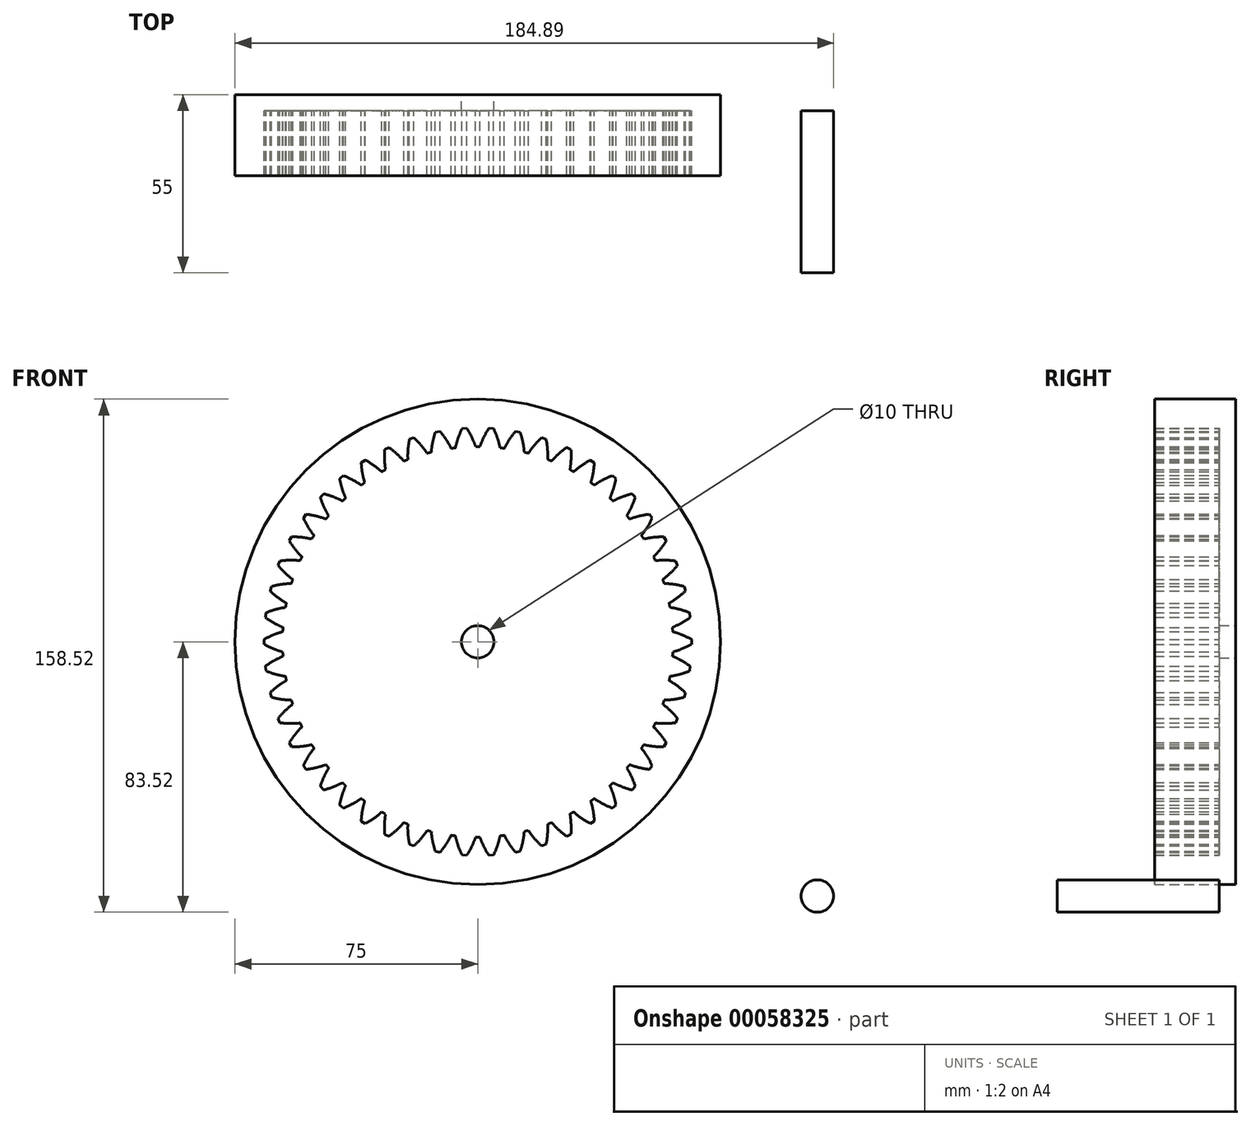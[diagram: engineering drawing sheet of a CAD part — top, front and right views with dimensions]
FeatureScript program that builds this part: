
annotation { "Feature Type Name" : "Feature", "Feature Type Description" : "" }
export const myFeature = defineFeature(function(context is Context, id is Id, definition is map)
    precondition{}
    {
        {
            var Q0;
            Q0=qCreatedBy(makeId("Front.planeOp"),FACE);
            var sketch = newSketch(context, id + "F0", { "sketchPlane" : qUnion([Q0])});
            skCircle(sketch, "E0", {"center": v(0, 0) * mm, "radius": 75 * mm});
            skSolve(sketch);
        }
        {
            var Q0;
            Q0 = qSketchRegion(id + "F0", true);
            extrude(context, id + "F1", {"entities" : qUnion([Q0]), "depth" : 20 * mm});
        }
        {
            var Q0;
            Q0=qCreatedBy(makeId("Front.planeOp"),FACE);
            var sketch = newSketch(context, id + "F2", { "sketchPlane" : qUnion([Q0])});
            skLineSegment(sketch, "E1", {"start": v(60.24, -3.11) * mm, "end": v(60.4, -3.07) * mm});
            skLineSegment(sketch, "E2", {"start": v(60.4, -3.07) * mm, "end": v(60.56, -3.03) * mm});
            skLineSegment(sketch, "E3", {"start": v(60.56, -3.03) * mm, "end": v(60.72, -2.98) * mm});
            skLineSegment(sketch, "E4", {"start": v(60.72, -2.98) * mm, "end": v(60.89, -2.94) * mm});
            skLineSegment(sketch, "E5", {"start": v(60.89, -2.94) * mm, "end": v(61.06, -2.88) * mm});
            skLineSegment(sketch, "E6", {"start": v(61.06, -2.88) * mm, "end": v(61.23, -2.83) * mm});
            skLineSegment(sketch, "E7", {"start": v(61.23, -2.83) * mm, "end": v(61.4, -2.77) * mm});
            skLineSegment(sketch, "E8", {"start": v(61.4, -2.77) * mm, "end": v(61.59, -2.71) * mm});
            skLineSegment(sketch, "E9", {"start": v(61.59, -2.71) * mm, "end": v(61.77, -2.65) * mm});
            skLineSegment(sketch, "E10", {"start": v(61.77, -2.65) * mm, "end": v(61.96, -2.59) * mm});
            skLineSegment(sketch, "E11", {"start": v(61.96, -2.59) * mm, "end": v(62.15, -2.52) * mm});
            skLineSegment(sketch, "E12", {"start": v(62.15, -2.52) * mm, "end": v(62.35, -2.44) * mm});
            skLineSegment(sketch, "E13", {"start": v(62.35, -2.44) * mm, "end": v(62.55, -2.37) * mm});
            skLineSegment(sketch, "E14", {"start": v(62.55, -2.37) * mm, "end": v(62.75, -2.3) * mm});
            skLineSegment(sketch, "E15", {"start": v(62.75, -2.3) * mm, "end": v(62.95, -2.2) * mm});
            skLineSegment(sketch, "E16", {"start": v(62.95, -2.2) * mm, "end": v(63.16, -2.12) * mm});
            skLineSegment(sketch, "E17", {"start": v(63.16, -2.12) * mm, "end": v(63.38, -2.03) * mm});
            skLineSegment(sketch, "E18", {"start": v(63.38, -2.03) * mm, "end": v(63.6, -1.94) * mm});
            skLineSegment(sketch, "E19", {"start": v(63.6, -1.94) * mm, "end": v(63.8, -1.85) * mm});
            skLineSegment(sketch, "E20", {"start": v(63.8, -1.85) * mm, "end": v(64.03, -1.75) * mm});
            skLineSegment(sketch, "E21", {"start": v(64.03, -1.75) * mm, "end": v(64.26, -1.64) * mm});
            skLineSegment(sketch, "E22", {"start": v(64.26, -1.64) * mm, "end": v(64.48, -1.54) * mm});
            skLineSegment(sketch, "E23", {"start": v(64.48, -1.54) * mm, "end": v(64.72, -1.42) * mm});
            skLineSegment(sketch, "E24", {"start": v(64.72, -1.42) * mm, "end": v(64.95, -1.3) * mm});
            skLineSegment(sketch, "E25", {"start": v(64.95, -1.3) * mm, "end": v(65.19, -1.19) * mm});
            skLineSegment(sketch, "E26", {"start": v(65.19, -1.19) * mm, "end": v(65.43, -1.07) * mm});
            skLineSegment(sketch, "E27", {"start": v(65.43, -1.07) * mm, "end": v(65.67, -0.94) * mm});
            skLineSegment(sketch, "E28", {"start": v(65.67, -0.94) * mm, "end": v(65.91, -0.8) * mm});
            skLineSegment(sketch, "E29", {"start": v(65.91, -0.8) * mm, "end": v(66.04, -0.74) * mm});
            skLineSegment(sketch, "E30", {"start": v(66.04, -0.74) * mm, "end": v(66.04, 0.74) * mm});
            skLineSegment(sketch, "E31", {"start": v(66.04, 0.74) * mm, "end": v(65.91, 0.8) * mm});
            skLineSegment(sketch, "E32", {"start": v(65.91, 0.8) * mm, "end": v(65.67, 0.94) * mm});
            skLineSegment(sketch, "E33", {"start": v(65.67, 0.94) * mm, "end": v(65.43, 1.07) * mm});
            skLineSegment(sketch, "E34", {"start": v(65.43, 1.07) * mm, "end": v(65.19, 1.19) * mm});
            skLineSegment(sketch, "E35", {"start": v(65.19, 1.19) * mm, "end": v(64.95, 1.3) * mm});
            skLineSegment(sketch, "E36", {"start": v(64.95, 1.3) * mm, "end": v(64.72, 1.42) * mm});
            skLineSegment(sketch, "E37", {"start": v(64.72, 1.42) * mm, "end": v(64.48, 1.54) * mm});
            skLineSegment(sketch, "E38", {"start": v(64.48, 1.54) * mm, "end": v(64.26, 1.64) * mm});
            skLineSegment(sketch, "E39", {"start": v(64.26, 1.64) * mm, "end": v(64.03, 1.75) * mm});
            skLineSegment(sketch, "E40", {"start": v(64.03, 1.75) * mm, "end": v(63.8, 1.85) * mm});
            skLineSegment(sketch, "E41", {"start": v(63.8, 1.85) * mm, "end": v(63.6, 1.94) * mm});
            skLineSegment(sketch, "E42", {"start": v(63.6, 1.94) * mm, "end": v(63.38, 2.03) * mm});
            skLineSegment(sketch, "E43", {"start": v(63.38, 2.03) * mm, "end": v(63.16, 2.12) * mm});
            skLineSegment(sketch, "E44", {"start": v(63.16, 2.12) * mm, "end": v(62.95, 2.2) * mm});
            skLineSegment(sketch, "E45", {"start": v(62.95, 2.2) * mm, "end": v(62.75, 2.3) * mm});
            skLineSegment(sketch, "E46", {"start": v(62.75, 2.3) * mm, "end": v(62.55, 2.37) * mm});
            skLineSegment(sketch, "E47", {"start": v(62.55, 2.37) * mm, "end": v(62.35, 2.44) * mm});
            skLineSegment(sketch, "E48", {"start": v(62.35, 2.44) * mm, "end": v(62.15, 2.52) * mm});
            skLineSegment(sketch, "E49", {"start": v(62.15, 2.52) * mm, "end": v(61.96, 2.59) * mm});
            skLineSegment(sketch, "E50", {"start": v(61.96, 2.59) * mm, "end": v(61.77, 2.65) * mm});
            skLineSegment(sketch, "E51", {"start": v(61.77, 2.65) * mm, "end": v(61.59, 2.71) * mm});
            skLineSegment(sketch, "E52", {"start": v(61.59, 2.71) * mm, "end": v(61.4, 2.77) * mm});
            skLineSegment(sketch, "E53", {"start": v(61.4, 2.77) * mm, "end": v(61.23, 2.83) * mm});
            skLineSegment(sketch, "E54", {"start": v(61.23, 2.83) * mm, "end": v(61.06, 2.88) * mm});
            skLineSegment(sketch, "E55", {"start": v(61.06, 2.88) * mm, "end": v(60.89, 2.94) * mm});
            skLineSegment(sketch, "E56", {"start": v(60.89, 2.94) * mm, "end": v(60.72, 2.98) * mm});
            skLineSegment(sketch, "E57", {"start": v(60.72, 2.98) * mm, "end": v(60.56, 3.03) * mm});
            skLineSegment(sketch, "E58", {"start": v(60.56, 3.03) * mm, "end": v(60.4, 3.07) * mm});
            skLineSegment(sketch, "E59", {"start": v(60.4, 3.07) * mm, "end": v(60.24, 3.11) * mm});
            skArc(sketch, "E60", {"start": v(60.24, 3.11) * mm, "mid": v(60.2, 3.79) * mm, "end": v(60.16, 4.46) * mm});
            skLineSegment(sketch, "E61", {"start": v(60.16, 4.46) * mm, "end": v(60.3, 4.52) * mm});
            skLineSegment(sketch, "E62", {"start": v(60.3, 4.52) * mm, "end": v(60.46, 4.58) * mm});
            skLineSegment(sketch, "E63", {"start": v(60.46, 4.58) * mm, "end": v(60.61, 4.65) * mm});
            skLineSegment(sketch, "E64", {"start": v(60.61, 4.65) * mm, "end": v(60.77, 4.72) * mm});
            skLineSegment(sketch, "E65", {"start": v(60.77, 4.72) * mm, "end": v(60.94, 4.8) * mm});
            skLineSegment(sketch, "E66", {"start": v(60.94, 4.8) * mm, "end": v(61.1, 4.87) * mm});
            skLineSegment(sketch, "E67", {"start": v(61.1, 4.87) * mm, "end": v(61.27, 4.94) * mm});
            skLineSegment(sketch, "E68", {"start": v(61.27, 4.94) * mm, "end": v(61.44, 5.03) * mm});
            skLineSegment(sketch, "E69", {"start": v(61.44, 5.03) * mm, "end": v(61.62, 5.11) * mm});
            skLineSegment(sketch, "E70", {"start": v(61.62, 5.11) * mm, "end": v(61.8, 5.2) * mm});
            skLineSegment(sketch, "E71", {"start": v(61.8, 5.2) * mm, "end": v(61.98, 5.3) * mm});
            skLineSegment(sketch, "E72", {"start": v(61.98, 5.3) * mm, "end": v(62.16, 5.39) * mm});
            skLineSegment(sketch, "E73", {"start": v(62.16, 5.39) * mm, "end": v(62.35, 5.49) * mm});
            skLineSegment(sketch, "E74", {"start": v(62.35, 5.49) * mm, "end": v(62.54, 5.6) * mm});
            skLineSegment(sketch, "E75", {"start": v(62.54, 5.6) * mm, "end": v(62.73, 5.7) * mm});
            skLineSegment(sketch, "E76", {"start": v(62.73, 5.7) * mm, "end": v(62.93, 5.8) * mm});
            skLineSegment(sketch, "E77", {"start": v(62.93, 5.8) * mm, "end": v(63.13, 5.92) * mm});
            skLineSegment(sketch, "E78", {"start": v(63.13, 5.92) * mm, "end": v(63.33, 6.04) * mm});
            skLineSegment(sketch, "E79", {"start": v(63.33, 6.04) * mm, "end": v(63.54, 6.17) * mm});
            skLineSegment(sketch, "E80", {"start": v(63.54, 6.17) * mm, "end": v(63.75, 6.3) * mm});
            skLineSegment(sketch, "E81", {"start": v(63.75, 6.3) * mm, "end": v(63.96, 6.42) * mm});
            skLineSegment(sketch, "E82", {"start": v(63.96, 6.42) * mm, "end": v(64.17, 6.56) * mm});
            skLineSegment(sketch, "E83", {"start": v(64.17, 6.56) * mm, "end": v(64.38, 6.7) * mm});
            skLineSegment(sketch, "E84", {"start": v(64.38, 6.7) * mm, "end": v(64.6, 6.84) * mm});
            skLineSegment(sketch, "E85", {"start": v(64.6, 6.84) * mm, "end": v(64.82, 7) * mm});
            skLineSegment(sketch, "E86", {"start": v(64.82, 7) * mm, "end": v(65.04, 7.14) * mm});
            skLineSegment(sketch, "E87", {"start": v(65.04, 7.14) * mm, "end": v(65.27, 7.3) * mm});
            skLineSegment(sketch, "E88", {"start": v(65.27, 7.3) * mm, "end": v(65.5, 7.46) * mm});
            skLineSegment(sketch, "E89", {"start": v(65.5, 7.46) * mm, "end": v(65.6, 7.54) * mm});
            skLineSegment(sketch, "E90", {"start": v(65.6, 7.54) * mm, "end": v(65.42, 9.01) * mm});
            skLineSegment(sketch, "E91", {"start": v(65.42, 9.01) * mm, "end": v(65.3, 9.06) * mm});
            skLineSegment(sketch, "E92", {"start": v(65.3, 9.06) * mm, "end": v(65.03, 9.16) * mm});
            skLineSegment(sketch, "E93", {"start": v(65.03, 9.16) * mm, "end": v(64.78, 9.26) * mm});
            skLineSegment(sketch, "E94", {"start": v(64.78, 9.26) * mm, "end": v(64.52, 9.35) * mm});
            skLineSegment(sketch, "E95", {"start": v(64.52, 9.35) * mm, "end": v(64.27, 9.44) * mm});
            skLineSegment(sketch, "E96", {"start": v(64.27, 9.44) * mm, "end": v(64.03, 9.52) * mm});
            skLineSegment(sketch, "E97", {"start": v(64.03, 9.52) * mm, "end": v(63.78, 9.6) * mm});
            skLineSegment(sketch, "E98", {"start": v(63.78, 9.6) * mm, "end": v(63.54, 9.68) * mm});
            skLineSegment(sketch, "E99", {"start": v(63.54, 9.68) * mm, "end": v(63.3, 9.76) * mm});
            skLineSegment(sketch, "E100", {"start": v(63.3, 9.76) * mm, "end": v(63.07, 9.83) * mm});
            skLineSegment(sketch, "E101", {"start": v(63.07, 9.83) * mm, "end": v(62.85, 9.9) * mm});
            skLineSegment(sketch, "E102", {"start": v(62.85, 9.9) * mm, "end": v(62.62, 9.96) * mm});
            skLineSegment(sketch, "E103", {"start": v(62.62, 9.96) * mm, "end": v(62.4, 10.02) * mm});
            skLineSegment(sketch, "E104", {"start": v(62.4, 10.02) * mm, "end": v(62.18, 10.08) * mm});
            skLineSegment(sketch, "E105", {"start": v(62.18, 10.08) * mm, "end": v(61.97, 10.14) * mm});
            skLineSegment(sketch, "E106", {"start": v(61.97, 10.14) * mm, "end": v(61.76, 10.19) * mm});
            skLineSegment(sketch, "E107", {"start": v(61.76, 10.19) * mm, "end": v(61.55, 10.24) * mm});
            skLineSegment(sketch, "E108", {"start": v(61.55, 10.24) * mm, "end": v(61.35, 10.29) * mm});
            skLineSegment(sketch, "E109", {"start": v(61.35, 10.29) * mm, "end": v(61.15, 10.33) * mm});
            skLineSegment(sketch, "E110", {"start": v(61.15, 10.33) * mm, "end": v(60.95, 10.37) * mm});
            skLineSegment(sketch, "E111", {"start": v(60.95, 10.37) * mm, "end": v(60.76, 10.41) * mm});
            skLineSegment(sketch, "E112", {"start": v(60.76, 10.41) * mm, "end": v(60.57, 10.45) * mm});
            skLineSegment(sketch, "E113", {"start": v(60.57, 10.45) * mm, "end": v(60.4, 10.48) * mm});
            skLineSegment(sketch, "E114", {"start": v(60.4, 10.48) * mm, "end": v(60.21, 10.51) * mm});
            skLineSegment(sketch, "E115", {"start": v(60.21, 10.51) * mm, "end": v(60.04, 10.54) * mm});
            skLineSegment(sketch, "E116", {"start": v(60.04, 10.54) * mm, "end": v(59.87, 10.57) * mm});
            skLineSegment(sketch, "E117", {"start": v(59.87, 10.57) * mm, "end": v(59.7, 10.6) * mm});
            skLineSegment(sketch, "E118", {"start": v(59.7, 10.6) * mm, "end": v(59.54, 10.62) * mm});
            skLineSegment(sketch, "E119", {"start": v(59.54, 10.62) * mm, "end": v(59.38, 10.64) * mm});
            skArc(sketch, "E120", {"start": v(59.38, 10.64) * mm, "mid": v(59.25, 11.3) * mm, "end": v(59.13, 11.97) * mm});
            skLineSegment(sketch, "E121", {"start": v(59.13, 11.97) * mm, "end": v(59.26, 12.04) * mm});
            skLineSegment(sketch, "E122", {"start": v(59.26, 12.04) * mm, "end": v(59.4, 12.13) * mm});
            skLineSegment(sketch, "E123", {"start": v(59.4, 12.13) * mm, "end": v(59.55, 12.21) * mm});
            skLineSegment(sketch, "E124", {"start": v(59.55, 12.21) * mm, "end": v(59.7, 12.3) * mm});
            skLineSegment(sketch, "E125", {"start": v(59.7, 12.3) * mm, "end": v(59.85, 12.4) * mm});
            skLineSegment(sketch, "E126", {"start": v(59.85, 12.4) * mm, "end": v(60, 12.49) * mm});
            skLineSegment(sketch, "E127", {"start": v(60, 12.49) * mm, "end": v(60.17, 12.58) * mm});
            skLineSegment(sketch, "E128", {"start": v(60.17, 12.58) * mm, "end": v(60.33, 12.69) * mm});
            skLineSegment(sketch, "E129", {"start": v(60.33, 12.69) * mm, "end": v(60.5, 12.8) * mm});
            skLineSegment(sketch, "E130", {"start": v(60.5, 12.8) * mm, "end": v(60.66, 12.9) * mm});
            skLineSegment(sketch, "E131", {"start": v(60.66, 12.9) * mm, "end": v(60.83, 13.02) * mm});
            skLineSegment(sketch, "E132", {"start": v(60.83, 13.02) * mm, "end": v(61, 13.14) * mm});
            skLineSegment(sketch, "E133", {"start": v(61, 13.14) * mm, "end": v(61.17, 13.26) * mm});
            skLineSegment(sketch, "E134", {"start": v(61.17, 13.26) * mm, "end": v(61.35, 13.39) * mm});
            skLineSegment(sketch, "E135", {"start": v(61.35, 13.39) * mm, "end": v(61.53, 13.52) * mm});
            skLineSegment(sketch, "E136", {"start": v(61.53, 13.52) * mm, "end": v(61.7, 13.65) * mm});
            skLineSegment(sketch, "E137", {"start": v(61.7, 13.65) * mm, "end": v(61.9, 13.8) * mm});
            skLineSegment(sketch, "E138", {"start": v(61.9, 13.8) * mm, "end": v(62.08, 13.93) * mm});
            skLineSegment(sketch, "E139", {"start": v(62.08, 13.93) * mm, "end": v(62.26, 14.08) * mm});
            skLineSegment(sketch, "E140", {"start": v(62.26, 14.08) * mm, "end": v(62.45, 14.23) * mm});
            skLineSegment(sketch, "E141", {"start": v(62.45, 14.23) * mm, "end": v(62.65, 14.39) * mm});
            skLineSegment(sketch, "E142", {"start": v(62.65, 14.39) * mm, "end": v(62.84, 14.55) * mm});
            skLineSegment(sketch, "E143", {"start": v(62.84, 14.55) * mm, "end": v(63.04, 14.71) * mm});
            skLineSegment(sketch, "E144", {"start": v(63.04, 14.71) * mm, "end": v(63.23, 14.88) * mm});
            skLineSegment(sketch, "E145", {"start": v(63.23, 14.88) * mm, "end": v(63.43, 15.06) * mm});
            skLineSegment(sketch, "E146", {"start": v(63.43, 15.06) * mm, "end": v(63.64, 15.24) * mm});
            skLineSegment(sketch, "E147", {"start": v(63.64, 15.24) * mm, "end": v(63.84, 15.42) * mm});
            skLineSegment(sketch, "E148", {"start": v(63.84, 15.42) * mm, "end": v(64.04, 15.61) * mm});
            skLineSegment(sketch, "E149", {"start": v(64.04, 15.61) * mm, "end": v(64.15, 15.7) * mm});
            skLineSegment(sketch, "E150", {"start": v(64.15, 15.7) * mm, "end": v(63.78, 17.14) * mm});
            skLineSegment(sketch, "E151", {"start": v(63.78, 17.14) * mm, "end": v(63.64, 17.17) * mm});
            skLineSegment(sketch, "E152", {"start": v(63.64, 17.17) * mm, "end": v(63.37, 17.24) * mm});
            skLineSegment(sketch, "E153", {"start": v(63.37, 17.24) * mm, "end": v(63.1, 17.3) * mm});
            skLineSegment(sketch, "E154", {"start": v(63.1, 17.3) * mm, "end": v(62.84, 17.36) * mm});
            skLineSegment(sketch, "E155", {"start": v(62.84, 17.36) * mm, "end": v(62.58, 17.42) * mm});
            skLineSegment(sketch, "E156", {"start": v(62.58, 17.42) * mm, "end": v(62.33, 17.47) * mm});
            skLineSegment(sketch, "E157", {"start": v(62.33, 17.47) * mm, "end": v(62.08, 17.52) * mm});
            skLineSegment(sketch, "E158", {"start": v(62.08, 17.52) * mm, "end": v(61.83, 17.57) * mm});
            skLineSegment(sketch, "E159", {"start": v(61.83, 17.57) * mm, "end": v(61.59, 17.62) * mm});
            skLineSegment(sketch, "E160", {"start": v(61.59, 17.62) * mm, "end": v(61.35, 17.66) * mm});
            skLineSegment(sketch, "E161", {"start": v(61.35, 17.66) * mm, "end": v(61.1, 17.7) * mm});
            skLineSegment(sketch, "E162", {"start": v(61.1, 17.7) * mm, "end": v(60.88, 17.73) * mm});
            skLineSegment(sketch, "E163", {"start": v(60.88, 17.73) * mm, "end": v(60.65, 17.76) * mm});
            skLineSegment(sketch, "E164", {"start": v(60.65, 17.76) * mm, "end": v(60.43, 17.8) * mm});
            skLineSegment(sketch, "E165", {"start": v(60.43, 17.8) * mm, "end": v(60.2, 17.82) * mm});
            skLineSegment(sketch, "E166", {"start": v(60.2, 17.82) * mm, "end": v(60, 17.85) * mm});
            skLineSegment(sketch, "E167", {"start": v(60, 17.85) * mm, "end": v(59.78, 17.87) * mm});
            skLineSegment(sketch, "E168", {"start": v(59.78, 17.87) * mm, "end": v(59.57, 17.9) * mm});
            skLineSegment(sketch, "E169", {"start": v(59.57, 17.9) * mm, "end": v(59.37, 17.91) * mm});
            skLineSegment(sketch, "E170", {"start": v(59.37, 17.91) * mm, "end": v(59.17, 17.93) * mm});
            skLineSegment(sketch, "E171", {"start": v(59.17, 17.93) * mm, "end": v(58.98, 17.94) * mm});
            skLineSegment(sketch, "E172", {"start": v(58.98, 17.94) * mm, "end": v(58.79, 17.96) * mm});
            skLineSegment(sketch, "E173", {"start": v(58.79, 17.96) * mm, "end": v(58.6, 17.97) * mm});
            skLineSegment(sketch, "E174", {"start": v(58.6, 17.97) * mm, "end": v(58.42, 17.98) * mm});
            skLineSegment(sketch, "E175", {"start": v(58.42, 17.98) * mm, "end": v(58.24, 17.98) * mm});
            skLineSegment(sketch, "E176", {"start": v(58.24, 17.98) * mm, "end": v(58.07, 18) * mm});
            skLineSegment(sketch, "E177", {"start": v(58.07, 18) * mm, "end": v(57.9, 18) * mm});
            skLineSegment(sketch, "E178", {"start": v(57.9, 18) * mm, "end": v(57.74, 18) * mm});
            skLineSegment(sketch, "E179", {"start": v(57.74, 18) * mm, "end": v(57.58, 18) * mm});
            skArc(sketch, "E180", {"start": v(57.58, 18) * mm, "mid": v(57.37, 18.64) * mm, "end": v(57.16, 19.28) * mm});
            skLineSegment(sketch, "E181", {"start": v(57.16, 19.28) * mm, "end": v(57.29, 19.38) * mm});
            skLineSegment(sketch, "E182", {"start": v(57.29, 19.38) * mm, "end": v(57.42, 19.48) * mm});
            skLineSegment(sketch, "E183", {"start": v(57.42, 19.48) * mm, "end": v(57.55, 19.58) * mm});
            skLineSegment(sketch, "E184", {"start": v(57.55, 19.58) * mm, "end": v(57.7, 19.68) * mm});
            skLineSegment(sketch, "E185", {"start": v(57.7, 19.68) * mm, "end": v(57.83, 19.8) * mm});
            skLineSegment(sketch, "E186", {"start": v(57.83, 19.8) * mm, "end": v(57.97, 19.9) * mm});
            skLineSegment(sketch, "E187", {"start": v(57.97, 19.9) * mm, "end": v(58.12, 20.03) * mm});
            skLineSegment(sketch, "E188", {"start": v(58.12, 20.03) * mm, "end": v(58.26, 20.15) * mm});
            skLineSegment(sketch, "E189", {"start": v(58.26, 20.15) * mm, "end": v(58.41, 20.27) * mm});
            skLineSegment(sketch, "E190", {"start": v(58.41, 20.27) * mm, "end": v(58.56, 20.4) * mm});
            skLineSegment(sketch, "E191", {"start": v(58.56, 20.4) * mm, "end": v(58.71, 20.54) * mm});
            skLineSegment(sketch, "E192", {"start": v(58.71, 20.54) * mm, "end": v(58.87, 20.68) * mm});
            skLineSegment(sketch, "E193", {"start": v(58.87, 20.68) * mm, "end": v(59.03, 20.82) * mm});
            skLineSegment(sketch, "E194", {"start": v(59.03, 20.82) * mm, "end": v(59.19, 20.97) * mm});
            skLineSegment(sketch, "E195", {"start": v(59.19, 20.97) * mm, "end": v(59.35, 21.12) * mm});
            skLineSegment(sketch, "E196", {"start": v(59.35, 21.12) * mm, "end": v(59.5, 21.28) * mm});
            skLineSegment(sketch, "E197", {"start": v(59.5, 21.28) * mm, "end": v(59.67, 21.44) * mm});
            skLineSegment(sketch, "E198", {"start": v(59.67, 21.44) * mm, "end": v(59.84, 21.6) * mm});
            skLineSegment(sketch, "E199", {"start": v(59.84, 21.6) * mm, "end": v(60, 21.77) * mm});
            skLineSegment(sketch, "E200", {"start": v(60, 21.77) * mm, "end": v(60.18, 21.95) * mm});
            skLineSegment(sketch, "E201", {"start": v(60.18, 21.95) * mm, "end": v(60.35, 22.13) * mm});
            skLineSegment(sketch, "E202", {"start": v(60.35, 22.13) * mm, "end": v(60.52, 22.31) * mm});
            skLineSegment(sketch, "E203", {"start": v(60.52, 22.31) * mm, "end": v(60.7, 22.5) * mm});
            skLineSegment(sketch, "E204", {"start": v(60.7, 22.5) * mm, "end": v(60.87, 22.7) * mm});
            skLineSegment(sketch, "E205", {"start": v(60.87, 22.7) * mm, "end": v(61.05, 22.9) * mm});
            skLineSegment(sketch, "E206", {"start": v(61.05, 22.9) * mm, "end": v(61.22, 23.1) * mm});
            skLineSegment(sketch, "E207", {"start": v(61.22, 23.1) * mm, "end": v(61.4, 23.3) * mm});
            skLineSegment(sketch, "E208", {"start": v(61.4, 23.3) * mm, "end": v(61.58, 23.51) * mm});
            skLineSegment(sketch, "E209", {"start": v(61.58, 23.51) * mm, "end": v(61.67, 23.62) * mm});
            skLineSegment(sketch, "E210", {"start": v(61.67, 23.62) * mm, "end": v(61.13, 25) * mm});
            skLineSegment(sketch, "E211", {"start": v(61.13, 25) * mm, "end": v(60.99, 25.01) * mm});
            skLineSegment(sketch, "E212", {"start": v(60.99, 25.01) * mm, "end": v(60.71, 25.05) * mm});
            skLineSegment(sketch, "E213", {"start": v(60.71, 25.05) * mm, "end": v(60.44, 25.08) * mm});
            skLineSegment(sketch, "E214", {"start": v(60.44, 25.08) * mm, "end": v(60.17, 25.1) * mm});
            skLineSegment(sketch, "E215", {"start": v(60.17, 25.1) * mm, "end": v(59.9, 25.13) * mm});
            skLineSegment(sketch, "E216", {"start": v(59.9, 25.13) * mm, "end": v(59.65, 25.15) * mm});
            skLineSegment(sketch, "E217", {"start": v(59.65, 25.15) * mm, "end": v(59.4, 25.17) * mm});
            skLineSegment(sketch, "E218", {"start": v(59.4, 25.17) * mm, "end": v(59.14, 25.18) * mm});
            skLineSegment(sketch, "E219", {"start": v(59.14, 25.18) * mm, "end": v(58.9, 25.2) * mm});
            skLineSegment(sketch, "E220", {"start": v(58.9, 25.2) * mm, "end": v(58.65, 25.2) * mm});
            skLineSegment(sketch, "E221", {"start": v(58.65, 25.2) * mm, "end": v(58.41, 25.22) * mm});
            skLineSegment(sketch, "E222", {"start": v(58.41, 25.22) * mm, "end": v(58.18, 25.22) * mm});
            skLineSegment(sketch, "E223", {"start": v(58.18, 25.22) * mm, "end": v(57.95, 25.23) * mm});
            skLineSegment(sketch, "E224", {"start": v(57.95, 25.23) * mm, "end": v(57.72, 25.23) * mm});
            skLineSegment(sketch, "E225", {"start": v(57.72, 25.23) * mm, "end": v(57.5, 25.23) * mm});
            skLineSegment(sketch, "E226", {"start": v(57.5, 25.23) * mm, "end": v(57.28, 25.23) * mm});
            skLineSegment(sketch, "E227", {"start": v(57.28, 25.23) * mm, "end": v(57.07, 25.22) * mm});
            skLineSegment(sketch, "E228", {"start": v(57.07, 25.22) * mm, "end": v(56.86, 25.22) * mm});
            skLineSegment(sketch, "E229", {"start": v(56.86, 25.22) * mm, "end": v(56.66, 25.21) * mm});
            skLineSegment(sketch, "E230", {"start": v(56.66, 25.21) * mm, "end": v(56.46, 25.2) * mm});
            skLineSegment(sketch, "E231", {"start": v(56.46, 25.2) * mm, "end": v(56.26, 25.2) * mm});
            skLineSegment(sketch, "E232", {"start": v(56.26, 25.2) * mm, "end": v(56.07, 25.18) * mm});
            skLineSegment(sketch, "E233", {"start": v(56.07, 25.18) * mm, "end": v(55.89, 25.17) * mm});
            skLineSegment(sketch, "E234", {"start": v(55.89, 25.17) * mm, "end": v(55.7, 25.16) * mm});
            skLineSegment(sketch, "E235", {"start": v(55.7, 25.16) * mm, "end": v(55.53, 25.14) * mm});
            skLineSegment(sketch, "E236", {"start": v(55.53, 25.14) * mm, "end": v(55.36, 25.13) * mm});
            skLineSegment(sketch, "E237", {"start": v(55.36, 25.13) * mm, "end": v(55.19, 25.1) * mm});
            skLineSegment(sketch, "E238", {"start": v(55.19, 25.1) * mm, "end": v(55.03, 25.1) * mm});
            skLineSegment(sketch, "E239", {"start": v(55.03, 25.1) * mm, "end": v(54.87, 25.07) * mm});
            skArc(sketch, "E240", {"start": v(54.87, 25.07) * mm, "mid": v(54.58, 25.68) * mm, "end": v(54.3, 26.3) * mm});
            skLineSegment(sketch, "E241", {"start": v(54.3, 26.3) * mm, "end": v(54.4, 26.4) * mm});
            skLineSegment(sketch, "E242", {"start": v(54.4, 26.4) * mm, "end": v(54.53, 26.52) * mm});
            skLineSegment(sketch, "E243", {"start": v(54.53, 26.52) * mm, "end": v(54.65, 26.64) * mm});
            skLineSegment(sketch, "E244", {"start": v(54.65, 26.64) * mm, "end": v(54.77, 26.76) * mm});
            skLineSegment(sketch, "E245", {"start": v(54.77, 26.76) * mm, "end": v(54.9, 26.89) * mm});
            skLineSegment(sketch, "E246", {"start": v(54.9, 26.89) * mm, "end": v(55.02, 27.02) * mm});
            skLineSegment(sketch, "E247", {"start": v(55.02, 27.02) * mm, "end": v(55.15, 27.15) * mm});
            skLineSegment(sketch, "E248", {"start": v(55.15, 27.15) * mm, "end": v(55.28, 27.3) * mm});
            skLineSegment(sketch, "E249", {"start": v(55.28, 27.3) * mm, "end": v(55.4, 27.44) * mm});
            skLineSegment(sketch, "E250", {"start": v(55.4, 27.44) * mm, "end": v(55.54, 27.58) * mm});
            skLineSegment(sketch, "E251", {"start": v(55.54, 27.58) * mm, "end": v(55.68, 27.74) * mm});
            skLineSegment(sketch, "E252", {"start": v(55.68, 27.74) * mm, "end": v(55.81, 27.9) * mm});
            skLineSegment(sketch, "E253", {"start": v(55.81, 27.9) * mm, "end": v(55.95, 28.06) * mm});
            skLineSegment(sketch, "E254", {"start": v(55.95, 28.06) * mm, "end": v(56.1, 28.22) * mm});
            skLineSegment(sketch, "E255", {"start": v(56.1, 28.22) * mm, "end": v(56.23, 28.4) * mm});
            skLineSegment(sketch, "E256", {"start": v(56.23, 28.4) * mm, "end": v(56.37, 28.57) * mm});
            skLineSegment(sketch, "E257", {"start": v(56.37, 28.57) * mm, "end": v(56.52, 28.75) * mm});
            skLineSegment(sketch, "E258", {"start": v(56.52, 28.75) * mm, "end": v(56.66, 28.93) * mm});
            skLineSegment(sketch, "E259", {"start": v(56.66, 28.93) * mm, "end": v(56.8, 29.12) * mm});
            skLineSegment(sketch, "E260", {"start": v(56.8, 29.12) * mm, "end": v(56.95, 29.32) * mm});
            skLineSegment(sketch, "E261", {"start": v(56.95, 29.32) * mm, "end": v(57.1, 29.52) * mm});
            skLineSegment(sketch, "E262", {"start": v(57.1, 29.52) * mm, "end": v(57.25, 29.72) * mm});
            skLineSegment(sketch, "E263", {"start": v(57.25, 29.72) * mm, "end": v(57.4, 29.93) * mm});
            skLineSegment(sketch, "E264", {"start": v(57.4, 29.93) * mm, "end": v(57.55, 30.14) * mm});
            skLineSegment(sketch, "E265", {"start": v(57.55, 30.14) * mm, "end": v(57.7, 30.36) * mm});
            skLineSegment(sketch, "E266", {"start": v(57.7, 30.36) * mm, "end": v(57.85, 30.58) * mm});
            skLineSegment(sketch, "E267", {"start": v(57.85, 30.58) * mm, "end": v(58, 30.81) * mm});
            skLineSegment(sketch, "E268", {"start": v(58, 30.81) * mm, "end": v(58.15, 31.05) * mm});
            skLineSegment(sketch, "E269", {"start": v(58.15, 31.05) * mm, "end": v(58.22, 31.16) * mm});
            skLineSegment(sketch, "E270", {"start": v(58.22, 31.16) * mm, "end": v(57.51, 32.46) * mm});
            skLineSegment(sketch, "E271", {"start": v(57.51, 32.46) * mm, "end": v(57.37, 32.46) * mm});
            skLineSegment(sketch, "E272", {"start": v(57.37, 32.46) * mm, "end": v(57.1, 32.46) * mm});
            skLineSegment(sketch, "E273", {"start": v(57.1, 32.46) * mm, "end": v(56.82, 32.45) * mm});
            skLineSegment(sketch, "E274", {"start": v(56.82, 32.45) * mm, "end": v(56.55, 32.45) * mm});
            skLineSegment(sketch, "E275", {"start": v(56.55, 32.45) * mm, "end": v(56.28, 32.44) * mm});
            skLineSegment(sketch, "E276", {"start": v(56.28, 32.44) * mm, "end": v(56.02, 32.42) * mm});
            skLineSegment(sketch, "E277", {"start": v(56.02, 32.42) * mm, "end": v(55.77, 32.41) * mm});
            skLineSegment(sketch, "E278", {"start": v(55.77, 32.41) * mm, "end": v(55.52, 32.4) * mm});
            skLineSegment(sketch, "E279", {"start": v(55.52, 32.4) * mm, "end": v(55.27, 32.38) * mm});
            skLineSegment(sketch, "E280", {"start": v(55.27, 32.38) * mm, "end": v(55.03, 32.36) * mm});
            skLineSegment(sketch, "E281", {"start": v(55.03, 32.36) * mm, "end": v(54.79, 32.34) * mm});
            skLineSegment(sketch, "E282", {"start": v(54.79, 32.34) * mm, "end": v(54.56, 32.31) * mm});
            skLineSegment(sketch, "E283", {"start": v(54.56, 32.31) * mm, "end": v(54.33, 32.29) * mm});
            skLineSegment(sketch, "E284", {"start": v(54.33, 32.29) * mm, "end": v(54.1, 32.26) * mm});
            skLineSegment(sketch, "E285", {"start": v(54.1, 32.26) * mm, "end": v(53.88, 32.24) * mm});
            skLineSegment(sketch, "E286", {"start": v(53.88, 32.24) * mm, "end": v(53.67, 32.2) * mm});
            skLineSegment(sketch, "E287", {"start": v(53.67, 32.2) * mm, "end": v(53.46, 32.18) * mm});
            skLineSegment(sketch, "E288", {"start": v(53.46, 32.18) * mm, "end": v(53.25, 32.15) * mm});
            skLineSegment(sketch, "E289", {"start": v(53.25, 32.15) * mm, "end": v(53.05, 32.12) * mm});
            skLineSegment(sketch, "E290", {"start": v(53.05, 32.12) * mm, "end": v(52.85, 32.08) * mm});
            skLineSegment(sketch, "E291", {"start": v(52.85, 32.08) * mm, "end": v(52.66, 32.05) * mm});
            skLineSegment(sketch, "E292", {"start": v(52.66, 32.05) * mm, "end": v(52.47, 32.01) * mm});
            skLineSegment(sketch, "E293", {"start": v(52.47, 32.01) * mm, "end": v(52.3, 31.98) * mm});
            skLineSegment(sketch, "E294", {"start": v(52.3, 31.98) * mm, "end": v(52.11, 31.94) * mm});
            skLineSegment(sketch, "E295", {"start": v(52.11, 31.94) * mm, "end": v(51.94, 31.9) * mm});
            skLineSegment(sketch, "E296", {"start": v(51.94, 31.9) * mm, "end": v(51.77, 31.87) * mm});
            skLineSegment(sketch, "E297", {"start": v(51.77, 31.87) * mm, "end": v(51.6, 31.83) * mm});
            skLineSegment(sketch, "E298", {"start": v(51.6, 31.83) * mm, "end": v(51.45, 31.79) * mm});
            skLineSegment(sketch, "E299", {"start": v(51.45, 31.79) * mm, "end": v(51.3, 31.75) * mm});
            skArc(sketch, "E300", {"start": v(51.3, 31.75) * mm, "mid": v(50.93, 32.32) * mm, "end": v(50.57, 32.9) * mm});
            skLineSegment(sketch, "E301", {"start": v(50.57, 32.9) * mm, "end": v(50.67, 33.02) * mm});
            skLineSegment(sketch, "E302", {"start": v(50.67, 33.02) * mm, "end": v(50.77, 33.14) * mm});
            skLineSegment(sketch, "E303", {"start": v(50.77, 33.14) * mm, "end": v(50.88, 33.28) * mm});
            skLineSegment(sketch, "E304", {"start": v(50.88, 33.28) * mm, "end": v(50.98, 33.41) * mm});
            skLineSegment(sketch, "E305", {"start": v(50.98, 33.41) * mm, "end": v(51.09, 33.55) * mm});
            skLineSegment(sketch, "E306", {"start": v(51.09, 33.55) * mm, "end": v(51.2, 33.7) * mm});
            skLineSegment(sketch, "E307", {"start": v(51.2, 33.7) * mm, "end": v(51.3, 33.85) * mm});
            skLineSegment(sketch, "E308", {"start": v(51.3, 33.85) * mm, "end": v(51.42, 34) * mm});
            skLineSegment(sketch, "E309", {"start": v(51.42, 34) * mm, "end": v(51.53, 34.16) * mm});
            skLineSegment(sketch, "E310", {"start": v(51.53, 34.16) * mm, "end": v(51.65, 34.33) * mm});
            skLineSegment(sketch, "E311", {"start": v(51.65, 34.33) * mm, "end": v(51.76, 34.5) * mm});
            skLineSegment(sketch, "E312", {"start": v(51.76, 34.5) * mm, "end": v(51.88, 34.67) * mm});
            skLineSegment(sketch, "E313", {"start": v(51.88, 34.67) * mm, "end": v(52, 34.85) * mm});
            skLineSegment(sketch, "E314", {"start": v(52, 34.85) * mm, "end": v(52.11, 35.03) * mm});
            skLineSegment(sketch, "E315", {"start": v(52.11, 35.03) * mm, "end": v(52.23, 35.22) * mm});
            skLineSegment(sketch, "E316", {"start": v(52.23, 35.22) * mm, "end": v(52.35, 35.4) * mm});
            skLineSegment(sketch, "E317", {"start": v(52.35, 35.4) * mm, "end": v(52.47, 35.6) * mm});
            skLineSegment(sketch, "E318", {"start": v(52.47, 35.6) * mm, "end": v(52.59, 35.8) * mm});
            skLineSegment(sketch, "E319", {"start": v(52.59, 35.8) * mm, "end": v(52.7, 36.01) * mm});
            skLineSegment(sketch, "E320", {"start": v(52.7, 36.01) * mm, "end": v(52.83, 36.22) * mm});
            skLineSegment(sketch, "E321", {"start": v(52.83, 36.22) * mm, "end": v(52.95, 36.44) * mm});
            skLineSegment(sketch, "E322", {"start": v(52.95, 36.44) * mm, "end": v(53.07, 36.66) * mm});
            skLineSegment(sketch, "E323", {"start": v(53.07, 36.66) * mm, "end": v(53.2, 36.89) * mm});
            skLineSegment(sketch, "E324", {"start": v(53.2, 36.89) * mm, "end": v(53.31, 37.12) * mm});
            skLineSegment(sketch, "E325", {"start": v(53.31, 37.12) * mm, "end": v(53.44, 37.35) * mm});
            skLineSegment(sketch, "E326", {"start": v(53.44, 37.35) * mm, "end": v(53.56, 37.6) * mm});
            skLineSegment(sketch, "E327", {"start": v(53.56, 37.6) * mm, "end": v(53.68, 37.84) * mm});
            skLineSegment(sketch, "E328", {"start": v(53.68, 37.84) * mm, "end": v(53.8, 38.1) * mm});
            skLineSegment(sketch, "E329", {"start": v(53.8, 38.1) * mm, "end": v(53.86, 38.22) * mm});
            skLineSegment(sketch, "E330", {"start": v(53.86, 38.22) * mm, "end": v(52.99, 39.41) * mm});
            skLineSegment(sketch, "E331", {"start": v(52.99, 39.41) * mm, "end": v(52.85, 39.4) * mm});
            skLineSegment(sketch, "E332", {"start": v(52.85, 39.4) * mm, "end": v(52.57, 39.36) * mm});
            skLineSegment(sketch, "E333", {"start": v(52.57, 39.36) * mm, "end": v(52.3, 39.32) * mm});
            skLineSegment(sketch, "E334", {"start": v(52.3, 39.32) * mm, "end": v(52.04, 39.28) * mm});
            skLineSegment(sketch, "E335", {"start": v(52.04, 39.28) * mm, "end": v(51.78, 39.23) * mm});
            skLineSegment(sketch, "E336", {"start": v(51.78, 39.23) * mm, "end": v(51.52, 39.2) * mm});
            skLineSegment(sketch, "E337", {"start": v(51.52, 39.2) * mm, "end": v(51.27, 39.14) * mm});
            skLineSegment(sketch, "E338", {"start": v(51.27, 39.14) * mm, "end": v(51.02, 39.1) * mm});
            skLineSegment(sketch, "E339", {"start": v(51.02, 39.1) * mm, "end": v(50.78, 39.05) * mm});
            skLineSegment(sketch, "E340", {"start": v(50.78, 39.05) * mm, "end": v(50.54, 39) * mm});
            skLineSegment(sketch, "E341", {"start": v(50.54, 39) * mm, "end": v(50.3, 38.95) * mm});
            skLineSegment(sketch, "E342", {"start": v(50.3, 38.95) * mm, "end": v(50.08, 38.9) * mm});
            skLineSegment(sketch, "E343", {"start": v(50.08, 38.9) * mm, "end": v(49.85, 38.84) * mm});
            skLineSegment(sketch, "E344", {"start": v(49.85, 38.84) * mm, "end": v(49.63, 38.8) * mm});
            skLineSegment(sketch, "E345", {"start": v(49.63, 38.8) * mm, "end": v(49.42, 38.74) * mm});
            skLineSegment(sketch, "E346", {"start": v(49.42, 38.74) * mm, "end": v(49.2, 38.68) * mm});
            skLineSegment(sketch, "E347", {"start": v(49.2, 38.68) * mm, "end": v(49, 38.62) * mm});
            skLineSegment(sketch, "E348", {"start": v(49, 38.62) * mm, "end": v(48.8, 38.57) * mm});
            skLineSegment(sketch, "E349", {"start": v(48.8, 38.57) * mm, "end": v(48.6, 38.51) * mm});
            skLineSegment(sketch, "E350", {"start": v(48.6, 38.51) * mm, "end": v(48.42, 38.45) * mm});
            skLineSegment(sketch, "E351", {"start": v(48.42, 38.45) * mm, "end": v(48.23, 38.4) * mm});
            skLineSegment(sketch, "E352", {"start": v(48.23, 38.4) * mm, "end": v(48.05, 38.34) * mm});
            skLineSegment(sketch, "E353", {"start": v(48.05, 38.34) * mm, "end": v(47.87, 38.28) * mm});
            skLineSegment(sketch, "E354", {"start": v(47.87, 38.28) * mm, "end": v(47.7, 38.22) * mm});
            skLineSegment(sketch, "E355", {"start": v(47.7, 38.22) * mm, "end": v(47.53, 38.16) * mm});
            skLineSegment(sketch, "E356", {"start": v(47.53, 38.16) * mm, "end": v(47.37, 38.1) * mm});
            skLineSegment(sketch, "E357", {"start": v(47.37, 38.1) * mm, "end": v(47.21, 38.05) * mm});
            skLineSegment(sketch, "E358", {"start": v(47.21, 38.05) * mm, "end": v(47.06, 37.99) * mm});
            skLineSegment(sketch, "E359", {"start": v(47.06, 37.99) * mm, "end": v(46.9, 37.93) * mm});
            skArc(sketch, "E360", {"start": v(46.9, 37.93) * mm, "mid": v(46.48, 38.45) * mm, "end": v(46.05, 38.97) * mm});
            skLineSegment(sketch, "E361", {"start": v(46.05, 38.97) * mm, "end": v(46.13, 39.1) * mm});
            skLineSegment(sketch, "E362", {"start": v(46.13, 39.1) * mm, "end": v(46.22, 39.25) * mm});
            skLineSegment(sketch, "E363", {"start": v(46.22, 39.25) * mm, "end": v(46.3, 39.4) * mm});
            skLineSegment(sketch, "E364", {"start": v(46.3, 39.4) * mm, "end": v(46.4, 39.54) * mm});
            skLineSegment(sketch, "E365", {"start": v(46.4, 39.54) * mm, "end": v(46.48, 39.7) * mm});
            skLineSegment(sketch, "E366", {"start": v(46.48, 39.7) * mm, "end": v(46.57, 39.85) * mm});
            skLineSegment(sketch, "E367", {"start": v(46.57, 39.85) * mm, "end": v(46.66, 40.01) * mm});
            skLineSegment(sketch, "E368", {"start": v(46.66, 40.01) * mm, "end": v(46.75, 40.18) * mm});
            skLineSegment(sketch, "E369", {"start": v(46.75, 40.18) * mm, "end": v(46.84, 40.35) * mm});
            skLineSegment(sketch, "E370", {"start": v(46.84, 40.35) * mm, "end": v(46.94, 40.53) * mm});
            skLineSegment(sketch, "E371", {"start": v(46.94, 40.53) * mm, "end": v(47.03, 40.71) * mm});
            skLineSegment(sketch, "E372", {"start": v(47.03, 40.71) * mm, "end": v(47.12, 40.9) * mm});
            skLineSegment(sketch, "E373", {"start": v(47.12, 40.9) * mm, "end": v(47.22, 41.09) * mm});
            skLineSegment(sketch, "E374", {"start": v(47.22, 41.09) * mm, "end": v(47.3, 41.28) * mm});
            skLineSegment(sketch, "E375", {"start": v(47.3, 41.28) * mm, "end": v(47.4, 41.48) * mm});
            skLineSegment(sketch, "E376", {"start": v(47.4, 41.48) * mm, "end": v(47.5, 41.7) * mm});
            skLineSegment(sketch, "E377", {"start": v(47.5, 41.7) * mm, "end": v(47.6, 41.9) * mm});
            skLineSegment(sketch, "E378", {"start": v(47.6, 41.9) * mm, "end": v(47.69, 42.12) * mm});
            skLineSegment(sketch, "E379", {"start": v(47.69, 42.12) * mm, "end": v(47.78, 42.33) * mm});
            skLineSegment(sketch, "E380", {"start": v(47.78, 42.33) * mm, "end": v(47.87, 42.56) * mm});
            skLineSegment(sketch, "E381", {"start": v(47.87, 42.56) * mm, "end": v(47.97, 42.79) * mm});
            skLineSegment(sketch, "E382", {"start": v(47.97, 42.79) * mm, "end": v(48.06, 43.02) * mm});
            skLineSegment(sketch, "E383", {"start": v(48.06, 43.02) * mm, "end": v(48.15, 43.26) * mm});
            skLineSegment(sketch, "E384", {"start": v(48.15, 43.26) * mm, "end": v(48.24, 43.5) * mm});
            skLineSegment(sketch, "E385", {"start": v(48.24, 43.5) * mm, "end": v(48.33, 43.76) * mm});
            skLineSegment(sketch, "E386", {"start": v(48.33, 43.76) * mm, "end": v(48.42, 44) * mm});
            skLineSegment(sketch, "E387", {"start": v(48.42, 44) * mm, "end": v(48.51, 44.27) * mm});
            skLineSegment(sketch, "E388", {"start": v(48.51, 44.27) * mm, "end": v(48.6, 44.53) * mm});
            skLineSegment(sketch, "E389", {"start": v(48.6, 44.53) * mm, "end": v(48.64, 44.67) * mm});
            skLineSegment(sketch, "E390", {"start": v(48.64, 44.67) * mm, "end": v(47.63, 45.74) * mm});
            skLineSegment(sketch, "E391", {"start": v(47.63, 45.74) * mm, "end": v(47.5, 45.7) * mm});
            skLineSegment(sketch, "E392", {"start": v(47.5, 45.7) * mm, "end": v(47.23, 45.64) * mm});
            skLineSegment(sketch, "E393", {"start": v(47.23, 45.64) * mm, "end": v(46.96, 45.56) * mm});
            skLineSegment(sketch, "E394", {"start": v(46.96, 45.56) * mm, "end": v(46.7, 45.49) * mm});
            skLineSegment(sketch, "E395", {"start": v(46.7, 45.49) * mm, "end": v(46.45, 45.41) * mm});
            skLineSegment(sketch, "E396", {"start": v(46.45, 45.41) * mm, "end": v(46.2, 45.34) * mm});
            skLineSegment(sketch, "E397", {"start": v(46.2, 45.34) * mm, "end": v(45.96, 45.26) * mm});
            skLineSegment(sketch, "E398", {"start": v(45.96, 45.26) * mm, "end": v(45.72, 45.18) * mm});
            skLineSegment(sketch, "E399", {"start": v(45.72, 45.18) * mm, "end": v(45.48, 45.1) * mm});
            skLineSegment(sketch, "E400", {"start": v(45.48, 45.1) * mm, "end": v(45.25, 45.03) * mm});
            skLineSegment(sketch, "E401", {"start": v(45.25, 45.03) * mm, "end": v(45.03, 44.95) * mm});
            skLineSegment(sketch, "E402", {"start": v(45.03, 44.95) * mm, "end": v(44.8, 44.87) * mm});
            skLineSegment(sketch, "E403", {"start": v(44.8, 44.87) * mm, "end": v(44.6, 44.79) * mm});
            skLineSegment(sketch, "E404", {"start": v(44.6, 44.79) * mm, "end": v(44.38, 44.7) * mm});
            skLineSegment(sketch, "E405", {"start": v(44.38, 44.7) * mm, "end": v(44.17, 44.62) * mm});
            skLineSegment(sketch, "E406", {"start": v(44.17, 44.62) * mm, "end": v(43.97, 44.54) * mm});
            skLineSegment(sketch, "E407", {"start": v(43.97, 44.54) * mm, "end": v(43.78, 44.46) * mm});
            skLineSegment(sketch, "E408", {"start": v(43.78, 44.46) * mm, "end": v(43.58, 44.38) * mm});
            skLineSegment(sketch, "E409", {"start": v(43.58, 44.38) * mm, "end": v(43.4, 44.3) * mm});
            skLineSegment(sketch, "E410", {"start": v(43.4, 44.3) * mm, "end": v(43.22, 44.22) * mm});
            skLineSegment(sketch, "E411", {"start": v(43.22, 44.22) * mm, "end": v(43.04, 44.14) * mm});
            skLineSegment(sketch, "E412", {"start": v(43.04, 44.14) * mm, "end": v(42.86, 44.06) * mm});
            skLineSegment(sketch, "E413", {"start": v(42.86, 44.06) * mm, "end": v(42.7, 43.98) * mm});
            skLineSegment(sketch, "E414", {"start": v(42.7, 43.98) * mm, "end": v(42.53, 43.9) * mm});
            skLineSegment(sketch, "E415", {"start": v(42.53, 43.9) * mm, "end": v(42.37, 43.82) * mm});
            skLineSegment(sketch, "E416", {"start": v(42.37, 43.82) * mm, "end": v(42.22, 43.74) * mm});
            skLineSegment(sketch, "E417", {"start": v(42.22, 43.74) * mm, "end": v(42.07, 43.66) * mm});
            skLineSegment(sketch, "E418", {"start": v(42.07, 43.66) * mm, "end": v(41.92, 43.59) * mm});
            skLineSegment(sketch, "E419", {"start": v(41.92, 43.59) * mm, "end": v(41.79, 43.5) * mm});
            skArc(sketch, "E420", {"start": v(41.79, 43.5) * mm, "mid": v(41.3, 43.97) * mm, "end": v(40.8, 44.44) * mm});
            skLineSegment(sketch, "E421", {"start": v(40.8, 44.43) * mm, "end": v(40.87, 44.58) * mm});
            skLineSegment(sketch, "E422", {"start": v(40.87, 44.58) * mm, "end": v(40.93, 44.73) * mm});
            skLineSegment(sketch, "E423", {"start": v(40.93, 44.73) * mm, "end": v(41, 44.88) * mm});
            skLineSegment(sketch, "E424", {"start": v(41, 44.88) * mm, "end": v(41.07, 45.04) * mm});
            skLineSegment(sketch, "E425", {"start": v(41.07, 45.04) * mm, "end": v(41.14, 45.2) * mm});
            skLineSegment(sketch, "E426", {"start": v(41.14, 45.2) * mm, "end": v(41.2, 45.37) * mm});
            skLineSegment(sketch, "E427", {"start": v(41.2, 45.37) * mm, "end": v(41.28, 45.55) * mm});
            skLineSegment(sketch, "E428", {"start": v(41.28, 45.55) * mm, "end": v(41.35, 45.72) * mm});
            skLineSegment(sketch, "E429", {"start": v(41.35, 45.72) * mm, "end": v(41.42, 45.9) * mm});
            skLineSegment(sketch, "E430", {"start": v(41.42, 45.9) * mm, "end": v(41.49, 46.1) * mm});
            skLineSegment(sketch, "E431", {"start": v(41.49, 46.1) * mm, "end": v(41.56, 46.28) * mm});
            skLineSegment(sketch, "E432", {"start": v(41.56, 46.28) * mm, "end": v(41.63, 46.48) * mm});
            skLineSegment(sketch, "E433", {"start": v(41.63, 46.48) * mm, "end": v(41.7, 46.68) * mm});
            skLineSegment(sketch, "E434", {"start": v(41.7, 46.68) * mm, "end": v(41.76, 46.89) * mm});
            skLineSegment(sketch, "E435", {"start": v(41.76, 46.89) * mm, "end": v(41.83, 47.1) * mm});
            skLineSegment(sketch, "E436", {"start": v(41.83, 47.1) * mm, "end": v(41.9, 47.31) * mm});
            skLineSegment(sketch, "E437", {"start": v(41.9, 47.31) * mm, "end": v(41.96, 47.53) * mm});
            skLineSegment(sketch, "E438", {"start": v(41.96, 47.53) * mm, "end": v(42.03, 47.76) * mm});
            skLineSegment(sketch, "E439", {"start": v(42.03, 47.76) * mm, "end": v(42.1, 47.99) * mm});
            skLineSegment(sketch, "E440", {"start": v(42.1, 47.99) * mm, "end": v(42.16, 48.22) * mm});
            skLineSegment(sketch, "E441", {"start": v(42.16, 48.22) * mm, "end": v(42.22, 48.46) * mm});
            skLineSegment(sketch, "E442", {"start": v(42.22, 48.46) * mm, "end": v(42.29, 48.7) * mm});
            skLineSegment(sketch, "E443", {"start": v(42.29, 48.7) * mm, "end": v(42.35, 48.96) * mm});
            skLineSegment(sketch, "E444", {"start": v(42.35, 48.96) * mm, "end": v(42.4, 49.2) * mm});
            skLineSegment(sketch, "E445", {"start": v(42.4, 49.2) * mm, "end": v(42.47, 49.47) * mm});
            skLineSegment(sketch, "E446", {"start": v(42.47, 49.47) * mm, "end": v(42.53, 49.73) * mm});
            skLineSegment(sketch, "E447", {"start": v(42.53, 49.73) * mm, "end": v(42.58, 50) * mm});
            skLineSegment(sketch, "E448", {"start": v(42.58, 50) * mm, "end": v(42.64, 50.27) * mm});
            skLineSegment(sketch, "E449", {"start": v(42.64, 50.27) * mm, "end": v(42.66, 50.41) * mm});
            skLineSegment(sketch, "E450", {"start": v(42.66, 50.41) * mm, "end": v(41.52, 51.35) * mm});
            skLineSegment(sketch, "E451", {"start": v(41.52, 51.35) * mm, "end": v(41.4, 51.3) * mm});
            skLineSegment(sketch, "E452", {"start": v(41.4, 51.3) * mm, "end": v(41.14, 51.2) * mm});
            skLineSegment(sketch, "E453", {"start": v(41.14, 51.2) * mm, "end": v(40.88, 51.1) * mm});
            skLineSegment(sketch, "E454", {"start": v(40.88, 51.1) * mm, "end": v(40.63, 50.98) * mm});
            skLineSegment(sketch, "E455", {"start": v(40.63, 50.98) * mm, "end": v(40.4, 50.88) * mm});
            skLineSegment(sketch, "E456", {"start": v(40.4, 50.88) * mm, "end": v(40.15, 50.77) * mm});
            skLineSegment(sketch, "E457", {"start": v(40.15, 50.77) * mm, "end": v(39.92, 50.66) * mm});
            skLineSegment(sketch, "E458", {"start": v(39.92, 50.66) * mm, "end": v(39.7, 50.56) * mm});
            skLineSegment(sketch, "E459", {"start": v(39.7, 50.56) * mm, "end": v(39.47, 50.45) * mm});
            skLineSegment(sketch, "E460", {"start": v(39.47, 50.45) * mm, "end": v(39.25, 50.34) * mm});
            skLineSegment(sketch, "E461", {"start": v(39.25, 50.34) * mm, "end": v(39.04, 50.24) * mm});
            skLineSegment(sketch, "E462", {"start": v(39.04, 50.24) * mm, "end": v(38.83, 50.13) * mm});
            skLineSegment(sketch, "E463", {"start": v(38.83, 50.13) * mm, "end": v(38.63, 50.02) * mm});
            skLineSegment(sketch, "E464", {"start": v(38.63, 50.02) * mm, "end": v(38.43, 49.92) * mm});
            skLineSegment(sketch, "E465", {"start": v(38.43, 49.92) * mm, "end": v(38.23, 49.8) * mm});
            skLineSegment(sketch, "E466", {"start": v(38.23, 49.8) * mm, "end": v(38.04, 49.7) * mm});
            skLineSegment(sketch, "E467", {"start": v(38.04, 49.7) * mm, "end": v(37.86, 49.6) * mm});
            skLineSegment(sketch, "E468", {"start": v(37.86, 49.6) * mm, "end": v(37.68, 49.5) * mm});
            skLineSegment(sketch, "E469", {"start": v(37.68, 49.5) * mm, "end": v(37.5, 49.39) * mm});
            skLineSegment(sketch, "E470", {"start": v(37.5, 49.39) * mm, "end": v(37.33, 49.29) * mm});
            skLineSegment(sketch, "E471", {"start": v(37.33, 49.29) * mm, "end": v(37.17, 49.18) * mm});
            skLineSegment(sketch, "E472", {"start": v(37.17, 49.18) * mm, "end": v(37, 49.08) * mm});
            skLineSegment(sketch, "E473", {"start": v(37, 49.08) * mm, "end": v(36.85, 48.98) * mm});
            skLineSegment(sketch, "E474", {"start": v(36.85, 48.98) * mm, "end": v(36.7, 48.88) * mm});
            skLineSegment(sketch, "E475", {"start": v(36.7, 48.88) * mm, "end": v(36.55, 48.78) * mm});
            skLineSegment(sketch, "E476", {"start": v(36.55, 48.78) * mm, "end": v(36.4, 48.69) * mm});
            skLineSegment(sketch, "E477", {"start": v(36.4, 48.69) * mm, "end": v(36.27, 48.6) * mm});
            skLineSegment(sketch, "E478", {"start": v(36.27, 48.6) * mm, "end": v(36.13, 48.5) * mm});
            skLineSegment(sketch, "E479", {"start": v(36.13, 48.5) * mm, "end": v(36, 48.4) * mm});
            skArc(sketch, "E480", {"start": v(36, 48.4) * mm, "mid": v(35.46, 48.8) * mm, "end": v(34.9, 49.2) * mm});
            skLineSegment(sketch, "E481", {"start": v(34.9, 49.2) * mm, "end": v(34.96, 49.35) * mm});
            skLineSegment(sketch, "E482", {"start": v(34.96, 49.35) * mm, "end": v(35, 49.5) * mm});
            skLineSegment(sketch, "E483", {"start": v(35, 49.5) * mm, "end": v(35.05, 49.67) * mm});
            skLineSegment(sketch, "E484", {"start": v(35.05, 49.67) * mm, "end": v(35.1, 49.83) * mm});
            skLineSegment(sketch, "E485", {"start": v(35.1, 49.83) * mm, "end": v(35.15, 50) * mm});
            skLineSegment(sketch, "E486", {"start": v(35.15, 50) * mm, "end": v(35.2, 50.18) * mm});
            skLineSegment(sketch, "E487", {"start": v(35.2, 50.18) * mm, "end": v(35.24, 50.36) * mm});
            skLineSegment(sketch, "E488", {"start": v(35.24, 50.36) * mm, "end": v(35.3, 50.55) * mm});
            skLineSegment(sketch, "E489", {"start": v(35.3, 50.55) * mm, "end": v(35.34, 50.74) * mm});
            skLineSegment(sketch, "E490", {"start": v(35.34, 50.74) * mm, "end": v(35.38, 50.93) * mm});
            skLineSegment(sketch, "E491", {"start": v(35.38, 50.93) * mm, "end": v(35.43, 51.13) * mm});
            skLineSegment(sketch, "E492", {"start": v(35.43, 51.13) * mm, "end": v(35.47, 51.33) * mm});
            skLineSegment(sketch, "E493", {"start": v(35.47, 51.33) * mm, "end": v(35.51, 51.54) * mm});
            skLineSegment(sketch, "E494", {"start": v(35.51, 51.54) * mm, "end": v(35.56, 51.75) * mm});
            skLineSegment(sketch, "E495", {"start": v(35.56, 51.75) * mm, "end": v(35.6, 51.97) * mm});
            skLineSegment(sketch, "E496", {"start": v(35.6, 51.97) * mm, "end": v(35.64, 52.2) * mm});
            skLineSegment(sketch, "E497", {"start": v(35.64, 52.2) * mm, "end": v(35.68, 52.42) * mm});
            skLineSegment(sketch, "E498", {"start": v(35.68, 52.42) * mm, "end": v(35.71, 52.65) * mm});
            skLineSegment(sketch, "E499", {"start": v(35.71, 52.65) * mm, "end": v(35.75, 52.89) * mm});
            skLineSegment(sketch, "E500", {"start": v(35.75, 52.89) * mm, "end": v(35.78, 53.13) * mm});
            skLineSegment(sketch, "E501", {"start": v(35.78, 53.13) * mm, "end": v(35.82, 53.37) * mm});
            skLineSegment(sketch, "E502", {"start": v(35.82, 53.37) * mm, "end": v(35.85, 53.62) * mm});
            skLineSegment(sketch, "E503", {"start": v(35.85, 53.62) * mm, "end": v(35.88, 53.88) * mm});
            skLineSegment(sketch, "E504", {"start": v(35.88, 53.88) * mm, "end": v(35.9, 54.14) * mm});
            skLineSegment(sketch, "E505", {"start": v(35.9, 54.14) * mm, "end": v(35.93, 54.4) * mm});
            skLineSegment(sketch, "E506", {"start": v(35.93, 54.4) * mm, "end": v(35.96, 54.67) * mm});
            skLineSegment(sketch, "E507", {"start": v(35.96, 54.67) * mm, "end": v(35.98, 54.94) * mm});
            skLineSegment(sketch, "E508", {"start": v(35.98, 54.94) * mm, "end": v(36, 55.22) * mm});
            skLineSegment(sketch, "E509", {"start": v(36, 55.22) * mm, "end": v(36, 55.36) * mm});
            skLineSegment(sketch, "E510", {"start": v(36, 55.36) * mm, "end": v(34.76, 56.15) * mm});
            skLineSegment(sketch, "E511", {"start": v(34.76, 56.15) * mm, "end": v(34.64, 56.08) * mm});
            skLineSegment(sketch, "E512", {"start": v(34.64, 56.08) * mm, "end": v(34.4, 55.95) * mm});
            skLineSegment(sketch, "E513", {"start": v(34.4, 55.95) * mm, "end": v(34.16, 55.81) * mm});
            skLineSegment(sketch, "E514", {"start": v(34.16, 55.81) * mm, "end": v(33.92, 55.68) * mm});
            skLineSegment(sketch, "E515", {"start": v(33.92, 55.68) * mm, "end": v(33.7, 55.54) * mm});
            skLineSegment(sketch, "E516", {"start": v(33.7, 55.54) * mm, "end": v(33.47, 55.4) * mm});
            skLineSegment(sketch, "E517", {"start": v(33.47, 55.4) * mm, "end": v(33.26, 55.27) * mm});
            skLineSegment(sketch, "E518", {"start": v(33.26, 55.27) * mm, "end": v(33.04, 55.13) * mm});
            skLineSegment(sketch, "E519", {"start": v(33.04, 55.13) * mm, "end": v(32.84, 55) * mm});
            skLineSegment(sketch, "E520", {"start": v(32.84, 55) * mm, "end": v(32.63, 54.87) * mm});
            skLineSegment(sketch, "E521", {"start": v(32.63, 54.87) * mm, "end": v(32.43, 54.73) * mm});
            skLineSegment(sketch, "E522", {"start": v(32.43, 54.73) * mm, "end": v(32.24, 54.6) * mm});
            skLineSegment(sketch, "E523", {"start": v(32.24, 54.6) * mm, "end": v(32.05, 54.47) * mm});
            skLineSegment(sketch, "E524", {"start": v(32.05, 54.47) * mm, "end": v(31.87, 54.34) * mm});
            skLineSegment(sketch, "E525", {"start": v(31.87, 54.34) * mm, "end": v(31.69, 54.2) * mm});
            skLineSegment(sketch, "E526", {"start": v(31.69, 54.2) * mm, "end": v(31.51, 54.08) * mm});
            skLineSegment(sketch, "E527", {"start": v(31.51, 54.08) * mm, "end": v(31.34, 53.95) * mm});
            skLineSegment(sketch, "E528", {"start": v(31.34, 53.95) * mm, "end": v(31.18, 53.83) * mm});
            skLineSegment(sketch, "E529", {"start": v(31.18, 53.83) * mm, "end": v(31.02, 53.7) * mm});
            skLineSegment(sketch, "E530", {"start": v(31.02, 53.7) * mm, "end": v(30.86, 53.58) * mm});
            skLineSegment(sketch, "E531", {"start": v(30.86, 53.58) * mm, "end": v(30.7, 53.45) * mm});
            skLineSegment(sketch, "E532", {"start": v(30.7, 53.45) * mm, "end": v(30.56, 53.33) * mm});
            skLineSegment(sketch, "E533", {"start": v(30.56, 53.33) * mm, "end": v(30.42, 53.21) * mm});
            skLineSegment(sketch, "E534", {"start": v(30.42, 53.21) * mm, "end": v(30.28, 53.1) * mm});
            skLineSegment(sketch, "E535", {"start": v(30.28, 53.1) * mm, "end": v(30.15, 52.98) * mm});
            skLineSegment(sketch, "E536", {"start": v(30.15, 52.98) * mm, "end": v(30.02, 52.87) * mm});
            skLineSegment(sketch, "E537", {"start": v(30.02, 52.87) * mm, "end": v(29.9, 52.75) * mm});
            skLineSegment(sketch, "E538", {"start": v(29.9, 52.75) * mm, "end": v(29.77, 52.64) * mm});
            skLineSegment(sketch, "E539", {"start": v(29.77, 52.64) * mm, "end": v(29.65, 52.53) * mm});
            skArc(sketch, "E540", {"start": v(29.65, 52.53) * mm, "mid": v(29.06, 52.86) * mm, "end": v(28.47, 53.19) * mm});
            skLineSegment(sketch, "E541", {"start": v(28.47, 53.19) * mm, "end": v(28.5, 53.34) * mm});
            skLineSegment(sketch, "E542", {"start": v(28.5, 53.34) * mm, "end": v(28.52, 53.5) * mm});
            skLineSegment(sketch, "E543", {"start": v(28.52, 53.5) * mm, "end": v(28.55, 53.67) * mm});
            skLineSegment(sketch, "E544", {"start": v(28.55, 53.67) * mm, "end": v(28.58, 53.84) * mm});
            skLineSegment(sketch, "E545", {"start": v(28.58, 53.84) * mm, "end": v(28.6, 54.02) * mm});
            skLineSegment(sketch, "E546", {"start": v(28.6, 54.02) * mm, "end": v(28.63, 54.2) * mm});
            skLineSegment(sketch, "E547", {"start": v(28.63, 54.2) * mm, "end": v(28.66, 54.38) * mm});
            skLineSegment(sketch, "E548", {"start": v(28.66, 54.38) * mm, "end": v(28.68, 54.57) * mm});
            skLineSegment(sketch, "E549", {"start": v(28.68, 54.57) * mm, "end": v(28.7, 54.76) * mm});
            skLineSegment(sketch, "E550", {"start": v(28.7, 54.76) * mm, "end": v(28.72, 54.96) * mm});
            skLineSegment(sketch, "E551", {"start": v(28.72, 54.96) * mm, "end": v(28.74, 55.17) * mm});
            skLineSegment(sketch, "E552", {"start": v(28.74, 55.17) * mm, "end": v(28.76, 55.37) * mm});
            skLineSegment(sketch, "E553", {"start": v(28.76, 55.37) * mm, "end": v(28.77, 55.58) * mm});
            skLineSegment(sketch, "E554", {"start": v(28.77, 55.58) * mm, "end": v(28.79, 55.8) * mm});
            skLineSegment(sketch, "E555", {"start": v(28.79, 55.8) * mm, "end": v(28.8, 56.02) * mm});
            skLineSegment(sketch, "E556", {"start": v(28.8, 56.02) * mm, "end": v(28.81, 56.25) * mm});
            skLineSegment(sketch, "E557", {"start": v(28.81, 56.25) * mm, "end": v(28.82, 56.48) * mm});
            skLineSegment(sketch, "E558", {"start": v(28.82, 56.48) * mm, "end": v(28.83, 56.71) * mm});
            skLineSegment(sketch, "E559", {"start": v(28.83, 56.71) * mm, "end": v(28.84, 56.95) * mm});
            skLineSegment(sketch, "E560", {"start": v(28.84, 56.95) * mm, "end": v(28.84, 57.2) * mm});
            skLineSegment(sketch, "E561", {"start": v(28.84, 57.2) * mm, "end": v(28.85, 57.44) * mm});
            skLineSegment(sketch, "E562", {"start": v(28.85, 57.44) * mm, "end": v(28.84, 57.7) * mm});
            skLineSegment(sketch, "E563", {"start": v(28.84, 57.7) * mm, "end": v(28.84, 57.95) * mm});
            skLineSegment(sketch, "E564", {"start": v(28.84, 57.95) * mm, "end": v(28.84, 58.21) * mm});
            skLineSegment(sketch, "E565", {"start": v(28.84, 58.21) * mm, "end": v(28.83, 58.48) * mm});
            skLineSegment(sketch, "E566", {"start": v(28.83, 58.48) * mm, "end": v(28.82, 58.74) * mm});
            skLineSegment(sketch, "E567", {"start": v(28.82, 58.74) * mm, "end": v(28.8, 59.02) * mm});
            skLineSegment(sketch, "E568", {"start": v(28.8, 59.02) * mm, "end": v(28.8, 59.3) * mm});
            skLineSegment(sketch, "E569", {"start": v(28.8, 59.3) * mm, "end": v(28.79, 59.44) * mm});
            skLineSegment(sketch, "E570", {"start": v(28.79, 59.44) * mm, "end": v(27.45, 60.07) * mm});
            skLineSegment(sketch, "E571", {"start": v(27.45, 60.07) * mm, "end": v(27.33, 59.98) * mm});
            skLineSegment(sketch, "E572", {"start": v(27.33, 59.98) * mm, "end": v(27.11, 59.82) * mm});
            skLineSegment(sketch, "E573", {"start": v(27.11, 59.82) * mm, "end": v(26.9, 59.65) * mm});
            skLineSegment(sketch, "E574", {"start": v(26.9, 59.65) * mm, "end": v(26.68, 59.49) * mm});
            skLineSegment(sketch, "E575", {"start": v(26.68, 59.49) * mm, "end": v(26.47, 59.32) * mm});
            skLineSegment(sketch, "E576", {"start": v(26.47, 59.32) * mm, "end": v(26.27, 59.16) * mm});
            skLineSegment(sketch, "E577", {"start": v(26.27, 59.16) * mm, "end": v(26.07, 59) * mm});
            skLineSegment(sketch, "E578", {"start": v(26.07, 59) * mm, "end": v(25.87, 58.84) * mm});
            skLineSegment(sketch, "E579", {"start": v(25.87, 58.84) * mm, "end": v(25.68, 58.68) * mm});
            skLineSegment(sketch, "E580", {"start": v(25.68, 58.68) * mm, "end": v(25.5, 58.52) * mm});
            skLineSegment(sketch, "E581", {"start": v(25.5, 58.52) * mm, "end": v(25.32, 58.37) * mm});
            skLineSegment(sketch, "E582", {"start": v(25.32, 58.37) * mm, "end": v(25.14, 58.2) * mm});
            skLineSegment(sketch, "E583", {"start": v(25.14, 58.2) * mm, "end": v(24.97, 58.06) * mm});
            skLineSegment(sketch, "E584", {"start": v(24.97, 58.06) * mm, "end": v(24.8, 57.9) * mm});
            skLineSegment(sketch, "E585", {"start": v(24.8, 57.9) * mm, "end": v(24.64, 57.75) * mm});
            skLineSegment(sketch, "E586", {"start": v(24.64, 57.75) * mm, "end": v(24.49, 57.6) * mm});
            skLineSegment(sketch, "E587", {"start": v(24.49, 57.6) * mm, "end": v(24.33, 57.45) * mm});
            skLineSegment(sketch, "E588", {"start": v(24.33, 57.45) * mm, "end": v(24.19, 57.3) * mm});
            skLineSegment(sketch, "E589", {"start": v(24.19, 57.3) * mm, "end": v(24.04, 57.16) * mm});
            skLineSegment(sketch, "E590", {"start": v(24.04, 57.16) * mm, "end": v(23.9, 57.02) * mm});
            skLineSegment(sketch, "E591", {"start": v(23.9, 57.02) * mm, "end": v(23.77, 56.88) * mm});
            skLineSegment(sketch, "E592", {"start": v(23.77, 56.88) * mm, "end": v(23.64, 56.74) * mm});
            skLineSegment(sketch, "E593", {"start": v(23.64, 56.74) * mm, "end": v(23.5, 56.6) * mm});
            skLineSegment(sketch, "E594", {"start": v(23.5, 56.6) * mm, "end": v(23.39, 56.47) * mm});
            skLineSegment(sketch, "E595", {"start": v(23.39, 56.47) * mm, "end": v(23.27, 56.34) * mm});
            skLineSegment(sketch, "E596", {"start": v(23.27, 56.34) * mm, "end": v(23.15, 56.21) * mm});
            skLineSegment(sketch, "E597", {"start": v(23.15, 56.21) * mm, "end": v(23.04, 56.08) * mm});
            skLineSegment(sketch, "E598", {"start": v(23.04, 56.08) * mm, "end": v(22.94, 55.96) * mm});
            skLineSegment(sketch, "E599", {"start": v(22.94, 55.96) * mm, "end": v(22.83, 55.84) * mm});
            skArc(sketch, "E600", {"start": v(22.83, 55.84) * mm, "mid": v(22.2, 56.09) * mm, "end": v(21.58, 56.33) * mm});
            skLineSegment(sketch, "E601", {"start": v(21.58, 56.33) * mm, "end": v(21.59, 56.5) * mm});
            skLineSegment(sketch, "E602", {"start": v(21.59, 56.5) * mm, "end": v(21.6, 56.66) * mm});
            skLineSegment(sketch, "E603", {"start": v(21.6, 56.66) * mm, "end": v(21.6, 56.83) * mm});
            skLineSegment(sketch, "E604", {"start": v(21.6, 56.83) * mm, "end": v(21.6, 57) * mm});
            skLineSegment(sketch, "E605", {"start": v(21.6, 57) * mm, "end": v(21.61, 57.18) * mm});
            skLineSegment(sketch, "E606", {"start": v(21.61, 57.18) * mm, "end": v(21.61, 57.36) * mm});
            skLineSegment(sketch, "E607", {"start": v(21.61, 57.36) * mm, "end": v(21.61, 57.54) * mm});
            skLineSegment(sketch, "E608", {"start": v(21.61, 57.54) * mm, "end": v(21.61, 57.73) * mm});
            skLineSegment(sketch, "E609", {"start": v(21.61, 57.73) * mm, "end": v(21.61, 57.93) * mm});
            skLineSegment(sketch, "E610", {"start": v(21.61, 57.93) * mm, "end": v(21.6, 58.13) * mm});
            skLineSegment(sketch, "E611", {"start": v(21.6, 58.13) * mm, "end": v(21.6, 58.33) * mm});
            skLineSegment(sketch, "E612", {"start": v(21.6, 58.33) * mm, "end": v(21.6, 58.54) * mm});
            skLineSegment(sketch, "E613", {"start": v(21.6, 58.54) * mm, "end": v(21.58, 58.75) * mm});
            skLineSegment(sketch, "E614", {"start": v(21.58, 58.75) * mm, "end": v(21.57, 58.97) * mm});
            skLineSegment(sketch, "E615", {"start": v(21.57, 58.97) * mm, "end": v(21.55, 59.2) * mm});
            skLineSegment(sketch, "E616", {"start": v(21.55, 59.2) * mm, "end": v(21.54, 59.42) * mm});
            skLineSegment(sketch, "E617", {"start": v(21.54, 59.42) * mm, "end": v(21.52, 59.64) * mm});
            skLineSegment(sketch, "E618", {"start": v(21.52, 59.64) * mm, "end": v(21.5, 59.88) * mm});
            skLineSegment(sketch, "E619", {"start": v(21.5, 59.88) * mm, "end": v(21.47, 60.12) * mm});
            skLineSegment(sketch, "E620", {"start": v(21.47, 60.12) * mm, "end": v(21.45, 60.36) * mm});
            skLineSegment(sketch, "E621", {"start": v(21.45, 60.36) * mm, "end": v(21.42, 60.6) * mm});
            skLineSegment(sketch, "E622", {"start": v(21.42, 60.6) * mm, "end": v(21.39, 60.85) * mm});
            skLineSegment(sketch, "E623", {"start": v(21.39, 60.85) * mm, "end": v(21.35, 61.1) * mm});
            skLineSegment(sketch, "E624", {"start": v(21.35, 61.1) * mm, "end": v(21.31, 61.37) * mm});
            skLineSegment(sketch, "E625", {"start": v(21.31, 61.37) * mm, "end": v(21.27, 61.63) * mm});
            skLineSegment(sketch, "E626", {"start": v(21.27, 61.63) * mm, "end": v(21.23, 61.9) * mm});
            skLineSegment(sketch, "E627", {"start": v(21.23, 61.9) * mm, "end": v(21.19, 62.16) * mm});
            skLineSegment(sketch, "E628", {"start": v(21.19, 62.16) * mm, "end": v(21.14, 62.44) * mm});
            skLineSegment(sketch, "E629", {"start": v(21.14, 62.44) * mm, "end": v(21.1, 62.58) * mm});
            skLineSegment(sketch, "E630", {"start": v(21.1, 62.58) * mm, "end": v(19.7, 63.03) * mm});
            skLineSegment(sketch, "E631", {"start": v(19.7, 63.03) * mm, "end": v(19.6, 62.94) * mm});
            skLineSegment(sketch, "E632", {"start": v(19.6, 62.94) * mm, "end": v(19.4, 62.74) * mm});
            skLineSegment(sketch, "E633", {"start": v(19.4, 62.74) * mm, "end": v(19.2, 62.55) * mm});
            skLineSegment(sketch, "E634", {"start": v(19.2, 62.55) * mm, "end": v(19.01, 62.36) * mm});
            skLineSegment(sketch, "E635", {"start": v(19.01, 62.36) * mm, "end": v(18.83, 62.17) * mm});
            skLineSegment(sketch, "E636", {"start": v(18.83, 62.17) * mm, "end": v(18.64, 61.99) * mm});
            skLineSegment(sketch, "E637", {"start": v(18.64, 61.99) * mm, "end": v(18.47, 61.8) * mm});
            skLineSegment(sketch, "E638", {"start": v(18.47, 61.8) * mm, "end": v(18.3, 61.62) * mm});
            skLineSegment(sketch, "E639", {"start": v(18.3, 61.62) * mm, "end": v(18.13, 61.44) * mm});
            skLineSegment(sketch, "E640", {"start": v(18.13, 61.44) * mm, "end": v(17.96, 61.26) * mm});
            skLineSegment(sketch, "E641", {"start": v(17.96, 61.26) * mm, "end": v(17.8, 61.08) * mm});
            skLineSegment(sketch, "E642", {"start": v(17.8, 61.08) * mm, "end": v(17.65, 60.9) * mm});
            skLineSegment(sketch, "E643", {"start": v(17.65, 60.9) * mm, "end": v(17.5, 60.73) * mm});
            skLineSegment(sketch, "E644", {"start": v(17.5, 60.73) * mm, "end": v(17.35, 60.56) * mm});
            skLineSegment(sketch, "E645", {"start": v(17.35, 60.56) * mm, "end": v(17.21, 60.39) * mm});
            skLineSegment(sketch, "E646", {"start": v(17.21, 60.39) * mm, "end": v(17.07, 60.22) * mm});
            skLineSegment(sketch, "E647", {"start": v(17.07, 60.22) * mm, "end": v(16.94, 60.05) * mm});
            skLineSegment(sketch, "E648", {"start": v(16.94, 60.05) * mm, "end": v(16.81, 59.89) * mm});
            skLineSegment(sketch, "E649", {"start": v(16.81, 59.89) * mm, "end": v(16.69, 59.73) * mm});
            skLineSegment(sketch, "E650", {"start": v(16.69, 59.73) * mm, "end": v(16.57, 59.57) * mm});
            skLineSegment(sketch, "E651", {"start": v(16.57, 59.57) * mm, "end": v(16.45, 59.41) * mm});
            skLineSegment(sketch, "E652", {"start": v(16.45, 59.41) * mm, "end": v(16.34, 59.26) * mm});
            skLineSegment(sketch, "E653", {"start": v(16.34, 59.26) * mm, "end": v(16.23, 59.1) * mm});
            skLineSegment(sketch, "E654", {"start": v(16.23, 59.1) * mm, "end": v(16.12, 58.96) * mm});
            skLineSegment(sketch, "E655", {"start": v(16.12, 58.96) * mm, "end": v(16.02, 58.81) * mm});
            skLineSegment(sketch, "E656", {"start": v(16.02, 58.81) * mm, "end": v(15.93, 58.67) * mm});
            skLineSegment(sketch, "E657", {"start": v(15.93, 58.67) * mm, "end": v(15.83, 58.53) * mm});
            skLineSegment(sketch, "E658", {"start": v(15.83, 58.53) * mm, "end": v(15.74, 58.4) * mm});
            skLineSegment(sketch, "E659", {"start": v(15.74, 58.4) * mm, "end": v(15.66, 58.26) * mm});
            skArc(sketch, "E660", {"start": v(15.66, 58.26) * mm, "mid": v(15, 58.43) * mm, "end": v(14.35, 58.6) * mm});
            skLineSegment(sketch, "E661", {"start": v(14.35, 58.6) * mm, "end": v(14.34, 58.75) * mm});
            skLineSegment(sketch, "E662", {"start": v(14.34, 58.75) * mm, "end": v(14.32, 58.92) * mm});
            skLineSegment(sketch, "E663", {"start": v(14.32, 58.92) * mm, "end": v(14.3, 59.08) * mm});
            skLineSegment(sketch, "E664", {"start": v(14.3, 59.08) * mm, "end": v(14.3, 59.26) * mm});
            skLineSegment(sketch, "E665", {"start": v(14.3, 59.26) * mm, "end": v(14.27, 59.43) * mm});
            skLineSegment(sketch, "E666", {"start": v(14.27, 59.43) * mm, "end": v(14.25, 59.61) * mm});
            skLineSegment(sketch, "E667", {"start": v(14.25, 59.61) * mm, "end": v(14.23, 59.8) * mm});
            skLineSegment(sketch, "E668", {"start": v(14.23, 59.8) * mm, "end": v(14.2, 59.99) * mm});
            skLineSegment(sketch, "E669", {"start": v(14.2, 59.99) * mm, "end": v(14.18, 60.18) * mm});
            skLineSegment(sketch, "E670", {"start": v(14.18, 60.18) * mm, "end": v(14.15, 60.38) * mm});
            skLineSegment(sketch, "E671", {"start": v(14.15, 60.38) * mm, "end": v(14.12, 60.58) * mm});
            skLineSegment(sketch, "E672", {"start": v(14.12, 60.58) * mm, "end": v(14.08, 60.79) * mm});
            skLineSegment(sketch, "E673", {"start": v(14.08, 60.79) * mm, "end": v(14.05, 61) * mm});
            skLineSegment(sketch, "E674", {"start": v(14.05, 61) * mm, "end": v(14, 61.2) * mm});
            skLineSegment(sketch, "E675", {"start": v(14, 61.2) * mm, "end": v(13.97, 61.43) * mm});
            skLineSegment(sketch, "E676", {"start": v(13.97, 61.43) * mm, "end": v(13.92, 61.65) * mm});
            skLineSegment(sketch, "E677", {"start": v(13.92, 61.65) * mm, "end": v(13.87, 61.87) * mm});
            skLineSegment(sketch, "E678", {"start": v(13.87, 61.87) * mm, "end": v(13.82, 62.1) * mm});
            skLineSegment(sketch, "E679", {"start": v(13.82, 62.1) * mm, "end": v(13.77, 62.33) * mm});
            skLineSegment(sketch, "E680", {"start": v(13.77, 62.33) * mm, "end": v(13.71, 62.57) * mm});
            skLineSegment(sketch, "E681", {"start": v(13.71, 62.57) * mm, "end": v(13.65, 62.81) * mm});
            skLineSegment(sketch, "E682", {"start": v(13.65, 62.81) * mm, "end": v(13.6, 63.05) * mm});
            skLineSegment(sketch, "E683", {"start": v(13.6, 63.05) * mm, "end": v(13.52, 63.3) * mm});
            skLineSegment(sketch, "E684", {"start": v(13.52, 63.3) * mm, "end": v(13.46, 63.55) * mm});
            skLineSegment(sketch, "E685", {"start": v(13.46, 63.55) * mm, "end": v(13.38, 63.8) * mm});
            skLineSegment(sketch, "E686", {"start": v(13.38, 63.8) * mm, "end": v(13.3, 64.07) * mm});
            skLineSegment(sketch, "E687", {"start": v(13.3, 64.07) * mm, "end": v(13.23, 64.33) * mm});
            skLineSegment(sketch, "E688", {"start": v(13.23, 64.33) * mm, "end": v(13.14, 64.6) * mm});
            skLineSegment(sketch, "E689", {"start": v(13.14, 64.6) * mm, "end": v(13.1, 64.73) * mm});
            skLineSegment(sketch, "E690", {"start": v(13.1, 64.73) * mm, "end": v(11.65, 65) * mm});
            skLineSegment(sketch, "E691", {"start": v(11.65, 65) * mm, "end": v(11.56, 64.9) * mm});
            skLineSegment(sketch, "E692", {"start": v(11.56, 64.9) * mm, "end": v(11.38, 64.68) * mm});
            skLineSegment(sketch, "E693", {"start": v(11.38, 64.68) * mm, "end": v(11.21, 64.47) * mm});
            skLineSegment(sketch, "E694", {"start": v(11.21, 64.47) * mm, "end": v(11.05, 64.25) * mm});
            skLineSegment(sketch, "E695", {"start": v(11.05, 64.25) * mm, "end": v(10.88, 64.04) * mm});
            skLineSegment(sketch, "E696", {"start": v(10.88, 64.04) * mm, "end": v(10.73, 63.84) * mm});
            skLineSegment(sketch, "E697", {"start": v(10.73, 63.84) * mm, "end": v(10.58, 63.63) * mm});
            skLineSegment(sketch, "E698", {"start": v(10.58, 63.63) * mm, "end": v(10.43, 63.43) * mm});
            skLineSegment(sketch, "E699", {"start": v(10.43, 63.43) * mm, "end": v(10.28, 63.22) * mm});
            skLineSegment(sketch, "E700", {"start": v(10.28, 63.22) * mm, "end": v(10.14, 63.03) * mm});
            skLineSegment(sketch, "E701", {"start": v(10.14, 63.03) * mm, "end": v(10, 62.83) * mm});
            skLineSegment(sketch, "E702", {"start": v(10, 62.83) * mm, "end": v(9.88, 62.63) * mm});
            skLineSegment(sketch, "E703", {"start": v(9.88, 62.63) * mm, "end": v(9.75, 62.44) * mm});
            skLineSegment(sketch, "E704", {"start": v(9.75, 62.44) * mm, "end": v(9.63, 62.25) * mm});
            skLineSegment(sketch, "E705", {"start": v(9.63, 62.25) * mm, "end": v(9.5, 62.07) * mm});
            skLineSegment(sketch, "E706", {"start": v(9.5, 62.07) * mm, "end": v(9.4, 61.88) * mm});
            skLineSegment(sketch, "E707", {"start": v(9.4, 61.88) * mm, "end": v(9.28, 61.7) * mm});
            skLineSegment(sketch, "E708", {"start": v(9.28, 61.7) * mm, "end": v(9.17, 61.52) * mm});
            skLineSegment(sketch, "E709", {"start": v(9.17, 61.52) * mm, "end": v(9.07, 61.35) * mm});
            skLineSegment(sketch, "E710", {"start": v(9.07, 61.35) * mm, "end": v(8.97, 61.17) * mm});
            skLineSegment(sketch, "E711", {"start": v(8.97, 61.17) * mm, "end": v(8.87, 61) * mm});
            skLineSegment(sketch, "E712", {"start": v(8.87, 61) * mm, "end": v(8.78, 60.84) * mm});
            skLineSegment(sketch, "E713", {"start": v(8.78, 60.84) * mm, "end": v(8.7, 60.67) * mm});
            skLineSegment(sketch, "E714", {"start": v(8.7, 60.67) * mm, "end": v(8.6, 60.51) * mm});
            skLineSegment(sketch, "E715", {"start": v(8.6, 60.51) * mm, "end": v(8.53, 60.36) * mm});
            skLineSegment(sketch, "E716", {"start": v(8.53, 60.36) * mm, "end": v(8.45, 60.2) * mm});
            skLineSegment(sketch, "E717", {"start": v(8.45, 60.2) * mm, "end": v(8.37, 60.05) * mm});
            skLineSegment(sketch, "E718", {"start": v(8.37, 60.05) * mm, "end": v(8.3, 59.9) * mm});
            skLineSegment(sketch, "E719", {"start": v(8.3, 59.9) * mm, "end": v(8.23, 59.76) * mm});
            skArc(sketch, "E720", {"start": v(8.23, 59.76) * mm, "mid": v(7.56, 59.85) * mm, "end": v(6.89, 59.93) * mm});
            skLineSegment(sketch, "E721", {"start": v(6.89, 59.93) * mm, "end": v(6.86, 60.09) * mm});
            skLineSegment(sketch, "E722", {"start": v(6.86, 60.09) * mm, "end": v(6.83, 60.25) * mm});
            skLineSegment(sketch, "E723", {"start": v(6.83, 60.25) * mm, "end": v(6.8, 60.41) * mm});
            skLineSegment(sketch, "E724", {"start": v(6.8, 60.41) * mm, "end": v(6.75, 60.58) * mm});
            skLineSegment(sketch, "E725", {"start": v(6.75, 60.58) * mm, "end": v(6.71, 60.75) * mm});
            skLineSegment(sketch, "E726", {"start": v(6.71, 60.75) * mm, "end": v(6.67, 60.93) * mm});
            skLineSegment(sketch, "E727", {"start": v(6.67, 60.93) * mm, "end": v(6.62, 61.11) * mm});
            skLineSegment(sketch, "E728", {"start": v(6.62, 61.11) * mm, "end": v(6.58, 61.3) * mm});
            skLineSegment(sketch, "E729", {"start": v(6.58, 61.3) * mm, "end": v(6.52, 61.48) * mm});
            skLineSegment(sketch, "E730", {"start": v(6.52, 61.48) * mm, "end": v(6.47, 61.68) * mm});
            skLineSegment(sketch, "E731", {"start": v(6.47, 61.68) * mm, "end": v(6.41, 61.87) * mm});
            skLineSegment(sketch, "E732", {"start": v(6.41, 61.87) * mm, "end": v(6.35, 62.07) * mm});
            skLineSegment(sketch, "E733", {"start": v(6.35, 62.07) * mm, "end": v(6.3, 62.27) * mm});
            skLineSegment(sketch, "E734", {"start": v(6.3, 62.27) * mm, "end": v(6.23, 62.48) * mm});
            skLineSegment(sketch, "E735", {"start": v(6.23, 62.48) * mm, "end": v(6.16, 62.7) * mm});
            skLineSegment(sketch, "E736", {"start": v(6.16, 62.7) * mm, "end": v(6.09, 62.9) * mm});
            skLineSegment(sketch, "E737", {"start": v(6.09, 62.9) * mm, "end": v(6, 63.12) * mm});
            skLineSegment(sketch, "E738", {"start": v(6, 63.12) * mm, "end": v(5.93, 63.34) * mm});
            skLineSegment(sketch, "E739", {"start": v(5.93, 63.34) * mm, "end": v(5.85, 63.57) * mm});
            skLineSegment(sketch, "E740", {"start": v(5.85, 63.57) * mm, "end": v(5.76, 63.8) * mm});
            skLineSegment(sketch, "E741", {"start": v(5.76, 63.8) * mm, "end": v(5.67, 64.03) * mm});
            skLineSegment(sketch, "E742", {"start": v(5.67, 64.03) * mm, "end": v(5.58, 64.26) * mm});
            skLineSegment(sketch, "E743", {"start": v(5.58, 64.26) * mm, "end": v(5.48, 64.5) * mm});
            skLineSegment(sketch, "E744", {"start": v(5.48, 64.5) * mm, "end": v(5.38, 64.74) * mm});
            skLineSegment(sketch, "E745", {"start": v(5.38, 64.74) * mm, "end": v(5.28, 64.98) * mm});
            skLineSegment(sketch, "E746", {"start": v(5.28, 64.98) * mm, "end": v(5.17, 65.23) * mm});
            skLineSegment(sketch, "E747", {"start": v(5.17, 65.23) * mm, "end": v(5.06, 65.48) * mm});
            skLineSegment(sketch, "E748", {"start": v(5.06, 65.48) * mm, "end": v(4.94, 65.73) * mm});
            skLineSegment(sketch, "E749", {"start": v(4.94, 65.73) * mm, "end": v(4.88, 65.86) * mm});
            skLineSegment(sketch, "E750", {"start": v(4.88, 65.86) * mm, "end": v(3.4, 65.95) * mm});
            skLineSegment(sketch, "E751", {"start": v(3.4, 65.95) * mm, "end": v(3.33, 65.83) * mm});
            skLineSegment(sketch, "E752", {"start": v(3.33, 65.83) * mm, "end": v(3.19, 65.6) * mm});
            skLineSegment(sketch, "E753", {"start": v(3.19, 65.6) * mm, "end": v(3.04, 65.36) * mm});
            skLineSegment(sketch, "E754", {"start": v(3.04, 65.36) * mm, "end": v(2.9, 65.13) * mm});
            skLineSegment(sketch, "E755", {"start": v(2.9, 65.13) * mm, "end": v(2.77, 64.9) * mm});
            skLineSegment(sketch, "E756", {"start": v(2.77, 64.9) * mm, "end": v(2.64, 64.68) * mm});
            skLineSegment(sketch, "E757", {"start": v(2.64, 64.68) * mm, "end": v(2.52, 64.45) * mm});
            skLineSegment(sketch, "E758", {"start": v(2.52, 64.45) * mm, "end": v(2.4, 64.23) * mm});
            skLineSegment(sketch, "E759", {"start": v(2.4, 64.23) * mm, "end": v(2.28, 64.01) * mm});
            skLineSegment(sketch, "E760", {"start": v(2.28, 64.01) * mm, "end": v(2.16, 63.8) * mm});
            skLineSegment(sketch, "E761", {"start": v(2.16, 63.8) * mm, "end": v(2.05, 63.59) * mm});
            skLineSegment(sketch, "E762", {"start": v(2.05, 63.59) * mm, "end": v(1.95, 63.38) * mm});
            skLineSegment(sketch, "E763", {"start": v(1.95, 63.38) * mm, "end": v(1.85, 63.17) * mm});
            skLineSegment(sketch, "E764", {"start": v(1.85, 63.17) * mm, "end": v(1.75, 62.97) * mm});
            skLineSegment(sketch, "E765", {"start": v(1.75, 62.97) * mm, "end": v(1.65, 62.77) * mm});
            skLineSegment(sketch, "E766", {"start": v(1.65, 62.77) * mm, "end": v(1.56, 62.57) * mm});
            skLineSegment(sketch, "E767", {"start": v(1.56, 62.57) * mm, "end": v(1.47, 62.38) * mm});
            skLineSegment(sketch, "E768", {"start": v(1.47, 62.38) * mm, "end": v(1.4, 62.19) * mm});
            skLineSegment(sketch, "E769", {"start": v(1.4, 62.19) * mm, "end": v(1.31, 62) * mm});
            skLineSegment(sketch, "E770", {"start": v(1.31, 62) * mm, "end": v(1.23, 61.82) * mm});
            skLineSegment(sketch, "E771", {"start": v(1.23, 61.82) * mm, "end": v(1.16, 61.64) * mm});
            skLineSegment(sketch, "E772", {"start": v(1.16, 61.64) * mm, "end": v(1.09, 61.46) * mm});
            skLineSegment(sketch, "E773", {"start": v(1.09, 61.46) * mm, "end": v(1.02, 61.29) * mm});
            skLineSegment(sketch, "E774", {"start": v(1.02, 61.29) * mm, "end": v(0.96, 61.12) * mm});
            skLineSegment(sketch, "E775", {"start": v(0.96, 61.12) * mm, "end": v(0.9, 60.95) * mm});
            skLineSegment(sketch, "E776", {"start": v(0.9, 60.95) * mm, "end": v(0.83, 60.79) * mm});
            skLineSegment(sketch, "E777", {"start": v(0.83, 60.79) * mm, "end": v(0.78, 60.63) * mm});
            skLineSegment(sketch, "E778", {"start": v(0.78, 60.63) * mm, "end": v(0.73, 60.47) * mm});
            skLineSegment(sketch, "E779", {"start": v(0.73, 60.47) * mm, "end": v(0.68, 60.32) * mm});
            skArc(sketch, "E780", {"start": v(0.68, 60.32) * mm, "mid": v(0, 60.32) * mm, "end": v(-0.68, 60.32) * mm});
            skLineSegment(sketch, "E781", {"start": v(-0.68, 60.32) * mm, "end": v(-0.73, 60.47) * mm});
            skLineSegment(sketch, "E782", {"start": v(-0.73, 60.47) * mm, "end": v(-0.78, 60.63) * mm});
            skLineSegment(sketch, "E783", {"start": v(-0.78, 60.63) * mm, "end": v(-0.83, 60.79) * mm});
            skLineSegment(sketch, "E784", {"start": v(-0.83, 60.79) * mm, "end": v(-0.9, 60.95) * mm});
            skLineSegment(sketch, "E785", {"start": v(-0.9, 60.95) * mm, "end": v(-0.96, 61.12) * mm});
            skLineSegment(sketch, "E786", {"start": v(-0.96, 61.12) * mm, "end": v(-1.02, 61.29) * mm});
            skLineSegment(sketch, "E787", {"start": v(-1.02, 61.29) * mm, "end": v(-1.09, 61.46) * mm});
            skLineSegment(sketch, "E788", {"start": v(-1.09, 61.46) * mm, "end": v(-1.16, 61.64) * mm});
            skLineSegment(sketch, "E789", {"start": v(-1.16, 61.64) * mm, "end": v(-1.23, 61.82) * mm});
            skLineSegment(sketch, "E790", {"start": v(-1.23, 61.82) * mm, "end": v(-1.31, 62) * mm});
            skLineSegment(sketch, "E791", {"start": v(-1.31, 62) * mm, "end": v(-1.4, 62.19) * mm});
            skLineSegment(sketch, "E792", {"start": v(-1.4, 62.19) * mm, "end": v(-1.47, 62.38) * mm});
            skLineSegment(sketch, "E793", {"start": v(-1.47, 62.38) * mm, "end": v(-1.56, 62.57) * mm});
            skLineSegment(sketch, "E794", {"start": v(-1.56, 62.57) * mm, "end": v(-1.65, 62.77) * mm});
            skLineSegment(sketch, "E795", {"start": v(-1.65, 62.77) * mm, "end": v(-1.75, 62.97) * mm});
            skLineSegment(sketch, "E796", {"start": v(-1.75, 62.97) * mm, "end": v(-1.85, 63.17) * mm});
            skLineSegment(sketch, "E797", {"start": v(-1.85, 63.17) * mm, "end": v(-1.95, 63.38) * mm});
            skLineSegment(sketch, "E798", {"start": v(-1.95, 63.38) * mm, "end": v(-2.05, 63.59) * mm});
            skLineSegment(sketch, "E799", {"start": v(-2.05, 63.59) * mm, "end": v(-2.16, 63.8) * mm});
            skLineSegment(sketch, "E800", {"start": v(-2.16, 63.8) * mm, "end": v(-2.28, 64.01) * mm});
            skLineSegment(sketch, "E801", {"start": v(-2.28, 64.01) * mm, "end": v(-2.4, 64.23) * mm});
            skLineSegment(sketch, "E802", {"start": v(-2.4, 64.23) * mm, "end": v(-2.52, 64.45) * mm});
            skLineSegment(sketch, "E803", {"start": v(-2.52, 64.45) * mm, "end": v(-2.64, 64.68) * mm});
            skLineSegment(sketch, "E804", {"start": v(-2.64, 64.68) * mm, "end": v(-2.77, 64.9) * mm});
            skLineSegment(sketch, "E805", {"start": v(-2.77, 64.9) * mm, "end": v(-2.9, 65.13) * mm});
            skLineSegment(sketch, "E806", {"start": v(-2.9, 65.13) * mm, "end": v(-3.04, 65.36) * mm});
            skLineSegment(sketch, "E807", {"start": v(-3.04, 65.36) * mm, "end": v(-3.19, 65.6) * mm});
            skLineSegment(sketch, "E808", {"start": v(-3.19, 65.6) * mm, "end": v(-3.33, 65.83) * mm});
            skLineSegment(sketch, "E809", {"start": v(-3.33, 65.83) * mm, "end": v(-3.4, 65.95) * mm});
            skLineSegment(sketch, "E810", {"start": v(-3.4, 65.95) * mm, "end": v(-4.88, 65.86) * mm});
            skLineSegment(sketch, "E811", {"start": v(-4.88, 65.86) * mm, "end": v(-4.94, 65.73) * mm});
            skLineSegment(sketch, "E812", {"start": v(-4.94, 65.73) * mm, "end": v(-5.06, 65.48) * mm});
            skLineSegment(sketch, "E813", {"start": v(-5.06, 65.48) * mm, "end": v(-5.17, 65.23) * mm});
            skLineSegment(sketch, "E814", {"start": v(-5.17, 65.23) * mm, "end": v(-5.28, 64.98) * mm});
            skLineSegment(sketch, "E815", {"start": v(-5.28, 64.98) * mm, "end": v(-5.38, 64.74) * mm});
            skLineSegment(sketch, "E816", {"start": v(-5.38, 64.74) * mm, "end": v(-5.48, 64.5) * mm});
            skLineSegment(sketch, "E817", {"start": v(-5.48, 64.5) * mm, "end": v(-5.58, 64.26) * mm});
            skLineSegment(sketch, "E818", {"start": v(-5.58, 64.26) * mm, "end": v(-5.67, 64.03) * mm});
            skLineSegment(sketch, "E819", {"start": v(-5.67, 64.03) * mm, "end": v(-5.76, 63.8) * mm});
            skLineSegment(sketch, "E820", {"start": v(-5.76, 63.8) * mm, "end": v(-5.85, 63.57) * mm});
            skLineSegment(sketch, "E821", {"start": v(-5.85, 63.57) * mm, "end": v(-5.93, 63.34) * mm});
            skLineSegment(sketch, "E822", {"start": v(-5.93, 63.34) * mm, "end": v(-6.01, 63.12) * mm});
            skLineSegment(sketch, "E823", {"start": v(-6.01, 63.12) * mm, "end": v(-6.09, 62.9) * mm});
            skLineSegment(sketch, "E824", {"start": v(-6.09, 62.9) * mm, "end": v(-6.16, 62.7) * mm});
            skLineSegment(sketch, "E825", {"start": v(-6.16, 62.7) * mm, "end": v(-6.23, 62.48) * mm});
            skLineSegment(sketch, "E826", {"start": v(-6.23, 62.48) * mm, "end": v(-6.3, 62.27) * mm});
            skLineSegment(sketch, "E827", {"start": v(-6.3, 62.27) * mm, "end": v(-6.35, 62.07) * mm});
            skLineSegment(sketch, "E828", {"start": v(-6.35, 62.07) * mm, "end": v(-6.41, 61.87) * mm});
            skLineSegment(sketch, "E829", {"start": v(-6.41, 61.87) * mm, "end": v(-6.47, 61.68) * mm});
            skLineSegment(sketch, "E830", {"start": v(-6.47, 61.68) * mm, "end": v(-6.52, 61.48) * mm});
            skLineSegment(sketch, "E831", {"start": v(-6.52, 61.48) * mm, "end": v(-6.58, 61.3) * mm});
            skLineSegment(sketch, "E832", {"start": v(-6.58, 61.3) * mm, "end": v(-6.62, 61.11) * mm});
            skLineSegment(sketch, "E833", {"start": v(-6.62, 61.11) * mm, "end": v(-6.67, 60.93) * mm});
            skLineSegment(sketch, "E834", {"start": v(-6.67, 60.93) * mm, "end": v(-6.71, 60.75) * mm});
            skLineSegment(sketch, "E835", {"start": v(-6.71, 60.75) * mm, "end": v(-6.75, 60.58) * mm});
            skLineSegment(sketch, "E836", {"start": v(-6.75, 60.58) * mm, "end": v(-6.8, 60.41) * mm});
            skLineSegment(sketch, "E837", {"start": v(-6.8, 60.41) * mm, "end": v(-6.83, 60.25) * mm});
            skLineSegment(sketch, "E838", {"start": v(-6.83, 60.25) * mm, "end": v(-6.86, 60.09) * mm});
            skLineSegment(sketch, "E839", {"start": v(-6.86, 60.09) * mm, "end": v(-6.89, 59.93) * mm});
            skArc(sketch, "E840", {"start": v(-6.89, 59.93) * mm, "mid": v(-7.56, 59.85) * mm, "end": v(-8.23, 59.76) * mm});
            skLineSegment(sketch, "E841", {"start": v(-8.23, 59.76) * mm, "end": v(-8.3, 59.9) * mm});
            skLineSegment(sketch, "E842", {"start": v(-8.3, 59.9) * mm, "end": v(-8.37, 60.05) * mm});
            skLineSegment(sketch, "E843", {"start": v(-8.37, 60.05) * mm, "end": v(-8.45, 60.2) * mm});
            skLineSegment(sketch, "E844", {"start": v(-8.45, 60.2) * mm, "end": v(-8.53, 60.36) * mm});
            skLineSegment(sketch, "E845", {"start": v(-8.53, 60.36) * mm, "end": v(-8.6, 60.51) * mm});
            skLineSegment(sketch, "E846", {"start": v(-8.6, 60.51) * mm, "end": v(-8.7, 60.67) * mm});
            skLineSegment(sketch, "E847", {"start": v(-8.7, 60.67) * mm, "end": v(-8.78, 60.84) * mm});
            skLineSegment(sketch, "E848", {"start": v(-8.78, 60.84) * mm, "end": v(-8.87, 61) * mm});
            skLineSegment(sketch, "E849", {"start": v(-8.87, 61) * mm, "end": v(-8.97, 61.17) * mm});
            skLineSegment(sketch, "E850", {"start": v(-8.97, 61.17) * mm, "end": v(-9.07, 61.35) * mm});
            skLineSegment(sketch, "E851", {"start": v(-9.07, 61.35) * mm, "end": v(-9.17, 61.52) * mm});
            skLineSegment(sketch, "E852", {"start": v(-9.17, 61.52) * mm, "end": v(-9.28, 61.7) * mm});
            skLineSegment(sketch, "E853", {"start": v(-9.28, 61.7) * mm, "end": v(-9.4, 61.88) * mm});
            skLineSegment(sketch, "E854", {"start": v(-9.4, 61.88) * mm, "end": v(-9.5, 62.07) * mm});
            skLineSegment(sketch, "E855", {"start": v(-9.5, 62.07) * mm, "end": v(-9.63, 62.25) * mm});
            skLineSegment(sketch, "E856", {"start": v(-9.63, 62.25) * mm, "end": v(-9.75, 62.44) * mm});
            skLineSegment(sketch, "E857", {"start": v(-9.75, 62.44) * mm, "end": v(-9.88, 62.63) * mm});
            skLineSegment(sketch, "E858", {"start": v(-9.88, 62.63) * mm, "end": v(-10, 62.83) * mm});
            skLineSegment(sketch, "E859", {"start": v(-10, 62.83) * mm, "end": v(-10.14, 63.03) * mm});
            skLineSegment(sketch, "E860", {"start": v(-10.14, 63.03) * mm, "end": v(-10.28, 63.22) * mm});
            skLineSegment(sketch, "E861", {"start": v(-10.28, 63.22) * mm, "end": v(-10.43, 63.43) * mm});
            skLineSegment(sketch, "E862", {"start": v(-10.43, 63.43) * mm, "end": v(-10.58, 63.63) * mm});
            skLineSegment(sketch, "E863", {"start": v(-10.58, 63.63) * mm, "end": v(-10.73, 63.84) * mm});
            skLineSegment(sketch, "E864", {"start": v(-10.73, 63.84) * mm, "end": v(-10.88, 64.04) * mm});
            skLineSegment(sketch, "E865", {"start": v(-10.88, 64.04) * mm, "end": v(-11.05, 64.25) * mm});
            skLineSegment(sketch, "E866", {"start": v(-11.05, 64.25) * mm, "end": v(-11.21, 64.47) * mm});
            skLineSegment(sketch, "E867", {"start": v(-11.21, 64.47) * mm, "end": v(-11.38, 64.68) * mm});
            skLineSegment(sketch, "E868", {"start": v(-11.38, 64.68) * mm, "end": v(-11.56, 64.9) * mm});
            skLineSegment(sketch, "E869", {"start": v(-11.56, 64.9) * mm, "end": v(-11.65, 65) * mm});
            skLineSegment(sketch, "E870", {"start": v(-11.65, 65) * mm, "end": v(-13.1, 64.73) * mm});
            skLineSegment(sketch, "E871", {"start": v(-13.1, 64.73) * mm, "end": v(-13.14, 64.6) * mm});
            skLineSegment(sketch, "E872", {"start": v(-13.14, 64.6) * mm, "end": v(-13.23, 64.33) * mm});
            skLineSegment(sketch, "E873", {"start": v(-13.23, 64.33) * mm, "end": v(-13.3, 64.07) * mm});
            skLineSegment(sketch, "E874", {"start": v(-13.3, 64.07) * mm, "end": v(-13.38, 63.8) * mm});
            skLineSegment(sketch, "E875", {"start": v(-13.38, 63.8) * mm, "end": v(-13.46, 63.55) * mm});
            skLineSegment(sketch, "E876", {"start": v(-13.46, 63.55) * mm, "end": v(-13.53, 63.3) * mm});
            skLineSegment(sketch, "E877", {"start": v(-13.53, 63.3) * mm, "end": v(-13.6, 63.05) * mm});
            skLineSegment(sketch, "E878", {"start": v(-13.6, 63.05) * mm, "end": v(-13.65, 62.81) * mm});
            skLineSegment(sketch, "E879", {"start": v(-13.65, 62.81) * mm, "end": v(-13.71, 62.57) * mm});
            skLineSegment(sketch, "E880", {"start": v(-13.71, 62.57) * mm, "end": v(-13.77, 62.33) * mm});
            skLineSegment(sketch, "E881", {"start": v(-13.77, 62.33) * mm, "end": v(-13.82, 62.1) * mm});
            skLineSegment(sketch, "E882", {"start": v(-13.82, 62.1) * mm, "end": v(-13.87, 61.87) * mm});
            skLineSegment(sketch, "E883", {"start": v(-13.87, 61.87) * mm, "end": v(-13.92, 61.65) * mm});
            skLineSegment(sketch, "E884", {"start": v(-13.92, 61.65) * mm, "end": v(-13.97, 61.43) * mm});
            skLineSegment(sketch, "E885", {"start": v(-13.97, 61.43) * mm, "end": v(-14, 61.2) * mm});
            skLineSegment(sketch, "E886", {"start": v(-14, 61.2) * mm, "end": v(-14.05, 61) * mm});
            skLineSegment(sketch, "E887", {"start": v(-14.05, 61) * mm, "end": v(-14.08, 60.79) * mm});
            skLineSegment(sketch, "E888", {"start": v(-14.08, 60.79) * mm, "end": v(-14.12, 60.58) * mm});
            skLineSegment(sketch, "E889", {"start": v(-14.12, 60.58) * mm, "end": v(-14.15, 60.38) * mm});
            skLineSegment(sketch, "E890", {"start": v(-14.15, 60.38) * mm, "end": v(-14.18, 60.18) * mm});
            skLineSegment(sketch, "E891", {"start": v(-14.18, 60.18) * mm, "end": v(-14.2, 59.99) * mm});
            skLineSegment(sketch, "E892", {"start": v(-14.2, 59.99) * mm, "end": v(-14.23, 59.8) * mm});
            skLineSegment(sketch, "E893", {"start": v(-14.23, 59.8) * mm, "end": v(-14.25, 59.61) * mm});
            skLineSegment(sketch, "E894", {"start": v(-14.25, 59.61) * mm, "end": v(-14.27, 59.43) * mm});
            skLineSegment(sketch, "E895", {"start": v(-14.27, 59.43) * mm, "end": v(-14.3, 59.26) * mm});
            skLineSegment(sketch, "E896", {"start": v(-14.3, 59.26) * mm, "end": v(-14.3, 59.08) * mm});
            skLineSegment(sketch, "E897", {"start": v(-14.3, 59.08) * mm, "end": v(-14.32, 58.92) * mm});
            skLineSegment(sketch, "E898", {"start": v(-14.32, 58.92) * mm, "end": v(-14.34, 58.75) * mm});
            skLineSegment(sketch, "E899", {"start": v(-14.34, 58.75) * mm, "end": v(-14.35, 58.6) * mm});
            skArc(sketch, "E900", {"start": v(-14.35, 58.6) * mm, "mid": v(-15, 58.43) * mm, "end": v(-15.66, 58.26) * mm});
            skLineSegment(sketch, "E901", {"start": v(-15.66, 58.26) * mm, "end": v(-15.74, 58.4) * mm});
            skLineSegment(sketch, "E902", {"start": v(-15.74, 58.4) * mm, "end": v(-15.83, 58.53) * mm});
            skLineSegment(sketch, "E903", {"start": v(-15.83, 58.53) * mm, "end": v(-15.93, 58.67) * mm});
            skLineSegment(sketch, "E904", {"start": v(-15.93, 58.67) * mm, "end": v(-16.02, 58.81) * mm});
            skLineSegment(sketch, "E905", {"start": v(-16.02, 58.81) * mm, "end": v(-16.12, 58.96) * mm});
            skLineSegment(sketch, "E906", {"start": v(-16.12, 58.96) * mm, "end": v(-16.23, 59.1) * mm});
            skLineSegment(sketch, "E907", {"start": v(-16.23, 59.1) * mm, "end": v(-16.34, 59.26) * mm});
            skLineSegment(sketch, "E908", {"start": v(-16.34, 59.26) * mm, "end": v(-16.45, 59.41) * mm});
            skLineSegment(sketch, "E909", {"start": v(-16.45, 59.41) * mm, "end": v(-16.57, 59.57) * mm});
            skLineSegment(sketch, "E910", {"start": v(-16.57, 59.57) * mm, "end": v(-16.69, 59.73) * mm});
            skLineSegment(sketch, "E911", {"start": v(-16.69, 59.73) * mm, "end": v(-16.81, 59.89) * mm});
            skLineSegment(sketch, "E912", {"start": v(-16.81, 59.89) * mm, "end": v(-16.94, 60.05) * mm});
            skLineSegment(sketch, "E913", {"start": v(-16.94, 60.05) * mm, "end": v(-17.07, 60.22) * mm});
            skLineSegment(sketch, "E914", {"start": v(-17.07, 60.22) * mm, "end": v(-17.21, 60.39) * mm});
            skLineSegment(sketch, "E915", {"start": v(-17.21, 60.39) * mm, "end": v(-17.35, 60.56) * mm});
            skLineSegment(sketch, "E916", {"start": v(-17.35, 60.56) * mm, "end": v(-17.5, 60.73) * mm});
            skLineSegment(sketch, "E917", {"start": v(-17.5, 60.73) * mm, "end": v(-17.65, 60.9) * mm});
            skLineSegment(sketch, "E918", {"start": v(-17.65, 60.9) * mm, "end": v(-17.8, 61.08) * mm});
            skLineSegment(sketch, "E919", {"start": v(-17.8, 61.08) * mm, "end": v(-17.96, 61.26) * mm});
            skLineSegment(sketch, "E920", {"start": v(-17.96, 61.26) * mm, "end": v(-18.13, 61.44) * mm});
            skLineSegment(sketch, "E921", {"start": v(-18.13, 61.44) * mm, "end": v(-18.3, 61.62) * mm});
            skLineSegment(sketch, "E922", {"start": v(-18.3, 61.62) * mm, "end": v(-18.47, 61.8) * mm});
            skLineSegment(sketch, "E923", {"start": v(-18.47, 61.8) * mm, "end": v(-18.64, 61.99) * mm});
            skLineSegment(sketch, "E924", {"start": v(-18.64, 61.99) * mm, "end": v(-18.83, 62.17) * mm});
            skLineSegment(sketch, "E925", {"start": v(-18.83, 62.17) * mm, "end": v(-19.01, 62.36) * mm});
            skLineSegment(sketch, "E926", {"start": v(-19.01, 62.36) * mm, "end": v(-19.2, 62.55) * mm});
            skLineSegment(sketch, "E927", {"start": v(-19.2, 62.55) * mm, "end": v(-19.4, 62.74) * mm});
            skLineSegment(sketch, "E928", {"start": v(-19.4, 62.74) * mm, "end": v(-19.6, 62.94) * mm});
            skLineSegment(sketch, "E929", {"start": v(-19.6, 62.94) * mm, "end": v(-19.7, 63.03) * mm});
            skLineSegment(sketch, "E930", {"start": v(-19.7, 63.03) * mm, "end": v(-21.1, 62.58) * mm});
            skLineSegment(sketch, "E931", {"start": v(-21.1, 62.58) * mm, "end": v(-21.14, 62.44) * mm});
            skLineSegment(sketch, "E932", {"start": v(-21.14, 62.44) * mm, "end": v(-21.19, 62.16) * mm});
            skLineSegment(sketch, "E933", {"start": v(-21.19, 62.16) * mm, "end": v(-21.23, 61.9) * mm});
            skLineSegment(sketch, "E934", {"start": v(-21.23, 61.9) * mm, "end": v(-21.27, 61.63) * mm});
            skLineSegment(sketch, "E935", {"start": v(-21.27, 61.63) * mm, "end": v(-21.31, 61.37) * mm});
            skLineSegment(sketch, "E936", {"start": v(-21.31, 61.37) * mm, "end": v(-21.35, 61.1) * mm});
            skLineSegment(sketch, "E937", {"start": v(-21.35, 61.1) * mm, "end": v(-21.39, 60.85) * mm});
            skLineSegment(sketch, "E938", {"start": v(-21.39, 60.85) * mm, "end": v(-21.42, 60.6) * mm});
            skLineSegment(sketch, "E939", {"start": v(-21.42, 60.6) * mm, "end": v(-21.45, 60.36) * mm});
            skLineSegment(sketch, "E940", {"start": v(-21.45, 60.36) * mm, "end": v(-21.47, 60.12) * mm});
            skLineSegment(sketch, "E941", {"start": v(-21.47, 60.12) * mm, "end": v(-21.5, 59.88) * mm});
            skLineSegment(sketch, "E942", {"start": v(-21.5, 59.88) * mm, "end": v(-21.52, 59.64) * mm});
            skLineSegment(sketch, "E943", {"start": v(-21.52, 59.64) * mm, "end": v(-21.54, 59.42) * mm});
            skLineSegment(sketch, "E944", {"start": v(-21.54, 59.42) * mm, "end": v(-21.55, 59.2) * mm});
            skLineSegment(sketch, "E945", {"start": v(-21.55, 59.2) * mm, "end": v(-21.57, 58.97) * mm});
            skLineSegment(sketch, "E946", {"start": v(-21.57, 58.97) * mm, "end": v(-21.58, 58.75) * mm});
            skLineSegment(sketch, "E947", {"start": v(-21.58, 58.75) * mm, "end": v(-21.6, 58.54) * mm});
            skLineSegment(sketch, "E948", {"start": v(-21.6, 58.54) * mm, "end": v(-21.6, 58.33) * mm});
            skLineSegment(sketch, "E949", {"start": v(-21.6, 58.33) * mm, "end": v(-21.6, 58.13) * mm});
            skLineSegment(sketch, "E950", {"start": v(-21.6, 58.13) * mm, "end": v(-21.61, 57.93) * mm});
            skLineSegment(sketch, "E951", {"start": v(-21.61, 57.93) * mm, "end": v(-21.61, 57.73) * mm});
            skLineSegment(sketch, "E952", {"start": v(-21.61, 57.73) * mm, "end": v(-21.61, 57.54) * mm});
            skLineSegment(sketch, "E953", {"start": v(-21.61, 57.54) * mm, "end": v(-21.61, 57.36) * mm});
            skLineSegment(sketch, "E954", {"start": v(-21.61, 57.36) * mm, "end": v(-21.61, 57.18) * mm});
            skLineSegment(sketch, "E955", {"start": v(-21.61, 57.18) * mm, "end": v(-21.6, 57) * mm});
            skLineSegment(sketch, "E956", {"start": v(-21.6, 57) * mm, "end": v(-21.6, 56.83) * mm});
            skLineSegment(sketch, "E957", {"start": v(-21.6, 56.83) * mm, "end": v(-21.6, 56.66) * mm});
            skLineSegment(sketch, "E958", {"start": v(-21.6, 56.66) * mm, "end": v(-21.59, 56.5) * mm});
            skLineSegment(sketch, "E959", {"start": v(-21.59, 56.5) * mm, "end": v(-21.58, 56.33) * mm});
            skArc(sketch, "E960", {"start": v(-21.58, 56.33) * mm, "mid": v(-22.2, 56.09) * mm, "end": v(-22.83, 55.84) * mm});
            skLineSegment(sketch, "E961", {"start": v(-22.83, 55.84) * mm, "end": v(-22.94, 55.96) * mm});
            skLineSegment(sketch, "E962", {"start": v(-22.94, 55.96) * mm, "end": v(-23.04, 56.08) * mm});
            skLineSegment(sketch, "E963", {"start": v(-23.04, 56.08) * mm, "end": v(-23.15, 56.21) * mm});
            skLineSegment(sketch, "E964", {"start": v(-23.15, 56.21) * mm, "end": v(-23.27, 56.34) * mm});
            skLineSegment(sketch, "E965", {"start": v(-23.27, 56.34) * mm, "end": v(-23.39, 56.47) * mm});
            skLineSegment(sketch, "E966", {"start": v(-23.39, 56.47) * mm, "end": v(-23.5, 56.6) * mm});
            skLineSegment(sketch, "E967", {"start": v(-23.5, 56.6) * mm, "end": v(-23.64, 56.74) * mm});
            skLineSegment(sketch, "E968", {"start": v(-23.64, 56.74) * mm, "end": v(-23.77, 56.88) * mm});
            skLineSegment(sketch, "E969", {"start": v(-23.77, 56.88) * mm, "end": v(-23.9, 57.02) * mm});
            skLineSegment(sketch, "E970", {"start": v(-23.9, 57.02) * mm, "end": v(-24.04, 57.16) * mm});
            skLineSegment(sketch, "E971", {"start": v(-24.04, 57.16) * mm, "end": v(-24.19, 57.3) * mm});
            skLineSegment(sketch, "E972", {"start": v(-24.19, 57.3) * mm, "end": v(-24.33, 57.45) * mm});
            skLineSegment(sketch, "E973", {"start": v(-24.33, 57.45) * mm, "end": v(-24.49, 57.6) * mm});
            skLineSegment(sketch, "E974", {"start": v(-24.49, 57.6) * mm, "end": v(-24.64, 57.75) * mm});
            skLineSegment(sketch, "E975", {"start": v(-24.64, 57.75) * mm, "end": v(-24.8, 57.9) * mm});
            skLineSegment(sketch, "E976", {"start": v(-24.8, 57.9) * mm, "end": v(-24.97, 58.06) * mm});
            skLineSegment(sketch, "E977", {"start": v(-24.97, 58.06) * mm, "end": v(-25.14, 58.2) * mm});
            skLineSegment(sketch, "E978", {"start": v(-25.14, 58.2) * mm, "end": v(-25.32, 58.37) * mm});
            skLineSegment(sketch, "E979", {"start": v(-25.32, 58.37) * mm, "end": v(-25.5, 58.52) * mm});
            skLineSegment(sketch, "E980", {"start": v(-25.5, 58.52) * mm, "end": v(-25.68, 58.68) * mm});
            skLineSegment(sketch, "E981", {"start": v(-25.68, 58.68) * mm, "end": v(-25.87, 58.84) * mm});
            skLineSegment(sketch, "E982", {"start": v(-25.87, 58.84) * mm, "end": v(-26.07, 59) * mm});
            skLineSegment(sketch, "E983", {"start": v(-26.07, 59) * mm, "end": v(-26.27, 59.16) * mm});
            skLineSegment(sketch, "E984", {"start": v(-26.27, 59.16) * mm, "end": v(-26.47, 59.32) * mm});
            skLineSegment(sketch, "E985", {"start": v(-26.47, 59.32) * mm, "end": v(-26.68, 59.49) * mm});
            skLineSegment(sketch, "E986", {"start": v(-26.68, 59.49) * mm, "end": v(-26.9, 59.65) * mm});
            skLineSegment(sketch, "E987", {"start": v(-26.9, 59.65) * mm, "end": v(-27.11, 59.82) * mm});
            skLineSegment(sketch, "E988", {"start": v(-27.11, 59.82) * mm, "end": v(-27.33, 59.98) * mm});
            skLineSegment(sketch, "E989", {"start": v(-27.33, 59.98) * mm, "end": v(-27.45, 60.07) * mm});
            skLineSegment(sketch, "E990", {"start": v(-27.45, 60.07) * mm, "end": v(-28.79, 59.44) * mm});
            skLineSegment(sketch, "E991", {"start": v(-28.79, 59.44) * mm, "end": v(-28.8, 59.3) * mm});
            skLineSegment(sketch, "E992", {"start": v(-28.8, 59.3) * mm, "end": v(-28.8, 59.02) * mm});
            skLineSegment(sketch, "E993", {"start": v(-28.8, 59.02) * mm, "end": v(-28.82, 58.74) * mm});
            skLineSegment(sketch, "E994", {"start": v(-28.82, 58.74) * mm, "end": v(-28.83, 58.48) * mm});
            skLineSegment(sketch, "E995", {"start": v(-28.83, 58.48) * mm, "end": v(-28.84, 58.21) * mm});
            skLineSegment(sketch, "E996", {"start": v(-28.84, 58.21) * mm, "end": v(-28.84, 57.95) * mm});
            skLineSegment(sketch, "E997", {"start": v(-28.84, 57.95) * mm, "end": v(-28.85, 57.7) * mm});
            skLineSegment(sketch, "E998", {"start": v(-28.85, 57.7) * mm, "end": v(-28.85, 57.44) * mm});
            skLineSegment(sketch, "E999", {"start": v(-28.85, 57.44) * mm, "end": v(-28.84, 57.2) * mm});
            skLineSegment(sketch, "E1000", {"start": v(-28.84, 57.2) * mm, "end": v(-28.84, 56.95) * mm});
            skLineSegment(sketch, "E1001", {"start": v(-28.84, 56.95) * mm, "end": v(-28.83, 56.71) * mm});
            skLineSegment(sketch, "E1002", {"start": v(-28.83, 56.71) * mm, "end": v(-28.82, 56.48) * mm});
            skLineSegment(sketch, "E1003", {"start": v(-28.82, 56.48) * mm, "end": v(-28.82, 56.25) * mm});
            skLineSegment(sketch, "E1004", {"start": v(-28.82, 56.25) * mm, "end": v(-28.8, 56.02) * mm});
            skLineSegment(sketch, "E1005", {"start": v(-28.8, 56.02) * mm, "end": v(-28.79, 55.8) * mm});
            skLineSegment(sketch, "E1006", {"start": v(-28.79, 55.8) * mm, "end": v(-28.77, 55.58) * mm});
            skLineSegment(sketch, "E1007", {"start": v(-28.77, 55.58) * mm, "end": v(-28.76, 55.37) * mm});
            skLineSegment(sketch, "E1008", {"start": v(-28.76, 55.37) * mm, "end": v(-28.74, 55.17) * mm});
            skLineSegment(sketch, "E1009", {"start": v(-28.74, 55.17) * mm, "end": v(-28.72, 54.96) * mm});
            skLineSegment(sketch, "E1010", {"start": v(-28.72, 54.96) * mm, "end": v(-28.7, 54.76) * mm});
            skLineSegment(sketch, "E1011", {"start": v(-28.7, 54.76) * mm, "end": v(-28.68, 54.57) * mm});
            skLineSegment(sketch, "E1012", {"start": v(-28.68, 54.57) * mm, "end": v(-28.66, 54.38) * mm});
            skLineSegment(sketch, "E1013", {"start": v(-28.66, 54.38) * mm, "end": v(-28.63, 54.2) * mm});
            skLineSegment(sketch, "E1014", {"start": v(-28.63, 54.2) * mm, "end": v(-28.6, 54.02) * mm});
            skLineSegment(sketch, "E1015", {"start": v(-28.6, 54.02) * mm, "end": v(-28.58, 53.84) * mm});
            skLineSegment(sketch, "E1016", {"start": v(-28.58, 53.84) * mm, "end": v(-28.55, 53.67) * mm});
            skLineSegment(sketch, "E1017", {"start": v(-28.55, 53.67) * mm, "end": v(-28.52, 53.5) * mm});
            skLineSegment(sketch, "E1018", {"start": v(-28.52, 53.5) * mm, "end": v(-28.5, 53.34) * mm});
            skLineSegment(sketch, "E1019", {"start": v(-28.5, 53.34) * mm, "end": v(-28.47, 53.19) * mm});
            skArc(sketch, "E1020", {"start": v(-28.47, 53.19) * mm, "mid": v(-29.06, 52.86) * mm, "end": v(-29.65, 52.53) * mm});
            skLineSegment(sketch, "E1021", {"start": v(-29.65, 52.53) * mm, "end": v(-29.77, 52.64) * mm});
            skLineSegment(sketch, "E1022", {"start": v(-29.77, 52.64) * mm, "end": v(-29.9, 52.75) * mm});
            skLineSegment(sketch, "E1023", {"start": v(-29.9, 52.75) * mm, "end": v(-30.02, 52.87) * mm});
            skLineSegment(sketch, "E1024", {"start": v(-30.02, 52.87) * mm, "end": v(-30.15, 52.98) * mm});
            skLineSegment(sketch, "E1025", {"start": v(-30.15, 52.98) * mm, "end": v(-30.28, 53.1) * mm});
            skLineSegment(sketch, "E1026", {"start": v(-30.28, 53.1) * mm, "end": v(-30.42, 53.21) * mm});
            skLineSegment(sketch, "E1027", {"start": v(-30.42, 53.21) * mm, "end": v(-30.56, 53.33) * mm});
            skLineSegment(sketch, "E1028", {"start": v(-30.56, 53.33) * mm, "end": v(-30.7, 53.45) * mm});
            skLineSegment(sketch, "E1029", {"start": v(-30.7, 53.45) * mm, "end": v(-30.86, 53.58) * mm});
            skLineSegment(sketch, "E1030", {"start": v(-30.86, 53.58) * mm, "end": v(-31.02, 53.7) * mm});
            skLineSegment(sketch, "E1031", {"start": v(-31.02, 53.7) * mm, "end": v(-31.18, 53.83) * mm});
            skLineSegment(sketch, "E1032", {"start": v(-31.18, 53.83) * mm, "end": v(-31.34, 53.95) * mm});
            skLineSegment(sketch, "E1033", {"start": v(-31.34, 53.95) * mm, "end": v(-31.51, 54.08) * mm});
            skLineSegment(sketch, "E1034", {"start": v(-31.51, 54.08) * mm, "end": v(-31.69, 54.2) * mm});
            skLineSegment(sketch, "E1035", {"start": v(-31.69, 54.2) * mm, "end": v(-31.87, 54.34) * mm});
            skLineSegment(sketch, "E1036", {"start": v(-31.87, 54.34) * mm, "end": v(-32.05, 54.47) * mm});
            skLineSegment(sketch, "E1037", {"start": v(-32.05, 54.47) * mm, "end": v(-32.24, 54.6) * mm});
            skLineSegment(sketch, "E1038", {"start": v(-32.24, 54.6) * mm, "end": v(-32.43, 54.73) * mm});
            skLineSegment(sketch, "E1039", {"start": v(-32.43, 54.73) * mm, "end": v(-32.63, 54.87) * mm});
            skLineSegment(sketch, "E1040", {"start": v(-32.63, 54.87) * mm, "end": v(-32.84, 55) * mm});
            skLineSegment(sketch, "E1041", {"start": v(-32.84, 55) * mm, "end": v(-33.04, 55.13) * mm});
            skLineSegment(sketch, "E1042", {"start": v(-33.04, 55.13) * mm, "end": v(-33.26, 55.27) * mm});
            skLineSegment(sketch, "E1043", {"start": v(-33.26, 55.27) * mm, "end": v(-33.47, 55.4) * mm});
            skLineSegment(sketch, "E1044", {"start": v(-33.47, 55.4) * mm, "end": v(-33.7, 55.54) * mm});
            skLineSegment(sketch, "E1045", {"start": v(-33.7, 55.54) * mm, "end": v(-33.92, 55.68) * mm});
            skLineSegment(sketch, "E1046", {"start": v(-33.92, 55.68) * mm, "end": v(-34.16, 55.81) * mm});
            skLineSegment(sketch, "E1047", {"start": v(-34.16, 55.81) * mm, "end": v(-34.4, 55.95) * mm});
            skLineSegment(sketch, "E1048", {"start": v(-34.4, 55.95) * mm, "end": v(-34.64, 56.08) * mm});
            skLineSegment(sketch, "E1049", {"start": v(-34.64, 56.08) * mm, "end": v(-34.76, 56.15) * mm});
            skLineSegment(sketch, "E1050", {"start": v(-34.76, 56.15) * mm, "end": v(-36, 55.36) * mm});
            skLineSegment(sketch, "E1051", {"start": v(-36, 55.36) * mm, "end": v(-36, 55.22) * mm});
            skLineSegment(sketch, "E1052", {"start": v(-36, 55.22) * mm, "end": v(-35.98, 54.94) * mm});
            skLineSegment(sketch, "E1053", {"start": v(-35.98, 54.94) * mm, "end": v(-35.96, 54.67) * mm});
            skLineSegment(sketch, "E1054", {"start": v(-35.96, 54.67) * mm, "end": v(-35.93, 54.4) * mm});
            skLineSegment(sketch, "E1055", {"start": v(-35.93, 54.4) * mm, "end": v(-35.9, 54.14) * mm});
            skLineSegment(sketch, "E1056", {"start": v(-35.9, 54.14) * mm, "end": v(-35.88, 53.88) * mm});
            skLineSegment(sketch, "E1057", {"start": v(-35.88, 53.88) * mm, "end": v(-35.85, 53.62) * mm});
            skLineSegment(sketch, "E1058", {"start": v(-35.85, 53.62) * mm, "end": v(-35.82, 53.37) * mm});
            skLineSegment(sketch, "E1059", {"start": v(-35.82, 53.37) * mm, "end": v(-35.78, 53.13) * mm});
            skLineSegment(sketch, "E1060", {"start": v(-35.78, 53.13) * mm, "end": v(-35.75, 52.89) * mm});
            skLineSegment(sketch, "E1061", {"start": v(-35.75, 52.89) * mm, "end": v(-35.71, 52.65) * mm});
            skLineSegment(sketch, "E1062", {"start": v(-35.71, 52.65) * mm, "end": v(-35.68, 52.42) * mm});
            skLineSegment(sketch, "E1063", {"start": v(-35.68, 52.42) * mm, "end": v(-35.64, 52.2) * mm});
            skLineSegment(sketch, "E1064", {"start": v(-35.64, 52.2) * mm, "end": v(-35.6, 51.97) * mm});
            skLineSegment(sketch, "E1065", {"start": v(-35.6, 51.97) * mm, "end": v(-35.56, 51.75) * mm});
            skLineSegment(sketch, "E1066", {"start": v(-35.56, 51.75) * mm, "end": v(-35.51, 51.54) * mm});
            skLineSegment(sketch, "E1067", {"start": v(-35.51, 51.54) * mm, "end": v(-35.47, 51.33) * mm});
            skLineSegment(sketch, "E1068", {"start": v(-35.47, 51.33) * mm, "end": v(-35.43, 51.13) * mm});
            skLineSegment(sketch, "E1069", {"start": v(-35.43, 51.13) * mm, "end": v(-35.38, 50.93) * mm});
            skLineSegment(sketch, "E1070", {"start": v(-35.38, 50.93) * mm, "end": v(-35.34, 50.74) * mm});
            skLineSegment(sketch, "E1071", {"start": v(-35.34, 50.74) * mm, "end": v(-35.3, 50.55) * mm});
            skLineSegment(sketch, "E1072", {"start": v(-35.3, 50.55) * mm, "end": v(-35.24, 50.36) * mm});
            skLineSegment(sketch, "E1073", {"start": v(-35.24, 50.36) * mm, "end": v(-35.2, 50.18) * mm});
            skLineSegment(sketch, "E1074", {"start": v(-35.2, 50.18) * mm, "end": v(-35.15, 50) * mm});
            skLineSegment(sketch, "E1075", {"start": v(-35.15, 50) * mm, "end": v(-35.1, 49.83) * mm});
            skLineSegment(sketch, "E1076", {"start": v(-35.1, 49.83) * mm, "end": v(-35.05, 49.67) * mm});
            skLineSegment(sketch, "E1077", {"start": v(-35.05, 49.67) * mm, "end": v(-35, 49.5) * mm});
            skLineSegment(sketch, "E1078", {"start": v(-35, 49.5) * mm, "end": v(-34.96, 49.35) * mm});
            skLineSegment(sketch, "E1079", {"start": v(-34.96, 49.35) * mm, "end": v(-34.9, 49.2) * mm});
            skArc(sketch, "E1080", {"start": v(-34.9, 49.2) * mm, "mid": v(-35.46, 48.8) * mm, "end": v(-36, 48.4) * mm});
            skLineSegment(sketch, "E1081", {"start": v(-36, 48.4) * mm, "end": v(-36.13, 48.5) * mm});
            skLineSegment(sketch, "E1082", {"start": v(-36.13, 48.5) * mm, "end": v(-36.27, 48.6) * mm});
            skLineSegment(sketch, "E1083", {"start": v(-36.27, 48.6) * mm, "end": v(-36.4, 48.69) * mm});
            skLineSegment(sketch, "E1084", {"start": v(-36.4, 48.69) * mm, "end": v(-36.55, 48.78) * mm});
            skLineSegment(sketch, "E1085", {"start": v(-36.55, 48.78) * mm, "end": v(-36.7, 48.88) * mm});
            skLineSegment(sketch, "E1086", {"start": v(-36.7, 48.88) * mm, "end": v(-36.85, 48.98) * mm});
            skLineSegment(sketch, "E1087", {"start": v(-36.85, 48.98) * mm, "end": v(-37, 49.08) * mm});
            skLineSegment(sketch, "E1088", {"start": v(-37, 49.08) * mm, "end": v(-37.17, 49.18) * mm});
            skLineSegment(sketch, "E1089", {"start": v(-37.17, 49.18) * mm, "end": v(-37.33, 49.29) * mm});
            skLineSegment(sketch, "E1090", {"start": v(-37.33, 49.29) * mm, "end": v(-37.5, 49.39) * mm});
            skLineSegment(sketch, "E1091", {"start": v(-37.5, 49.39) * mm, "end": v(-37.68, 49.5) * mm});
            skLineSegment(sketch, "E1092", {"start": v(-37.68, 49.5) * mm, "end": v(-37.86, 49.6) * mm});
            skLineSegment(sketch, "E1093", {"start": v(-37.86, 49.6) * mm, "end": v(-38.04, 49.7) * mm});
            skLineSegment(sketch, "E1094", {"start": v(-38.04, 49.7) * mm, "end": v(-38.23, 49.8) * mm});
            skLineSegment(sketch, "E1095", {"start": v(-38.23, 49.8) * mm, "end": v(-38.43, 49.92) * mm});
            skLineSegment(sketch, "E1096", {"start": v(-38.43, 49.92) * mm, "end": v(-38.63, 50.02) * mm});
            skLineSegment(sketch, "E1097", {"start": v(-38.63, 50.02) * mm, "end": v(-38.83, 50.13) * mm});
            skLineSegment(sketch, "E1098", {"start": v(-38.83, 50.13) * mm, "end": v(-39.04, 50.24) * mm});
            skLineSegment(sketch, "E1099", {"start": v(-39.04, 50.24) * mm, "end": v(-39.25, 50.34) * mm});
            skLineSegment(sketch, "E1100", {"start": v(-39.25, 50.34) * mm, "end": v(-39.47, 50.45) * mm});
            skLineSegment(sketch, "E1101", {"start": v(-39.47, 50.45) * mm, "end": v(-39.7, 50.56) * mm});
            skLineSegment(sketch, "E1102", {"start": v(-39.7, 50.56) * mm, "end": v(-39.92, 50.66) * mm});
            skLineSegment(sketch, "E1103", {"start": v(-39.92, 50.66) * mm, "end": v(-40.15, 50.77) * mm});
            skLineSegment(sketch, "E1104", {"start": v(-40.15, 50.77) * mm, "end": v(-40.4, 50.88) * mm});
            skLineSegment(sketch, "E1105", {"start": v(-40.4, 50.88) * mm, "end": v(-40.63, 50.98) * mm});
            skLineSegment(sketch, "E1106", {"start": v(-40.63, 50.98) * mm, "end": v(-40.88, 51.1) * mm});
            skLineSegment(sketch, "E1107", {"start": v(-40.88, 51.1) * mm, "end": v(-41.14, 51.2) * mm});
            skLineSegment(sketch, "E1108", {"start": v(-41.14, 51.2) * mm, "end": v(-41.4, 51.3) * mm});
            skLineSegment(sketch, "E1109", {"start": v(-41.4, 51.3) * mm, "end": v(-41.52, 51.35) * mm});
            skLineSegment(sketch, "E1110", {"start": v(-41.52, 51.35) * mm, "end": v(-42.66, 50.41) * mm});
            skLineSegment(sketch, "E1111", {"start": v(-42.66, 50.41) * mm, "end": v(-42.64, 50.27) * mm});
            skLineSegment(sketch, "E1112", {"start": v(-42.64, 50.27) * mm, "end": v(-42.58, 50) * mm});
            skLineSegment(sketch, "E1113", {"start": v(-42.58, 50) * mm, "end": v(-42.53, 49.73) * mm});
            skLineSegment(sketch, "E1114", {"start": v(-42.53, 49.73) * mm, "end": v(-42.47, 49.47) * mm});
            skLineSegment(sketch, "E1115", {"start": v(-42.47, 49.47) * mm, "end": v(-42.4, 49.2) * mm});
            skLineSegment(sketch, "E1116", {"start": v(-42.4, 49.2) * mm, "end": v(-42.35, 48.96) * mm});
            skLineSegment(sketch, "E1117", {"start": v(-42.35, 48.96) * mm, "end": v(-42.29, 48.7) * mm});
            skLineSegment(sketch, "E1118", {"start": v(-42.29, 48.7) * mm, "end": v(-42.22, 48.46) * mm});
            skLineSegment(sketch, "E1119", {"start": v(-42.22, 48.46) * mm, "end": v(-42.16, 48.22) * mm});
            skLineSegment(sketch, "E1120", {"start": v(-42.16, 48.22) * mm, "end": v(-42.1, 47.99) * mm});
            skLineSegment(sketch, "E1121", {"start": v(-42.1, 47.99) * mm, "end": v(-42.03, 47.76) * mm});
            skLineSegment(sketch, "E1122", {"start": v(-42.03, 47.76) * mm, "end": v(-41.96, 47.53) * mm});
            skLineSegment(sketch, "E1123", {"start": v(-41.96, 47.53) * mm, "end": v(-41.9, 47.31) * mm});
            skLineSegment(sketch, "E1124", {"start": v(-41.9, 47.31) * mm, "end": v(-41.83, 47.1) * mm});
            skLineSegment(sketch, "E1125", {"start": v(-41.83, 47.1) * mm, "end": v(-41.76, 46.89) * mm});
            skLineSegment(sketch, "E1126", {"start": v(-41.76, 46.89) * mm, "end": v(-41.7, 46.68) * mm});
            skLineSegment(sketch, "E1127", {"start": v(-41.7, 46.68) * mm, "end": v(-41.63, 46.48) * mm});
            skLineSegment(sketch, "E1128", {"start": v(-41.63, 46.48) * mm, "end": v(-41.56, 46.28) * mm});
            skLineSegment(sketch, "E1129", {"start": v(-41.56, 46.28) * mm, "end": v(-41.49, 46.1) * mm});
            skLineSegment(sketch, "E1130", {"start": v(-41.49, 46.1) * mm, "end": v(-41.42, 45.9) * mm});
            skLineSegment(sketch, "E1131", {"start": v(-41.42, 45.9) * mm, "end": v(-41.35, 45.72) * mm});
            skLineSegment(sketch, "E1132", {"start": v(-41.35, 45.72) * mm, "end": v(-41.28, 45.55) * mm});
            skLineSegment(sketch, "E1133", {"start": v(-41.28, 45.55) * mm, "end": v(-41.2, 45.37) * mm});
            skLineSegment(sketch, "E1134", {"start": v(-41.2, 45.37) * mm, "end": v(-41.14, 45.2) * mm});
            skLineSegment(sketch, "E1135", {"start": v(-41.14, 45.2) * mm, "end": v(-41.07, 45.04) * mm});
            skLineSegment(sketch, "E1136", {"start": v(-41.07, 45.04) * mm, "end": v(-41, 44.88) * mm});
            skLineSegment(sketch, "E1137", {"start": v(-41, 44.88) * mm, "end": v(-40.93, 44.73) * mm});
            skLineSegment(sketch, "E1138", {"start": v(-40.93, 44.73) * mm, "end": v(-40.87, 44.58) * mm});
            skLineSegment(sketch, "E1139", {"start": v(-40.87, 44.58) * mm, "end": v(-40.8, 44.43) * mm});
            skArc(sketch, "E1140", {"start": v(-40.8, 44.43) * mm, "mid": v(-41.3, 43.97) * mm, "end": v(-41.79, 43.5) * mm});
            skLineSegment(sketch, "E1141", {"start": v(-41.79, 43.5) * mm, "end": v(-41.92, 43.59) * mm});
            skLineSegment(sketch, "E1142", {"start": v(-41.92, 43.59) * mm, "end": v(-42.07, 43.66) * mm});
            skLineSegment(sketch, "E1143", {"start": v(-42.07, 43.66) * mm, "end": v(-42.22, 43.74) * mm});
            skLineSegment(sketch, "E1144", {"start": v(-42.22, 43.74) * mm, "end": v(-42.37, 43.82) * mm});
            skLineSegment(sketch, "E1145", {"start": v(-42.37, 43.82) * mm, "end": v(-42.53, 43.9) * mm});
            skLineSegment(sketch, "E1146", {"start": v(-42.53, 43.9) * mm, "end": v(-42.7, 43.98) * mm});
            skLineSegment(sketch, "E1147", {"start": v(-42.7, 43.98) * mm, "end": v(-42.86, 44.06) * mm});
            skLineSegment(sketch, "E1148", {"start": v(-42.86, 44.06) * mm, "end": v(-43.04, 44.14) * mm});
            skLineSegment(sketch, "E1149", {"start": v(-43.04, 44.14) * mm, "end": v(-43.22, 44.22) * mm});
            skLineSegment(sketch, "E1150", {"start": v(-43.22, 44.22) * mm, "end": v(-43.4, 44.3) * mm});
            skLineSegment(sketch, "E1151", {"start": v(-43.4, 44.3) * mm, "end": v(-43.58, 44.38) * mm});
            skLineSegment(sketch, "E1152", {"start": v(-43.58, 44.38) * mm, "end": v(-43.78, 44.46) * mm});
            skLineSegment(sketch, "E1153", {"start": v(-43.78, 44.46) * mm, "end": v(-43.97, 44.54) * mm});
            skLineSegment(sketch, "E1154", {"start": v(-43.97, 44.54) * mm, "end": v(-44.17, 44.62) * mm});
            skLineSegment(sketch, "E1155", {"start": v(-44.17, 44.62) * mm, "end": v(-44.38, 44.7) * mm});
            skLineSegment(sketch, "E1156", {"start": v(-44.38, 44.7) * mm, "end": v(-44.6, 44.79) * mm});
            skLineSegment(sketch, "E1157", {"start": v(-44.6, 44.79) * mm, "end": v(-44.8, 44.87) * mm});
            skLineSegment(sketch, "E1158", {"start": v(-44.8, 44.87) * mm, "end": v(-45.03, 44.95) * mm});
            skLineSegment(sketch, "E1159", {"start": v(-45.03, 44.95) * mm, "end": v(-45.25, 45.03) * mm});
            skLineSegment(sketch, "E1160", {"start": v(-45.25, 45.03) * mm, "end": v(-45.48, 45.1) * mm});
            skLineSegment(sketch, "E1161", {"start": v(-45.48, 45.1) * mm, "end": v(-45.72, 45.18) * mm});
            skLineSegment(sketch, "E1162", {"start": v(-45.72, 45.18) * mm, "end": v(-45.96, 45.26) * mm});
            skLineSegment(sketch, "E1163", {"start": v(-45.96, 45.26) * mm, "end": v(-46.2, 45.34) * mm});
            skLineSegment(sketch, "E1164", {"start": v(-46.2, 45.34) * mm, "end": v(-46.45, 45.41) * mm});
            skLineSegment(sketch, "E1165", {"start": v(-46.45, 45.41) * mm, "end": v(-46.7, 45.49) * mm});
            skLineSegment(sketch, "E1166", {"start": v(-46.7, 45.49) * mm, "end": v(-46.96, 45.56) * mm});
            skLineSegment(sketch, "E1167", {"start": v(-46.96, 45.56) * mm, "end": v(-47.23, 45.64) * mm});
            skLineSegment(sketch, "E1168", {"start": v(-47.23, 45.64) * mm, "end": v(-47.5, 45.7) * mm});
            skLineSegment(sketch, "E1169", {"start": v(-47.5, 45.7) * mm, "end": v(-47.63, 45.74) * mm});
            skLineSegment(sketch, "E1170", {"start": v(-47.63, 45.74) * mm, "end": v(-48.64, 44.67) * mm});
            skLineSegment(sketch, "E1171", {"start": v(-48.64, 44.67) * mm, "end": v(-48.6, 44.53) * mm});
            skLineSegment(sketch, "E1172", {"start": v(-48.6, 44.53) * mm, "end": v(-48.51, 44.27) * mm});
            skLineSegment(sketch, "E1173", {"start": v(-48.51, 44.27) * mm, "end": v(-48.42, 44) * mm});
            skLineSegment(sketch, "E1174", {"start": v(-48.42, 44) * mm, "end": v(-48.33, 43.76) * mm});
            skLineSegment(sketch, "E1175", {"start": v(-48.33, 43.76) * mm, "end": v(-48.24, 43.5) * mm});
            skLineSegment(sketch, "E1176", {"start": v(-48.24, 43.5) * mm, "end": v(-48.15, 43.26) * mm});
            skLineSegment(sketch, "E1177", {"start": v(-48.15, 43.26) * mm, "end": v(-48.06, 43.02) * mm});
            skLineSegment(sketch, "E1178", {"start": v(-48.06, 43.02) * mm, "end": v(-47.97, 42.79) * mm});
            skLineSegment(sketch, "E1179", {"start": v(-47.97, 42.79) * mm, "end": v(-47.87, 42.56) * mm});
            skLineSegment(sketch, "E1180", {"start": v(-47.87, 42.56) * mm, "end": v(-47.78, 42.33) * mm});
            skLineSegment(sketch, "E1181", {"start": v(-47.78, 42.33) * mm, "end": v(-47.69, 42.12) * mm});
            skLineSegment(sketch, "E1182", {"start": v(-47.69, 42.12) * mm, "end": v(-47.6, 41.9) * mm});
            skLineSegment(sketch, "E1183", {"start": v(-47.6, 41.9) * mm, "end": v(-47.5, 41.7) * mm});
            skLineSegment(sketch, "E1184", {"start": v(-47.5, 41.7) * mm, "end": v(-47.4, 41.48) * mm});
            skLineSegment(sketch, "E1185", {"start": v(-47.4, 41.48) * mm, "end": v(-47.31, 41.28) * mm});
            skLineSegment(sketch, "E1186", {"start": v(-47.31, 41.28) * mm, "end": v(-47.22, 41.09) * mm});
            skLineSegment(sketch, "E1187", {"start": v(-47.22, 41.09) * mm, "end": v(-47.12, 40.9) * mm});
            skLineSegment(sketch, "E1188", {"start": v(-47.12, 40.9) * mm, "end": v(-47.03, 40.71) * mm});
            skLineSegment(sketch, "E1189", {"start": v(-47.03, 40.71) * mm, "end": v(-46.94, 40.53) * mm});
            skLineSegment(sketch, "E1190", {"start": v(-46.94, 40.53) * mm, "end": v(-46.84, 40.35) * mm});
            skLineSegment(sketch, "E1191", {"start": v(-46.84, 40.35) * mm, "end": v(-46.75, 40.18) * mm});
            skLineSegment(sketch, "E1192", {"start": v(-46.75, 40.18) * mm, "end": v(-46.66, 40.01) * mm});
            skLineSegment(sketch, "E1193", {"start": v(-46.66, 40.01) * mm, "end": v(-46.57, 39.85) * mm});
            skLineSegment(sketch, "E1194", {"start": v(-46.57, 39.85) * mm, "end": v(-46.48, 39.7) * mm});
            skLineSegment(sketch, "E1195", {"start": v(-46.48, 39.7) * mm, "end": v(-46.4, 39.54) * mm});
            skLineSegment(sketch, "E1196", {"start": v(-46.4, 39.54) * mm, "end": v(-46.3, 39.39) * mm});
            skLineSegment(sketch, "E1197", {"start": v(-46.3, 39.39) * mm, "end": v(-46.22, 39.25) * mm});
            skLineSegment(sketch, "E1198", {"start": v(-46.22, 39.25) * mm, "end": v(-46.13, 39.1) * mm});
            skLineSegment(sketch, "E1199", {"start": v(-46.13, 39.1) * mm, "end": v(-46.05, 38.97) * mm});
            skArc(sketch, "E1200", {"start": v(-46.05, 38.97) * mm, "mid": v(-46.48, 38.45) * mm, "end": v(-46.9, 37.93) * mm});
            skLineSegment(sketch, "E1201", {"start": v(-46.9, 37.93) * mm, "end": v(-47.06, 37.99) * mm});
            skLineSegment(sketch, "E1202", {"start": v(-47.06, 37.99) * mm, "end": v(-47.21, 38.05) * mm});
            skLineSegment(sketch, "E1203", {"start": v(-47.21, 38.05) * mm, "end": v(-47.37, 38.1) * mm});
            skLineSegment(sketch, "E1204", {"start": v(-47.37, 38.1) * mm, "end": v(-47.53, 38.16) * mm});
            skLineSegment(sketch, "E1205", {"start": v(-47.53, 38.16) * mm, "end": v(-47.7, 38.22) * mm});
            skLineSegment(sketch, "E1206", {"start": v(-47.7, 38.22) * mm, "end": v(-47.87, 38.28) * mm});
            skLineSegment(sketch, "E1207", {"start": v(-47.87, 38.28) * mm, "end": v(-48.05, 38.34) * mm});
            skLineSegment(sketch, "E1208", {"start": v(-48.05, 38.34) * mm, "end": v(-48.23, 38.4) * mm});
            skLineSegment(sketch, "E1209", {"start": v(-48.23, 38.4) * mm, "end": v(-48.42, 38.45) * mm});
            skLineSegment(sketch, "E1210", {"start": v(-48.42, 38.45) * mm, "end": v(-48.6, 38.51) * mm});
            skLineSegment(sketch, "E1211", {"start": v(-48.6, 38.51) * mm, "end": v(-48.8, 38.57) * mm});
            skLineSegment(sketch, "E1212", {"start": v(-48.8, 38.57) * mm, "end": v(-49, 38.62) * mm});
            skLineSegment(sketch, "E1213", {"start": v(-49, 38.62) * mm, "end": v(-49.2, 38.68) * mm});
            skLineSegment(sketch, "E1214", {"start": v(-49.2, 38.68) * mm, "end": v(-49.42, 38.74) * mm});
            skLineSegment(sketch, "E1215", {"start": v(-49.42, 38.74) * mm, "end": v(-49.63, 38.8) * mm});
            skLineSegment(sketch, "E1216", {"start": v(-49.63, 38.8) * mm, "end": v(-49.85, 38.84) * mm});
            skLineSegment(sketch, "E1217", {"start": v(-49.85, 38.84) * mm, "end": v(-50.08, 38.9) * mm});
            skLineSegment(sketch, "E1218", {"start": v(-50.08, 38.9) * mm, "end": v(-50.3, 38.95) * mm});
            skLineSegment(sketch, "E1219", {"start": v(-50.3, 38.95) * mm, "end": v(-50.54, 39) * mm});
            skLineSegment(sketch, "E1220", {"start": v(-50.54, 39) * mm, "end": v(-50.78, 39.05) * mm});
            skLineSegment(sketch, "E1221", {"start": v(-50.78, 39.05) * mm, "end": v(-51.02, 39.1) * mm});
            skLineSegment(sketch, "E1222", {"start": v(-51.02, 39.1) * mm, "end": v(-51.27, 39.14) * mm});
            skLineSegment(sketch, "E1223", {"start": v(-51.27, 39.14) * mm, "end": v(-51.52, 39.2) * mm});
            skLineSegment(sketch, "E1224", {"start": v(-51.52, 39.2) * mm, "end": v(-51.78, 39.23) * mm});
            skLineSegment(sketch, "E1225", {"start": v(-51.78, 39.23) * mm, "end": v(-52.04, 39.28) * mm});
            skLineSegment(sketch, "E1226", {"start": v(-52.04, 39.28) * mm, "end": v(-52.3, 39.32) * mm});
            skLineSegment(sketch, "E1227", {"start": v(-52.3, 39.32) * mm, "end": v(-52.57, 39.36) * mm});
            skLineSegment(sketch, "E1228", {"start": v(-52.57, 39.36) * mm, "end": v(-52.85, 39.4) * mm});
            skLineSegment(sketch, "E1229", {"start": v(-52.85, 39.4) * mm, "end": v(-52.99, 39.41) * mm});
            skLineSegment(sketch, "E1230", {"start": v(-52.99, 39.41) * mm, "end": v(-53.86, 38.22) * mm});
            skLineSegment(sketch, "E1231", {"start": v(-53.86, 38.22) * mm, "end": v(-53.8, 38.09) * mm});
            skLineSegment(sketch, "E1232", {"start": v(-53.8, 38.09) * mm, "end": v(-53.68, 37.84) * mm});
            skLineSegment(sketch, "E1233", {"start": v(-53.68, 37.84) * mm, "end": v(-53.56, 37.6) * mm});
            skLineSegment(sketch, "E1234", {"start": v(-53.56, 37.6) * mm, "end": v(-53.44, 37.35) * mm});
            skLineSegment(sketch, "E1235", {"start": v(-53.44, 37.35) * mm, "end": v(-53.31, 37.12) * mm});
            skLineSegment(sketch, "E1236", {"start": v(-53.31, 37.12) * mm, "end": v(-53.2, 36.89) * mm});
            skLineSegment(sketch, "E1237", {"start": v(-53.2, 36.89) * mm, "end": v(-53.07, 36.66) * mm});
            skLineSegment(sketch, "E1238", {"start": v(-53.07, 36.66) * mm, "end": v(-52.95, 36.44) * mm});
            skLineSegment(sketch, "E1239", {"start": v(-52.95, 36.44) * mm, "end": v(-52.83, 36.22) * mm});
            skLineSegment(sketch, "E1240", {"start": v(-52.83, 36.22) * mm, "end": v(-52.7, 36.01) * mm});
            skLineSegment(sketch, "E1241", {"start": v(-52.7, 36.01) * mm, "end": v(-52.59, 35.8) * mm});
            skLineSegment(sketch, "E1242", {"start": v(-52.59, 35.8) * mm, "end": v(-52.47, 35.6) * mm});
            skLineSegment(sketch, "E1243", {"start": v(-52.47, 35.6) * mm, "end": v(-52.35, 35.4) * mm});
            skLineSegment(sketch, "E1244", {"start": v(-52.35, 35.4) * mm, "end": v(-52.23, 35.22) * mm});
            skLineSegment(sketch, "E1245", {"start": v(-52.23, 35.22) * mm, "end": v(-52.11, 35.03) * mm});
            skLineSegment(sketch, "E1246", {"start": v(-52.11, 35.03) * mm, "end": v(-52, 34.85) * mm});
            skLineSegment(sketch, "E1247", {"start": v(-52, 34.85) * mm, "end": v(-51.88, 34.67) * mm});
            skLineSegment(sketch, "E1248", {"start": v(-51.88, 34.67) * mm, "end": v(-51.76, 34.5) * mm});
            skLineSegment(sketch, "E1249", {"start": v(-51.76, 34.5) * mm, "end": v(-51.65, 34.33) * mm});
            skLineSegment(sketch, "E1250", {"start": v(-51.65, 34.33) * mm, "end": v(-51.53, 34.16) * mm});
            skLineSegment(sketch, "E1251", {"start": v(-51.53, 34.16) * mm, "end": v(-51.42, 34) * mm});
            skLineSegment(sketch, "E1252", {"start": v(-51.42, 34) * mm, "end": v(-51.3, 33.85) * mm});
            skLineSegment(sketch, "E1253", {"start": v(-51.3, 33.85) * mm, "end": v(-51.2, 33.7) * mm});
            skLineSegment(sketch, "E1254", {"start": v(-51.2, 33.7) * mm, "end": v(-51.09, 33.55) * mm});
            skLineSegment(sketch, "E1255", {"start": v(-51.09, 33.55) * mm, "end": v(-50.98, 33.41) * mm});
            skLineSegment(sketch, "E1256", {"start": v(-50.98, 33.41) * mm, "end": v(-50.88, 33.28) * mm});
            skLineSegment(sketch, "E1257", {"start": v(-50.88, 33.28) * mm, "end": v(-50.77, 33.14) * mm});
            skLineSegment(sketch, "E1258", {"start": v(-50.77, 33.14) * mm, "end": v(-50.67, 33.02) * mm});
            skLineSegment(sketch, "E1259", {"start": v(-50.67, 33.02) * mm, "end": v(-50.57, 32.9) * mm});
            skArc(sketch, "E1260", {"start": v(-50.57, 32.9) * mm, "mid": v(-50.93, 32.32) * mm, "end": v(-51.3, 31.75) * mm});
            skLineSegment(sketch, "E1261", {"start": v(-51.3, 31.75) * mm, "end": v(-51.45, 31.79) * mm});
            skLineSegment(sketch, "E1262", {"start": v(-51.45, 31.79) * mm, "end": v(-51.6, 31.83) * mm});
            skLineSegment(sketch, "E1263", {"start": v(-51.6, 31.83) * mm, "end": v(-51.77, 31.87) * mm});
            skLineSegment(sketch, "E1264", {"start": v(-51.77, 31.87) * mm, "end": v(-51.94, 31.9) * mm});
            skLineSegment(sketch, "E1265", {"start": v(-51.94, 31.9) * mm, "end": v(-52.11, 31.94) * mm});
            skLineSegment(sketch, "E1266", {"start": v(-52.11, 31.94) * mm, "end": v(-52.3, 31.98) * mm});
            skLineSegment(sketch, "E1267", {"start": v(-52.3, 31.98) * mm, "end": v(-52.47, 32.01) * mm});
            skLineSegment(sketch, "E1268", {"start": v(-52.47, 32.01) * mm, "end": v(-52.66, 32.05) * mm});
            skLineSegment(sketch, "E1269", {"start": v(-52.66, 32.05) * mm, "end": v(-52.85, 32.08) * mm});
            skLineSegment(sketch, "E1270", {"start": v(-52.85, 32.08) * mm, "end": v(-53.05, 32.12) * mm});
            skLineSegment(sketch, "E1271", {"start": v(-53.05, 32.12) * mm, "end": v(-53.25, 32.15) * mm});
            skLineSegment(sketch, "E1272", {"start": v(-53.25, 32.15) * mm, "end": v(-53.46, 32.18) * mm});
            skLineSegment(sketch, "E1273", {"start": v(-53.46, 32.18) * mm, "end": v(-53.67, 32.2) * mm});
            skLineSegment(sketch, "E1274", {"start": v(-53.67, 32.2) * mm, "end": v(-53.88, 32.24) * mm});
            skLineSegment(sketch, "E1275", {"start": v(-53.88, 32.24) * mm, "end": v(-54.1, 32.26) * mm});
            skLineSegment(sketch, "E1276", {"start": v(-54.1, 32.26) * mm, "end": v(-54.33, 32.29) * mm});
            skLineSegment(sketch, "E1277", {"start": v(-54.33, 32.29) * mm, "end": v(-54.56, 32.31) * mm});
            skLineSegment(sketch, "E1278", {"start": v(-54.56, 32.31) * mm, "end": v(-54.79, 32.34) * mm});
            skLineSegment(sketch, "E1279", {"start": v(-54.79, 32.34) * mm, "end": v(-55.03, 32.36) * mm});
            skLineSegment(sketch, "E1280", {"start": v(-55.03, 32.36) * mm, "end": v(-55.27, 32.38) * mm});
            skLineSegment(sketch, "E1281", {"start": v(-55.27, 32.38) * mm, "end": v(-55.52, 32.4) * mm});
            skLineSegment(sketch, "E1282", {"start": v(-55.52, 32.4) * mm, "end": v(-55.77, 32.41) * mm});
            skLineSegment(sketch, "E1283", {"start": v(-55.77, 32.41) * mm, "end": v(-56.02, 32.42) * mm});
            skLineSegment(sketch, "E1284", {"start": v(-56.02, 32.42) * mm, "end": v(-56.28, 32.44) * mm});
            skLineSegment(sketch, "E1285", {"start": v(-56.28, 32.44) * mm, "end": v(-56.55, 32.45) * mm});
            skLineSegment(sketch, "E1286", {"start": v(-56.55, 32.45) * mm, "end": v(-56.82, 32.45) * mm});
            skLineSegment(sketch, "E1287", {"start": v(-56.82, 32.45) * mm, "end": v(-57.1, 32.46) * mm});
            skLineSegment(sketch, "E1288", {"start": v(-57.1, 32.46) * mm, "end": v(-57.37, 32.46) * mm});
            skLineSegment(sketch, "E1289", {"start": v(-57.37, 32.46) * mm, "end": v(-57.51, 32.46) * mm});
            skLineSegment(sketch, "E1290", {"start": v(-57.51, 32.46) * mm, "end": v(-58.22, 31.16) * mm});
            skLineSegment(sketch, "E1291", {"start": v(-58.22, 31.16) * mm, "end": v(-58.15, 31.05) * mm});
            skLineSegment(sketch, "E1292", {"start": v(-58.15, 31.05) * mm, "end": v(-58, 30.81) * mm});
            skLineSegment(sketch, "E1293", {"start": v(-58, 30.81) * mm, "end": v(-57.85, 30.58) * mm});
            skLineSegment(sketch, "E1294", {"start": v(-57.85, 30.58) * mm, "end": v(-57.7, 30.36) * mm});
            skLineSegment(sketch, "E1295", {"start": v(-57.7, 30.36) * mm, "end": v(-57.55, 30.14) * mm});
            skLineSegment(sketch, "E1296", {"start": v(-57.55, 30.14) * mm, "end": v(-57.4, 29.93) * mm});
            skLineSegment(sketch, "E1297", {"start": v(-57.4, 29.93) * mm, "end": v(-57.25, 29.72) * mm});
            skLineSegment(sketch, "E1298", {"start": v(-57.25, 29.72) * mm, "end": v(-57.1, 29.52) * mm});
            skLineSegment(sketch, "E1299", {"start": v(-57.1, 29.52) * mm, "end": v(-56.95, 29.32) * mm});
            skLineSegment(sketch, "E1300", {"start": v(-56.95, 29.32) * mm, "end": v(-56.8, 29.12) * mm});
            skLineSegment(sketch, "E1301", {"start": v(-56.8, 29.12) * mm, "end": v(-56.66, 28.93) * mm});
            skLineSegment(sketch, "E1302", {"start": v(-56.66, 28.93) * mm, "end": v(-56.52, 28.75) * mm});
            skLineSegment(sketch, "E1303", {"start": v(-56.52, 28.75) * mm, "end": v(-56.37, 28.57) * mm});
            skLineSegment(sketch, "E1304", {"start": v(-56.37, 28.57) * mm, "end": v(-56.23, 28.4) * mm});
            skLineSegment(sketch, "E1305", {"start": v(-56.23, 28.4) * mm, "end": v(-56.1, 28.22) * mm});
            skLineSegment(sketch, "E1306", {"start": v(-56.1, 28.22) * mm, "end": v(-55.95, 28.06) * mm});
            skLineSegment(sketch, "E1307", {"start": v(-55.95, 28.06) * mm, "end": v(-55.81, 27.9) * mm});
            skLineSegment(sketch, "E1308", {"start": v(-55.81, 27.9) * mm, "end": v(-55.68, 27.74) * mm});
            skLineSegment(sketch, "E1309", {"start": v(-55.68, 27.74) * mm, "end": v(-55.54, 27.58) * mm});
            skLineSegment(sketch, "E1310", {"start": v(-55.54, 27.58) * mm, "end": v(-55.4, 27.44) * mm});
            skLineSegment(sketch, "E1311", {"start": v(-55.4, 27.44) * mm, "end": v(-55.28, 27.3) * mm});
            skLineSegment(sketch, "E1312", {"start": v(-55.28, 27.3) * mm, "end": v(-55.15, 27.15) * mm});
            skLineSegment(sketch, "E1313", {"start": v(-55.15, 27.15) * mm, "end": v(-55.02, 27.02) * mm});
            skLineSegment(sketch, "E1314", {"start": v(-55.02, 27.02) * mm, "end": v(-54.9, 26.89) * mm});
            skLineSegment(sketch, "E1315", {"start": v(-54.9, 26.89) * mm, "end": v(-54.77, 26.76) * mm});
            skLineSegment(sketch, "E1316", {"start": v(-54.77, 26.76) * mm, "end": v(-54.65, 26.64) * mm});
            skLineSegment(sketch, "E1317", {"start": v(-54.65, 26.64) * mm, "end": v(-54.53, 26.52) * mm});
            skLineSegment(sketch, "E1318", {"start": v(-54.53, 26.52) * mm, "end": v(-54.4, 26.4) * mm});
            skLineSegment(sketch, "E1319", {"start": v(-54.4, 26.4) * mm, "end": v(-54.3, 26.3) * mm});
            skArc(sketch, "E1320", {"start": v(-54.3, 26.3) * mm, "mid": v(-54.58, 25.68) * mm, "end": v(-54.87, 25.07) * mm});
            skLineSegment(sketch, "E1321", {"start": v(-54.87, 25.07) * mm, "end": v(-55.03, 25.1) * mm});
            skLineSegment(sketch, "E1322", {"start": v(-55.03, 25.1) * mm, "end": v(-55.19, 25.1) * mm});
            skLineSegment(sketch, "E1323", {"start": v(-55.19, 25.1) * mm, "end": v(-55.36, 25.13) * mm});
            skLineSegment(sketch, "E1324", {"start": v(-55.36, 25.13) * mm, "end": v(-55.53, 25.14) * mm});
            skLineSegment(sketch, "E1325", {"start": v(-55.53, 25.14) * mm, "end": v(-55.7, 25.16) * mm});
            skLineSegment(sketch, "E1326", {"start": v(-55.7, 25.16) * mm, "end": v(-55.89, 25.17) * mm});
            skLineSegment(sketch, "E1327", {"start": v(-55.89, 25.17) * mm, "end": v(-56.07, 25.18) * mm});
            skLineSegment(sketch, "E1328", {"start": v(-56.07, 25.18) * mm, "end": v(-56.26, 25.2) * mm});
            skLineSegment(sketch, "E1329", {"start": v(-56.26, 25.2) * mm, "end": v(-56.46, 25.2) * mm});
            skLineSegment(sketch, "E1330", {"start": v(-56.46, 25.2) * mm, "end": v(-56.66, 25.21) * mm});
            skLineSegment(sketch, "E1331", {"start": v(-56.66, 25.21) * mm, "end": v(-56.86, 25.22) * mm});
            skLineSegment(sketch, "E1332", {"start": v(-56.86, 25.22) * mm, "end": v(-57.07, 25.22) * mm});
            skLineSegment(sketch, "E1333", {"start": v(-57.07, 25.22) * mm, "end": v(-57.28, 25.23) * mm});
            skLineSegment(sketch, "E1334", {"start": v(-57.28, 25.23) * mm, "end": v(-57.5, 25.23) * mm});
            skLineSegment(sketch, "E1335", {"start": v(-57.5, 25.23) * mm, "end": v(-57.72, 25.23) * mm});
            skLineSegment(sketch, "E1336", {"start": v(-57.72, 25.23) * mm, "end": v(-57.95, 25.23) * mm});
            skLineSegment(sketch, "E1337", {"start": v(-57.95, 25.23) * mm, "end": v(-58.18, 25.22) * mm});
            skLineSegment(sketch, "E1338", {"start": v(-58.18, 25.22) * mm, "end": v(-58.41, 25.22) * mm});
            skLineSegment(sketch, "E1339", {"start": v(-58.41, 25.22) * mm, "end": v(-58.65, 25.2) * mm});
            skLineSegment(sketch, "E1340", {"start": v(-58.65, 25.2) * mm, "end": v(-58.9, 25.2) * mm});
            skLineSegment(sketch, "E1341", {"start": v(-58.9, 25.2) * mm, "end": v(-59.14, 25.18) * mm});
            skLineSegment(sketch, "E1342", {"start": v(-59.14, 25.18) * mm, "end": v(-59.4, 25.17) * mm});
            skLineSegment(sketch, "E1343", {"start": v(-59.4, 25.17) * mm, "end": v(-59.65, 25.15) * mm});
            skLineSegment(sketch, "E1344", {"start": v(-59.65, 25.15) * mm, "end": v(-59.9, 25.13) * mm});
            skLineSegment(sketch, "E1345", {"start": v(-59.9, 25.13) * mm, "end": v(-60.17, 25.1) * mm});
            skLineSegment(sketch, "E1346", {"start": v(-60.17, 25.1) * mm, "end": v(-60.44, 25.08) * mm});
            skLineSegment(sketch, "E1347", {"start": v(-60.44, 25.08) * mm, "end": v(-60.71, 25.05) * mm});
            skLineSegment(sketch, "E1348", {"start": v(-60.71, 25.05) * mm, "end": v(-60.99, 25.01) * mm});
            skLineSegment(sketch, "E1349", {"start": v(-60.99, 25.01) * mm, "end": v(-61.13, 25) * mm});
            skLineSegment(sketch, "E1350", {"start": v(-61.13, 25) * mm, "end": v(-61.67, 23.62) * mm});
            skLineSegment(sketch, "E1351", {"start": v(-61.67, 23.62) * mm, "end": v(-61.58, 23.51) * mm});
            skLineSegment(sketch, "E1352", {"start": v(-61.58, 23.51) * mm, "end": v(-61.4, 23.3) * mm});
            skLineSegment(sketch, "E1353", {"start": v(-61.4, 23.3) * mm, "end": v(-61.22, 23.1) * mm});
            skLineSegment(sketch, "E1354", {"start": v(-61.22, 23.1) * mm, "end": v(-61.05, 22.9) * mm});
            skLineSegment(sketch, "E1355", {"start": v(-61.05, 22.9) * mm, "end": v(-60.87, 22.7) * mm});
            skLineSegment(sketch, "E1356", {"start": v(-60.87, 22.7) * mm, "end": v(-60.7, 22.5) * mm});
            skLineSegment(sketch, "E1357", {"start": v(-60.7, 22.5) * mm, "end": v(-60.52, 22.31) * mm});
            skLineSegment(sketch, "E1358", {"start": v(-60.52, 22.31) * mm, "end": v(-60.35, 22.13) * mm});
            skLineSegment(sketch, "E1359", {"start": v(-60.35, 22.13) * mm, "end": v(-60.18, 21.95) * mm});
            skLineSegment(sketch, "E1360", {"start": v(-60.18, 21.95) * mm, "end": v(-60, 21.77) * mm});
            skLineSegment(sketch, "E1361", {"start": v(-60, 21.77) * mm, "end": v(-59.84, 21.6) * mm});
            skLineSegment(sketch, "E1362", {"start": v(-59.84, 21.6) * mm, "end": v(-59.67, 21.44) * mm});
            skLineSegment(sketch, "E1363", {"start": v(-59.67, 21.44) * mm, "end": v(-59.5, 21.28) * mm});
            skLineSegment(sketch, "E1364", {"start": v(-59.5, 21.28) * mm, "end": v(-59.35, 21.12) * mm});
            skLineSegment(sketch, "E1365", {"start": v(-59.35, 21.12) * mm, "end": v(-59.19, 20.97) * mm});
            skLineSegment(sketch, "E1366", {"start": v(-59.19, 20.97) * mm, "end": v(-59.03, 20.82) * mm});
            skLineSegment(sketch, "E1367", {"start": v(-59.03, 20.82) * mm, "end": v(-58.87, 20.68) * mm});
            skLineSegment(sketch, "E1368", {"start": v(-58.87, 20.68) * mm, "end": v(-58.71, 20.54) * mm});
            skLineSegment(sketch, "E1369", {"start": v(-58.71, 20.54) * mm, "end": v(-58.56, 20.4) * mm});
            skLineSegment(sketch, "E1370", {"start": v(-58.56, 20.4) * mm, "end": v(-58.41, 20.27) * mm});
            skLineSegment(sketch, "E1371", {"start": v(-58.41, 20.27) * mm, "end": v(-58.26, 20.15) * mm});
            skLineSegment(sketch, "E1372", {"start": v(-58.26, 20.15) * mm, "end": v(-58.12, 20.03) * mm});
            skLineSegment(sketch, "E1373", {"start": v(-58.12, 20.03) * mm, "end": v(-57.97, 19.9) * mm});
            skLineSegment(sketch, "E1374", {"start": v(-57.97, 19.9) * mm, "end": v(-57.83, 19.8) * mm});
            skLineSegment(sketch, "E1375", {"start": v(-57.83, 19.8) * mm, "end": v(-57.7, 19.68) * mm});
            skLineSegment(sketch, "E1376", {"start": v(-57.7, 19.68) * mm, "end": v(-57.55, 19.58) * mm});
            skLineSegment(sketch, "E1377", {"start": v(-57.55, 19.58) * mm, "end": v(-57.42, 19.48) * mm});
            skLineSegment(sketch, "E1378", {"start": v(-57.42, 19.48) * mm, "end": v(-57.29, 19.38) * mm});
            skLineSegment(sketch, "E1379", {"start": v(-57.29, 19.38) * mm, "end": v(-57.16, 19.28) * mm});
            skArc(sketch, "E1380", {"start": v(-57.16, 19.28) * mm, "mid": v(-57.37, 18.64) * mm, "end": v(-57.58, 18) * mm});
            skLineSegment(sketch, "E1381", {"start": v(-57.58, 18) * mm, "end": v(-57.74, 18) * mm});
            skLineSegment(sketch, "E1382", {"start": v(-57.74, 18) * mm, "end": v(-57.9, 18) * mm});
            skLineSegment(sketch, "E1383", {"start": v(-57.9, 18) * mm, "end": v(-58.07, 18) * mm});
            skLineSegment(sketch, "E1384", {"start": v(-58.07, 18) * mm, "end": v(-58.24, 17.98) * mm});
            skLineSegment(sketch, "E1385", {"start": v(-58.24, 17.98) * mm, "end": v(-58.42, 17.98) * mm});
            skLineSegment(sketch, "E1386", {"start": v(-58.42, 17.98) * mm, "end": v(-58.6, 17.97) * mm});
            skLineSegment(sketch, "E1387", {"start": v(-58.6, 17.97) * mm, "end": v(-58.79, 17.96) * mm});
            skLineSegment(sketch, "E1388", {"start": v(-58.79, 17.96) * mm, "end": v(-58.98, 17.94) * mm});
            skLineSegment(sketch, "E1389", {"start": v(-58.98, 17.94) * mm, "end": v(-59.17, 17.93) * mm});
            skLineSegment(sketch, "E1390", {"start": v(-59.17, 17.93) * mm, "end": v(-59.37, 17.91) * mm});
            skLineSegment(sketch, "E1391", {"start": v(-59.37, 17.91) * mm, "end": v(-59.57, 17.9) * mm});
            skLineSegment(sketch, "E1392", {"start": v(-59.57, 17.9) * mm, "end": v(-59.78, 17.87) * mm});
            skLineSegment(sketch, "E1393", {"start": v(-59.78, 17.87) * mm, "end": v(-60, 17.85) * mm});
            skLineSegment(sketch, "E1394", {"start": v(-60, 17.85) * mm, "end": v(-60.2, 17.82) * mm});
            skLineSegment(sketch, "E1395", {"start": v(-60.2, 17.82) * mm, "end": v(-60.43, 17.8) * mm});
            skLineSegment(sketch, "E1396", {"start": v(-60.43, 17.8) * mm, "end": v(-60.65, 17.76) * mm});
            skLineSegment(sketch, "E1397", {"start": v(-60.65, 17.76) * mm, "end": v(-60.88, 17.73) * mm});
            skLineSegment(sketch, "E1398", {"start": v(-60.88, 17.73) * mm, "end": v(-61.1, 17.7) * mm});
            skLineSegment(sketch, "E1399", {"start": v(-61.1, 17.7) * mm, "end": v(-61.35, 17.66) * mm});
            skLineSegment(sketch, "E1400", {"start": v(-61.35, 17.66) * mm, "end": v(-61.59, 17.62) * mm});
            skLineSegment(sketch, "E1401", {"start": v(-61.59, 17.62) * mm, "end": v(-61.83, 17.57) * mm});
            skLineSegment(sketch, "E1402", {"start": v(-61.83, 17.57) * mm, "end": v(-62.08, 17.52) * mm});
            skLineSegment(sketch, "E1403", {"start": v(-62.08, 17.52) * mm, "end": v(-62.33, 17.47) * mm});
            skLineSegment(sketch, "E1404", {"start": v(-62.33, 17.47) * mm, "end": v(-62.58, 17.42) * mm});
            skLineSegment(sketch, "E1405", {"start": v(-62.58, 17.42) * mm, "end": v(-62.84, 17.36) * mm});
            skLineSegment(sketch, "E1406", {"start": v(-62.84, 17.36) * mm, "end": v(-63.1, 17.3) * mm});
            skLineSegment(sketch, "E1407", {"start": v(-63.1, 17.3) * mm, "end": v(-63.37, 17.24) * mm});
            skLineSegment(sketch, "E1408", {"start": v(-63.37, 17.24) * mm, "end": v(-63.64, 17.17) * mm});
            skLineSegment(sketch, "E1409", {"start": v(-63.64, 17.17) * mm, "end": v(-63.78, 17.14) * mm});
            skLineSegment(sketch, "E1410", {"start": v(-63.78, 17.14) * mm, "end": v(-64.15, 15.7) * mm});
            skLineSegment(sketch, "E1411", {"start": v(-64.15, 15.7) * mm, "end": v(-64.04, 15.61) * mm});
            skLineSegment(sketch, "E1412", {"start": v(-64.04, 15.61) * mm, "end": v(-63.84, 15.42) * mm});
            skLineSegment(sketch, "E1413", {"start": v(-63.84, 15.42) * mm, "end": v(-63.64, 15.24) * mm});
            skLineSegment(sketch, "E1414", {"start": v(-63.64, 15.24) * mm, "end": v(-63.43, 15.06) * mm});
            skLineSegment(sketch, "E1415", {"start": v(-63.43, 15.06) * mm, "end": v(-63.23, 14.88) * mm});
            skLineSegment(sketch, "E1416", {"start": v(-63.23, 14.88) * mm, "end": v(-63.04, 14.71) * mm});
            skLineSegment(sketch, "E1417", {"start": v(-63.04, 14.71) * mm, "end": v(-62.84, 14.55) * mm});
            skLineSegment(sketch, "E1418", {"start": v(-62.84, 14.55) * mm, "end": v(-62.65, 14.39) * mm});
            skLineSegment(sketch, "E1419", {"start": v(-62.65, 14.39) * mm, "end": v(-62.45, 14.23) * mm});
            skLineSegment(sketch, "E1420", {"start": v(-62.45, 14.23) * mm, "end": v(-62.26, 14.08) * mm});
            skLineSegment(sketch, "E1421", {"start": v(-62.26, 14.08) * mm, "end": v(-62.08, 13.93) * mm});
            skLineSegment(sketch, "E1422", {"start": v(-62.08, 13.93) * mm, "end": v(-61.9, 13.8) * mm});
            skLineSegment(sketch, "E1423", {"start": v(-61.9, 13.8) * mm, "end": v(-61.7, 13.65) * mm});
            skLineSegment(sketch, "E1424", {"start": v(-61.7, 13.65) * mm, "end": v(-61.53, 13.52) * mm});
            skLineSegment(sketch, "E1425", {"start": v(-61.53, 13.52) * mm, "end": v(-61.35, 13.39) * mm});
            skLineSegment(sketch, "E1426", {"start": v(-61.35, 13.39) * mm, "end": v(-61.17, 13.26) * mm});
            skLineSegment(sketch, "E1427", {"start": v(-61.17, 13.26) * mm, "end": v(-61, 13.14) * mm});
            skLineSegment(sketch, "E1428", {"start": v(-61, 13.14) * mm, "end": v(-60.83, 13.02) * mm});
            skLineSegment(sketch, "E1429", {"start": v(-60.83, 13.02) * mm, "end": v(-60.66, 12.9) * mm});
            skLineSegment(sketch, "E1430", {"start": v(-60.66, 12.9) * mm, "end": v(-60.5, 12.8) * mm});
            skLineSegment(sketch, "E1431", {"start": v(-60.5, 12.8) * mm, "end": v(-60.33, 12.69) * mm});
            skLineSegment(sketch, "E1432", {"start": v(-60.33, 12.69) * mm, "end": v(-60.17, 12.58) * mm});
            skLineSegment(sketch, "E1433", {"start": v(-60.17, 12.58) * mm, "end": v(-60, 12.49) * mm});
            skLineSegment(sketch, "E1434", {"start": v(-60, 12.49) * mm, "end": v(-59.85, 12.4) * mm});
            skLineSegment(sketch, "E1435", {"start": v(-59.85, 12.4) * mm, "end": v(-59.7, 12.3) * mm});
            skLineSegment(sketch, "E1436", {"start": v(-59.7, 12.3) * mm, "end": v(-59.55, 12.21) * mm});
            skLineSegment(sketch, "E1437", {"start": v(-59.55, 12.21) * mm, "end": v(-59.4, 12.13) * mm});
            skLineSegment(sketch, "E1438", {"start": v(-59.4, 12.13) * mm, "end": v(-59.26, 12.04) * mm});
            skLineSegment(sketch, "E1439", {"start": v(-59.26, 12.04) * mm, "end": v(-59.13, 11.97) * mm});
            skArc(sketch, "E1440", {"start": v(-59.13, 11.97) * mm, "mid": v(-59.25, 11.3) * mm, "end": v(-59.38, 10.64) * mm});
            skLineSegment(sketch, "E1441", {"start": v(-59.38, 10.64) * mm, "end": v(-59.54, 10.62) * mm});
            skLineSegment(sketch, "E1442", {"start": v(-59.54, 10.62) * mm, "end": v(-59.7, 10.6) * mm});
            skLineSegment(sketch, "E1443", {"start": v(-59.7, 10.6) * mm, "end": v(-59.87, 10.57) * mm});
            skLineSegment(sketch, "E1444", {"start": v(-59.87, 10.57) * mm, "end": v(-60.04, 10.54) * mm});
            skLineSegment(sketch, "E1445", {"start": v(-60.04, 10.54) * mm, "end": v(-60.21, 10.51) * mm});
            skLineSegment(sketch, "E1446", {"start": v(-60.21, 10.51) * mm, "end": v(-60.4, 10.48) * mm});
            skLineSegment(sketch, "E1447", {"start": v(-60.4, 10.48) * mm, "end": v(-60.57, 10.45) * mm});
            skLineSegment(sketch, "E1448", {"start": v(-60.57, 10.45) * mm, "end": v(-60.76, 10.41) * mm});
            skLineSegment(sketch, "E1449", {"start": v(-60.76, 10.41) * mm, "end": v(-60.95, 10.37) * mm});
            skLineSegment(sketch, "E1450", {"start": v(-60.95, 10.37) * mm, "end": v(-61.15, 10.33) * mm});
            skLineSegment(sketch, "E1451", {"start": v(-61.15, 10.33) * mm, "end": v(-61.35, 10.29) * mm});
            skLineSegment(sketch, "E1452", {"start": v(-61.35, 10.29) * mm, "end": v(-61.55, 10.24) * mm});
            skLineSegment(sketch, "E1453", {"start": v(-61.55, 10.24) * mm, "end": v(-61.76, 10.19) * mm});
            skLineSegment(sketch, "E1454", {"start": v(-61.76, 10.19) * mm, "end": v(-61.97, 10.14) * mm});
            skLineSegment(sketch, "E1455", {"start": v(-61.97, 10.14) * mm, "end": v(-62.18, 10.08) * mm});
            skLineSegment(sketch, "E1456", {"start": v(-62.18, 10.08) * mm, "end": v(-62.4, 10.02) * mm});
            skLineSegment(sketch, "E1457", {"start": v(-62.4, 10.02) * mm, "end": v(-62.62, 9.96) * mm});
            skLineSegment(sketch, "E1458", {"start": v(-62.62, 9.96) * mm, "end": v(-62.85, 9.9) * mm});
            skLineSegment(sketch, "E1459", {"start": v(-62.85, 9.9) * mm, "end": v(-63.07, 9.83) * mm});
            skLineSegment(sketch, "E1460", {"start": v(-63.07, 9.83) * mm, "end": v(-63.3, 9.76) * mm});
            skLineSegment(sketch, "E1461", {"start": v(-63.3, 9.76) * mm, "end": v(-63.54, 9.68) * mm});
            skLineSegment(sketch, "E1462", {"start": v(-63.54, 9.68) * mm, "end": v(-63.78, 9.6) * mm});
            skLineSegment(sketch, "E1463", {"start": v(-63.78, 9.6) * mm, "end": v(-64.03, 9.52) * mm});
            skLineSegment(sketch, "E1464", {"start": v(-64.03, 9.52) * mm, "end": v(-64.27, 9.44) * mm});
            skLineSegment(sketch, "E1465", {"start": v(-64.27, 9.44) * mm, "end": v(-64.52, 9.35) * mm});
            skLineSegment(sketch, "E1466", {"start": v(-64.52, 9.35) * mm, "end": v(-64.78, 9.26) * mm});
            skLineSegment(sketch, "E1467", {"start": v(-64.78, 9.26) * mm, "end": v(-65.03, 9.16) * mm});
            skLineSegment(sketch, "E1468", {"start": v(-65.03, 9.16) * mm, "end": v(-65.3, 9.06) * mm});
            skLineSegment(sketch, "E1469", {"start": v(-65.3, 9.06) * mm, "end": v(-65.42, 9.01) * mm});
            skLineSegment(sketch, "E1470", {"start": v(-65.42, 9.01) * mm, "end": v(-65.6, 7.54) * mm});
            skLineSegment(sketch, "E1471", {"start": v(-65.6, 7.54) * mm, "end": v(-65.5, 7.46) * mm});
            skLineSegment(sketch, "E1472", {"start": v(-65.5, 7.46) * mm, "end": v(-65.27, 7.3) * mm});
            skLineSegment(sketch, "E1473", {"start": v(-65.27, 7.3) * mm, "end": v(-65.04, 7.14) * mm});
            skLineSegment(sketch, "E1474", {"start": v(-65.04, 7.14) * mm, "end": v(-64.82, 7) * mm});
            skLineSegment(sketch, "E1475", {"start": v(-64.82, 7) * mm, "end": v(-64.6, 6.84) * mm});
            skLineSegment(sketch, "E1476", {"start": v(-64.6, 6.84) * mm, "end": v(-64.38, 6.7) * mm});
            skLineSegment(sketch, "E1477", {"start": v(-64.38, 6.7) * mm, "end": v(-64.17, 6.56) * mm});
            skLineSegment(sketch, "E1478", {"start": v(-64.17, 6.56) * mm, "end": v(-63.96, 6.42) * mm});
            skLineSegment(sketch, "E1479", {"start": v(-63.96, 6.42) * mm, "end": v(-63.75, 6.3) * mm});
            skLineSegment(sketch, "E1480", {"start": v(-63.75, 6.3) * mm, "end": v(-63.54, 6.17) * mm});
            skLineSegment(sketch, "E1481", {"start": v(-63.54, 6.17) * mm, "end": v(-63.33, 6.04) * mm});
            skLineSegment(sketch, "E1482", {"start": v(-63.33, 6.04) * mm, "end": v(-63.13, 5.92) * mm});
            skLineSegment(sketch, "E1483", {"start": v(-63.13, 5.92) * mm, "end": v(-62.93, 5.8) * mm});
            skLineSegment(sketch, "E1484", {"start": v(-62.93, 5.8) * mm, "end": v(-62.73, 5.7) * mm});
            skLineSegment(sketch, "E1485", {"start": v(-62.73, 5.7) * mm, "end": v(-62.54, 5.6) * mm});
            skLineSegment(sketch, "E1486", {"start": v(-62.54, 5.6) * mm, "end": v(-62.35, 5.49) * mm});
            skLineSegment(sketch, "E1487", {"start": v(-62.35, 5.49) * mm, "end": v(-62.16, 5.39) * mm});
            skLineSegment(sketch, "E1488", {"start": v(-62.16, 5.39) * mm, "end": v(-61.98, 5.3) * mm});
            skLineSegment(sketch, "E1489", {"start": v(-61.98, 5.3) * mm, "end": v(-61.8, 5.2) * mm});
            skLineSegment(sketch, "E1490", {"start": v(-61.8, 5.2) * mm, "end": v(-61.62, 5.11) * mm});
            skLineSegment(sketch, "E1491", {"start": v(-61.62, 5.11) * mm, "end": v(-61.44, 5.03) * mm});
            skLineSegment(sketch, "E1492", {"start": v(-61.44, 5.03) * mm, "end": v(-61.27, 4.94) * mm});
            skLineSegment(sketch, "E1493", {"start": v(-61.27, 4.94) * mm, "end": v(-61.1, 4.87) * mm});
            skLineSegment(sketch, "E1494", {"start": v(-61.1, 4.87) * mm, "end": v(-60.94, 4.8) * mm});
            skLineSegment(sketch, "E1495", {"start": v(-60.94, 4.8) * mm, "end": v(-60.77, 4.72) * mm});
            skLineSegment(sketch, "E1496", {"start": v(-60.77, 4.72) * mm, "end": v(-60.61, 4.65) * mm});
            skLineSegment(sketch, "E1497", {"start": v(-60.61, 4.65) * mm, "end": v(-60.46, 4.58) * mm});
            skLineSegment(sketch, "E1498", {"start": v(-60.46, 4.58) * mm, "end": v(-60.3, 4.52) * mm});
            skLineSegment(sketch, "E1499", {"start": v(-60.3, 4.52) * mm, "end": v(-60.16, 4.46) * mm});
            skArc(sketch, "E1500", {"start": v(-60.16, 4.46) * mm, "mid": v(-60.2, 3.79) * mm, "end": v(-60.24, 3.11) * mm});
            skLineSegment(sketch, "E1501", {"start": v(-60.24, 3.11) * mm, "end": v(-60.4, 3.07) * mm});
            skLineSegment(sketch, "E1502", {"start": v(-60.4, 3.07) * mm, "end": v(-60.56, 3.03) * mm});
            skLineSegment(sketch, "E1503", {"start": v(-60.56, 3.03) * mm, "end": v(-60.72, 2.98) * mm});
            skLineSegment(sketch, "E1504", {"start": v(-60.72, 2.98) * mm, "end": v(-60.89, 2.94) * mm});
            skLineSegment(sketch, "E1505", {"start": v(-60.89, 2.94) * mm, "end": v(-61.06, 2.88) * mm});
            skLineSegment(sketch, "E1506", {"start": v(-61.06, 2.88) * mm, "end": v(-61.23, 2.83) * mm});
            skLineSegment(sketch, "E1507", {"start": v(-61.23, 2.83) * mm, "end": v(-61.4, 2.77) * mm});
            skLineSegment(sketch, "E1508", {"start": v(-61.4, 2.77) * mm, "end": v(-61.59, 2.71) * mm});
            skLineSegment(sketch, "E1509", {"start": v(-61.59, 2.71) * mm, "end": v(-61.77, 2.65) * mm});
            skLineSegment(sketch, "E1510", {"start": v(-61.77, 2.65) * mm, "end": v(-61.96, 2.59) * mm});
            skLineSegment(sketch, "E1511", {"start": v(-61.96, 2.59) * mm, "end": v(-62.15, 2.52) * mm});
            skLineSegment(sketch, "E1512", {"start": v(-62.15, 2.52) * mm, "end": v(-62.35, 2.44) * mm});
            skLineSegment(sketch, "E1513", {"start": v(-62.35, 2.44) * mm, "end": v(-62.55, 2.37) * mm});
            skLineSegment(sketch, "E1514", {"start": v(-62.55, 2.37) * mm, "end": v(-62.75, 2.3) * mm});
            skLineSegment(sketch, "E1515", {"start": v(-62.75, 2.3) * mm, "end": v(-62.95, 2.2) * mm});
            skLineSegment(sketch, "E1516", {"start": v(-62.95, 2.2) * mm, "end": v(-63.16, 2.12) * mm});
            skLineSegment(sketch, "E1517", {"start": v(-63.16, 2.12) * mm, "end": v(-63.38, 2.03) * mm});
            skLineSegment(sketch, "E1518", {"start": v(-63.38, 2.03) * mm, "end": v(-63.6, 1.94) * mm});
            skLineSegment(sketch, "E1519", {"start": v(-63.6, 1.94) * mm, "end": v(-63.8, 1.85) * mm});
            skLineSegment(sketch, "E1520", {"start": v(-63.8, 1.85) * mm, "end": v(-64.03, 1.75) * mm});
            skLineSegment(sketch, "E1521", {"start": v(-64.03, 1.75) * mm, "end": v(-64.26, 1.64) * mm});
            skLineSegment(sketch, "E1522", {"start": v(-64.26, 1.64) * mm, "end": v(-64.48, 1.54) * mm});
            skLineSegment(sketch, "E1523", {"start": v(-64.48, 1.54) * mm, "end": v(-64.72, 1.42) * mm});
            skLineSegment(sketch, "E1524", {"start": v(-64.72, 1.42) * mm, "end": v(-64.95, 1.3) * mm});
            skLineSegment(sketch, "E1525", {"start": v(-64.95, 1.3) * mm, "end": v(-65.19, 1.19) * mm});
            skLineSegment(sketch, "E1526", {"start": v(-65.19, 1.19) * mm, "end": v(-65.43, 1.07) * mm});
            skLineSegment(sketch, "E1527", {"start": v(-65.43, 1.07) * mm, "end": v(-65.67, 0.94) * mm});
            skLineSegment(sketch, "E1528", {"start": v(-65.67, 0.94) * mm, "end": v(-65.91, 0.8) * mm});
            skLineSegment(sketch, "E1529", {"start": v(-65.91, 0.8) * mm, "end": v(-66.04, 0.74) * mm});
            skLineSegment(sketch, "E1530", {"start": v(-66.04, 0.74) * mm, "end": v(-66.04, -0.74) * mm});
            skLineSegment(sketch, "E1531", {"start": v(-66.04, -0.74) * mm, "end": v(-65.91, -0.8) * mm});
            skLineSegment(sketch, "E1532", {"start": v(-65.91, -0.8) * mm, "end": v(-65.67, -0.94) * mm});
            skLineSegment(sketch, "E1533", {"start": v(-65.67, -0.94) * mm, "end": v(-65.43, -1.07) * mm});
            skLineSegment(sketch, "E1534", {"start": v(-65.43, -1.07) * mm, "end": v(-65.19, -1.19) * mm});
            skLineSegment(sketch, "E1535", {"start": v(-65.19, -1.19) * mm, "end": v(-64.95, -1.3) * mm});
            skLineSegment(sketch, "E1536", {"start": v(-64.95, -1.3) * mm, "end": v(-64.72, -1.42) * mm});
            skLineSegment(sketch, "E1537", {"start": v(-64.72, -1.42) * mm, "end": v(-64.48, -1.54) * mm});
            skLineSegment(sketch, "E1538", {"start": v(-64.48, -1.54) * mm, "end": v(-64.26, -1.64) * mm});
            skLineSegment(sketch, "E1539", {"start": v(-64.26, -1.64) * mm, "end": v(-64.03, -1.75) * mm});
            skLineSegment(sketch, "E1540", {"start": v(-64.03, -1.75) * mm, "end": v(-63.8, -1.85) * mm});
            skLineSegment(sketch, "E1541", {"start": v(-63.8, -1.85) * mm, "end": v(-63.6, -1.94) * mm});
            skLineSegment(sketch, "E1542", {"start": v(-63.6, -1.94) * mm, "end": v(-63.38, -2.03) * mm});
            skLineSegment(sketch, "E1543", {"start": v(-63.38, -2.03) * mm, "end": v(-63.16, -2.12) * mm});
            skLineSegment(sketch, "E1544", {"start": v(-63.16, -2.12) * mm, "end": v(-62.95, -2.2) * mm});
            skLineSegment(sketch, "E1545", {"start": v(-62.95, -2.2) * mm, "end": v(-62.75, -2.3) * mm});
            skLineSegment(sketch, "E1546", {"start": v(-62.75, -2.3) * mm, "end": v(-62.55, -2.37) * mm});
            skLineSegment(sketch, "E1547", {"start": v(-62.55, -2.37) * mm, "end": v(-62.35, -2.44) * mm});
            skLineSegment(sketch, "E1548", {"start": v(-62.35, -2.44) * mm, "end": v(-62.15, -2.52) * mm});
            skLineSegment(sketch, "E1549", {"start": v(-62.15, -2.52) * mm, "end": v(-61.96, -2.59) * mm});
            skLineSegment(sketch, "E1550", {"start": v(-61.96, -2.59) * mm, "end": v(-61.77, -2.65) * mm});
            skLineSegment(sketch, "E1551", {"start": v(-61.77, -2.65) * mm, "end": v(-61.59, -2.71) * mm});
            skLineSegment(sketch, "E1552", {"start": v(-61.59, -2.71) * mm, "end": v(-61.4, -2.77) * mm});
            skLineSegment(sketch, "E1553", {"start": v(-61.4, -2.77) * mm, "end": v(-61.23, -2.83) * mm});
            skLineSegment(sketch, "E1554", {"start": v(-61.23, -2.83) * mm, "end": v(-61.06, -2.88) * mm});
            skLineSegment(sketch, "E1555", {"start": v(-61.06, -2.88) * mm, "end": v(-60.89, -2.94) * mm});
            skLineSegment(sketch, "E1556", {"start": v(-60.89, -2.94) * mm, "end": v(-60.72, -2.98) * mm});
            skLineSegment(sketch, "E1557", {"start": v(-60.72, -2.98) * mm, "end": v(-60.56, -3.03) * mm});
            skLineSegment(sketch, "E1558", {"start": v(-60.56, -3.03) * mm, "end": v(-60.4, -3.07) * mm});
            skLineSegment(sketch, "E1559", {"start": v(-60.4, -3.07) * mm, "end": v(-60.24, -3.11) * mm});
            skArc(sketch, "E1560", {"start": v(-60.24, -3.11) * mm, "mid": v(-60.2, -3.79) * mm, "end": v(-60.16, -4.46) * mm});
            skLineSegment(sketch, "E1561", {"start": v(-60.16, -4.46) * mm, "end": v(-60.3, -4.52) * mm});
            skLineSegment(sketch, "E1562", {"start": v(-60.3, -4.52) * mm, "end": v(-60.46, -4.58) * mm});
            skLineSegment(sketch, "E1563", {"start": v(-60.46, -4.58) * mm, "end": v(-60.61, -4.65) * mm});
            skLineSegment(sketch, "E1564", {"start": v(-60.61, -4.65) * mm, "end": v(-60.77, -4.72) * mm});
            skLineSegment(sketch, "E1565", {"start": v(-60.77, -4.72) * mm, "end": v(-60.94, -4.8) * mm});
            skLineSegment(sketch, "E1566", {"start": v(-60.94, -4.8) * mm, "end": v(-61.1, -4.87) * mm});
            skLineSegment(sketch, "E1567", {"start": v(-61.1, -4.87) * mm, "end": v(-61.27, -4.94) * mm});
            skLineSegment(sketch, "E1568", {"start": v(-61.27, -4.94) * mm, "end": v(-61.44, -5.03) * mm});
            skLineSegment(sketch, "E1569", {"start": v(-61.44, -5.03) * mm, "end": v(-61.62, -5.11) * mm});
            skLineSegment(sketch, "E1570", {"start": v(-61.62, -5.11) * mm, "end": v(-61.8, -5.2) * mm});
            skLineSegment(sketch, "E1571", {"start": v(-61.8, -5.2) * mm, "end": v(-61.98, -5.3) * mm});
            skLineSegment(sketch, "E1572", {"start": v(-61.98, -5.3) * mm, "end": v(-62.16, -5.39) * mm});
            skLineSegment(sketch, "E1573", {"start": v(-62.16, -5.39) * mm, "end": v(-62.35, -5.49) * mm});
            skLineSegment(sketch, "E1574", {"start": v(-62.35, -5.49) * mm, "end": v(-62.54, -5.6) * mm});
            skLineSegment(sketch, "E1575", {"start": v(-62.54, -5.6) * mm, "end": v(-62.73, -5.7) * mm});
            skLineSegment(sketch, "E1576", {"start": v(-62.73, -5.7) * mm, "end": v(-62.93, -5.8) * mm});
            skLineSegment(sketch, "E1577", {"start": v(-62.93, -5.8) * mm, "end": v(-63.13, -5.92) * mm});
            skLineSegment(sketch, "E1578", {"start": v(-63.13, -5.92) * mm, "end": v(-63.33, -6.04) * mm});
            skLineSegment(sketch, "E1579", {"start": v(-63.33, -6.04) * mm, "end": v(-63.54, -6.17) * mm});
            skLineSegment(sketch, "E1580", {"start": v(-63.54, -6.17) * mm, "end": v(-63.75, -6.3) * mm});
            skLineSegment(sketch, "E1581", {"start": v(-63.75, -6.3) * mm, "end": v(-63.96, -6.42) * mm});
            skLineSegment(sketch, "E1582", {"start": v(-63.96, -6.42) * mm, "end": v(-64.17, -6.56) * mm});
            skLineSegment(sketch, "E1583", {"start": v(-64.17, -6.56) * mm, "end": v(-64.38, -6.7) * mm});
            skLineSegment(sketch, "E1584", {"start": v(-64.38, -6.7) * mm, "end": v(-64.6, -6.84) * mm});
            skLineSegment(sketch, "E1585", {"start": v(-64.6, -6.84) * mm, "end": v(-64.82, -7) * mm});
            skLineSegment(sketch, "E1586", {"start": v(-64.82, -7) * mm, "end": v(-65.04, -7.14) * mm});
            skLineSegment(sketch, "E1587", {"start": v(-65.04, -7.14) * mm, "end": v(-65.27, -7.3) * mm});
            skLineSegment(sketch, "E1588", {"start": v(-65.27, -7.3) * mm, "end": v(-65.5, -7.46) * mm});
            skLineSegment(sketch, "E1589", {"start": v(-65.5, -7.46) * mm, "end": v(-65.6, -7.54) * mm});
            skLineSegment(sketch, "E1590", {"start": v(-65.6, -7.54) * mm, "end": v(-65.42, -9.01) * mm});
            skLineSegment(sketch, "E1591", {"start": v(-65.42, -9.01) * mm, "end": v(-65.3, -9.06) * mm});
            skLineSegment(sketch, "E1592", {"start": v(-65.3, -9.06) * mm, "end": v(-65.03, -9.16) * mm});
            skLineSegment(sketch, "E1593", {"start": v(-65.03, -9.16) * mm, "end": v(-64.78, -9.26) * mm});
            skLineSegment(sketch, "E1594", {"start": v(-64.78, -9.26) * mm, "end": v(-64.52, -9.35) * mm});
            skLineSegment(sketch, "E1595", {"start": v(-64.52, -9.35) * mm, "end": v(-64.27, -9.44) * mm});
            skLineSegment(sketch, "E1596", {"start": v(-64.27, -9.44) * mm, "end": v(-64.03, -9.52) * mm});
            skLineSegment(sketch, "E1597", {"start": v(-64.03, -9.52) * mm, "end": v(-63.78, -9.6) * mm});
            skLineSegment(sketch, "E1598", {"start": v(-63.78, -9.6) * mm, "end": v(-63.54, -9.68) * mm});
            skLineSegment(sketch, "E1599", {"start": v(-63.54, -9.68) * mm, "end": v(-63.3, -9.76) * mm});
            skLineSegment(sketch, "E1600", {"start": v(-63.3, -9.76) * mm, "end": v(-63.07, -9.83) * mm});
            skLineSegment(sketch, "E1601", {"start": v(-63.07, -9.83) * mm, "end": v(-62.85, -9.9) * mm});
            skLineSegment(sketch, "E1602", {"start": v(-62.85, -9.9) * mm, "end": v(-62.62, -9.96) * mm});
            skLineSegment(sketch, "E1603", {"start": v(-62.62, -9.96) * mm, "end": v(-62.4, -10.02) * mm});
            skLineSegment(sketch, "E1604", {"start": v(-62.4, -10.02) * mm, "end": v(-62.18, -10.08) * mm});
            skLineSegment(sketch, "E1605", {"start": v(-62.18, -10.08) * mm, "end": v(-61.97, -10.14) * mm});
            skLineSegment(sketch, "E1606", {"start": v(-61.97, -10.14) * mm, "end": v(-61.76, -10.19) * mm});
            skLineSegment(sketch, "E1607", {"start": v(-61.76, -10.19) * mm, "end": v(-61.55, -10.24) * mm});
            skLineSegment(sketch, "E1608", {"start": v(-61.55, -10.24) * mm, "end": v(-61.35, -10.29) * mm});
            skLineSegment(sketch, "E1609", {"start": v(-61.35, -10.29) * mm, "end": v(-61.15, -10.33) * mm});
            skLineSegment(sketch, "E1610", {"start": v(-61.15, -10.33) * mm, "end": v(-60.95, -10.37) * mm});
            skLineSegment(sketch, "E1611", {"start": v(-60.95, -10.37) * mm, "end": v(-60.76, -10.41) * mm});
            skLineSegment(sketch, "E1612", {"start": v(-60.76, -10.41) * mm, "end": v(-60.57, -10.45) * mm});
            skLineSegment(sketch, "E1613", {"start": v(-60.57, -10.45) * mm, "end": v(-60.4, -10.48) * mm});
            skLineSegment(sketch, "E1614", {"start": v(-60.4, -10.48) * mm, "end": v(-60.21, -10.51) * mm});
            skLineSegment(sketch, "E1615", {"start": v(-60.21, -10.51) * mm, "end": v(-60.04, -10.54) * mm});
            skLineSegment(sketch, "E1616", {"start": v(-60.04, -10.54) * mm, "end": v(-59.87, -10.57) * mm});
            skLineSegment(sketch, "E1617", {"start": v(-59.87, -10.57) * mm, "end": v(-59.7, -10.6) * mm});
            skLineSegment(sketch, "E1618", {"start": v(-59.7, -10.6) * mm, "end": v(-59.54, -10.62) * mm});
            skLineSegment(sketch, "E1619", {"start": v(-59.54, -10.62) * mm, "end": v(-59.38, -10.64) * mm});
            skArc(sketch, "E1620", {"start": v(-59.38, -10.64) * mm, "mid": v(-59.25, -11.3) * mm, "end": v(-59.13, -11.97) * mm});
            skLineSegment(sketch, "E1621", {"start": v(-59.13, -11.97) * mm, "end": v(-59.26, -12.04) * mm});
            skLineSegment(sketch, "E1622", {"start": v(-59.26, -12.04) * mm, "end": v(-59.4, -12.13) * mm});
            skLineSegment(sketch, "E1623", {"start": v(-59.4, -12.13) * mm, "end": v(-59.55, -12.21) * mm});
            skLineSegment(sketch, "E1624", {"start": v(-59.55, -12.21) * mm, "end": v(-59.7, -12.3) * mm});
            skLineSegment(sketch, "E1625", {"start": v(-59.7, -12.3) * mm, "end": v(-59.85, -12.4) * mm});
            skLineSegment(sketch, "E1626", {"start": v(-59.85, -12.4) * mm, "end": v(-60, -12.49) * mm});
            skLineSegment(sketch, "E1627", {"start": v(-60, -12.49) * mm, "end": v(-60.17, -12.58) * mm});
            skLineSegment(sketch, "E1628", {"start": v(-60.17, -12.58) * mm, "end": v(-60.33, -12.69) * mm});
            skLineSegment(sketch, "E1629", {"start": v(-60.33, -12.69) * mm, "end": v(-60.5, -12.8) * mm});
            skLineSegment(sketch, "E1630", {"start": v(-60.5, -12.8) * mm, "end": v(-60.66, -12.9) * mm});
            skLineSegment(sketch, "E1631", {"start": v(-60.66, -12.9) * mm, "end": v(-60.83, -13.02) * mm});
            skLineSegment(sketch, "E1632", {"start": v(-60.83, -13.02) * mm, "end": v(-61, -13.14) * mm});
            skLineSegment(sketch, "E1633", {"start": v(-61, -13.14) * mm, "end": v(-61.17, -13.26) * mm});
            skLineSegment(sketch, "E1634", {"start": v(-61.17, -13.26) * mm, "end": v(-61.35, -13.39) * mm});
            skLineSegment(sketch, "E1635", {"start": v(-61.35, -13.39) * mm, "end": v(-61.53, -13.52) * mm});
            skLineSegment(sketch, "E1636", {"start": v(-61.53, -13.52) * mm, "end": v(-61.7, -13.65) * mm});
            skLineSegment(sketch, "E1637", {"start": v(-61.7, -13.65) * mm, "end": v(-61.9, -13.8) * mm});
            skLineSegment(sketch, "E1638", {"start": v(-61.9, -13.8) * mm, "end": v(-62.08, -13.93) * mm});
            skLineSegment(sketch, "E1639", {"start": v(-62.08, -13.93) * mm, "end": v(-62.26, -14.08) * mm});
            skLineSegment(sketch, "E1640", {"start": v(-62.26, -14.08) * mm, "end": v(-62.45, -14.23) * mm});
            skLineSegment(sketch, "E1641", {"start": v(-62.45, -14.23) * mm, "end": v(-62.65, -14.39) * mm});
            skLineSegment(sketch, "E1642", {"start": v(-62.65, -14.39) * mm, "end": v(-62.84, -14.55) * mm});
            skLineSegment(sketch, "E1643", {"start": v(-62.84, -14.55) * mm, "end": v(-63.04, -14.71) * mm});
            skLineSegment(sketch, "E1644", {"start": v(-63.04, -14.71) * mm, "end": v(-63.23, -14.88) * mm});
            skLineSegment(sketch, "E1645", {"start": v(-63.23, -14.88) * mm, "end": v(-63.43, -15.06) * mm});
            skLineSegment(sketch, "E1646", {"start": v(-63.43, -15.06) * mm, "end": v(-63.64, -15.24) * mm});
            skLineSegment(sketch, "E1647", {"start": v(-63.64, -15.24) * mm, "end": v(-63.84, -15.42) * mm});
            skLineSegment(sketch, "E1648", {"start": v(-63.84, -15.42) * mm, "end": v(-64.04, -15.61) * mm});
            skLineSegment(sketch, "E1649", {"start": v(-64.04, -15.61) * mm, "end": v(-64.15, -15.7) * mm});
            skLineSegment(sketch, "E1650", {"start": v(-64.15, -15.7) * mm, "end": v(-63.78, -17.14) * mm});
            skLineSegment(sketch, "E1651", {"start": v(-63.78, -17.14) * mm, "end": v(-63.64, -17.17) * mm});
            skLineSegment(sketch, "E1652", {"start": v(-63.64, -17.17) * mm, "end": v(-63.37, -17.24) * mm});
            skLineSegment(sketch, "E1653", {"start": v(-63.37, -17.24) * mm, "end": v(-63.1, -17.3) * mm});
            skLineSegment(sketch, "E1654", {"start": v(-63.1, -17.3) * mm, "end": v(-62.84, -17.36) * mm});
            skLineSegment(sketch, "E1655", {"start": v(-62.84, -17.36) * mm, "end": v(-62.58, -17.42) * mm});
            skLineSegment(sketch, "E1656", {"start": v(-62.58, -17.42) * mm, "end": v(-62.33, -17.47) * mm});
            skLineSegment(sketch, "E1657", {"start": v(-62.33, -17.47) * mm, "end": v(-62.08, -17.52) * mm});
            skLineSegment(sketch, "E1658", {"start": v(-62.08, -17.52) * mm, "end": v(-61.83, -17.57) * mm});
            skLineSegment(sketch, "E1659", {"start": v(-61.83, -17.57) * mm, "end": v(-61.59, -17.62) * mm});
            skLineSegment(sketch, "E1660", {"start": v(-61.59, -17.62) * mm, "end": v(-61.35, -17.66) * mm});
            skLineSegment(sketch, "E1661", {"start": v(-61.35, -17.66) * mm, "end": v(-61.1, -17.7) * mm});
            skLineSegment(sketch, "E1662", {"start": v(-61.1, -17.7) * mm, "end": v(-60.88, -17.73) * mm});
            skLineSegment(sketch, "E1663", {"start": v(-60.88, -17.73) * mm, "end": v(-60.65, -17.76) * mm});
            skLineSegment(sketch, "E1664", {"start": v(-60.65, -17.76) * mm, "end": v(-60.43, -17.8) * mm});
            skLineSegment(sketch, "E1665", {"start": v(-60.43, -17.8) * mm, "end": v(-60.2, -17.82) * mm});
            skLineSegment(sketch, "E1666", {"start": v(-60.2, -17.82) * mm, "end": v(-60, -17.85) * mm});
            skLineSegment(sketch, "E1667", {"start": v(-60, -17.85) * mm, "end": v(-59.78, -17.87) * mm});
            skLineSegment(sketch, "E1668", {"start": v(-59.78, -17.87) * mm, "end": v(-59.57, -17.9) * mm});
            skLineSegment(sketch, "E1669", {"start": v(-59.57, -17.9) * mm, "end": v(-59.37, -17.91) * mm});
            skLineSegment(sketch, "E1670", {"start": v(-59.37, -17.91) * mm, "end": v(-59.17, -17.93) * mm});
            skLineSegment(sketch, "E1671", {"start": v(-59.17, -17.93) * mm, "end": v(-58.98, -17.94) * mm});
            skLineSegment(sketch, "E1672", {"start": v(-58.98, -17.94) * mm, "end": v(-58.79, -17.96) * mm});
            skLineSegment(sketch, "E1673", {"start": v(-58.79, -17.96) * mm, "end": v(-58.6, -17.97) * mm});
            skLineSegment(sketch, "E1674", {"start": v(-58.6, -17.97) * mm, "end": v(-58.42, -17.98) * mm});
            skLineSegment(sketch, "E1675", {"start": v(-58.42, -17.98) * mm, "end": v(-58.24, -17.98) * mm});
            skLineSegment(sketch, "E1676", {"start": v(-58.24, -17.98) * mm, "end": v(-58.07, -18) * mm});
            skLineSegment(sketch, "E1677", {"start": v(-58.07, -18) * mm, "end": v(-57.9, -18) * mm});
            skLineSegment(sketch, "E1678", {"start": v(-57.9, -18) * mm, "end": v(-57.74, -18) * mm});
            skLineSegment(sketch, "E1679", {"start": v(-57.74, -18) * mm, "end": v(-57.58, -18) * mm});
            skArc(sketch, "E1680", {"start": v(-57.58, -18) * mm, "mid": v(-57.37, -18.64) * mm, "end": v(-57.16, -19.28) * mm});
            skLineSegment(sketch, "E1681", {"start": v(-57.16, -19.28) * mm, "end": v(-57.29, -19.38) * mm});
            skLineSegment(sketch, "E1682", {"start": v(-57.29, -19.38) * mm, "end": v(-57.42, -19.48) * mm});
            skLineSegment(sketch, "E1683", {"start": v(-57.42, -19.48) * mm, "end": v(-57.55, -19.58) * mm});
            skLineSegment(sketch, "E1684", {"start": v(-57.55, -19.58) * mm, "end": v(-57.7, -19.68) * mm});
            skLineSegment(sketch, "E1685", {"start": v(-57.7, -19.68) * mm, "end": v(-57.83, -19.8) * mm});
            skLineSegment(sketch, "E1686", {"start": v(-57.83, -19.8) * mm, "end": v(-57.97, -19.9) * mm});
            skLineSegment(sketch, "E1687", {"start": v(-57.97, -19.9) * mm, "end": v(-58.12, -20.03) * mm});
            skLineSegment(sketch, "E1688", {"start": v(-58.12, -20.03) * mm, "end": v(-58.26, -20.15) * mm});
            skLineSegment(sketch, "E1689", {"start": v(-58.26, -20.15) * mm, "end": v(-58.41, -20.27) * mm});
            skLineSegment(sketch, "E1690", {"start": v(-58.41, -20.27) * mm, "end": v(-58.56, -20.4) * mm});
            skLineSegment(sketch, "E1691", {"start": v(-58.56, -20.4) * mm, "end": v(-58.71, -20.54) * mm});
            skLineSegment(sketch, "E1692", {"start": v(-58.71, -20.54) * mm, "end": v(-58.87, -20.68) * mm});
            skLineSegment(sketch, "E1693", {"start": v(-58.87, -20.68) * mm, "end": v(-59.03, -20.82) * mm});
            skLineSegment(sketch, "E1694", {"start": v(-59.03, -20.82) * mm, "end": v(-59.19, -20.97) * mm});
            skLineSegment(sketch, "E1695", {"start": v(-59.19, -20.97) * mm, "end": v(-59.35, -21.12) * mm});
            skLineSegment(sketch, "E1696", {"start": v(-59.35, -21.12) * mm, "end": v(-59.5, -21.28) * mm});
            skLineSegment(sketch, "E1697", {"start": v(-59.5, -21.28) * mm, "end": v(-59.67, -21.44) * mm});
            skLineSegment(sketch, "E1698", {"start": v(-59.67, -21.44) * mm, "end": v(-59.84, -21.6) * mm});
            skLineSegment(sketch, "E1699", {"start": v(-59.84, -21.6) * mm, "end": v(-60, -21.77) * mm});
            skLineSegment(sketch, "E1700", {"start": v(-60, -21.77) * mm, "end": v(-60.18, -21.95) * mm});
            skLineSegment(sketch, "E1701", {"start": v(-60.18, -21.95) * mm, "end": v(-60.35, -22.13) * mm});
            skLineSegment(sketch, "E1702", {"start": v(-60.35, -22.13) * mm, "end": v(-60.52, -22.31) * mm});
            skLineSegment(sketch, "E1703", {"start": v(-60.52, -22.31) * mm, "end": v(-60.7, -22.5) * mm});
            skLineSegment(sketch, "E1704", {"start": v(-60.7, -22.5) * mm, "end": v(-60.87, -22.7) * mm});
            skLineSegment(sketch, "E1705", {"start": v(-60.87, -22.7) * mm, "end": v(-61.05, -22.9) * mm});
            skLineSegment(sketch, "E1706", {"start": v(-61.05, -22.9) * mm, "end": v(-61.22, -23.1) * mm});
            skLineSegment(sketch, "E1707", {"start": v(-61.22, -23.1) * mm, "end": v(-61.4, -23.3) * mm});
            skLineSegment(sketch, "E1708", {"start": v(-61.4, -23.3) * mm, "end": v(-61.58, -23.51) * mm});
            skLineSegment(sketch, "E1709", {"start": v(-61.58, -23.51) * mm, "end": v(-61.67, -23.62) * mm});
            skLineSegment(sketch, "E1710", {"start": v(-61.67, -23.62) * mm, "end": v(-61.13, -25) * mm});
            skLineSegment(sketch, "E1711", {"start": v(-61.13, -25) * mm, "end": v(-60.99, -25.01) * mm});
            skLineSegment(sketch, "E1712", {"start": v(-60.99, -25.01) * mm, "end": v(-60.71, -25.05) * mm});
            skLineSegment(sketch, "E1713", {"start": v(-60.71, -25.05) * mm, "end": v(-60.44, -25.08) * mm});
            skLineSegment(sketch, "E1714", {"start": v(-60.44, -25.08) * mm, "end": v(-60.17, -25.1) * mm});
            skLineSegment(sketch, "E1715", {"start": v(-60.17, -25.1) * mm, "end": v(-59.9, -25.13) * mm});
            skLineSegment(sketch, "E1716", {"start": v(-59.9, -25.13) * mm, "end": v(-59.65, -25.15) * mm});
            skLineSegment(sketch, "E1717", {"start": v(-59.65, -25.15) * mm, "end": v(-59.4, -25.17) * mm});
            skLineSegment(sketch, "E1718", {"start": v(-59.4, -25.17) * mm, "end": v(-59.14, -25.18) * mm});
            skLineSegment(sketch, "E1719", {"start": v(-59.14, -25.18) * mm, "end": v(-58.9, -25.2) * mm});
            skLineSegment(sketch, "E1720", {"start": v(-58.9, -25.2) * mm, "end": v(-58.65, -25.2) * mm});
            skLineSegment(sketch, "E1721", {"start": v(-58.65, -25.2) * mm, "end": v(-58.41, -25.22) * mm});
            skLineSegment(sketch, "E1722", {"start": v(-58.41, -25.22) * mm, "end": v(-58.18, -25.22) * mm});
            skLineSegment(sketch, "E1723", {"start": v(-58.18, -25.22) * mm, "end": v(-57.95, -25.23) * mm});
            skLineSegment(sketch, "E1724", {"start": v(-57.95, -25.23) * mm, "end": v(-57.72, -25.23) * mm});
            skLineSegment(sketch, "E1725", {"start": v(-57.72, -25.23) * mm, "end": v(-57.5, -25.23) * mm});
            skLineSegment(sketch, "E1726", {"start": v(-57.5, -25.23) * mm, "end": v(-57.28, -25.23) * mm});
            skLineSegment(sketch, "E1727", {"start": v(-57.28, -25.23) * mm, "end": v(-57.07, -25.22) * mm});
            skLineSegment(sketch, "E1728", {"start": v(-57.07, -25.22) * mm, "end": v(-56.86, -25.22) * mm});
            skLineSegment(sketch, "E1729", {"start": v(-56.86, -25.22) * mm, "end": v(-56.66, -25.21) * mm});
            skLineSegment(sketch, "E1730", {"start": v(-56.66, -25.21) * mm, "end": v(-56.46, -25.2) * mm});
            skLineSegment(sketch, "E1731", {"start": v(-56.46, -25.2) * mm, "end": v(-56.26, -25.2) * mm});
            skLineSegment(sketch, "E1732", {"start": v(-56.26, -25.2) * mm, "end": v(-56.07, -25.18) * mm});
            skLineSegment(sketch, "E1733", {"start": v(-56.07, -25.18) * mm, "end": v(-55.89, -25.17) * mm});
            skLineSegment(sketch, "E1734", {"start": v(-55.89, -25.17) * mm, "end": v(-55.7, -25.16) * mm});
            skLineSegment(sketch, "E1735", {"start": v(-55.7, -25.16) * mm, "end": v(-55.53, -25.14) * mm});
            skLineSegment(sketch, "E1736", {"start": v(-55.53, -25.14) * mm, "end": v(-55.36, -25.13) * mm});
            skLineSegment(sketch, "E1737", {"start": v(-55.36, -25.13) * mm, "end": v(-55.19, -25.1) * mm});
            skLineSegment(sketch, "E1738", {"start": v(-55.19, -25.1) * mm, "end": v(-55.03, -25.1) * mm});
            skLineSegment(sketch, "E1739", {"start": v(-55.03, -25.1) * mm, "end": v(-54.87, -25.07) * mm});
            skArc(sketch, "E1740", {"start": v(-54.87, -25.07) * mm, "mid": v(-54.58, -25.68) * mm, "end": v(-54.3, -26.3) * mm});
            skLineSegment(sketch, "E1741", {"start": v(-54.3, -26.3) * mm, "end": v(-54.4, -26.4) * mm});
            skLineSegment(sketch, "E1742", {"start": v(-54.4, -26.4) * mm, "end": v(-54.53, -26.52) * mm});
            skLineSegment(sketch, "E1743", {"start": v(-54.53, -26.52) * mm, "end": v(-54.65, -26.64) * mm});
            skLineSegment(sketch, "E1744", {"start": v(-54.65, -26.64) * mm, "end": v(-54.77, -26.76) * mm});
            skLineSegment(sketch, "E1745", {"start": v(-54.77, -26.76) * mm, "end": v(-54.9, -26.89) * mm});
            skLineSegment(sketch, "E1746", {"start": v(-54.9, -26.89) * mm, "end": v(-55.02, -27.02) * mm});
            skLineSegment(sketch, "E1747", {"start": v(-55.02, -27.02) * mm, "end": v(-55.15, -27.15) * mm});
            skLineSegment(sketch, "E1748", {"start": v(-55.15, -27.15) * mm, "end": v(-55.28, -27.3) * mm});
            skLineSegment(sketch, "E1749", {"start": v(-55.28, -27.3) * mm, "end": v(-55.4, -27.44) * mm});
            skLineSegment(sketch, "E1750", {"start": v(-55.4, -27.44) * mm, "end": v(-55.54, -27.58) * mm});
            skLineSegment(sketch, "E1751", {"start": v(-55.54, -27.58) * mm, "end": v(-55.68, -27.74) * mm});
            skLineSegment(sketch, "E1752", {"start": v(-55.68, -27.74) * mm, "end": v(-55.81, -27.9) * mm});
            skLineSegment(sketch, "E1753", {"start": v(-55.81, -27.9) * mm, "end": v(-55.95, -28.06) * mm});
            skLineSegment(sketch, "E1754", {"start": v(-55.95, -28.06) * mm, "end": v(-56.1, -28.22) * mm});
            skLineSegment(sketch, "E1755", {"start": v(-56.1, -28.22) * mm, "end": v(-56.23, -28.4) * mm});
            skLineSegment(sketch, "E1756", {"start": v(-56.23, -28.4) * mm, "end": v(-56.37, -28.57) * mm});
            skLineSegment(sketch, "E1757", {"start": v(-56.37, -28.57) * mm, "end": v(-56.52, -28.75) * mm});
            skLineSegment(sketch, "E1758", {"start": v(-56.52, -28.75) * mm, "end": v(-56.66, -28.93) * mm});
            skLineSegment(sketch, "E1759", {"start": v(-56.66, -28.93) * mm, "end": v(-56.8, -29.12) * mm});
            skLineSegment(sketch, "E1760", {"start": v(-56.8, -29.12) * mm, "end": v(-56.95, -29.32) * mm});
            skLineSegment(sketch, "E1761", {"start": v(-56.95, -29.32) * mm, "end": v(-57.1, -29.52) * mm});
            skLineSegment(sketch, "E1762", {"start": v(-57.1, -29.52) * mm, "end": v(-57.25, -29.72) * mm});
            skLineSegment(sketch, "E1763", {"start": v(-57.25, -29.72) * mm, "end": v(-57.4, -29.93) * mm});
            skLineSegment(sketch, "E1764", {"start": v(-57.4, -29.93) * mm, "end": v(-57.55, -30.14) * mm});
            skLineSegment(sketch, "E1765", {"start": v(-57.55, -30.14) * mm, "end": v(-57.7, -30.36) * mm});
            skLineSegment(sketch, "E1766", {"start": v(-57.7, -30.36) * mm, "end": v(-57.85, -30.58) * mm});
            skLineSegment(sketch, "E1767", {"start": v(-57.85, -30.58) * mm, "end": v(-58, -30.81) * mm});
            skLineSegment(sketch, "E1768", {"start": v(-58, -30.81) * mm, "end": v(-58.15, -31.05) * mm});
            skLineSegment(sketch, "E1769", {"start": v(-58.15, -31.05) * mm, "end": v(-58.22, -31.16) * mm});
            skLineSegment(sketch, "E1770", {"start": v(-58.22, -31.16) * mm, "end": v(-57.51, -32.46) * mm});
            skLineSegment(sketch, "E1771", {"start": v(-57.51, -32.46) * mm, "end": v(-57.37, -32.46) * mm});
            skLineSegment(sketch, "E1772", {"start": v(-57.37, -32.46) * mm, "end": v(-57.1, -32.46) * mm});
            skLineSegment(sketch, "E1773", {"start": v(-57.1, -32.46) * mm, "end": v(-56.82, -32.45) * mm});
            skLineSegment(sketch, "E1774", {"start": v(-56.82, -32.45) * mm, "end": v(-56.55, -32.45) * mm});
            skLineSegment(sketch, "E1775", {"start": v(-56.55, -32.45) * mm, "end": v(-56.28, -32.44) * mm});
            skLineSegment(sketch, "E1776", {"start": v(-56.28, -32.44) * mm, "end": v(-56.02, -32.42) * mm});
            skLineSegment(sketch, "E1777", {"start": v(-56.02, -32.42) * mm, "end": v(-55.77, -32.41) * mm});
            skLineSegment(sketch, "E1778", {"start": v(-55.77, -32.41) * mm, "end": v(-55.52, -32.4) * mm});
            skLineSegment(sketch, "E1779", {"start": v(-55.52, -32.4) * mm, "end": v(-55.27, -32.38) * mm});
            skLineSegment(sketch, "E1780", {"start": v(-55.27, -32.38) * mm, "end": v(-55.03, -32.36) * mm});
            skLineSegment(sketch, "E1781", {"start": v(-55.03, -32.36) * mm, "end": v(-54.79, -32.34) * mm});
            skLineSegment(sketch, "E1782", {"start": v(-54.79, -32.34) * mm, "end": v(-54.56, -32.31) * mm});
            skLineSegment(sketch, "E1783", {"start": v(-54.56, -32.31) * mm, "end": v(-54.33, -32.29) * mm});
            skLineSegment(sketch, "E1784", {"start": v(-54.33, -32.29) * mm, "end": v(-54.1, -32.26) * mm});
            skLineSegment(sketch, "E1785", {"start": v(-54.1, -32.26) * mm, "end": v(-53.88, -32.24) * mm});
            skLineSegment(sketch, "E1786", {"start": v(-53.88, -32.24) * mm, "end": v(-53.67, -32.2) * mm});
            skLineSegment(sketch, "E1787", {"start": v(-53.67, -32.2) * mm, "end": v(-53.46, -32.18) * mm});
            skLineSegment(sketch, "E1788", {"start": v(-53.46, -32.18) * mm, "end": v(-53.25, -32.15) * mm});
            skLineSegment(sketch, "E1789", {"start": v(-53.25, -32.15) * mm, "end": v(-53.05, -32.12) * mm});
            skLineSegment(sketch, "E1790", {"start": v(-53.05, -32.12) * mm, "end": v(-52.85, -32.08) * mm});
            skLineSegment(sketch, "E1791", {"start": v(-52.85, -32.08) * mm, "end": v(-52.66, -32.05) * mm});
            skLineSegment(sketch, "E1792", {"start": v(-52.66, -32.05) * mm, "end": v(-52.47, -32.01) * mm});
            skLineSegment(sketch, "E1793", {"start": v(-52.47, -32.01) * mm, "end": v(-52.3, -31.98) * mm});
            skLineSegment(sketch, "E1794", {"start": v(-52.3, -31.98) * mm, "end": v(-52.11, -31.94) * mm});
            skLineSegment(sketch, "E1795", {"start": v(-52.11, -31.94) * mm, "end": v(-51.94, -31.9) * mm});
            skLineSegment(sketch, "E1796", {"start": v(-51.94, -31.9) * mm, "end": v(-51.77, -31.87) * mm});
            skLineSegment(sketch, "E1797", {"start": v(-51.77, -31.87) * mm, "end": v(-51.6, -31.83) * mm});
            skLineSegment(sketch, "E1798", {"start": v(-51.6, -31.83) * mm, "end": v(-51.45, -31.79) * mm});
            skLineSegment(sketch, "E1799", {"start": v(-51.45, -31.79) * mm, "end": v(-51.3, -31.75) * mm});
            skArc(sketch, "E1800", {"start": v(-51.3, -31.75) * mm, "mid": v(-50.93, -32.32) * mm, "end": v(-50.57, -32.9) * mm});
            skLineSegment(sketch, "E1801", {"start": v(-50.57, -32.9) * mm, "end": v(-50.67, -33.02) * mm});
            skLineSegment(sketch, "E1802", {"start": v(-50.67, -33.02) * mm, "end": v(-50.77, -33.14) * mm});
            skLineSegment(sketch, "E1803", {"start": v(-50.77, -33.14) * mm, "end": v(-50.88, -33.28) * mm});
            skLineSegment(sketch, "E1804", {"start": v(-50.88, -33.28) * mm, "end": v(-50.98, -33.41) * mm});
            skLineSegment(sketch, "E1805", {"start": v(-50.98, -33.41) * mm, "end": v(-51.09, -33.55) * mm});
            skLineSegment(sketch, "E1806", {"start": v(-51.09, -33.55) * mm, "end": v(-51.2, -33.7) * mm});
            skLineSegment(sketch, "E1807", {"start": v(-51.2, -33.7) * mm, "end": v(-51.3, -33.85) * mm});
            skLineSegment(sketch, "E1808", {"start": v(-51.3, -33.85) * mm, "end": v(-51.42, -34) * mm});
            skLineSegment(sketch, "E1809", {"start": v(-51.42, -34) * mm, "end": v(-51.53, -34.16) * mm});
            skLineSegment(sketch, "E1810", {"start": v(-51.53, -34.16) * mm, "end": v(-51.65, -34.33) * mm});
            skLineSegment(sketch, "E1811", {"start": v(-51.65, -34.33) * mm, "end": v(-51.76, -34.5) * mm});
            skLineSegment(sketch, "E1812", {"start": v(-51.76, -34.5) * mm, "end": v(-51.88, -34.67) * mm});
            skLineSegment(sketch, "E1813", {"start": v(-51.88, -34.67) * mm, "end": v(-52, -34.85) * mm});
            skLineSegment(sketch, "E1814", {"start": v(-52, -34.85) * mm, "end": v(-52.11, -35.03) * mm});
            skLineSegment(sketch, "E1815", {"start": v(-52.11, -35.03) * mm, "end": v(-52.23, -35.22) * mm});
            skLineSegment(sketch, "E1816", {"start": v(-52.23, -35.22) * mm, "end": v(-52.35, -35.4) * mm});
            skLineSegment(sketch, "E1817", {"start": v(-52.35, -35.4) * mm, "end": v(-52.47, -35.6) * mm});
            skLineSegment(sketch, "E1818", {"start": v(-52.47, -35.6) * mm, "end": v(-52.59, -35.8) * mm});
            skLineSegment(sketch, "E1819", {"start": v(-52.59, -35.8) * mm, "end": v(-52.7, -36.01) * mm});
            skLineSegment(sketch, "E1820", {"start": v(-52.7, -36.01) * mm, "end": v(-52.83, -36.22) * mm});
            skLineSegment(sketch, "E1821", {"start": v(-52.83, -36.22) * mm, "end": v(-52.95, -36.44) * mm});
            skLineSegment(sketch, "E1822", {"start": v(-52.95, -36.44) * mm, "end": v(-53.07, -36.66) * mm});
            skLineSegment(sketch, "E1823", {"start": v(-53.07, -36.66) * mm, "end": v(-53.2, -36.89) * mm});
            skLineSegment(sketch, "E1824", {"start": v(-53.2, -36.89) * mm, "end": v(-53.31, -37.12) * mm});
            skLineSegment(sketch, "E1825", {"start": v(-53.31, -37.12) * mm, "end": v(-53.44, -37.35) * mm});
            skLineSegment(sketch, "E1826", {"start": v(-53.44, -37.35) * mm, "end": v(-53.56, -37.6) * mm});
            skLineSegment(sketch, "E1827", {"start": v(-53.56, -37.6) * mm, "end": v(-53.68, -37.84) * mm});
            skLineSegment(sketch, "E1828", {"start": v(-53.68, -37.84) * mm, "end": v(-53.8, -38.09) * mm});
            skLineSegment(sketch, "E1829", {"start": v(-53.8, -38.09) * mm, "end": v(-53.86, -38.22) * mm});
            skLineSegment(sketch, "E1830", {"start": v(-53.86, -38.22) * mm, "end": v(-52.99, -39.41) * mm});
            skLineSegment(sketch, "E1831", {"start": v(-52.99, -39.41) * mm, "end": v(-52.85, -39.4) * mm});
            skLineSegment(sketch, "E1832", {"start": v(-52.85, -39.4) * mm, "end": v(-52.57, -39.36) * mm});
            skLineSegment(sketch, "E1833", {"start": v(-52.57, -39.36) * mm, "end": v(-52.3, -39.32) * mm});
            skLineSegment(sketch, "E1834", {"start": v(-52.3, -39.32) * mm, "end": v(-52.04, -39.28) * mm});
            skLineSegment(sketch, "E1835", {"start": v(-52.04, -39.28) * mm, "end": v(-51.78, -39.23) * mm});
            skLineSegment(sketch, "E1836", {"start": v(-51.78, -39.23) * mm, "end": v(-51.52, -39.2) * mm});
            skLineSegment(sketch, "E1837", {"start": v(-51.52, -39.2) * mm, "end": v(-51.27, -39.14) * mm});
            skLineSegment(sketch, "E1838", {"start": v(-51.27, -39.14) * mm, "end": v(-51.02, -39.1) * mm});
            skLineSegment(sketch, "E1839", {"start": v(-51.02, -39.1) * mm, "end": v(-50.78, -39.05) * mm});
            skLineSegment(sketch, "E1840", {"start": v(-50.78, -39.05) * mm, "end": v(-50.54, -39) * mm});
            skLineSegment(sketch, "E1841", {"start": v(-50.54, -39) * mm, "end": v(-50.3, -38.95) * mm});
            skLineSegment(sketch, "E1842", {"start": v(-50.3, -38.95) * mm, "end": v(-50.08, -38.9) * mm});
            skLineSegment(sketch, "E1843", {"start": v(-50.08, -38.9) * mm, "end": v(-49.85, -38.84) * mm});
            skLineSegment(sketch, "E1844", {"start": v(-49.85, -38.84) * mm, "end": v(-49.63, -38.8) * mm});
            skLineSegment(sketch, "E1845", {"start": v(-49.63, -38.8) * mm, "end": v(-49.42, -38.74) * mm});
            skLineSegment(sketch, "E1846", {"start": v(-49.42, -38.74) * mm, "end": v(-49.2, -38.68) * mm});
            skLineSegment(sketch, "E1847", {"start": v(-49.2, -38.68) * mm, "end": v(-49, -38.62) * mm});
            skLineSegment(sketch, "E1848", {"start": v(-49, -38.62) * mm, "end": v(-48.8, -38.57) * mm});
            skLineSegment(sketch, "E1849", {"start": v(-48.8, -38.57) * mm, "end": v(-48.6, -38.51) * mm});
            skLineSegment(sketch, "E1850", {"start": v(-48.6, -38.51) * mm, "end": v(-48.42, -38.45) * mm});
            skLineSegment(sketch, "E1851", {"start": v(-48.42, -38.45) * mm, "end": v(-48.23, -38.4) * mm});
            skLineSegment(sketch, "E1852", {"start": v(-48.23, -38.4) * mm, "end": v(-48.05, -38.34) * mm});
            skLineSegment(sketch, "E1853", {"start": v(-48.05, -38.34) * mm, "end": v(-47.87, -38.28) * mm});
            skLineSegment(sketch, "E1854", {"start": v(-47.87, -38.28) * mm, "end": v(-47.7, -38.22) * mm});
            skLineSegment(sketch, "E1855", {"start": v(-47.7, -38.22) * mm, "end": v(-47.53, -38.16) * mm});
            skLineSegment(sketch, "E1856", {"start": v(-47.53, -38.16) * mm, "end": v(-47.37, -38.1) * mm});
            skLineSegment(sketch, "E1857", {"start": v(-47.37, -38.1) * mm, "end": v(-47.21, -38.05) * mm});
            skLineSegment(sketch, "E1858", {"start": v(-47.21, -38.05) * mm, "end": v(-47.06, -37.99) * mm});
            skLineSegment(sketch, "E1859", {"start": v(-47.06, -37.99) * mm, "end": v(-46.9, -37.93) * mm});
            skArc(sketch, "E1860", {"start": v(-46.9, -37.93) * mm, "mid": v(-46.48, -38.45) * mm, "end": v(-46.05, -38.97) * mm});
            skLineSegment(sketch, "E1861", {"start": v(-46.05, -38.97) * mm, "end": v(-46.13, -39.1) * mm});
            skLineSegment(sketch, "E1862", {"start": v(-46.13, -39.1) * mm, "end": v(-46.22, -39.25) * mm});
            skLineSegment(sketch, "E1863", {"start": v(-46.22, -39.25) * mm, "end": v(-46.3, -39.4) * mm});
            skLineSegment(sketch, "E1864", {"start": v(-46.3, -39.4) * mm, "end": v(-46.4, -39.54) * mm});
            skLineSegment(sketch, "E1865", {"start": v(-46.4, -39.54) * mm, "end": v(-46.48, -39.7) * mm});
            skLineSegment(sketch, "E1866", {"start": v(-46.48, -39.7) * mm, "end": v(-46.57, -39.85) * mm});
            skLineSegment(sketch, "E1867", {"start": v(-46.57, -39.85) * mm, "end": v(-46.66, -40.01) * mm});
            skLineSegment(sketch, "E1868", {"start": v(-46.66, -40.01) * mm, "end": v(-46.75, -40.18) * mm});
            skLineSegment(sketch, "E1869", {"start": v(-46.75, -40.18) * mm, "end": v(-46.84, -40.35) * mm});
            skLineSegment(sketch, "E1870", {"start": v(-46.84, -40.35) * mm, "end": v(-46.94, -40.53) * mm});
            skLineSegment(sketch, "E1871", {"start": v(-46.94, -40.53) * mm, "end": v(-47.03, -40.71) * mm});
            skLineSegment(sketch, "E1872", {"start": v(-47.03, -40.71) * mm, "end": v(-47.12, -40.9) * mm});
            skLineSegment(sketch, "E1873", {"start": v(-47.12, -40.9) * mm, "end": v(-47.22, -41.09) * mm});
            skLineSegment(sketch, "E1874", {"start": v(-47.22, -41.09) * mm, "end": v(-47.3, -41.28) * mm});
            skLineSegment(sketch, "E1875", {"start": v(-47.3, -41.28) * mm, "end": v(-47.4, -41.48) * mm});
            skLineSegment(sketch, "E1876", {"start": v(-47.4, -41.48) * mm, "end": v(-47.5, -41.7) * mm});
            skLineSegment(sketch, "E1877", {"start": v(-47.5, -41.7) * mm, "end": v(-47.6, -41.9) * mm});
            skLineSegment(sketch, "E1878", {"start": v(-47.6, -41.9) * mm, "end": v(-47.69, -42.12) * mm});
            skLineSegment(sketch, "E1879", {"start": v(-47.69, -42.12) * mm, "end": v(-47.78, -42.33) * mm});
            skLineSegment(sketch, "E1880", {"start": v(-47.78, -42.33) * mm, "end": v(-47.87, -42.56) * mm});
            skLineSegment(sketch, "E1881", {"start": v(-47.87, -42.56) * mm, "end": v(-47.97, -42.79) * mm});
            skLineSegment(sketch, "E1882", {"start": v(-47.97, -42.79) * mm, "end": v(-48.06, -43.02) * mm});
            skLineSegment(sketch, "E1883", {"start": v(-48.06, -43.02) * mm, "end": v(-48.15, -43.26) * mm});
            skLineSegment(sketch, "E1884", {"start": v(-48.15, -43.26) * mm, "end": v(-48.24, -43.5) * mm});
            skLineSegment(sketch, "E1885", {"start": v(-48.24, -43.5) * mm, "end": v(-48.33, -43.76) * mm});
            skLineSegment(sketch, "E1886", {"start": v(-48.33, -43.76) * mm, "end": v(-48.42, -44) * mm});
            skLineSegment(sketch, "E1887", {"start": v(-48.42, -44) * mm, "end": v(-48.51, -44.27) * mm});
            skLineSegment(sketch, "E1888", {"start": v(-48.51, -44.27) * mm, "end": v(-48.6, -44.53) * mm});
            skLineSegment(sketch, "E1889", {"start": v(-48.6, -44.53) * mm, "end": v(-48.64, -44.67) * mm});
            skLineSegment(sketch, "E1890", {"start": v(-48.64, -44.67) * mm, "end": v(-47.63, -45.74) * mm});
            skLineSegment(sketch, "E1891", {"start": v(-47.63, -45.74) * mm, "end": v(-47.5, -45.7) * mm});
            skLineSegment(sketch, "E1892", {"start": v(-47.5, -45.7) * mm, "end": v(-47.23, -45.64) * mm});
            skLineSegment(sketch, "E1893", {"start": v(-47.23, -45.64) * mm, "end": v(-46.96, -45.56) * mm});
            skLineSegment(sketch, "E1894", {"start": v(-46.96, -45.56) * mm, "end": v(-46.7, -45.49) * mm});
            skLineSegment(sketch, "E1895", {"start": v(-46.7, -45.49) * mm, "end": v(-46.45, -45.41) * mm});
            skLineSegment(sketch, "E1896", {"start": v(-46.45, -45.41) * mm, "end": v(-46.2, -45.34) * mm});
            skLineSegment(sketch, "E1897", {"start": v(-46.2, -45.34) * mm, "end": v(-45.96, -45.26) * mm});
            skLineSegment(sketch, "E1898", {"start": v(-45.96, -45.26) * mm, "end": v(-45.72, -45.18) * mm});
            skLineSegment(sketch, "E1899", {"start": v(-45.72, -45.18) * mm, "end": v(-45.48, -45.1) * mm});
            skLineSegment(sketch, "E1900", {"start": v(-45.48, -45.1) * mm, "end": v(-45.25, -45.03) * mm});
            skLineSegment(sketch, "E1901", {"start": v(-45.25, -45.03) * mm, "end": v(-45.03, -44.95) * mm});
            skLineSegment(sketch, "E1902", {"start": v(-45.03, -44.95) * mm, "end": v(-44.8, -44.87) * mm});
            skLineSegment(sketch, "E1903", {"start": v(-44.8, -44.87) * mm, "end": v(-44.6, -44.79) * mm});
            skLineSegment(sketch, "E1904", {"start": v(-44.6, -44.79) * mm, "end": v(-44.38, -44.7) * mm});
            skLineSegment(sketch, "E1905", {"start": v(-44.38, -44.7) * mm, "end": v(-44.17, -44.62) * mm});
            skLineSegment(sketch, "E1906", {"start": v(-44.17, -44.62) * mm, "end": v(-43.97, -44.54) * mm});
            skLineSegment(sketch, "E1907", {"start": v(-43.97, -44.54) * mm, "end": v(-43.78, -44.46) * mm});
            skLineSegment(sketch, "E1908", {"start": v(-43.78, -44.46) * mm, "end": v(-43.58, -44.38) * mm});
            skLineSegment(sketch, "E1909", {"start": v(-43.58, -44.38) * mm, "end": v(-43.4, -44.3) * mm});
            skLineSegment(sketch, "E1910", {"start": v(-43.4, -44.3) * mm, "end": v(-43.22, -44.22) * mm});
            skLineSegment(sketch, "E1911", {"start": v(-43.22, -44.22) * mm, "end": v(-43.04, -44.14) * mm});
            skLineSegment(sketch, "E1912", {"start": v(-43.04, -44.14) * mm, "end": v(-42.86, -44.06) * mm});
            skLineSegment(sketch, "E1913", {"start": v(-42.86, -44.06) * mm, "end": v(-42.7, -43.98) * mm});
            skLineSegment(sketch, "E1914", {"start": v(-42.7, -43.98) * mm, "end": v(-42.53, -43.9) * mm});
            skLineSegment(sketch, "E1915", {"start": v(-42.53, -43.9) * mm, "end": v(-42.37, -43.82) * mm});
            skLineSegment(sketch, "E1916", {"start": v(-42.37, -43.82) * mm, "end": v(-42.22, -43.74) * mm});
            skLineSegment(sketch, "E1917", {"start": v(-42.22, -43.74) * mm, "end": v(-42.07, -43.66) * mm});
            skLineSegment(sketch, "E1918", {"start": v(-42.07, -43.66) * mm, "end": v(-41.92, -43.59) * mm});
            skLineSegment(sketch, "E1919", {"start": v(-41.92, -43.59) * mm, "end": v(-41.79, -43.5) * mm});
            skArc(sketch, "E1920", {"start": v(-41.79, -43.5) * mm, "mid": v(-41.3, -43.97) * mm, "end": v(-40.8, -44.43) * mm});
            skLineSegment(sketch, "E1921", {"start": v(-40.8, -44.43) * mm, "end": v(-40.87, -44.58) * mm});
            skLineSegment(sketch, "E1922", {"start": v(-40.87, -44.58) * mm, "end": v(-40.93, -44.73) * mm});
            skLineSegment(sketch, "E1923", {"start": v(-40.93, -44.73) * mm, "end": v(-41, -44.88) * mm});
            skLineSegment(sketch, "E1924", {"start": v(-41, -44.88) * mm, "end": v(-41.07, -45.04) * mm});
            skLineSegment(sketch, "E1925", {"start": v(-41.07, -45.04) * mm, "end": v(-41.14, -45.2) * mm});
            skLineSegment(sketch, "E1926", {"start": v(-41.14, -45.2) * mm, "end": v(-41.2, -45.37) * mm});
            skLineSegment(sketch, "E1927", {"start": v(-41.2, -45.37) * mm, "end": v(-41.28, -45.55) * mm});
            skLineSegment(sketch, "E1928", {"start": v(-41.28, -45.55) * mm, "end": v(-41.35, -45.72) * mm});
            skLineSegment(sketch, "E1929", {"start": v(-41.35, -45.72) * mm, "end": v(-41.42, -45.9) * mm});
            skLineSegment(sketch, "E1930", {"start": v(-41.42, -45.9) * mm, "end": v(-41.49, -46.1) * mm});
            skLineSegment(sketch, "E1931", {"start": v(-41.49, -46.1) * mm, "end": v(-41.56, -46.28) * mm});
            skLineSegment(sketch, "E1932", {"start": v(-41.56, -46.28) * mm, "end": v(-41.63, -46.48) * mm});
            skLineSegment(sketch, "E1933", {"start": v(-41.63, -46.48) * mm, "end": v(-41.7, -46.68) * mm});
            skLineSegment(sketch, "E1934", {"start": v(-41.7, -46.68) * mm, "end": v(-41.76, -46.89) * mm});
            skLineSegment(sketch, "E1935", {"start": v(-41.76, -46.89) * mm, "end": v(-41.83, -47.1) * mm});
            skLineSegment(sketch, "E1936", {"start": v(-41.83, -47.1) * mm, "end": v(-41.9, -47.31) * mm});
            skLineSegment(sketch, "E1937", {"start": v(-41.9, -47.31) * mm, "end": v(-41.96, -47.53) * mm});
            skLineSegment(sketch, "E1938", {"start": v(-41.96, -47.53) * mm, "end": v(-42.03, -47.76) * mm});
            skLineSegment(sketch, "E1939", {"start": v(-42.03, -47.76) * mm, "end": v(-42.1, -47.99) * mm});
            skLineSegment(sketch, "E1940", {"start": v(-42.1, -47.99) * mm, "end": v(-42.16, -48.22) * mm});
            skLineSegment(sketch, "E1941", {"start": v(-42.16, -48.22) * mm, "end": v(-42.22, -48.46) * mm});
            skLineSegment(sketch, "E1942", {"start": v(-42.22, -48.46) * mm, "end": v(-42.29, -48.7) * mm});
            skLineSegment(sketch, "E1943", {"start": v(-42.29, -48.7) * mm, "end": v(-42.35, -48.96) * mm});
            skLineSegment(sketch, "E1944", {"start": v(-42.35, -48.96) * mm, "end": v(-42.4, -49.2) * mm});
            skLineSegment(sketch, "E1945", {"start": v(-42.4, -49.2) * mm, "end": v(-42.47, -49.47) * mm});
            skLineSegment(sketch, "E1946", {"start": v(-42.47, -49.47) * mm, "end": v(-42.53, -49.73) * mm});
            skLineSegment(sketch, "E1947", {"start": v(-42.53, -49.73) * mm, "end": v(-42.58, -50) * mm});
            skLineSegment(sketch, "E1948", {"start": v(-42.58, -50) * mm, "end": v(-42.64, -50.27) * mm});
            skLineSegment(sketch, "E1949", {"start": v(-42.64, -50.27) * mm, "end": v(-42.66, -50.41) * mm});
            skLineSegment(sketch, "E1950", {"start": v(-42.66, -50.41) * mm, "end": v(-41.52, -51.35) * mm});
            skLineSegment(sketch, "E1951", {"start": v(-41.52, -51.35) * mm, "end": v(-41.4, -51.3) * mm});
            skLineSegment(sketch, "E1952", {"start": v(-41.4, -51.3) * mm, "end": v(-41.14, -51.2) * mm});
            skLineSegment(sketch, "E1953", {"start": v(-41.14, -51.2) * mm, "end": v(-40.88, -51.1) * mm});
            skLineSegment(sketch, "E1954", {"start": v(-40.88, -51.1) * mm, "end": v(-40.63, -50.98) * mm});
            skLineSegment(sketch, "E1955", {"start": v(-40.63, -50.98) * mm, "end": v(-40.4, -50.88) * mm});
            skLineSegment(sketch, "E1956", {"start": v(-40.4, -50.88) * mm, "end": v(-40.15, -50.77) * mm});
            skLineSegment(sketch, "E1957", {"start": v(-40.15, -50.77) * mm, "end": v(-39.92, -50.66) * mm});
            skLineSegment(sketch, "E1958", {"start": v(-39.92, -50.66) * mm, "end": v(-39.7, -50.56) * mm});
            skLineSegment(sketch, "E1959", {"start": v(-39.7, -50.56) * mm, "end": v(-39.47, -50.45) * mm});
            skLineSegment(sketch, "E1960", {"start": v(-39.47, -50.45) * mm, "end": v(-39.25, -50.34) * mm});
            skLineSegment(sketch, "E1961", {"start": v(-39.25, -50.34) * mm, "end": v(-39.04, -50.24) * mm});
            skLineSegment(sketch, "E1962", {"start": v(-39.04, -50.24) * mm, "end": v(-38.83, -50.13) * mm});
            skLineSegment(sketch, "E1963", {"start": v(-38.83, -50.13) * mm, "end": v(-38.63, -50.02) * mm});
            skLineSegment(sketch, "E1964", {"start": v(-38.63, -50.02) * mm, "end": v(-38.43, -49.92) * mm});
            skLineSegment(sketch, "E1965", {"start": v(-38.43, -49.92) * mm, "end": v(-38.23, -49.8) * mm});
            skLineSegment(sketch, "E1966", {"start": v(-38.23, -49.8) * mm, "end": v(-38.04, -49.7) * mm});
            skLineSegment(sketch, "E1967", {"start": v(-38.04, -49.7) * mm, "end": v(-37.86, -49.6) * mm});
            skLineSegment(sketch, "E1968", {"start": v(-37.86, -49.6) * mm, "end": v(-37.68, -49.5) * mm});
            skLineSegment(sketch, "E1969", {"start": v(-37.68, -49.5) * mm, "end": v(-37.5, -49.39) * mm});
            skLineSegment(sketch, "E1970", {"start": v(-37.5, -49.39) * mm, "end": v(-37.33, -49.29) * mm});
            skLineSegment(sketch, "E1971", {"start": v(-37.33, -49.29) * mm, "end": v(-37.17, -49.18) * mm});
            skLineSegment(sketch, "E1972", {"start": v(-37.17, -49.18) * mm, "end": v(-37, -49.08) * mm});
            skLineSegment(sketch, "E1973", {"start": v(-37, -49.08) * mm, "end": v(-36.85, -48.98) * mm});
            skLineSegment(sketch, "E1974", {"start": v(-36.85, -48.98) * mm, "end": v(-36.7, -48.88) * mm});
            skLineSegment(sketch, "E1975", {"start": v(-36.7, -48.88) * mm, "end": v(-36.55, -48.78) * mm});
            skLineSegment(sketch, "E1976", {"start": v(-36.55, -48.78) * mm, "end": v(-36.4, -48.69) * mm});
            skLineSegment(sketch, "E1977", {"start": v(-36.4, -48.69) * mm, "end": v(-36.27, -48.6) * mm});
            skLineSegment(sketch, "E1978", {"start": v(-36.27, -48.6) * mm, "end": v(-36.13, -48.5) * mm});
            skLineSegment(sketch, "E1979", {"start": v(-36.13, -48.5) * mm, "end": v(-36, -48.4) * mm});
            skArc(sketch, "E1980", {"start": v(-36, -48.4) * mm, "mid": v(-35.46, -48.8) * mm, "end": v(-34.9, -49.2) * mm});
            skLineSegment(sketch, "E1981", {"start": v(-34.9, -49.2) * mm, "end": v(-34.96, -49.35) * mm});
            skLineSegment(sketch, "E1982", {"start": v(-34.96, -49.35) * mm, "end": v(-35, -49.5) * mm});
            skLineSegment(sketch, "E1983", {"start": v(-35, -49.5) * mm, "end": v(-35.05, -49.67) * mm});
            skLineSegment(sketch, "E1984", {"start": v(-35.05, -49.67) * mm, "end": v(-35.1, -49.83) * mm});
            skLineSegment(sketch, "E1985", {"start": v(-35.1, -49.83) * mm, "end": v(-35.15, -50) * mm});
            skLineSegment(sketch, "E1986", {"start": v(-35.15, -50) * mm, "end": v(-35.2, -50.18) * mm});
            skLineSegment(sketch, "E1987", {"start": v(-35.2, -50.18) * mm, "end": v(-35.24, -50.36) * mm});
            skLineSegment(sketch, "E1988", {"start": v(-35.24, -50.36) * mm, "end": v(-35.3, -50.55) * mm});
            skLineSegment(sketch, "E1989", {"start": v(-35.3, -50.55) * mm, "end": v(-35.34, -50.74) * mm});
            skLineSegment(sketch, "E1990", {"start": v(-35.34, -50.74) * mm, "end": v(-35.38, -50.93) * mm});
            skLineSegment(sketch, "E1991", {"start": v(-35.38, -50.93) * mm, "end": v(-35.43, -51.13) * mm});
            skLineSegment(sketch, "E1992", {"start": v(-35.43, -51.13) * mm, "end": v(-35.47, -51.33) * mm});
            skLineSegment(sketch, "E1993", {"start": v(-35.47, -51.33) * mm, "end": v(-35.51, -51.54) * mm});
            skLineSegment(sketch, "E1994", {"start": v(-35.51, -51.54) * mm, "end": v(-35.56, -51.75) * mm});
            skLineSegment(sketch, "E1995", {"start": v(-35.56, -51.75) * mm, "end": v(-35.6, -51.97) * mm});
            skLineSegment(sketch, "E1996", {"start": v(-35.6, -51.97) * mm, "end": v(-35.64, -52.2) * mm});
            skLineSegment(sketch, "E1997", {"start": v(-35.64, -52.2) * mm, "end": v(-35.68, -52.42) * mm});
            skLineSegment(sketch, "E1998", {"start": v(-35.68, -52.42) * mm, "end": v(-35.71, -52.65) * mm});
            skLineSegment(sketch, "E1999", {"start": v(-35.71, -52.65) * mm, "end": v(-35.75, -52.89) * mm});
            skLineSegment(sketch, "E2000", {"start": v(-35.75, -52.89) * mm, "end": v(-35.78, -53.13) * mm});
            skLineSegment(sketch, "E2001", {"start": v(-35.78, -53.13) * mm, "end": v(-35.82, -53.37) * mm});
            skLineSegment(sketch, "E2002", {"start": v(-35.82, -53.37) * mm, "end": v(-35.85, -53.62) * mm});
            skLineSegment(sketch, "E2003", {"start": v(-35.85, -53.62) * mm, "end": v(-35.88, -53.88) * mm});
            skLineSegment(sketch, "E2004", {"start": v(-35.88, -53.88) * mm, "end": v(-35.9, -54.14) * mm});
            skLineSegment(sketch, "E2005", {"start": v(-35.9, -54.14) * mm, "end": v(-35.93, -54.4) * mm});
            skLineSegment(sketch, "E2006", {"start": v(-35.93, -54.4) * mm, "end": v(-35.96, -54.67) * mm});
            skLineSegment(sketch, "E2007", {"start": v(-35.96, -54.67) * mm, "end": v(-35.98, -54.94) * mm});
            skLineSegment(sketch, "E2008", {"start": v(-35.98, -54.94) * mm, "end": v(-36, -55.22) * mm});
            skLineSegment(sketch, "E2009", {"start": v(-36, -55.22) * mm, "end": v(-36, -55.36) * mm});
            skLineSegment(sketch, "E2010", {"start": v(-36, -55.36) * mm, "end": v(-34.76, -56.15) * mm});
            skLineSegment(sketch, "E2011", {"start": v(-34.76, -56.15) * mm, "end": v(-34.64, -56.08) * mm});
            skLineSegment(sketch, "E2012", {"start": v(-34.64, -56.08) * mm, "end": v(-34.4, -55.95) * mm});
            skLineSegment(sketch, "E2013", {"start": v(-34.4, -55.95) * mm, "end": v(-34.16, -55.81) * mm});
            skLineSegment(sketch, "E2014", {"start": v(-34.16, -55.81) * mm, "end": v(-33.92, -55.68) * mm});
            skLineSegment(sketch, "E2015", {"start": v(-33.92, -55.68) * mm, "end": v(-33.7, -55.54) * mm});
            skLineSegment(sketch, "E2016", {"start": v(-33.7, -55.54) * mm, "end": v(-33.47, -55.4) * mm});
            skLineSegment(sketch, "E2017", {"start": v(-33.47, -55.4) * mm, "end": v(-33.26, -55.27) * mm});
            skLineSegment(sketch, "E2018", {"start": v(-33.26, -55.27) * mm, "end": v(-33.04, -55.13) * mm});
            skLineSegment(sketch, "E2019", {"start": v(-33.04, -55.13) * mm, "end": v(-32.84, -55) * mm});
            skLineSegment(sketch, "E2020", {"start": v(-32.84, -55) * mm, "end": v(-32.63, -54.87) * mm});
            skLineSegment(sketch, "E2021", {"start": v(-32.63, -54.87) * mm, "end": v(-32.43, -54.73) * mm});
            skLineSegment(sketch, "E2022", {"start": v(-32.43, -54.73) * mm, "end": v(-32.24, -54.6) * mm});
            skLineSegment(sketch, "E2023", {"start": v(-32.24, -54.6) * mm, "end": v(-32.05, -54.47) * mm});
            skLineSegment(sketch, "E2024", {"start": v(-32.05, -54.47) * mm, "end": v(-31.87, -54.34) * mm});
            skLineSegment(sketch, "E2025", {"start": v(-31.87, -54.34) * mm, "end": v(-31.69, -54.2) * mm});
            skLineSegment(sketch, "E2026", {"start": v(-31.69, -54.2) * mm, "end": v(-31.51, -54.08) * mm});
            skLineSegment(sketch, "E2027", {"start": v(-31.51, -54.08) * mm, "end": v(-31.34, -53.95) * mm});
            skLineSegment(sketch, "E2028", {"start": v(-31.34, -53.95) * mm, "end": v(-31.18, -53.83) * mm});
            skLineSegment(sketch, "E2029", {"start": v(-31.18, -53.83) * mm, "end": v(-31.02, -53.7) * mm});
            skLineSegment(sketch, "E2030", {"start": v(-31.02, -53.7) * mm, "end": v(-30.86, -53.58) * mm});
            skLineSegment(sketch, "E2031", {"start": v(-30.86, -53.58) * mm, "end": v(-30.7, -53.45) * mm});
            skLineSegment(sketch, "E2032", {"start": v(-30.7, -53.45) * mm, "end": v(-30.56, -53.33) * mm});
            skLineSegment(sketch, "E2033", {"start": v(-30.56, -53.33) * mm, "end": v(-30.42, -53.21) * mm});
            skLineSegment(sketch, "E2034", {"start": v(-30.42, -53.21) * mm, "end": v(-30.28, -53.1) * mm});
            skLineSegment(sketch, "E2035", {"start": v(-30.28, -53.1) * mm, "end": v(-30.15, -52.98) * mm});
            skLineSegment(sketch, "E2036", {"start": v(-30.15, -52.98) * mm, "end": v(-30.02, -52.87) * mm});
            skLineSegment(sketch, "E2037", {"start": v(-30.02, -52.87) * mm, "end": v(-29.9, -52.75) * mm});
            skLineSegment(sketch, "E2038", {"start": v(-29.9, -52.75) * mm, "end": v(-29.77, -52.64) * mm});
            skLineSegment(sketch, "E2039", {"start": v(-29.77, -52.64) * mm, "end": v(-29.65, -52.53) * mm});
            skArc(sketch, "E2040", {"start": v(-29.65, -52.53) * mm, "mid": v(-29.06, -52.86) * mm, "end": v(-28.47, -53.19) * mm});
            skLineSegment(sketch, "E2041", {"start": v(-28.47, -53.19) * mm, "end": v(-28.5, -53.34) * mm});
            skLineSegment(sketch, "E2042", {"start": v(-28.5, -53.34) * mm, "end": v(-28.52, -53.5) * mm});
            skLineSegment(sketch, "E2043", {"start": v(-28.52, -53.5) * mm, "end": v(-28.55, -53.67) * mm});
            skLineSegment(sketch, "E2044", {"start": v(-28.55, -53.67) * mm, "end": v(-28.58, -53.84) * mm});
            skLineSegment(sketch, "E2045", {"start": v(-28.58, -53.84) * mm, "end": v(-28.6, -54.02) * mm});
            skLineSegment(sketch, "E2046", {"start": v(-28.6, -54.02) * mm, "end": v(-28.63, -54.2) * mm});
            skLineSegment(sketch, "E2047", {"start": v(-28.63, -54.2) * mm, "end": v(-28.66, -54.38) * mm});
            skLineSegment(sketch, "E2048", {"start": v(-28.66, -54.38) * mm, "end": v(-28.68, -54.57) * mm});
            skLineSegment(sketch, "E2049", {"start": v(-28.68, -54.57) * mm, "end": v(-28.7, -54.76) * mm});
            skLineSegment(sketch, "E2050", {"start": v(-28.7, -54.76) * mm, "end": v(-28.72, -54.96) * mm});
            skLineSegment(sketch, "E2051", {"start": v(-28.72, -54.96) * mm, "end": v(-28.74, -55.17) * mm});
            skLineSegment(sketch, "E2052", {"start": v(-28.74, -55.17) * mm, "end": v(-28.76, -55.37) * mm});
            skLineSegment(sketch, "E2053", {"start": v(-28.76, -55.37) * mm, "end": v(-28.77, -55.58) * mm});
            skLineSegment(sketch, "E2054", {"start": v(-28.77, -55.58) * mm, "end": v(-28.79, -55.8) * mm});
            skLineSegment(sketch, "E2055", {"start": v(-28.79, -55.8) * mm, "end": v(-28.8, -56.02) * mm});
            skLineSegment(sketch, "E2056", {"start": v(-28.8, -56.02) * mm, "end": v(-28.82, -56.25) * mm});
            skLineSegment(sketch, "E2057", {"start": v(-28.82, -56.25) * mm, "end": v(-28.82, -56.48) * mm});
            skLineSegment(sketch, "E2058", {"start": v(-28.82, -56.48) * mm, "end": v(-28.83, -56.71) * mm});
            skLineSegment(sketch, "E2059", {"start": v(-28.83, -56.71) * mm, "end": v(-28.84, -56.95) * mm});
            skLineSegment(sketch, "E2060", {"start": v(-28.84, -56.95) * mm, "end": v(-28.84, -57.2) * mm});
            skLineSegment(sketch, "E2061", {"start": v(-28.84, -57.2) * mm, "end": v(-28.85, -57.44) * mm});
            skLineSegment(sketch, "E2062", {"start": v(-28.85, -57.44) * mm, "end": v(-28.85, -57.7) * mm});
            skLineSegment(sketch, "E2063", {"start": v(-28.85, -57.7) * mm, "end": v(-28.84, -57.95) * mm});
            skLineSegment(sketch, "E2064", {"start": v(-28.84, -57.95) * mm, "end": v(-28.84, -58.21) * mm});
            skLineSegment(sketch, "E2065", {"start": v(-28.84, -58.21) * mm, "end": v(-28.83, -58.48) * mm});
            skLineSegment(sketch, "E2066", {"start": v(-28.83, -58.48) * mm, "end": v(-28.82, -58.74) * mm});
            skLineSegment(sketch, "E2067", {"start": v(-28.82, -58.74) * mm, "end": v(-28.8, -59.02) * mm});
            skLineSegment(sketch, "E2068", {"start": v(-28.8, -59.02) * mm, "end": v(-28.8, -59.3) * mm});
            skLineSegment(sketch, "E2069", {"start": v(-28.8, -59.3) * mm, "end": v(-28.79, -59.44) * mm});
            skLineSegment(sketch, "E2070", {"start": v(-28.79, -59.44) * mm, "end": v(-27.45, -60.07) * mm});
            skLineSegment(sketch, "E2071", {"start": v(-27.45, -60.07) * mm, "end": v(-27.33, -59.98) * mm});
            skLineSegment(sketch, "E2072", {"start": v(-27.33, -59.98) * mm, "end": v(-27.11, -59.82) * mm});
            skLineSegment(sketch, "E2073", {"start": v(-27.11, -59.82) * mm, "end": v(-26.9, -59.65) * mm});
            skLineSegment(sketch, "E2074", {"start": v(-26.9, -59.65) * mm, "end": v(-26.68, -59.49) * mm});
            skLineSegment(sketch, "E2075", {"start": v(-26.68, -59.49) * mm, "end": v(-26.47, -59.32) * mm});
            skLineSegment(sketch, "E2076", {"start": v(-26.47, -59.32) * mm, "end": v(-26.27, -59.16) * mm});
            skLineSegment(sketch, "E2077", {"start": v(-26.27, -59.16) * mm, "end": v(-26.07, -59) * mm});
            skLineSegment(sketch, "E2078", {"start": v(-26.07, -59) * mm, "end": v(-25.87, -58.84) * mm});
            skLineSegment(sketch, "E2079", {"start": v(-25.87, -58.84) * mm, "end": v(-25.68, -58.68) * mm});
            skLineSegment(sketch, "E2080", {"start": v(-25.68, -58.68) * mm, "end": v(-25.5, -58.52) * mm});
            skLineSegment(sketch, "E2081", {"start": v(-25.5, -58.52) * mm, "end": v(-25.32, -58.37) * mm});
            skLineSegment(sketch, "E2082", {"start": v(-25.32, -58.37) * mm, "end": v(-25.14, -58.2) * mm});
            skLineSegment(sketch, "E2083", {"start": v(-25.14, -58.2) * mm, "end": v(-24.97, -58.06) * mm});
            skLineSegment(sketch, "E2084", {"start": v(-24.97, -58.06) * mm, "end": v(-24.8, -57.9) * mm});
            skLineSegment(sketch, "E2085", {"start": v(-24.8, -57.9) * mm, "end": v(-24.64, -57.75) * mm});
            skLineSegment(sketch, "E2086", {"start": v(-24.64, -57.75) * mm, "end": v(-24.49, -57.6) * mm});
            skLineSegment(sketch, "E2087", {"start": v(-24.49, -57.6) * mm, "end": v(-24.33, -57.45) * mm});
            skLineSegment(sketch, "E2088", {"start": v(-24.33, -57.45) * mm, "end": v(-24.19, -57.3) * mm});
            skLineSegment(sketch, "E2089", {"start": v(-24.19, -57.3) * mm, "end": v(-24.04, -57.16) * mm});
            skLineSegment(sketch, "E2090", {"start": v(-24.04, -57.16) * mm, "end": v(-23.9, -57.02) * mm});
            skLineSegment(sketch, "E2091", {"start": v(-23.9, -57.02) * mm, "end": v(-23.77, -56.88) * mm});
            skLineSegment(sketch, "E2092", {"start": v(-23.77, -56.88) * mm, "end": v(-23.64, -56.74) * mm});
            skLineSegment(sketch, "E2093", {"start": v(-23.64, -56.74) * mm, "end": v(-23.5, -56.6) * mm});
            skLineSegment(sketch, "E2094", {"start": v(-23.5, -56.6) * mm, "end": v(-23.39, -56.47) * mm});
            skLineSegment(sketch, "E2095", {"start": v(-23.39, -56.47) * mm, "end": v(-23.27, -56.34) * mm});
            skLineSegment(sketch, "E2096", {"start": v(-23.27, -56.34) * mm, "end": v(-23.15, -56.21) * mm});
            skLineSegment(sketch, "E2097", {"start": v(-23.15, -56.21) * mm, "end": v(-23.04, -56.08) * mm});
            skLineSegment(sketch, "E2098", {"start": v(-23.04, -56.08) * mm, "end": v(-22.94, -55.96) * mm});
            skLineSegment(sketch, "E2099", {"start": v(-22.94, -55.96) * mm, "end": v(-22.83, -55.84) * mm});
            skArc(sketch, "E2100", {"start": v(-22.83, -55.84) * mm, "mid": v(-22.2, -56.09) * mm, "end": v(-21.58, -56.33) * mm});
            skLineSegment(sketch, "E2101", {"start": v(-21.58, -56.33) * mm, "end": v(-21.59, -56.5) * mm});
            skLineSegment(sketch, "E2102", {"start": v(-21.59, -56.5) * mm, "end": v(-21.6, -56.66) * mm});
            skLineSegment(sketch, "E2103", {"start": v(-21.6, -56.66) * mm, "end": v(-21.6, -56.83) * mm});
            skLineSegment(sketch, "E2104", {"start": v(-21.6, -56.83) * mm, "end": v(-21.6, -57) * mm});
            skLineSegment(sketch, "E2105", {"start": v(-21.6, -57) * mm, "end": v(-21.61, -57.18) * mm});
            skLineSegment(sketch, "E2106", {"start": v(-21.61, -57.18) * mm, "end": v(-21.61, -57.36) * mm});
            skLineSegment(sketch, "E2107", {"start": v(-21.61, -57.36) * mm, "end": v(-21.61, -57.54) * mm});
            skLineSegment(sketch, "E2108", {"start": v(-21.61, -57.54) * mm, "end": v(-21.61, -57.73) * mm});
            skLineSegment(sketch, "E2109", {"start": v(-21.61, -57.73) * mm, "end": v(-21.61, -57.93) * mm});
            skLineSegment(sketch, "E2110", {"start": v(-21.61, -57.93) * mm, "end": v(-21.6, -58.13) * mm});
            skLineSegment(sketch, "E2111", {"start": v(-21.6, -58.13) * mm, "end": v(-21.6, -58.33) * mm});
            skLineSegment(sketch, "E2112", {"start": v(-21.6, -58.33) * mm, "end": v(-21.6, -58.54) * mm});
            skLineSegment(sketch, "E2113", {"start": v(-21.6, -58.54) * mm, "end": v(-21.58, -58.75) * mm});
            skLineSegment(sketch, "E2114", {"start": v(-21.58, -58.75) * mm, "end": v(-21.57, -58.97) * mm});
            skLineSegment(sketch, "E2115", {"start": v(-21.57, -58.97) * mm, "end": v(-21.55, -59.2) * mm});
            skLineSegment(sketch, "E2116", {"start": v(-21.55, -59.2) * mm, "end": v(-21.54, -59.42) * mm});
            skLineSegment(sketch, "E2117", {"start": v(-21.54, -59.42) * mm, "end": v(-21.52, -59.64) * mm});
            skLineSegment(sketch, "E2118", {"start": v(-21.52, -59.64) * mm, "end": v(-21.5, -59.88) * mm});
            skLineSegment(sketch, "E2119", {"start": v(-21.5, -59.88) * mm, "end": v(-21.47, -60.12) * mm});
            skLineSegment(sketch, "E2120", {"start": v(-21.47, -60.12) * mm, "end": v(-21.45, -60.36) * mm});
            skLineSegment(sketch, "E2121", {"start": v(-21.45, -60.36) * mm, "end": v(-21.42, -60.6) * mm});
            skLineSegment(sketch, "E2122", {"start": v(-21.42, -60.6) * mm, "end": v(-21.39, -60.85) * mm});
            skLineSegment(sketch, "E2123", {"start": v(-21.39, -60.85) * mm, "end": v(-21.35, -61.1) * mm});
            skLineSegment(sketch, "E2124", {"start": v(-21.35, -61.1) * mm, "end": v(-21.31, -61.37) * mm});
            skLineSegment(sketch, "E2125", {"start": v(-21.31, -61.37) * mm, "end": v(-21.27, -61.63) * mm});
            skLineSegment(sketch, "E2126", {"start": v(-21.27, -61.63) * mm, "end": v(-21.23, -61.9) * mm});
            skLineSegment(sketch, "E2127", {"start": v(-21.23, -61.9) * mm, "end": v(-21.19, -62.16) * mm});
            skLineSegment(sketch, "E2128", {"start": v(-21.19, -62.16) * mm, "end": v(-21.14, -62.44) * mm});
            skLineSegment(sketch, "E2129", {"start": v(-21.14, -62.44) * mm, "end": v(-21.1, -62.58) * mm});
            skLineSegment(sketch, "E2130", {"start": v(-21.1, -62.58) * mm, "end": v(-19.7, -63.03) * mm});
            skLineSegment(sketch, "E2131", {"start": v(-19.7, -63.03) * mm, "end": v(-19.6, -62.94) * mm});
            skLineSegment(sketch, "E2132", {"start": v(-19.6, -62.94) * mm, "end": v(-19.4, -62.74) * mm});
            skLineSegment(sketch, "E2133", {"start": v(-19.4, -62.74) * mm, "end": v(-19.2, -62.55) * mm});
            skLineSegment(sketch, "E2134", {"start": v(-19.2, -62.55) * mm, "end": v(-19.01, -62.36) * mm});
            skLineSegment(sketch, "E2135", {"start": v(-19.01, -62.36) * mm, "end": v(-18.83, -62.17) * mm});
            skLineSegment(sketch, "E2136", {"start": v(-18.83, -62.17) * mm, "end": v(-18.64, -61.99) * mm});
            skLineSegment(sketch, "E2137", {"start": v(-18.64, -61.99) * mm, "end": v(-18.47, -61.8) * mm});
            skLineSegment(sketch, "E2138", {"start": v(-18.47, -61.8) * mm, "end": v(-18.3, -61.62) * mm});
            skLineSegment(sketch, "E2139", {"start": v(-18.3, -61.62) * mm, "end": v(-18.13, -61.44) * mm});
            skLineSegment(sketch, "E2140", {"start": v(-18.13, -61.44) * mm, "end": v(-17.96, -61.26) * mm});
            skLineSegment(sketch, "E2141", {"start": v(-17.96, -61.26) * mm, "end": v(-17.8, -61.08) * mm});
            skLineSegment(sketch, "E2142", {"start": v(-17.8, -61.08) * mm, "end": v(-17.65, -60.9) * mm});
            skLineSegment(sketch, "E2143", {"start": v(-17.65, -60.9) * mm, "end": v(-17.5, -60.73) * mm});
            skLineSegment(sketch, "E2144", {"start": v(-17.5, -60.73) * mm, "end": v(-17.35, -60.56) * mm});
            skLineSegment(sketch, "E2145", {"start": v(-17.35, -60.56) * mm, "end": v(-17.21, -60.39) * mm});
            skLineSegment(sketch, "E2146", {"start": v(-17.21, -60.39) * mm, "end": v(-17.07, -60.22) * mm});
            skLineSegment(sketch, "E2147", {"start": v(-17.07, -60.22) * mm, "end": v(-16.94, -60.05) * mm});
            skLineSegment(sketch, "E2148", {"start": v(-16.94, -60.05) * mm, "end": v(-16.81, -59.89) * mm});
            skLineSegment(sketch, "E2149", {"start": v(-16.81, -59.89) * mm, "end": v(-16.69, -59.73) * mm});
            skLineSegment(sketch, "E2150", {"start": v(-16.69, -59.73) * mm, "end": v(-16.57, -59.57) * mm});
            skLineSegment(sketch, "E2151", {"start": v(-16.57, -59.57) * mm, "end": v(-16.45, -59.41) * mm});
            skLineSegment(sketch, "E2152", {"start": v(-16.45, -59.41) * mm, "end": v(-16.34, -59.26) * mm});
            skLineSegment(sketch, "E2153", {"start": v(-16.34, -59.26) * mm, "end": v(-16.23, -59.1) * mm});
            skLineSegment(sketch, "E2154", {"start": v(-16.23, -59.1) * mm, "end": v(-16.12, -58.96) * mm});
            skLineSegment(sketch, "E2155", {"start": v(-16.12, -58.96) * mm, "end": v(-16.02, -58.81) * mm});
            skLineSegment(sketch, "E2156", {"start": v(-16.02, -58.81) * mm, "end": v(-15.93, -58.67) * mm});
            skLineSegment(sketch, "E2157", {"start": v(-15.93, -58.67) * mm, "end": v(-15.83, -58.53) * mm});
            skLineSegment(sketch, "E2158", {"start": v(-15.83, -58.53) * mm, "end": v(-15.74, -58.4) * mm});
            skLineSegment(sketch, "E2159", {"start": v(-15.74, -58.4) * mm, "end": v(-15.66, -58.26) * mm});
            skArc(sketch, "E2160", {"start": v(-15.66, -58.26) * mm, "mid": v(-15, -58.43) * mm, "end": v(-14.35, -58.6) * mm});
            skLineSegment(sketch, "E2161", {"start": v(-14.35, -58.6) * mm, "end": v(-14.34, -58.75) * mm});
            skLineSegment(sketch, "E2162", {"start": v(-14.34, -58.75) * mm, "end": v(-14.32, -58.92) * mm});
            skLineSegment(sketch, "E2163", {"start": v(-14.32, -58.92) * mm, "end": v(-14.3, -59.08) * mm});
            skLineSegment(sketch, "E2164", {"start": v(-14.3, -59.08) * mm, "end": v(-14.3, -59.26) * mm});
            skLineSegment(sketch, "E2165", {"start": v(-14.3, -59.26) * mm, "end": v(-14.27, -59.43) * mm});
            skLineSegment(sketch, "E2166", {"start": v(-14.27, -59.43) * mm, "end": v(-14.25, -59.61) * mm});
            skLineSegment(sketch, "E2167", {"start": v(-14.25, -59.61) * mm, "end": v(-14.23, -59.8) * mm});
            skLineSegment(sketch, "E2168", {"start": v(-14.23, -59.8) * mm, "end": v(-14.2, -59.99) * mm});
            skLineSegment(sketch, "E2169", {"start": v(-14.2, -59.99) * mm, "end": v(-14.18, -60.18) * mm});
            skLineSegment(sketch, "E2170", {"start": v(-14.18, -60.18) * mm, "end": v(-14.15, -60.38) * mm});
            skLineSegment(sketch, "E2171", {"start": v(-14.15, -60.38) * mm, "end": v(-14.12, -60.58) * mm});
            skLineSegment(sketch, "E2172", {"start": v(-14.12, -60.58) * mm, "end": v(-14.08, -60.79) * mm});
            skLineSegment(sketch, "E2173", {"start": v(-14.08, -60.79) * mm, "end": v(-14.05, -61) * mm});
            skLineSegment(sketch, "E2174", {"start": v(-14.05, -61) * mm, "end": v(-14, -61.2) * mm});
            skLineSegment(sketch, "E2175", {"start": v(-14, -61.2) * mm, "end": v(-13.97, -61.43) * mm});
            skLineSegment(sketch, "E2176", {"start": v(-13.97, -61.43) * mm, "end": v(-13.92, -61.65) * mm});
            skLineSegment(sketch, "E2177", {"start": v(-13.92, -61.65) * mm, "end": v(-13.87, -61.87) * mm});
            skLineSegment(sketch, "E2178", {"start": v(-13.87, -61.87) * mm, "end": v(-13.82, -62.1) * mm});
            skLineSegment(sketch, "E2179", {"start": v(-13.82, -62.1) * mm, "end": v(-13.77, -62.33) * mm});
            skLineSegment(sketch, "E2180", {"start": v(-13.77, -62.33) * mm, "end": v(-13.71, -62.57) * mm});
            skLineSegment(sketch, "E2181", {"start": v(-13.71, -62.57) * mm, "end": v(-13.65, -62.81) * mm});
            skLineSegment(sketch, "E2182", {"start": v(-13.65, -62.81) * mm, "end": v(-13.6, -63.05) * mm});
            skLineSegment(sketch, "E2183", {"start": v(-13.6, -63.05) * mm, "end": v(-13.53, -63.3) * mm});
            skLineSegment(sketch, "E2184", {"start": v(-13.53, -63.3) * mm, "end": v(-13.46, -63.55) * mm});
            skLineSegment(sketch, "E2185", {"start": v(-13.46, -63.55) * mm, "end": v(-13.38, -63.8) * mm});
            skLineSegment(sketch, "E2186", {"start": v(-13.38, -63.8) * mm, "end": v(-13.3, -64.07) * mm});
            skLineSegment(sketch, "E2187", {"start": v(-13.3, -64.07) * mm, "end": v(-13.23, -64.33) * mm});
            skLineSegment(sketch, "E2188", {"start": v(-13.23, -64.33) * mm, "end": v(-13.14, -64.6) * mm});
            skLineSegment(sketch, "E2189", {"start": v(-13.14, -64.6) * mm, "end": v(-13.1, -64.73) * mm});
            skLineSegment(sketch, "E2190", {"start": v(-13.1, -64.73) * mm, "end": v(-11.65, -65) * mm});
            skLineSegment(sketch, "E2191", {"start": v(-11.65, -65) * mm, "end": v(-11.56, -64.9) * mm});
            skLineSegment(sketch, "E2192", {"start": v(-11.56, -64.9) * mm, "end": v(-11.38, -64.68) * mm});
            skLineSegment(sketch, "E2193", {"start": v(-11.38, -64.68) * mm, "end": v(-11.21, -64.47) * mm});
            skLineSegment(sketch, "E2194", {"start": v(-11.21, -64.47) * mm, "end": v(-11.05, -64.25) * mm});
            skLineSegment(sketch, "E2195", {"start": v(-11.05, -64.25) * mm, "end": v(-10.88, -64.04) * mm});
            skLineSegment(sketch, "E2196", {"start": v(-10.88, -64.04) * mm, "end": v(-10.73, -63.84) * mm});
            skLineSegment(sketch, "E2197", {"start": v(-10.73, -63.84) * mm, "end": v(-10.58, -63.63) * mm});
            skLineSegment(sketch, "E2198", {"start": v(-10.58, -63.63) * mm, "end": v(-10.43, -63.43) * mm});
            skLineSegment(sketch, "E2199", {"start": v(-10.43, -63.43) * mm, "end": v(-10.28, -63.22) * mm});
            skLineSegment(sketch, "E2200", {"start": v(-10.28, -63.22) * mm, "end": v(-10.14, -63.03) * mm});
            skLineSegment(sketch, "E2201", {"start": v(-10.14, -63.03) * mm, "end": v(-10, -62.83) * mm});
            skLineSegment(sketch, "E2202", {"start": v(-10, -62.83) * mm, "end": v(-9.88, -62.63) * mm});
            skLineSegment(sketch, "E2203", {"start": v(-9.88, -62.63) * mm, "end": v(-9.75, -62.44) * mm});
            skLineSegment(sketch, "E2204", {"start": v(-9.75, -62.44) * mm, "end": v(-9.63, -62.25) * mm});
            skLineSegment(sketch, "E2205", {"start": v(-9.63, -62.25) * mm, "end": v(-9.5, -62.07) * mm});
            skLineSegment(sketch, "E2206", {"start": v(-9.5, -62.07) * mm, "end": v(-9.4, -61.88) * mm});
            skLineSegment(sketch, "E2207", {"start": v(-9.4, -61.88) * mm, "end": v(-9.28, -61.7) * mm});
            skLineSegment(sketch, "E2208", {"start": v(-9.28, -61.7) * mm, "end": v(-9.17, -61.52) * mm});
            skLineSegment(sketch, "E2209", {"start": v(-9.17, -61.52) * mm, "end": v(-9.07, -61.35) * mm});
            skLineSegment(sketch, "E2210", {"start": v(-9.07, -61.35) * mm, "end": v(-8.97, -61.17) * mm});
            skLineSegment(sketch, "E2211", {"start": v(-8.97, -61.17) * mm, "end": v(-8.87, -61) * mm});
            skLineSegment(sketch, "E2212", {"start": v(-8.87, -61) * mm, "end": v(-8.78, -60.84) * mm});
            skLineSegment(sketch, "E2213", {"start": v(-8.78, -60.84) * mm, "end": v(-8.7, -60.67) * mm});
            skLineSegment(sketch, "E2214", {"start": v(-8.7, -60.67) * mm, "end": v(-8.6, -60.51) * mm});
            skLineSegment(sketch, "E2215", {"start": v(-8.6, -60.51) * mm, "end": v(-8.53, -60.36) * mm});
            skLineSegment(sketch, "E2216", {"start": v(-8.53, -60.36) * mm, "end": v(-8.45, -60.2) * mm});
            skLineSegment(sketch, "E2217", {"start": v(-8.45, -60.2) * mm, "end": v(-8.37, -60.05) * mm});
            skLineSegment(sketch, "E2218", {"start": v(-8.37, -60.05) * mm, "end": v(-8.3, -59.9) * mm});
            skLineSegment(sketch, "E2219", {"start": v(-8.3, -59.9) * mm, "end": v(-8.23, -59.76) * mm});
            skArc(sketch, "E2220", {"start": v(-8.23, -59.76) * mm, "mid": v(-7.56, -59.85) * mm, "end": v(-6.89, -59.93) * mm});
            skLineSegment(sketch, "E2221", {"start": v(-6.89, -59.93) * mm, "end": v(-6.86, -60.09) * mm});
            skLineSegment(sketch, "E2222", {"start": v(-6.86, -60.09) * mm, "end": v(-6.83, -60.25) * mm});
            skLineSegment(sketch, "E2223", {"start": v(-6.83, -60.25) * mm, "end": v(-6.8, -60.41) * mm});
            skLineSegment(sketch, "E2224", {"start": v(-6.8, -60.41) * mm, "end": v(-6.75, -60.58) * mm});
            skLineSegment(sketch, "E2225", {"start": v(-6.75, -60.58) * mm, "end": v(-6.71, -60.75) * mm});
            skLineSegment(sketch, "E2226", {"start": v(-6.71, -60.75) * mm, "end": v(-6.67, -60.93) * mm});
            skLineSegment(sketch, "E2227", {"start": v(-6.67, -60.93) * mm, "end": v(-6.62, -61.11) * mm});
            skLineSegment(sketch, "E2228", {"start": v(-6.62, -61.11) * mm, "end": v(-6.58, -61.3) * mm});
            skLineSegment(sketch, "E2229", {"start": v(-6.58, -61.3) * mm, "end": v(-6.52, -61.48) * mm});
            skLineSegment(sketch, "E2230", {"start": v(-6.52, -61.48) * mm, "end": v(-6.47, -61.68) * mm});
            skLineSegment(sketch, "E2231", {"start": v(-6.47, -61.68) * mm, "end": v(-6.41, -61.87) * mm});
            skLineSegment(sketch, "E2232", {"start": v(-6.41, -61.87) * mm, "end": v(-6.35, -62.07) * mm});
            skLineSegment(sketch, "E2233", {"start": v(-6.35, -62.07) * mm, "end": v(-6.3, -62.27) * mm});
            skLineSegment(sketch, "E2234", {"start": v(-6.3, -62.27) * mm, "end": v(-6.23, -62.48) * mm});
            skLineSegment(sketch, "E2235", {"start": v(-6.23, -62.48) * mm, "end": v(-6.16, -62.7) * mm});
            skLineSegment(sketch, "E2236", {"start": v(-6.16, -62.7) * mm, "end": v(-6.09, -62.9) * mm});
            skLineSegment(sketch, "E2237", {"start": v(-6.09, -62.9) * mm, "end": v(-6.01, -63.12) * mm});
            skLineSegment(sketch, "E2238", {"start": v(-6.01, -63.12) * mm, "end": v(-5.93, -63.34) * mm});
            skLineSegment(sketch, "E2239", {"start": v(-5.93, -63.34) * mm, "end": v(-5.85, -63.57) * mm});
            skLineSegment(sketch, "E2240", {"start": v(-5.85, -63.57) * mm, "end": v(-5.76, -63.8) * mm});
            skLineSegment(sketch, "E2241", {"start": v(-5.76, -63.8) * mm, "end": v(-5.67, -64.03) * mm});
            skLineSegment(sketch, "E2242", {"start": v(-5.67, -64.03) * mm, "end": v(-5.58, -64.26) * mm});
            skLineSegment(sketch, "E2243", {"start": v(-5.58, -64.26) * mm, "end": v(-5.48, -64.5) * mm});
            skLineSegment(sketch, "E2244", {"start": v(-5.48, -64.5) * mm, "end": v(-5.38, -64.74) * mm});
            skLineSegment(sketch, "E2245", {"start": v(-5.38, -64.74) * mm, "end": v(-5.28, -64.98) * mm});
            skLineSegment(sketch, "E2246", {"start": v(-5.28, -64.98) * mm, "end": v(-5.17, -65.23) * mm});
            skLineSegment(sketch, "E2247", {"start": v(-5.17, -65.23) * mm, "end": v(-5.06, -65.48) * mm});
            skLineSegment(sketch, "E2248", {"start": v(-5.06, -65.48) * mm, "end": v(-4.94, -65.73) * mm});
            skLineSegment(sketch, "E2249", {"start": v(-4.94, -65.73) * mm, "end": v(-4.88, -65.86) * mm});
            skLineSegment(sketch, "E2250", {"start": v(-4.88, -65.86) * mm, "end": v(-3.4, -65.95) * mm});
            skLineSegment(sketch, "E2251", {"start": v(-3.4, -65.95) * mm, "end": v(-3.33, -65.83) * mm});
            skLineSegment(sketch, "E2252", {"start": v(-3.33, -65.83) * mm, "end": v(-3.19, -65.6) * mm});
            skLineSegment(sketch, "E2253", {"start": v(-3.19, -65.6) * mm, "end": v(-3.04, -65.36) * mm});
            skLineSegment(sketch, "E2254", {"start": v(-3.04, -65.36) * mm, "end": v(-2.9, -65.13) * mm});
            skLineSegment(sketch, "E2255", {"start": v(-2.9, -65.13) * mm, "end": v(-2.77, -64.9) * mm});
            skLineSegment(sketch, "E2256", {"start": v(-2.77, -64.9) * mm, "end": v(-2.64, -64.68) * mm});
            skLineSegment(sketch, "E2257", {"start": v(-2.64, -64.68) * mm, "end": v(-2.52, -64.45) * mm});
            skLineSegment(sketch, "E2258", {"start": v(-2.52, -64.45) * mm, "end": v(-2.4, -64.23) * mm});
            skLineSegment(sketch, "E2259", {"start": v(-2.4, -64.23) * mm, "end": v(-2.28, -64.01) * mm});
            skLineSegment(sketch, "E2260", {"start": v(-2.28, -64.01) * mm, "end": v(-2.16, -63.8) * mm});
            skLineSegment(sketch, "E2261", {"start": v(-2.16, -63.8) * mm, "end": v(-2.05, -63.59) * mm});
            skLineSegment(sketch, "E2262", {"start": v(-2.05, -63.59) * mm, "end": v(-1.95, -63.38) * mm});
            skLineSegment(sketch, "E2263", {"start": v(-1.95, -63.38) * mm, "end": v(-1.85, -63.17) * mm});
            skLineSegment(sketch, "E2264", {"start": v(-1.85, -63.17) * mm, "end": v(-1.75, -62.97) * mm});
            skLineSegment(sketch, "E2265", {"start": v(-1.75, -62.97) * mm, "end": v(-1.65, -62.77) * mm});
            skLineSegment(sketch, "E2266", {"start": v(-1.65, -62.77) * mm, "end": v(-1.56, -62.57) * mm});
            skLineSegment(sketch, "E2267", {"start": v(-1.56, -62.57) * mm, "end": v(-1.47, -62.38) * mm});
            skLineSegment(sketch, "E2268", {"start": v(-1.47, -62.38) * mm, "end": v(-1.4, -62.19) * mm});
            skLineSegment(sketch, "E2269", {"start": v(-1.4, -62.19) * mm, "end": v(-1.31, -62) * mm});
            skLineSegment(sketch, "E2270", {"start": v(-1.31, -62) * mm, "end": v(-1.23, -61.82) * mm});
            skLineSegment(sketch, "E2271", {"start": v(-1.23, -61.82) * mm, "end": v(-1.16, -61.64) * mm});
            skLineSegment(sketch, "E2272", {"start": v(-1.16, -61.64) * mm, "end": v(-1.09, -61.46) * mm});
            skLineSegment(sketch, "E2273", {"start": v(-1.09, -61.46) * mm, "end": v(-1.02, -61.29) * mm});
            skLineSegment(sketch, "E2274", {"start": v(-1.02, -61.29) * mm, "end": v(-0.96, -61.12) * mm});
            skLineSegment(sketch, "E2275", {"start": v(-0.96, -61.12) * mm, "end": v(-0.9, -60.95) * mm});
            skLineSegment(sketch, "E2276", {"start": v(-0.9, -60.95) * mm, "end": v(-0.83, -60.79) * mm});
            skLineSegment(sketch, "E2277", {"start": v(-0.83, -60.79) * mm, "end": v(-0.78, -60.63) * mm});
            skLineSegment(sketch, "E2278", {"start": v(-0.78, -60.63) * mm, "end": v(-0.73, -60.47) * mm});
            skLineSegment(sketch, "E2279", {"start": v(-0.73, -60.47) * mm, "end": v(-0.68, -60.32) * mm});
            skArc(sketch, "E2280", {"start": v(-0.68, -60.32) * mm, "mid": v(0, -60.32) * mm, "end": v(0.68, -60.32) * mm});
            skLineSegment(sketch, "E2281", {"start": v(0.68, -60.32) * mm, "end": v(0.73, -60.47) * mm});
            skLineSegment(sketch, "E2282", {"start": v(0.73, -60.47) * mm, "end": v(0.78, -60.63) * mm});
            skLineSegment(sketch, "E2283", {"start": v(0.78, -60.63) * mm, "end": v(0.83, -60.79) * mm});
            skLineSegment(sketch, "E2284", {"start": v(0.83, -60.79) * mm, "end": v(0.9, -60.95) * mm});
            skLineSegment(sketch, "E2285", {"start": v(0.9, -60.95) * mm, "end": v(0.96, -61.12) * mm});
            skLineSegment(sketch, "E2286", {"start": v(0.96, -61.12) * mm, "end": v(1.02, -61.29) * mm});
            skLineSegment(sketch, "E2287", {"start": v(1.02, -61.29) * mm, "end": v(1.09, -61.46) * mm});
            skLineSegment(sketch, "E2288", {"start": v(1.09, -61.46) * mm, "end": v(1.16, -61.64) * mm});
            skLineSegment(sketch, "E2289", {"start": v(1.16, -61.64) * mm, "end": v(1.23, -61.82) * mm});
            skLineSegment(sketch, "E2290", {"start": v(1.23, -61.82) * mm, "end": v(1.31, -62) * mm});
            skLineSegment(sketch, "E2291", {"start": v(1.31, -62) * mm, "end": v(1.4, -62.19) * mm});
            skLineSegment(sketch, "E2292", {"start": v(1.4, -62.19) * mm, "end": v(1.47, -62.38) * mm});
            skLineSegment(sketch, "E2293", {"start": v(1.47, -62.38) * mm, "end": v(1.56, -62.57) * mm});
            skLineSegment(sketch, "E2294", {"start": v(1.56, -62.57) * mm, "end": v(1.65, -62.77) * mm});
            skLineSegment(sketch, "E2295", {"start": v(1.65, -62.77) * mm, "end": v(1.75, -62.97) * mm});
            skLineSegment(sketch, "E2296", {"start": v(1.75, -62.97) * mm, "end": v(1.85, -63.17) * mm});
            skLineSegment(sketch, "E2297", {"start": v(1.85, -63.17) * mm, "end": v(1.95, -63.38) * mm});
            skLineSegment(sketch, "E2298", {"start": v(1.95, -63.38) * mm, "end": v(2.05, -63.59) * mm});
            skLineSegment(sketch, "E2299", {"start": v(2.05, -63.59) * mm, "end": v(2.16, -63.8) * mm});
            skLineSegment(sketch, "E2300", {"start": v(2.16, -63.8) * mm, "end": v(2.28, -64.01) * mm});
            skLineSegment(sketch, "E2301", {"start": v(2.28, -64.01) * mm, "end": v(2.4, -64.23) * mm});
            skLineSegment(sketch, "E2302", {"start": v(2.4, -64.23) * mm, "end": v(2.52, -64.45) * mm});
            skLineSegment(sketch, "E2303", {"start": v(2.52, -64.45) * mm, "end": v(2.64, -64.68) * mm});
            skLineSegment(sketch, "E2304", {"start": v(2.64, -64.68) * mm, "end": v(2.77, -64.9) * mm});
            skLineSegment(sketch, "E2305", {"start": v(2.77, -64.9) * mm, "end": v(2.9, -65.13) * mm});
            skLineSegment(sketch, "E2306", {"start": v(2.9, -65.13) * mm, "end": v(3.04, -65.36) * mm});
            skLineSegment(sketch, "E2307", {"start": v(3.04, -65.36) * mm, "end": v(3.19, -65.6) * mm});
            skLineSegment(sketch, "E2308", {"start": v(3.19, -65.6) * mm, "end": v(3.33, -65.83) * mm});
            skLineSegment(sketch, "E2309", {"start": v(3.33, -65.83) * mm, "end": v(3.4, -65.95) * mm});
            skLineSegment(sketch, "E2310", {"start": v(3.4, -65.95) * mm, "end": v(4.88, -65.86) * mm});
            skLineSegment(sketch, "E2311", {"start": v(4.88, -65.86) * mm, "end": v(4.94, -65.73) * mm});
            skLineSegment(sketch, "E2312", {"start": v(4.94, -65.73) * mm, "end": v(5.06, -65.48) * mm});
            skLineSegment(sketch, "E2313", {"start": v(5.06, -65.48) * mm, "end": v(5.17, -65.23) * mm});
            skLineSegment(sketch, "E2314", {"start": v(5.17, -65.23) * mm, "end": v(5.28, -64.98) * mm});
            skLineSegment(sketch, "E2315", {"start": v(5.28, -64.98) * mm, "end": v(5.38, -64.74) * mm});
            skLineSegment(sketch, "E2316", {"start": v(5.38, -64.74) * mm, "end": v(5.48, -64.5) * mm});
            skLineSegment(sketch, "E2317", {"start": v(5.48, -64.5) * mm, "end": v(5.58, -64.26) * mm});
            skLineSegment(sketch, "E2318", {"start": v(5.58, -64.26) * mm, "end": v(5.67, -64.03) * mm});
            skLineSegment(sketch, "E2319", {"start": v(5.67, -64.03) * mm, "end": v(5.76, -63.8) * mm});
            skLineSegment(sketch, "E2320", {"start": v(5.76, -63.8) * mm, "end": v(5.85, -63.57) * mm});
            skLineSegment(sketch, "E2321", {"start": v(5.85, -63.57) * mm, "end": v(5.93, -63.34) * mm});
            skLineSegment(sketch, "E2322", {"start": v(5.93, -63.34) * mm, "end": v(6, -63.12) * mm});
            skLineSegment(sketch, "E2323", {"start": v(6, -63.12) * mm, "end": v(6.09, -62.9) * mm});
            skLineSegment(sketch, "E2324", {"start": v(6.09, -62.9) * mm, "end": v(6.16, -62.7) * mm});
            skLineSegment(sketch, "E2325", {"start": v(6.16, -62.7) * mm, "end": v(6.23, -62.48) * mm});
            skLineSegment(sketch, "E2326", {"start": v(6.23, -62.48) * mm, "end": v(6.3, -62.27) * mm});
            skLineSegment(sketch, "E2327", {"start": v(6.3, -62.27) * mm, "end": v(6.35, -62.07) * mm});
            skLineSegment(sketch, "E2328", {"start": v(6.35, -62.07) * mm, "end": v(6.41, -61.87) * mm});
            skLineSegment(sketch, "E2329", {"start": v(6.41, -61.87) * mm, "end": v(6.47, -61.68) * mm});
            skLineSegment(sketch, "E2330", {"start": v(6.47, -61.68) * mm, "end": v(6.52, -61.48) * mm});
            skLineSegment(sketch, "E2331", {"start": v(6.52, -61.48) * mm, "end": v(6.58, -61.3) * mm});
            skLineSegment(sketch, "E2332", {"start": v(6.58, -61.3) * mm, "end": v(6.62, -61.11) * mm});
            skLineSegment(sketch, "E2333", {"start": v(6.62, -61.11) * mm, "end": v(6.67, -60.93) * mm});
            skLineSegment(sketch, "E2334", {"start": v(6.67, -60.93) * mm, "end": v(6.71, -60.75) * mm});
            skLineSegment(sketch, "E2335", {"start": v(6.71, -60.75) * mm, "end": v(6.75, -60.58) * mm});
            skLineSegment(sketch, "E2336", {"start": v(6.75, -60.58) * mm, "end": v(6.8, -60.41) * mm});
            skLineSegment(sketch, "E2337", {"start": v(6.8, -60.41) * mm, "end": v(6.83, -60.25) * mm});
            skLineSegment(sketch, "E2338", {"start": v(6.83, -60.25) * mm, "end": v(6.86, -60.09) * mm});
            skLineSegment(sketch, "E2339", {"start": v(6.86, -60.09) * mm, "end": v(6.89, -59.93) * mm});
            skArc(sketch, "E2340", {"start": v(6.89, -59.93) * mm, "mid": v(7.56, -59.85) * mm, "end": v(8.23, -59.76) * mm});
            skLineSegment(sketch, "E2341", {"start": v(8.23, -59.76) * mm, "end": v(8.3, -59.9) * mm});
            skLineSegment(sketch, "E2342", {"start": v(8.3, -59.9) * mm, "end": v(8.37, -60.05) * mm});
            skLineSegment(sketch, "E2343", {"start": v(8.37, -60.05) * mm, "end": v(8.45, -60.2) * mm});
            skLineSegment(sketch, "E2344", {"start": v(8.45, -60.2) * mm, "end": v(8.53, -60.36) * mm});
            skLineSegment(sketch, "E2345", {"start": v(8.53, -60.36) * mm, "end": v(8.6, -60.51) * mm});
            skLineSegment(sketch, "E2346", {"start": v(8.6, -60.51) * mm, "end": v(8.7, -60.67) * mm});
            skLineSegment(sketch, "E2347", {"start": v(8.7, -60.67) * mm, "end": v(8.78, -60.84) * mm});
            skLineSegment(sketch, "E2348", {"start": v(8.78, -60.84) * mm, "end": v(8.87, -61) * mm});
            skLineSegment(sketch, "E2349", {"start": v(8.87, -61) * mm, "end": v(8.97, -61.17) * mm});
            skLineSegment(sketch, "E2350", {"start": v(8.97, -61.17) * mm, "end": v(9.07, -61.35) * mm});
            skLineSegment(sketch, "E2351", {"start": v(9.07, -61.35) * mm, "end": v(9.17, -61.52) * mm});
            skLineSegment(sketch, "E2352", {"start": v(9.17, -61.52) * mm, "end": v(9.28, -61.7) * mm});
            skLineSegment(sketch, "E2353", {"start": v(9.28, -61.7) * mm, "end": v(9.4, -61.88) * mm});
            skLineSegment(sketch, "E2354", {"start": v(9.4, -61.88) * mm, "end": v(9.5, -62.07) * mm});
            skLineSegment(sketch, "E2355", {"start": v(9.5, -62.07) * mm, "end": v(9.63, -62.25) * mm});
            skLineSegment(sketch, "E2356", {"start": v(9.63, -62.25) * mm, "end": v(9.75, -62.44) * mm});
            skLineSegment(sketch, "E2357", {"start": v(9.75, -62.44) * mm, "end": v(9.88, -62.63) * mm});
            skLineSegment(sketch, "E2358", {"start": v(9.88, -62.63) * mm, "end": v(10, -62.83) * mm});
            skLineSegment(sketch, "E2359", {"start": v(10, -62.83) * mm, "end": v(10.14, -63.03) * mm});
            skLineSegment(sketch, "E2360", {"start": v(10.14, -63.03) * mm, "end": v(10.28, -63.22) * mm});
            skLineSegment(sketch, "E2361", {"start": v(10.28, -63.22) * mm, "end": v(10.43, -63.43) * mm});
            skLineSegment(sketch, "E2362", {"start": v(10.43, -63.43) * mm, "end": v(10.58, -63.63) * mm});
            skLineSegment(sketch, "E2363", {"start": v(10.58, -63.63) * mm, "end": v(10.73, -63.84) * mm});
            skLineSegment(sketch, "E2364", {"start": v(10.73, -63.84) * mm, "end": v(10.88, -64.04) * mm});
            skLineSegment(sketch, "E2365", {"start": v(10.88, -64.04) * mm, "end": v(11.05, -64.25) * mm});
            skLineSegment(sketch, "E2366", {"start": v(11.05, -64.25) * mm, "end": v(11.21, -64.47) * mm});
            skLineSegment(sketch, "E2367", {"start": v(11.21, -64.47) * mm, "end": v(11.38, -64.68) * mm});
            skLineSegment(sketch, "E2368", {"start": v(11.38, -64.68) * mm, "end": v(11.56, -64.9) * mm});
            skLineSegment(sketch, "E2369", {"start": v(11.56, -64.9) * mm, "end": v(11.65, -65) * mm});
            skLineSegment(sketch, "E2370", {"start": v(11.65, -65) * mm, "end": v(13.1, -64.73) * mm});
            skLineSegment(sketch, "E2371", {"start": v(13.1, -64.73) * mm, "end": v(13.14, -64.6) * mm});
            skLineSegment(sketch, "E2372", {"start": v(13.14, -64.6) * mm, "end": v(13.23, -64.33) * mm});
            skLineSegment(sketch, "E2373", {"start": v(13.23, -64.33) * mm, "end": v(13.3, -64.07) * mm});
            skLineSegment(sketch, "E2374", {"start": v(13.3, -64.07) * mm, "end": v(13.38, -63.8) * mm});
            skLineSegment(sketch, "E2375", {"start": v(13.38, -63.8) * mm, "end": v(13.46, -63.55) * mm});
            skLineSegment(sketch, "E2376", {"start": v(13.46, -63.55) * mm, "end": v(13.52, -63.3) * mm});
            skLineSegment(sketch, "E2377", {"start": v(13.52, -63.3) * mm, "end": v(13.6, -63.05) * mm});
            skLineSegment(sketch, "E2378", {"start": v(13.6, -63.05) * mm, "end": v(13.65, -62.81) * mm});
            skLineSegment(sketch, "E2379", {"start": v(13.65, -62.81) * mm, "end": v(13.71, -62.57) * mm});
            skLineSegment(sketch, "E2380", {"start": v(13.71, -62.57) * mm, "end": v(13.77, -62.33) * mm});
            skLineSegment(sketch, "E2381", {"start": v(13.77, -62.33) * mm, "end": v(13.82, -62.1) * mm});
            skLineSegment(sketch, "E2382", {"start": v(13.82, -62.1) * mm, "end": v(13.87, -61.87) * mm});
            skLineSegment(sketch, "E2383", {"start": v(13.87, -61.87) * mm, "end": v(13.92, -61.65) * mm});
            skLineSegment(sketch, "E2384", {"start": v(13.92, -61.65) * mm, "end": v(13.97, -61.43) * mm});
            skLineSegment(sketch, "E2385", {"start": v(13.97, -61.43) * mm, "end": v(14, -61.2) * mm});
            skLineSegment(sketch, "E2386", {"start": v(14, -61.2) * mm, "end": v(14.05, -61) * mm});
            skLineSegment(sketch, "E2387", {"start": v(14.05, -61) * mm, "end": v(14.08, -60.79) * mm});
            skLineSegment(sketch, "E2388", {"start": v(14.08, -60.79) * mm, "end": v(14.12, -60.58) * mm});
            skLineSegment(sketch, "E2389", {"start": v(14.12, -60.58) * mm, "end": v(14.15, -60.38) * mm});
            skLineSegment(sketch, "E2390", {"start": v(14.15, -60.38) * mm, "end": v(14.18, -60.18) * mm});
            skLineSegment(sketch, "E2391", {"start": v(14.18, -60.18) * mm, "end": v(14.2, -59.99) * mm});
            skLineSegment(sketch, "E2392", {"start": v(14.2, -59.99) * mm, "end": v(14.23, -59.8) * mm});
            skLineSegment(sketch, "E2393", {"start": v(14.23, -59.8) * mm, "end": v(14.25, -59.61) * mm});
            skLineSegment(sketch, "E2394", {"start": v(14.25, -59.61) * mm, "end": v(14.27, -59.43) * mm});
            skLineSegment(sketch, "E2395", {"start": v(14.27, -59.43) * mm, "end": v(14.3, -59.26) * mm});
            skLineSegment(sketch, "E2396", {"start": v(14.3, -59.26) * mm, "end": v(14.3, -59.08) * mm});
            skLineSegment(sketch, "E2397", {"start": v(14.3, -59.08) * mm, "end": v(14.32, -58.92) * mm});
            skLineSegment(sketch, "E2398", {"start": v(14.32, -58.92) * mm, "end": v(14.34, -58.75) * mm});
            skLineSegment(sketch, "E2399", {"start": v(14.34, -58.75) * mm, "end": v(14.35, -58.6) * mm});
            skArc(sketch, "E2400", {"start": v(14.35, -58.6) * mm, "mid": v(15, -58.43) * mm, "end": v(15.66, -58.26) * mm});
            skLineSegment(sketch, "E2401", {"start": v(15.66, -58.26) * mm, "end": v(15.74, -58.4) * mm});
            skLineSegment(sketch, "E2402", {"start": v(15.74, -58.4) * mm, "end": v(15.83, -58.53) * mm});
            skLineSegment(sketch, "E2403", {"start": v(15.83, -58.53) * mm, "end": v(15.93, -58.67) * mm});
            skLineSegment(sketch, "E2404", {"start": v(15.93, -58.67) * mm, "end": v(16.02, -58.81) * mm});
            skLineSegment(sketch, "E2405", {"start": v(16.02, -58.81) * mm, "end": v(16.12, -58.96) * mm});
            skLineSegment(sketch, "E2406", {"start": v(16.12, -58.96) * mm, "end": v(16.23, -59.1) * mm});
            skLineSegment(sketch, "E2407", {"start": v(16.23, -59.1) * mm, "end": v(16.34, -59.26) * mm});
            skLineSegment(sketch, "E2408", {"start": v(16.34, -59.26) * mm, "end": v(16.45, -59.41) * mm});
            skLineSegment(sketch, "E2409", {"start": v(16.45, -59.41) * mm, "end": v(16.57, -59.57) * mm});
            skLineSegment(sketch, "E2410", {"start": v(16.57, -59.57) * mm, "end": v(16.69, -59.73) * mm});
            skLineSegment(sketch, "E2411", {"start": v(16.69, -59.73) * mm, "end": v(16.81, -59.89) * mm});
            skLineSegment(sketch, "E2412", {"start": v(16.81, -59.89) * mm, "end": v(16.94, -60.05) * mm});
            skLineSegment(sketch, "E2413", {"start": v(16.94, -60.05) * mm, "end": v(17.07, -60.22) * mm});
            skLineSegment(sketch, "E2414", {"start": v(17.07, -60.22) * mm, "end": v(17.21, -60.39) * mm});
            skLineSegment(sketch, "E2415", {"start": v(17.21, -60.39) * mm, "end": v(17.35, -60.56) * mm});
            skLineSegment(sketch, "E2416", {"start": v(17.35, -60.56) * mm, "end": v(17.5, -60.73) * mm});
            skLineSegment(sketch, "E2417", {"start": v(17.5, -60.73) * mm, "end": v(17.65, -60.9) * mm});
            skLineSegment(sketch, "E2418", {"start": v(17.65, -60.9) * mm, "end": v(17.8, -61.08) * mm});
            skLineSegment(sketch, "E2419", {"start": v(17.8, -61.08) * mm, "end": v(17.96, -61.26) * mm});
            skLineSegment(sketch, "E2420", {"start": v(17.96, -61.26) * mm, "end": v(18.13, -61.44) * mm});
            skLineSegment(sketch, "E2421", {"start": v(18.13, -61.44) * mm, "end": v(18.3, -61.62) * mm});
            skLineSegment(sketch, "E2422", {"start": v(18.3, -61.62) * mm, "end": v(18.47, -61.8) * mm});
            skLineSegment(sketch, "E2423", {"start": v(18.47, -61.8) * mm, "end": v(18.64, -61.99) * mm});
            skLineSegment(sketch, "E2424", {"start": v(18.64, -61.99) * mm, "end": v(18.83, -62.17) * mm});
            skLineSegment(sketch, "E2425", {"start": v(18.83, -62.17) * mm, "end": v(19.01, -62.36) * mm});
            skLineSegment(sketch, "E2426", {"start": v(19.01, -62.36) * mm, "end": v(19.2, -62.55) * mm});
            skLineSegment(sketch, "E2427", {"start": v(19.2, -62.55) * mm, "end": v(19.4, -62.74) * mm});
            skLineSegment(sketch, "E2428", {"start": v(19.4, -62.74) * mm, "end": v(19.6, -62.94) * mm});
            skLineSegment(sketch, "E2429", {"start": v(19.6, -62.94) * mm, "end": v(19.7, -63.03) * mm});
            skLineSegment(sketch, "E2430", {"start": v(19.7, -63.03) * mm, "end": v(21.1, -62.58) * mm});
            skLineSegment(sketch, "E2431", {"start": v(21.1, -62.58) * mm, "end": v(21.14, -62.44) * mm});
            skLineSegment(sketch, "E2432", {"start": v(21.14, -62.44) * mm, "end": v(21.19, -62.16) * mm});
            skLineSegment(sketch, "E2433", {"start": v(21.19, -62.16) * mm, "end": v(21.23, -61.9) * mm});
            skLineSegment(sketch, "E2434", {"start": v(21.23, -61.9) * mm, "end": v(21.27, -61.63) * mm});
            skLineSegment(sketch, "E2435", {"start": v(21.27, -61.63) * mm, "end": v(21.31, -61.37) * mm});
            skLineSegment(sketch, "E2436", {"start": v(21.31, -61.37) * mm, "end": v(21.35, -61.1) * mm});
            skLineSegment(sketch, "E2437", {"start": v(21.35, -61.1) * mm, "end": v(21.39, -60.85) * mm});
            skLineSegment(sketch, "E2438", {"start": v(21.39, -60.85) * mm, "end": v(21.42, -60.6) * mm});
            skLineSegment(sketch, "E2439", {"start": v(21.42, -60.6) * mm, "end": v(21.45, -60.36) * mm});
            skLineSegment(sketch, "E2440", {"start": v(21.45, -60.36) * mm, "end": v(21.47, -60.12) * mm});
            skLineSegment(sketch, "E2441", {"start": v(21.47, -60.12) * mm, "end": v(21.5, -59.88) * mm});
            skLineSegment(sketch, "E2442", {"start": v(21.5, -59.88) * mm, "end": v(21.52, -59.64) * mm});
            skLineSegment(sketch, "E2443", {"start": v(21.52, -59.64) * mm, "end": v(21.54, -59.42) * mm});
            skLineSegment(sketch, "E2444", {"start": v(21.54, -59.42) * mm, "end": v(21.55, -59.2) * mm});
            skLineSegment(sketch, "E2445", {"start": v(21.55, -59.2) * mm, "end": v(21.57, -58.97) * mm});
            skLineSegment(sketch, "E2446", {"start": v(21.57, -58.97) * mm, "end": v(21.58, -58.75) * mm});
            skLineSegment(sketch, "E2447", {"start": v(21.58, -58.75) * mm, "end": v(21.6, -58.54) * mm});
            skLineSegment(sketch, "E2448", {"start": v(21.6, -58.54) * mm, "end": v(21.6, -58.33) * mm});
            skLineSegment(sketch, "E2449", {"start": v(21.6, -58.33) * mm, "end": v(21.6, -58.13) * mm});
            skLineSegment(sketch, "E2450", {"start": v(21.6, -58.13) * mm, "end": v(21.61, -57.93) * mm});
            skLineSegment(sketch, "E2451", {"start": v(21.61, -57.93) * mm, "end": v(21.61, -57.73) * mm});
            skLineSegment(sketch, "E2452", {"start": v(21.61, -57.73) * mm, "end": v(21.61, -57.54) * mm});
            skLineSegment(sketch, "E2453", {"start": v(21.61, -57.54) * mm, "end": v(21.61, -57.36) * mm});
            skLineSegment(sketch, "E2454", {"start": v(21.61, -57.36) * mm, "end": v(21.61, -57.18) * mm});
            skLineSegment(sketch, "E2455", {"start": v(21.61, -57.18) * mm, "end": v(21.6, -57) * mm});
            skLineSegment(sketch, "E2456", {"start": v(21.6, -57) * mm, "end": v(21.6, -56.83) * mm});
            skLineSegment(sketch, "E2457", {"start": v(21.6, -56.83) * mm, "end": v(21.6, -56.66) * mm});
            skLineSegment(sketch, "E2458", {"start": v(21.6, -56.66) * mm, "end": v(21.59, -56.5) * mm});
            skLineSegment(sketch, "E2459", {"start": v(21.59, -56.5) * mm, "end": v(21.58, -56.33) * mm});
            skArc(sketch, "E2460", {"start": v(21.58, -56.33) * mm, "mid": v(22.2, -56.09) * mm, "end": v(22.83, -55.84) * mm});
            skLineSegment(sketch, "E2461", {"start": v(22.83, -55.84) * mm, "end": v(22.94, -55.96) * mm});
            skLineSegment(sketch, "E2462", {"start": v(22.94, -55.96) * mm, "end": v(23.04, -56.08) * mm});
            skLineSegment(sketch, "E2463", {"start": v(23.04, -56.08) * mm, "end": v(23.15, -56.21) * mm});
            skLineSegment(sketch, "E2464", {"start": v(23.15, -56.21) * mm, "end": v(23.27, -56.34) * mm});
            skLineSegment(sketch, "E2465", {"start": v(23.27, -56.34) * mm, "end": v(23.39, -56.47) * mm});
            skLineSegment(sketch, "E2466", {"start": v(23.39, -56.47) * mm, "end": v(23.5, -56.6) * mm});
            skLineSegment(sketch, "E2467", {"start": v(23.5, -56.6) * mm, "end": v(23.64, -56.74) * mm});
            skLineSegment(sketch, "E2468", {"start": v(23.64, -56.74) * mm, "end": v(23.77, -56.88) * mm});
            skLineSegment(sketch, "E2469", {"start": v(23.77, -56.88) * mm, "end": v(23.9, -57.02) * mm});
            skLineSegment(sketch, "E2470", {"start": v(23.9, -57.02) * mm, "end": v(24.04, -57.16) * mm});
            skLineSegment(sketch, "E2471", {"start": v(24.04, -57.16) * mm, "end": v(24.19, -57.3) * mm});
            skLineSegment(sketch, "E2472", {"start": v(24.19, -57.3) * mm, "end": v(24.33, -57.45) * mm});
            skLineSegment(sketch, "E2473", {"start": v(24.33, -57.45) * mm, "end": v(24.49, -57.6) * mm});
            skLineSegment(sketch, "E2474", {"start": v(24.49, -57.6) * mm, "end": v(24.64, -57.75) * mm});
            skLineSegment(sketch, "E2475", {"start": v(24.64, -57.75) * mm, "end": v(24.8, -57.9) * mm});
            skLineSegment(sketch, "E2476", {"start": v(24.8, -57.9) * mm, "end": v(24.97, -58.06) * mm});
            skLineSegment(sketch, "E2477", {"start": v(24.97, -58.06) * mm, "end": v(25.14, -58.2) * mm});
            skLineSegment(sketch, "E2478", {"start": v(25.14, -58.2) * mm, "end": v(25.32, -58.37) * mm});
            skLineSegment(sketch, "E2479", {"start": v(25.32, -58.37) * mm, "end": v(25.5, -58.52) * mm});
            skLineSegment(sketch, "E2480", {"start": v(25.5, -58.52) * mm, "end": v(25.68, -58.68) * mm});
            skLineSegment(sketch, "E2481", {"start": v(25.68, -58.68) * mm, "end": v(25.87, -58.84) * mm});
            skLineSegment(sketch, "E2482", {"start": v(25.87, -58.84) * mm, "end": v(26.07, -59) * mm});
            skLineSegment(sketch, "E2483", {"start": v(26.07, -59) * mm, "end": v(26.27, -59.16) * mm});
            skLineSegment(sketch, "E2484", {"start": v(26.27, -59.16) * mm, "end": v(26.47, -59.32) * mm});
            skLineSegment(sketch, "E2485", {"start": v(26.47, -59.32) * mm, "end": v(26.68, -59.49) * mm});
            skLineSegment(sketch, "E2486", {"start": v(26.68, -59.49) * mm, "end": v(26.9, -59.65) * mm});
            skLineSegment(sketch, "E2487", {"start": v(26.9, -59.65) * mm, "end": v(27.11, -59.82) * mm});
            skLineSegment(sketch, "E2488", {"start": v(27.11, -59.82) * mm, "end": v(27.33, -59.98) * mm});
            skLineSegment(sketch, "E2489", {"start": v(27.33, -59.98) * mm, "end": v(27.45, -60.07) * mm});
            skLineSegment(sketch, "E2490", {"start": v(27.45, -60.07) * mm, "end": v(28.79, -59.44) * mm});
            skLineSegment(sketch, "E2491", {"start": v(28.79, -59.44) * mm, "end": v(28.8, -59.3) * mm});
            skLineSegment(sketch, "E2492", {"start": v(28.8, -59.3) * mm, "end": v(28.8, -59.02) * mm});
            skLineSegment(sketch, "E2493", {"start": v(28.8, -59.02) * mm, "end": v(28.82, -58.74) * mm});
            skLineSegment(sketch, "E2494", {"start": v(28.82, -58.74) * mm, "end": v(28.83, -58.48) * mm});
            skLineSegment(sketch, "E2495", {"start": v(28.83, -58.48) * mm, "end": v(28.84, -58.21) * mm});
            skLineSegment(sketch, "E2496", {"start": v(28.84, -58.21) * mm, "end": v(28.84, -57.95) * mm});
            skLineSegment(sketch, "E2497", {"start": v(28.84, -57.95) * mm, "end": v(28.84, -57.7) * mm});
            skLineSegment(sketch, "E2498", {"start": v(28.84, -57.7) * mm, "end": v(28.85, -57.44) * mm});
            skLineSegment(sketch, "E2499", {"start": v(28.85, -57.44) * mm, "end": v(28.84, -57.2) * mm});
            skLineSegment(sketch, "E2500", {"start": v(28.84, -57.2) * mm, "end": v(28.84, -56.95) * mm});
            skLineSegment(sketch, "E2501", {"start": v(28.84, -56.95) * mm, "end": v(28.83, -56.71) * mm});
            skLineSegment(sketch, "E2502", {"start": v(28.83, -56.71) * mm, "end": v(28.82, -56.48) * mm});
            skLineSegment(sketch, "E2503", {"start": v(28.82, -56.48) * mm, "end": v(28.81, -56.25) * mm});
            skLineSegment(sketch, "E2504", {"start": v(28.81, -56.25) * mm, "end": v(28.8, -56.02) * mm});
            skLineSegment(sketch, "E2505", {"start": v(28.8, -56.02) * mm, "end": v(28.79, -55.8) * mm});
            skLineSegment(sketch, "E2506", {"start": v(28.79, -55.8) * mm, "end": v(28.77, -55.58) * mm});
            skLineSegment(sketch, "E2507", {"start": v(28.77, -55.58) * mm, "end": v(28.76, -55.37) * mm});
            skLineSegment(sketch, "E2508", {"start": v(28.76, -55.37) * mm, "end": v(28.74, -55.17) * mm});
            skLineSegment(sketch, "E2509", {"start": v(28.74, -55.17) * mm, "end": v(28.72, -54.96) * mm});
            skLineSegment(sketch, "E2510", {"start": v(28.72, -54.96) * mm, "end": v(28.7, -54.76) * mm});
            skLineSegment(sketch, "E2511", {"start": v(28.7, -54.76) * mm, "end": v(28.68, -54.57) * mm});
            skLineSegment(sketch, "E2512", {"start": v(28.68, -54.57) * mm, "end": v(28.66, -54.38) * mm});
            skLineSegment(sketch, "E2513", {"start": v(28.66, -54.38) * mm, "end": v(28.63, -54.2) * mm});
            skLineSegment(sketch, "E2514", {"start": v(28.63, -54.2) * mm, "end": v(28.6, -54.02) * mm});
            skLineSegment(sketch, "E2515", {"start": v(28.6, -54.02) * mm, "end": v(28.58, -53.84) * mm});
            skLineSegment(sketch, "E2516", {"start": v(28.58, -53.84) * mm, "end": v(28.55, -53.67) * mm});
            skLineSegment(sketch, "E2517", {"start": v(28.55, -53.67) * mm, "end": v(28.52, -53.5) * mm});
            skLineSegment(sketch, "E2518", {"start": v(28.52, -53.5) * mm, "end": v(28.5, -53.34) * mm});
            skLineSegment(sketch, "E2519", {"start": v(28.5, -53.34) * mm, "end": v(28.47, -53.19) * mm});
            skArc(sketch, "E2520", {"start": v(28.47, -53.19) * mm, "mid": v(29.06, -52.86) * mm, "end": v(29.65, -52.53) * mm});
            skLineSegment(sketch, "E2521", {"start": v(29.65, -52.53) * mm, "end": v(29.77, -52.64) * mm});
            skLineSegment(sketch, "E2522", {"start": v(29.77, -52.64) * mm, "end": v(29.9, -52.75) * mm});
            skLineSegment(sketch, "E2523", {"start": v(29.9, -52.75) * mm, "end": v(30.02, -52.87) * mm});
            skLineSegment(sketch, "E2524", {"start": v(30.02, -52.87) * mm, "end": v(30.15, -52.98) * mm});
            skLineSegment(sketch, "E2525", {"start": v(30.15, -52.98) * mm, "end": v(30.28, -53.1) * mm});
            skLineSegment(sketch, "E2526", {"start": v(30.28, -53.1) * mm, "end": v(30.42, -53.21) * mm});
            skLineSegment(sketch, "E2527", {"start": v(30.42, -53.21) * mm, "end": v(30.56, -53.33) * mm});
            skLineSegment(sketch, "E2528", {"start": v(30.56, -53.33) * mm, "end": v(30.7, -53.45) * mm});
            skLineSegment(sketch, "E2529", {"start": v(30.7, -53.45) * mm, "end": v(30.86, -53.58) * mm});
            skLineSegment(sketch, "E2530", {"start": v(30.86, -53.58) * mm, "end": v(31.02, -53.7) * mm});
            skLineSegment(sketch, "E2531", {"start": v(31.02, -53.7) * mm, "end": v(31.18, -53.83) * mm});
            skLineSegment(sketch, "E2532", {"start": v(31.18, -53.83) * mm, "end": v(31.34, -53.95) * mm});
            skLineSegment(sketch, "E2533", {"start": v(31.34, -53.95) * mm, "end": v(31.51, -54.08) * mm});
            skLineSegment(sketch, "E2534", {"start": v(31.51, -54.08) * mm, "end": v(31.69, -54.2) * mm});
            skLineSegment(sketch, "E2535", {"start": v(31.69, -54.2) * mm, "end": v(31.87, -54.34) * mm});
            skLineSegment(sketch, "E2536", {"start": v(31.87, -54.34) * mm, "end": v(32.05, -54.47) * mm});
            skLineSegment(sketch, "E2537", {"start": v(32.05, -54.47) * mm, "end": v(32.24, -54.6) * mm});
            skLineSegment(sketch, "E2538", {"start": v(32.24, -54.6) * mm, "end": v(32.43, -54.73) * mm});
            skLineSegment(sketch, "E2539", {"start": v(32.43, -54.73) * mm, "end": v(32.63, -54.87) * mm});
            skLineSegment(sketch, "E2540", {"start": v(32.63, -54.87) * mm, "end": v(32.84, -55) * mm});
            skLineSegment(sketch, "E2541", {"start": v(32.84, -55) * mm, "end": v(33.04, -55.13) * mm});
            skLineSegment(sketch, "E2542", {"start": v(33.04, -55.13) * mm, "end": v(33.26, -55.27) * mm});
            skLineSegment(sketch, "E2543", {"start": v(33.26, -55.27) * mm, "end": v(33.47, -55.4) * mm});
            skLineSegment(sketch, "E2544", {"start": v(33.47, -55.4) * mm, "end": v(33.7, -55.54) * mm});
            skLineSegment(sketch, "E2545", {"start": v(33.7, -55.54) * mm, "end": v(33.92, -55.68) * mm});
            skLineSegment(sketch, "E2546", {"start": v(33.92, -55.68) * mm, "end": v(34.16, -55.81) * mm});
            skLineSegment(sketch, "E2547", {"start": v(34.16, -55.81) * mm, "end": v(34.4, -55.95) * mm});
            skLineSegment(sketch, "E2548", {"start": v(34.4, -55.95) * mm, "end": v(34.64, -56.08) * mm});
            skLineSegment(sketch, "E2549", {"start": v(34.64, -56.08) * mm, "end": v(34.76, -56.15) * mm});
            skLineSegment(sketch, "E2550", {"start": v(34.76, -56.15) * mm, "end": v(36, -55.36) * mm});
            skLineSegment(sketch, "E2551", {"start": v(36, -55.36) * mm, "end": v(36, -55.22) * mm});
            skLineSegment(sketch, "E2552", {"start": v(36, -55.22) * mm, "end": v(35.98, -54.94) * mm});
            skLineSegment(sketch, "E2553", {"start": v(35.98, -54.94) * mm, "end": v(35.96, -54.67) * mm});
            skLineSegment(sketch, "E2554", {"start": v(35.96, -54.67) * mm, "end": v(35.93, -54.4) * mm});
            skLineSegment(sketch, "E2555", {"start": v(35.93, -54.4) * mm, "end": v(35.9, -54.14) * mm});
            skLineSegment(sketch, "E2556", {"start": v(35.9, -54.14) * mm, "end": v(35.88, -53.88) * mm});
            skLineSegment(sketch, "E2557", {"start": v(35.88, -53.88) * mm, "end": v(35.85, -53.62) * mm});
            skLineSegment(sketch, "E2558", {"start": v(35.85, -53.62) * mm, "end": v(35.82, -53.37) * mm});
            skLineSegment(sketch, "E2559", {"start": v(35.82, -53.37) * mm, "end": v(35.78, -53.13) * mm});
            skLineSegment(sketch, "E2560", {"start": v(35.78, -53.13) * mm, "end": v(35.75, -52.89) * mm});
            skLineSegment(sketch, "E2561", {"start": v(35.75, -52.89) * mm, "end": v(35.71, -52.65) * mm});
            skLineSegment(sketch, "E2562", {"start": v(35.71, -52.65) * mm, "end": v(35.68, -52.42) * mm});
            skLineSegment(sketch, "E2563", {"start": v(35.68, -52.42) * mm, "end": v(35.64, -52.2) * mm});
            skLineSegment(sketch, "E2564", {"start": v(35.64, -52.2) * mm, "end": v(35.6, -51.97) * mm});
            skLineSegment(sketch, "E2565", {"start": v(35.6, -51.97) * mm, "end": v(35.56, -51.75) * mm});
            skLineSegment(sketch, "E2566", {"start": v(35.56, -51.75) * mm, "end": v(35.51, -51.54) * mm});
            skLineSegment(sketch, "E2567", {"start": v(35.51, -51.54) * mm, "end": v(35.47, -51.33) * mm});
            skLineSegment(sketch, "E2568", {"start": v(35.47, -51.33) * mm, "end": v(35.43, -51.13) * mm});
            skLineSegment(sketch, "E2569", {"start": v(35.43, -51.13) * mm, "end": v(35.38, -50.93) * mm});
            skLineSegment(sketch, "E2570", {"start": v(35.38, -50.93) * mm, "end": v(35.34, -50.74) * mm});
            skLineSegment(sketch, "E2571", {"start": v(35.34, -50.74) * mm, "end": v(35.3, -50.55) * mm});
            skLineSegment(sketch, "E2572", {"start": v(35.3, -50.55) * mm, "end": v(35.24, -50.36) * mm});
            skLineSegment(sketch, "E2573", {"start": v(35.24, -50.36) * mm, "end": v(35.2, -50.18) * mm});
            skLineSegment(sketch, "E2574", {"start": v(35.2, -50.18) * mm, "end": v(35.15, -50) * mm});
            skLineSegment(sketch, "E2575", {"start": v(35.15, -50) * mm, "end": v(35.1, -49.83) * mm});
            skLineSegment(sketch, "E2576", {"start": v(35.1, -49.83) * mm, "end": v(35.05, -49.67) * mm});
            skLineSegment(sketch, "E2577", {"start": v(35.05, -49.67) * mm, "end": v(35, -49.5) * mm});
            skLineSegment(sketch, "E2578", {"start": v(35, -49.5) * mm, "end": v(34.96, -49.35) * mm});
            skLineSegment(sketch, "E2579", {"start": v(34.96, -49.35) * mm, "end": v(34.9, -49.2) * mm});
            skArc(sketch, "E2580", {"start": v(34.9, -49.2) * mm, "mid": v(35.46, -48.8) * mm, "end": v(36, -48.4) * mm});
            skLineSegment(sketch, "E2581", {"start": v(36, -48.4) * mm, "end": v(36.13, -48.5) * mm});
            skLineSegment(sketch, "E2582", {"start": v(36.13, -48.5) * mm, "end": v(36.27, -48.6) * mm});
            skLineSegment(sketch, "E2583", {"start": v(36.27, -48.6) * mm, "end": v(36.4, -48.69) * mm});
            skLineSegment(sketch, "E2584", {"start": v(36.4, -48.69) * mm, "end": v(36.55, -48.78) * mm});
            skLineSegment(sketch, "E2585", {"start": v(36.55, -48.78) * mm, "end": v(36.7, -48.88) * mm});
            skLineSegment(sketch, "E2586", {"start": v(36.7, -48.88) * mm, "end": v(36.85, -48.98) * mm});
            skLineSegment(sketch, "E2587", {"start": v(36.85, -48.98) * mm, "end": v(37, -49.08) * mm});
            skLineSegment(sketch, "E2588", {"start": v(37, -49.08) * mm, "end": v(37.17, -49.18) * mm});
            skLineSegment(sketch, "E2589", {"start": v(37.17, -49.18) * mm, "end": v(37.33, -49.29) * mm});
            skLineSegment(sketch, "E2590", {"start": v(37.33, -49.29) * mm, "end": v(37.5, -49.39) * mm});
            skLineSegment(sketch, "E2591", {"start": v(37.5, -49.39) * mm, "end": v(37.68, -49.5) * mm});
            skLineSegment(sketch, "E2592", {"start": v(37.68, -49.5) * mm, "end": v(37.86, -49.6) * mm});
            skLineSegment(sketch, "E2593", {"start": v(37.86, -49.6) * mm, "end": v(38.04, -49.7) * mm});
            skLineSegment(sketch, "E2594", {"start": v(38.04, -49.7) * mm, "end": v(38.23, -49.8) * mm});
            skLineSegment(sketch, "E2595", {"start": v(38.23, -49.8) * mm, "end": v(38.43, -49.92) * mm});
            skLineSegment(sketch, "E2596", {"start": v(38.43, -49.92) * mm, "end": v(38.63, -50.02) * mm});
            skLineSegment(sketch, "E2597", {"start": v(38.63, -50.02) * mm, "end": v(38.83, -50.13) * mm});
            skLineSegment(sketch, "E2598", {"start": v(38.83, -50.13) * mm, "end": v(39.04, -50.24) * mm});
            skLineSegment(sketch, "E2599", {"start": v(39.04, -50.24) * mm, "end": v(39.25, -50.34) * mm});
            skLineSegment(sketch, "E2600", {"start": v(39.25, -50.34) * mm, "end": v(39.47, -50.45) * mm});
            skLineSegment(sketch, "E2601", {"start": v(39.47, -50.45) * mm, "end": v(39.7, -50.56) * mm});
            skLineSegment(sketch, "E2602", {"start": v(39.7, -50.56) * mm, "end": v(39.92, -50.66) * mm});
            skLineSegment(sketch, "E2603", {"start": v(39.92, -50.66) * mm, "end": v(40.15, -50.77) * mm});
            skLineSegment(sketch, "E2604", {"start": v(40.15, -50.77) * mm, "end": v(40.4, -50.88) * mm});
            skLineSegment(sketch, "E2605", {"start": v(40.4, -50.88) * mm, "end": v(40.63, -50.98) * mm});
            skLineSegment(sketch, "E2606", {"start": v(40.63, -50.98) * mm, "end": v(40.88, -51.1) * mm});
            skLineSegment(sketch, "E2607", {"start": v(40.88, -51.1) * mm, "end": v(41.14, -51.2) * mm});
            skLineSegment(sketch, "E2608", {"start": v(41.14, -51.2) * mm, "end": v(41.4, -51.3) * mm});
            skLineSegment(sketch, "E2609", {"start": v(41.4, -51.3) * mm, "end": v(41.52, -51.35) * mm});
            skLineSegment(sketch, "E2610", {"start": v(41.52, -51.35) * mm, "end": v(42.66, -50.41) * mm});
            skLineSegment(sketch, "E2611", {"start": v(42.66, -50.41) * mm, "end": v(42.64, -50.27) * mm});
            skLineSegment(sketch, "E2612", {"start": v(42.64, -50.27) * mm, "end": v(42.58, -50) * mm});
            skLineSegment(sketch, "E2613", {"start": v(42.58, -50) * mm, "end": v(42.53, -49.73) * mm});
            skLineSegment(sketch, "E2614", {"start": v(42.53, -49.73) * mm, "end": v(42.47, -49.47) * mm});
            skLineSegment(sketch, "E2615", {"start": v(42.47, -49.47) * mm, "end": v(42.4, -49.2) * mm});
            skLineSegment(sketch, "E2616", {"start": v(42.4, -49.2) * mm, "end": v(42.35, -48.96) * mm});
            skLineSegment(sketch, "E2617", {"start": v(42.35, -48.96) * mm, "end": v(42.29, -48.7) * mm});
            skLineSegment(sketch, "E2618", {"start": v(42.29, -48.7) * mm, "end": v(42.22, -48.46) * mm});
            skLineSegment(sketch, "E2619", {"start": v(42.22, -48.46) * mm, "end": v(42.16, -48.22) * mm});
            skLineSegment(sketch, "E2620", {"start": v(42.16, -48.22) * mm, "end": v(42.1, -47.99) * mm});
            skLineSegment(sketch, "E2621", {"start": v(42.1, -47.99) * mm, "end": v(42.03, -47.76) * mm});
            skLineSegment(sketch, "E2622", {"start": v(42.03, -47.76) * mm, "end": v(41.96, -47.53) * mm});
            skLineSegment(sketch, "E2623", {"start": v(41.96, -47.53) * mm, "end": v(41.9, -47.31) * mm});
            skLineSegment(sketch, "E2624", {"start": v(41.9, -47.31) * mm, "end": v(41.83, -47.1) * mm});
            skLineSegment(sketch, "E2625", {"start": v(41.83, -47.1) * mm, "end": v(41.76, -46.89) * mm});
            skLineSegment(sketch, "E2626", {"start": v(41.76, -46.89) * mm, "end": v(41.7, -46.68) * mm});
            skLineSegment(sketch, "E2627", {"start": v(41.7, -46.68) * mm, "end": v(41.63, -46.48) * mm});
            skLineSegment(sketch, "E2628", {"start": v(41.63, -46.48) * mm, "end": v(41.56, -46.28) * mm});
            skLineSegment(sketch, "E2629", {"start": v(41.56, -46.28) * mm, "end": v(41.49, -46.1) * mm});
            skLineSegment(sketch, "E2630", {"start": v(41.49, -46.1) * mm, "end": v(41.42, -45.9) * mm});
            skLineSegment(sketch, "E2631", {"start": v(41.42, -45.9) * mm, "end": v(41.35, -45.72) * mm});
            skLineSegment(sketch, "E2632", {"start": v(41.35, -45.72) * mm, "end": v(41.28, -45.55) * mm});
            skLineSegment(sketch, "E2633", {"start": v(41.28, -45.55) * mm, "end": v(41.2, -45.37) * mm});
            skLineSegment(sketch, "E2634", {"start": v(41.2, -45.37) * mm, "end": v(41.14, -45.2) * mm});
            skLineSegment(sketch, "E2635", {"start": v(41.14, -45.2) * mm, "end": v(41.07, -45.04) * mm});
            skLineSegment(sketch, "E2636", {"start": v(41.07, -45.04) * mm, "end": v(41, -44.88) * mm});
            skLineSegment(sketch, "E2637", {"start": v(41, -44.88) * mm, "end": v(40.93, -44.73) * mm});
            skLineSegment(sketch, "E2638", {"start": v(40.93, -44.73) * mm, "end": v(40.87, -44.58) * mm});
            skLineSegment(sketch, "E2639", {"start": v(40.87, -44.58) * mm, "end": v(40.8, -44.43) * mm});
            skArc(sketch, "E2640", {"start": v(40.8, -44.43) * mm, "mid": v(41.3, -43.97) * mm, "end": v(41.79, -43.5) * mm});
            skLineSegment(sketch, "E2641", {"start": v(41.79, -43.5) * mm, "end": v(41.92, -43.59) * mm});
            skLineSegment(sketch, "E2642", {"start": v(41.92, -43.59) * mm, "end": v(42.07, -43.66) * mm});
            skLineSegment(sketch, "E2643", {"start": v(42.07, -43.66) * mm, "end": v(42.22, -43.74) * mm});
            skLineSegment(sketch, "E2644", {"start": v(42.22, -43.74) * mm, "end": v(42.37, -43.82) * mm});
            skLineSegment(sketch, "E2645", {"start": v(42.37, -43.82) * mm, "end": v(42.53, -43.9) * mm});
            skLineSegment(sketch, "E2646", {"start": v(42.53, -43.9) * mm, "end": v(42.7, -43.98) * mm});
            skLineSegment(sketch, "E2647", {"start": v(42.7, -43.98) * mm, "end": v(42.86, -44.06) * mm});
            skLineSegment(sketch, "E2648", {"start": v(42.86, -44.06) * mm, "end": v(43.04, -44.14) * mm});
            skLineSegment(sketch, "E2649", {"start": v(43.04, -44.14) * mm, "end": v(43.21, -44.22) * mm});
            skLineSegment(sketch, "E2650", {"start": v(43.21, -44.22) * mm, "end": v(43.4, -44.3) * mm});
            skLineSegment(sketch, "E2651", {"start": v(43.4, -44.3) * mm, "end": v(43.58, -44.38) * mm});
            skLineSegment(sketch, "E2652", {"start": v(43.58, -44.38) * mm, "end": v(43.78, -44.46) * mm});
            skLineSegment(sketch, "E2653", {"start": v(43.78, -44.46) * mm, "end": v(43.97, -44.54) * mm});
            skLineSegment(sketch, "E2654", {"start": v(43.97, -44.54) * mm, "end": v(44.17, -44.62) * mm});
            skLineSegment(sketch, "E2655", {"start": v(44.17, -44.62) * mm, "end": v(44.38, -44.7) * mm});
            skLineSegment(sketch, "E2656", {"start": v(44.38, -44.7) * mm, "end": v(44.6, -44.79) * mm});
            skLineSegment(sketch, "E2657", {"start": v(44.6, -44.79) * mm, "end": v(44.8, -44.87) * mm});
            skLineSegment(sketch, "E2658", {"start": v(44.8, -44.87) * mm, "end": v(45.03, -44.95) * mm});
            skLineSegment(sketch, "E2659", {"start": v(45.03, -44.95) * mm, "end": v(45.25, -45.03) * mm});
            skLineSegment(sketch, "E2660", {"start": v(45.25, -45.03) * mm, "end": v(45.48, -45.1) * mm});
            skLineSegment(sketch, "E2661", {"start": v(45.48, -45.1) * mm, "end": v(45.72, -45.18) * mm});
            skLineSegment(sketch, "E2662", {"start": v(45.72, -45.18) * mm, "end": v(45.96, -45.26) * mm});
            skLineSegment(sketch, "E2663", {"start": v(45.96, -45.26) * mm, "end": v(46.2, -45.34) * mm});
            skLineSegment(sketch, "E2664", {"start": v(46.2, -45.34) * mm, "end": v(46.45, -45.41) * mm});
            skLineSegment(sketch, "E2665", {"start": v(46.45, -45.41) * mm, "end": v(46.7, -45.49) * mm});
            skLineSegment(sketch, "E2666", {"start": v(46.7, -45.49) * mm, "end": v(46.96, -45.56) * mm});
            skLineSegment(sketch, "E2667", {"start": v(46.96, -45.56) * mm, "end": v(47.23, -45.64) * mm});
            skLineSegment(sketch, "E2668", {"start": v(47.23, -45.64) * mm, "end": v(47.5, -45.7) * mm});
            skLineSegment(sketch, "E2669", {"start": v(47.5, -45.7) * mm, "end": v(47.63, -45.74) * mm});
            skLineSegment(sketch, "E2670", {"start": v(47.63, -45.74) * mm, "end": v(48.64, -44.67) * mm});
            skLineSegment(sketch, "E2671", {"start": v(48.64, -44.67) * mm, "end": v(48.6, -44.53) * mm});
            skLineSegment(sketch, "E2672", {"start": v(48.6, -44.53) * mm, "end": v(48.51, -44.27) * mm});
            skLineSegment(sketch, "E2673", {"start": v(48.51, -44.27) * mm, "end": v(48.42, -44) * mm});
            skLineSegment(sketch, "E2674", {"start": v(48.42, -44) * mm, "end": v(48.33, -43.76) * mm});
            skLineSegment(sketch, "E2675", {"start": v(48.33, -43.76) * mm, "end": v(48.24, -43.5) * mm});
            skLineSegment(sketch, "E2676", {"start": v(48.24, -43.5) * mm, "end": v(48.15, -43.26) * mm});
            skLineSegment(sketch, "E2677", {"start": v(48.15, -43.26) * mm, "end": v(48.06, -43.02) * mm});
            skLineSegment(sketch, "E2678", {"start": v(48.06, -43.02) * mm, "end": v(47.97, -42.79) * mm});
            skLineSegment(sketch, "E2679", {"start": v(47.97, -42.79) * mm, "end": v(47.87, -42.56) * mm});
            skLineSegment(sketch, "E2680", {"start": v(47.87, -42.56) * mm, "end": v(47.78, -42.33) * mm});
            skLineSegment(sketch, "E2681", {"start": v(47.78, -42.33) * mm, "end": v(47.69, -42.12) * mm});
            skLineSegment(sketch, "E2682", {"start": v(47.69, -42.12) * mm, "end": v(47.6, -41.9) * mm});
            skLineSegment(sketch, "E2683", {"start": v(47.6, -41.9) * mm, "end": v(47.5, -41.7) * mm});
            skLineSegment(sketch, "E2684", {"start": v(47.5, -41.7) * mm, "end": v(47.4, -41.48) * mm});
            skLineSegment(sketch, "E2685", {"start": v(47.4, -41.48) * mm, "end": v(47.3, -41.28) * mm});
            skLineSegment(sketch, "E2686", {"start": v(47.3, -41.28) * mm, "end": v(47.22, -41.09) * mm});
            skLineSegment(sketch, "E2687", {"start": v(47.22, -41.09) * mm, "end": v(47.12, -40.9) * mm});
            skLineSegment(sketch, "E2688", {"start": v(47.12, -40.9) * mm, "end": v(47.03, -40.71) * mm});
            skLineSegment(sketch, "E2689", {"start": v(47.03, -40.71) * mm, "end": v(46.94, -40.53) * mm});
            skLineSegment(sketch, "E2690", {"start": v(46.94, -40.53) * mm, "end": v(46.84, -40.35) * mm});
            skLineSegment(sketch, "E2691", {"start": v(46.84, -40.35) * mm, "end": v(46.75, -40.18) * mm});
            skLineSegment(sketch, "E2692", {"start": v(46.75, -40.18) * mm, "end": v(46.66, -40.01) * mm});
            skLineSegment(sketch, "E2693", {"start": v(46.66, -40.01) * mm, "end": v(46.57, -39.85) * mm});
            skLineSegment(sketch, "E2694", {"start": v(46.57, -39.85) * mm, "end": v(46.48, -39.7) * mm});
            skLineSegment(sketch, "E2695", {"start": v(46.48, -39.7) * mm, "end": v(46.4, -39.54) * mm});
            skLineSegment(sketch, "E2696", {"start": v(46.4, -39.54) * mm, "end": v(46.3, -39.4) * mm});
            skLineSegment(sketch, "E2697", {"start": v(46.3, -39.4) * mm, "end": v(46.22, -39.25) * mm});
            skLineSegment(sketch, "E2698", {"start": v(46.22, -39.25) * mm, "end": v(46.13, -39.1) * mm});
            skLineSegment(sketch, "E2699", {"start": v(46.13, -39.1) * mm, "end": v(46.05, -38.97) * mm});
            skArc(sketch, "E2700", {"start": v(46.05, -38.97) * mm, "mid": v(46.48, -38.45) * mm, "end": v(46.9, -37.93) * mm});
            skLineSegment(sketch, "E2701", {"start": v(46.9, -37.93) * mm, "end": v(47.06, -37.99) * mm});
            skLineSegment(sketch, "E2702", {"start": v(47.06, -37.99) * mm, "end": v(47.21, -38.05) * mm});
            skLineSegment(sketch, "E2703", {"start": v(47.21, -38.05) * mm, "end": v(47.37, -38.1) * mm});
            skLineSegment(sketch, "E2704", {"start": v(47.37, -38.1) * mm, "end": v(47.53, -38.16) * mm});
            skLineSegment(sketch, "E2705", {"start": v(47.53, -38.16) * mm, "end": v(47.7, -38.22) * mm});
            skLineSegment(sketch, "E2706", {"start": v(47.7, -38.22) * mm, "end": v(47.87, -38.28) * mm});
            skLineSegment(sketch, "E2707", {"start": v(47.87, -38.28) * mm, "end": v(48.05, -38.34) * mm});
            skLineSegment(sketch, "E2708", {"start": v(48.05, -38.34) * mm, "end": v(48.23, -38.4) * mm});
            skLineSegment(sketch, "E2709", {"start": v(48.23, -38.4) * mm, "end": v(48.42, -38.45) * mm});
            skLineSegment(sketch, "E2710", {"start": v(48.42, -38.45) * mm, "end": v(48.6, -38.51) * mm});
            skLineSegment(sketch, "E2711", {"start": v(48.6, -38.51) * mm, "end": v(48.8, -38.57) * mm});
            skLineSegment(sketch, "E2712", {"start": v(48.8, -38.57) * mm, "end": v(49, -38.62) * mm});
            skLineSegment(sketch, "E2713", {"start": v(49, -38.62) * mm, "end": v(49.2, -38.68) * mm});
            skLineSegment(sketch, "E2714", {"start": v(49.2, -38.68) * mm, "end": v(49.42, -38.74) * mm});
            skLineSegment(sketch, "E2715", {"start": v(49.42, -38.74) * mm, "end": v(49.63, -38.8) * mm});
            skLineSegment(sketch, "E2716", {"start": v(49.63, -38.8) * mm, "end": v(49.85, -38.84) * mm});
            skLineSegment(sketch, "E2717", {"start": v(49.85, -38.84) * mm, "end": v(50.08, -38.9) * mm});
            skLineSegment(sketch, "E2718", {"start": v(50.08, -38.9) * mm, "end": v(50.3, -38.95) * mm});
            skLineSegment(sketch, "E2719", {"start": v(50.3, -38.95) * mm, "end": v(50.54, -39) * mm});
            skLineSegment(sketch, "E2720", {"start": v(50.54, -39) * mm, "end": v(50.78, -39.05) * mm});
            skLineSegment(sketch, "E2721", {"start": v(50.78, -39.05) * mm, "end": v(51.02, -39.1) * mm});
            skLineSegment(sketch, "E2722", {"start": v(51.02, -39.1) * mm, "end": v(51.27, -39.14) * mm});
            skLineSegment(sketch, "E2723", {"start": v(51.27, -39.14) * mm, "end": v(51.52, -39.2) * mm});
            skLineSegment(sketch, "E2724", {"start": v(51.52, -39.2) * mm, "end": v(51.78, -39.23) * mm});
            skLineSegment(sketch, "E2725", {"start": v(51.78, -39.23) * mm, "end": v(52.04, -39.28) * mm});
            skLineSegment(sketch, "E2726", {"start": v(52.04, -39.28) * mm, "end": v(52.3, -39.32) * mm});
            skLineSegment(sketch, "E2727", {"start": v(52.3, -39.32) * mm, "end": v(52.57, -39.36) * mm});
            skLineSegment(sketch, "E2728", {"start": v(52.57, -39.36) * mm, "end": v(52.85, -39.4) * mm});
            skLineSegment(sketch, "E2729", {"start": v(52.85, -39.4) * mm, "end": v(52.99, -39.41) * mm});
            skLineSegment(sketch, "E2730", {"start": v(52.99, -39.41) * mm, "end": v(53.86, -38.22) * mm});
            skLineSegment(sketch, "E2731", {"start": v(53.86, -38.22) * mm, "end": v(53.8, -38.09) * mm});
            skLineSegment(sketch, "E2732", {"start": v(53.8, -38.09) * mm, "end": v(53.68, -37.84) * mm});
            skLineSegment(sketch, "E2733", {"start": v(53.68, -37.84) * mm, "end": v(53.56, -37.6) * mm});
            skLineSegment(sketch, "E2734", {"start": v(53.56, -37.6) * mm, "end": v(53.44, -37.35) * mm});
            skLineSegment(sketch, "E2735", {"start": v(53.44, -37.35) * mm, "end": v(53.31, -37.12) * mm});
            skLineSegment(sketch, "E2736", {"start": v(53.31, -37.12) * mm, "end": v(53.2, -36.89) * mm});
            skLineSegment(sketch, "E2737", {"start": v(53.2, -36.89) * mm, "end": v(53.07, -36.66) * mm});
            skLineSegment(sketch, "E2738", {"start": v(53.07, -36.66) * mm, "end": v(52.95, -36.44) * mm});
            skLineSegment(sketch, "E2739", {"start": v(52.95, -36.44) * mm, "end": v(52.83, -36.22) * mm});
            skLineSegment(sketch, "E2740", {"start": v(52.83, -36.22) * mm, "end": v(52.7, -36.01) * mm});
            skLineSegment(sketch, "E2741", {"start": v(52.7, -36.01) * mm, "end": v(52.59, -35.8) * mm});
            skLineSegment(sketch, "E2742", {"start": v(52.59, -35.8) * mm, "end": v(52.47, -35.6) * mm});
            skLineSegment(sketch, "E2743", {"start": v(52.47, -35.6) * mm, "end": v(52.35, -35.4) * mm});
            skLineSegment(sketch, "E2744", {"start": v(52.35, -35.4) * mm, "end": v(52.23, -35.22) * mm});
            skLineSegment(sketch, "E2745", {"start": v(52.23, -35.22) * mm, "end": v(52.11, -35.03) * mm});
            skLineSegment(sketch, "E2746", {"start": v(52.11, -35.03) * mm, "end": v(52, -34.85) * mm});
            skLineSegment(sketch, "E2747", {"start": v(52, -34.85) * mm, "end": v(51.88, -34.67) * mm});
            skLineSegment(sketch, "E2748", {"start": v(51.88, -34.67) * mm, "end": v(51.76, -34.5) * mm});
            skLineSegment(sketch, "E2749", {"start": v(51.76, -34.5) * mm, "end": v(51.65, -34.33) * mm});
            skLineSegment(sketch, "E2750", {"start": v(51.65, -34.33) * mm, "end": v(51.53, -34.16) * mm});
            skLineSegment(sketch, "E2751", {"start": v(51.53, -34.16) * mm, "end": v(51.42, -34) * mm});
            skLineSegment(sketch, "E2752", {"start": v(51.42, -34) * mm, "end": v(51.3, -33.85) * mm});
            skLineSegment(sketch, "E2753", {"start": v(51.3, -33.85) * mm, "end": v(51.2, -33.7) * mm});
            skLineSegment(sketch, "E2754", {"start": v(51.2, -33.7) * mm, "end": v(51.09, -33.55) * mm});
            skLineSegment(sketch, "E2755", {"start": v(51.09, -33.55) * mm, "end": v(50.98, -33.41) * mm});
            skLineSegment(sketch, "E2756", {"start": v(50.98, -33.41) * mm, "end": v(50.88, -33.28) * mm});
            skLineSegment(sketch, "E2757", {"start": v(50.88, -33.28) * mm, "end": v(50.77, -33.14) * mm});
            skLineSegment(sketch, "E2758", {"start": v(50.77, -33.14) * mm, "end": v(50.67, -33.02) * mm});
            skLineSegment(sketch, "E2759", {"start": v(50.67, -33.02) * mm, "end": v(50.57, -32.9) * mm});
            skArc(sketch, "E2760", {"start": v(50.57, -32.9) * mm, "mid": v(50.93, -32.32) * mm, "end": v(51.3, -31.75) * mm});
            skLineSegment(sketch, "E2761", {"start": v(51.3, -31.75) * mm, "end": v(51.45, -31.79) * mm});
            skLineSegment(sketch, "E2762", {"start": v(51.45, -31.79) * mm, "end": v(51.6, -31.83) * mm});
            skLineSegment(sketch, "E2763", {"start": v(51.6, -31.83) * mm, "end": v(51.77, -31.87) * mm});
            skLineSegment(sketch, "E2764", {"start": v(51.77, -31.87) * mm, "end": v(51.94, -31.9) * mm});
            skLineSegment(sketch, "E2765", {"start": v(51.94, -31.9) * mm, "end": v(52.11, -31.94) * mm});
            skLineSegment(sketch, "E2766", {"start": v(52.11, -31.94) * mm, "end": v(52.3, -31.98) * mm});
            skLineSegment(sketch, "E2767", {"start": v(52.3, -31.98) * mm, "end": v(52.47, -32.01) * mm});
            skLineSegment(sketch, "E2768", {"start": v(52.47, -32.01) * mm, "end": v(52.66, -32.05) * mm});
            skLineSegment(sketch, "E2769", {"start": v(52.66, -32.05) * mm, "end": v(52.85, -32.08) * mm});
            skLineSegment(sketch, "E2770", {"start": v(52.85, -32.08) * mm, "end": v(53.05, -32.12) * mm});
            skLineSegment(sketch, "E2771", {"start": v(53.05, -32.12) * mm, "end": v(53.25, -32.15) * mm});
            skLineSegment(sketch, "E2772", {"start": v(53.25, -32.15) * mm, "end": v(53.46, -32.18) * mm});
            skLineSegment(sketch, "E2773", {"start": v(53.46, -32.18) * mm, "end": v(53.67, -32.2) * mm});
            skLineSegment(sketch, "E2774", {"start": v(53.67, -32.2) * mm, "end": v(53.88, -32.24) * mm});
            skLineSegment(sketch, "E2775", {"start": v(53.88, -32.24) * mm, "end": v(54.1, -32.26) * mm});
            skLineSegment(sketch, "E2776", {"start": v(54.1, -32.26) * mm, "end": v(54.33, -32.29) * mm});
            skLineSegment(sketch, "E2777", {"start": v(54.33, -32.29) * mm, "end": v(54.56, -32.31) * mm});
            skLineSegment(sketch, "E2778", {"start": v(54.56, -32.31) * mm, "end": v(54.79, -32.34) * mm});
            skLineSegment(sketch, "E2779", {"start": v(54.79, -32.34) * mm, "end": v(55.03, -32.36) * mm});
            skLineSegment(sketch, "E2780", {"start": v(55.03, -32.36) * mm, "end": v(55.27, -32.38) * mm});
            skLineSegment(sketch, "E2781", {"start": v(55.27, -32.38) * mm, "end": v(55.52, -32.4) * mm});
            skLineSegment(sketch, "E2782", {"start": v(55.52, -32.4) * mm, "end": v(55.77, -32.41) * mm});
            skLineSegment(sketch, "E2783", {"start": v(55.77, -32.41) * mm, "end": v(56.02, -32.42) * mm});
            skLineSegment(sketch, "E2784", {"start": v(56.02, -32.42) * mm, "end": v(56.28, -32.44) * mm});
            skLineSegment(sketch, "E2785", {"start": v(56.28, -32.44) * mm, "end": v(56.55, -32.45) * mm});
            skLineSegment(sketch, "E2786", {"start": v(56.55, -32.45) * mm, "end": v(56.82, -32.45) * mm});
            skLineSegment(sketch, "E2787", {"start": v(56.82, -32.45) * mm, "end": v(57.1, -32.46) * mm});
            skLineSegment(sketch, "E2788", {"start": v(57.1, -32.46) * mm, "end": v(57.37, -32.46) * mm});
            skLineSegment(sketch, "E2789", {"start": v(57.37, -32.46) * mm, "end": v(57.51, -32.46) * mm});
            skLineSegment(sketch, "E2790", {"start": v(57.51, -32.46) * mm, "end": v(58.22, -31.16) * mm});
            skLineSegment(sketch, "E2791", {"start": v(58.22, -31.16) * mm, "end": v(58.15, -31.05) * mm});
            skLineSegment(sketch, "E2792", {"start": v(58.15, -31.05) * mm, "end": v(58, -30.81) * mm});
            skLineSegment(sketch, "E2793", {"start": v(58, -30.81) * mm, "end": v(57.85, -30.58) * mm});
            skLineSegment(sketch, "E2794", {"start": v(57.85, -30.58) * mm, "end": v(57.7, -30.36) * mm});
            skLineSegment(sketch, "E2795", {"start": v(57.7, -30.36) * mm, "end": v(57.55, -30.14) * mm});
            skLineSegment(sketch, "E2796", {"start": v(57.55, -30.14) * mm, "end": v(57.4, -29.93) * mm});
            skLineSegment(sketch, "E2797", {"start": v(57.4, -29.93) * mm, "end": v(57.25, -29.72) * mm});
            skLineSegment(sketch, "E2798", {"start": v(57.25, -29.72) * mm, "end": v(57.1, -29.52) * mm});
            skLineSegment(sketch, "E2799", {"start": v(57.1, -29.52) * mm, "end": v(56.95, -29.32) * mm});
            skLineSegment(sketch, "E2800", {"start": v(56.95, -29.32) * mm, "end": v(56.8, -29.12) * mm});
            skLineSegment(sketch, "E2801", {"start": v(56.8, -29.12) * mm, "end": v(56.66, -28.93) * mm});
            skLineSegment(sketch, "E2802", {"start": v(56.66, -28.93) * mm, "end": v(56.52, -28.75) * mm});
            skLineSegment(sketch, "E2803", {"start": v(56.52, -28.75) * mm, "end": v(56.37, -28.57) * mm});
            skLineSegment(sketch, "E2804", {"start": v(56.37, -28.57) * mm, "end": v(56.23, -28.4) * mm});
            skLineSegment(sketch, "E2805", {"start": v(56.23, -28.4) * mm, "end": v(56.1, -28.22) * mm});
            skLineSegment(sketch, "E2806", {"start": v(56.1, -28.22) * mm, "end": v(55.95, -28.06) * mm});
            skLineSegment(sketch, "E2807", {"start": v(55.95, -28.06) * mm, "end": v(55.81, -27.9) * mm});
            skLineSegment(sketch, "E2808", {"start": v(55.81, -27.9) * mm, "end": v(55.68, -27.74) * mm});
            skLineSegment(sketch, "E2809", {"start": v(55.68, -27.74) * mm, "end": v(55.54, -27.58) * mm});
            skLineSegment(sketch, "E2810", {"start": v(55.54, -27.58) * mm, "end": v(55.4, -27.44) * mm});
            skLineSegment(sketch, "E2811", {"start": v(55.4, -27.44) * mm, "end": v(55.28, -27.3) * mm});
            skLineSegment(sketch, "E2812", {"start": v(55.28, -27.3) * mm, "end": v(55.15, -27.15) * mm});
            skLineSegment(sketch, "E2813", {"start": v(55.15, -27.15) * mm, "end": v(55.02, -27.02) * mm});
            skLineSegment(sketch, "E2814", {"start": v(55.02, -27.02) * mm, "end": v(54.9, -26.89) * mm});
            skLineSegment(sketch, "E2815", {"start": v(54.9, -26.89) * mm, "end": v(54.77, -26.76) * mm});
            skLineSegment(sketch, "E2816", {"start": v(54.77, -26.76) * mm, "end": v(54.65, -26.64) * mm});
            skLineSegment(sketch, "E2817", {"start": v(54.65, -26.64) * mm, "end": v(54.53, -26.52) * mm});
            skLineSegment(sketch, "E2818", {"start": v(54.53, -26.52) * mm, "end": v(54.4, -26.4) * mm});
            skLineSegment(sketch, "E2819", {"start": v(54.4, -26.4) * mm, "end": v(54.3, -26.3) * mm});
            skArc(sketch, "E2820", {"start": v(54.3, -26.3) * mm, "mid": v(54.58, -25.68) * mm, "end": v(54.87, -25.07) * mm});
            skLineSegment(sketch, "E2821", {"start": v(54.87, -25.07) * mm, "end": v(55.03, -25.1) * mm});
            skLineSegment(sketch, "E2822", {"start": v(55.03, -25.1) * mm, "end": v(55.19, -25.1) * mm});
            skLineSegment(sketch, "E2823", {"start": v(55.19, -25.1) * mm, "end": v(55.36, -25.13) * mm});
            skLineSegment(sketch, "E2824", {"start": v(55.36, -25.13) * mm, "end": v(55.53, -25.14) * mm});
            skLineSegment(sketch, "E2825", {"start": v(55.53, -25.14) * mm, "end": v(55.7, -25.16) * mm});
            skLineSegment(sketch, "E2826", {"start": v(55.7, -25.16) * mm, "end": v(55.89, -25.17) * mm});
            skLineSegment(sketch, "E2827", {"start": v(55.89, -25.17) * mm, "end": v(56.07, -25.18) * mm});
            skLineSegment(sketch, "E2828", {"start": v(56.07, -25.18) * mm, "end": v(56.26, -25.2) * mm});
            skLineSegment(sketch, "E2829", {"start": v(56.26, -25.2) * mm, "end": v(56.46, -25.2) * mm});
            skLineSegment(sketch, "E2830", {"start": v(56.46, -25.2) * mm, "end": v(56.66, -25.21) * mm});
            skLineSegment(sketch, "E2831", {"start": v(56.66, -25.21) * mm, "end": v(56.86, -25.22) * mm});
            skLineSegment(sketch, "E2832", {"start": v(56.86, -25.22) * mm, "end": v(57.07, -25.22) * mm});
            skLineSegment(sketch, "E2833", {"start": v(57.07, -25.22) * mm, "end": v(57.28, -25.23) * mm});
            skLineSegment(sketch, "E2834", {"start": v(57.28, -25.23) * mm, "end": v(57.5, -25.23) * mm});
            skLineSegment(sketch, "E2835", {"start": v(57.5, -25.23) * mm, "end": v(57.72, -25.23) * mm});
            skLineSegment(sketch, "E2836", {"start": v(57.72, -25.23) * mm, "end": v(57.95, -25.23) * mm});
            skLineSegment(sketch, "E2837", {"start": v(57.95, -25.23) * mm, "end": v(58.18, -25.22) * mm});
            skLineSegment(sketch, "E2838", {"start": v(58.18, -25.22) * mm, "end": v(58.41, -25.22) * mm});
            skLineSegment(sketch, "E2839", {"start": v(58.41, -25.22) * mm, "end": v(58.65, -25.2) * mm});
            skLineSegment(sketch, "E2840", {"start": v(58.65, -25.2) * mm, "end": v(58.9, -25.2) * mm});
            skLineSegment(sketch, "E2841", {"start": v(58.9, -25.2) * mm, "end": v(59.14, -25.18) * mm});
            skLineSegment(sketch, "E2842", {"start": v(59.14, -25.18) * mm, "end": v(59.4, -25.17) * mm});
            skLineSegment(sketch, "E2843", {"start": v(59.4, -25.17) * mm, "end": v(59.65, -25.15) * mm});
            skLineSegment(sketch, "E2844", {"start": v(59.65, -25.15) * mm, "end": v(59.9, -25.13) * mm});
            skLineSegment(sketch, "E2845", {"start": v(59.9, -25.13) * mm, "end": v(60.17, -25.1) * mm});
            skLineSegment(sketch, "E2846", {"start": v(60.17, -25.1) * mm, "end": v(60.44, -25.08) * mm});
            skLineSegment(sketch, "E2847", {"start": v(60.44, -25.08) * mm, "end": v(60.71, -25.05) * mm});
            skLineSegment(sketch, "E2848", {"start": v(60.71, -25.05) * mm, "end": v(60.99, -25.01) * mm});
            skLineSegment(sketch, "E2849", {"start": v(60.99, -25.01) * mm, "end": v(61.13, -25) * mm});
            skLineSegment(sketch, "E2850", {"start": v(61.13, -25) * mm, "end": v(61.67, -23.62) * mm});
            skLineSegment(sketch, "E2851", {"start": v(61.67, -23.62) * mm, "end": v(61.58, -23.51) * mm});
            skLineSegment(sketch, "E2852", {"start": v(61.58, -23.51) * mm, "end": v(61.4, -23.3) * mm});
            skLineSegment(sketch, "E2853", {"start": v(61.4, -23.3) * mm, "end": v(61.22, -23.1) * mm});
            skLineSegment(sketch, "E2854", {"start": v(61.22, -23.1) * mm, "end": v(61.05, -22.9) * mm});
            skLineSegment(sketch, "E2855", {"start": v(61.05, -22.9) * mm, "end": v(60.87, -22.7) * mm});
            skLineSegment(sketch, "E2856", {"start": v(60.87, -22.7) * mm, "end": v(60.7, -22.5) * mm});
            skLineSegment(sketch, "E2857", {"start": v(60.7, -22.5) * mm, "end": v(60.52, -22.31) * mm});
            skLineSegment(sketch, "E2858", {"start": v(60.52, -22.31) * mm, "end": v(60.35, -22.13) * mm});
            skLineSegment(sketch, "E2859", {"start": v(60.35, -22.13) * mm, "end": v(60.18, -21.95) * mm});
            skLineSegment(sketch, "E2860", {"start": v(60.18, -21.95) * mm, "end": v(60, -21.77) * mm});
            skLineSegment(sketch, "E2861", {"start": v(60, -21.77) * mm, "end": v(59.84, -21.6) * mm});
            skLineSegment(sketch, "E2862", {"start": v(59.84, -21.6) * mm, "end": v(59.67, -21.44) * mm});
            skLineSegment(sketch, "E2863", {"start": v(59.67, -21.44) * mm, "end": v(59.5, -21.28) * mm});
            skLineSegment(sketch, "E2864", {"start": v(59.5, -21.28) * mm, "end": v(59.35, -21.12) * mm});
            skLineSegment(sketch, "E2865", {"start": v(59.35, -21.12) * mm, "end": v(59.19, -20.97) * mm});
            skLineSegment(sketch, "E2866", {"start": v(59.19, -20.97) * mm, "end": v(59.03, -20.82) * mm});
            skLineSegment(sketch, "E2867", {"start": v(59.03, -20.82) * mm, "end": v(58.87, -20.68) * mm});
            skLineSegment(sketch, "E2868", {"start": v(58.87, -20.68) * mm, "end": v(58.71, -20.54) * mm});
            skLineSegment(sketch, "E2869", {"start": v(58.71, -20.54) * mm, "end": v(58.56, -20.4) * mm});
            skLineSegment(sketch, "E2870", {"start": v(58.56, -20.4) * mm, "end": v(58.41, -20.27) * mm});
            skLineSegment(sketch, "E2871", {"start": v(58.41, -20.27) * mm, "end": v(58.26, -20.15) * mm});
            skLineSegment(sketch, "E2872", {"start": v(58.26, -20.15) * mm, "end": v(58.12, -20.03) * mm});
            skLineSegment(sketch, "E2873", {"start": v(58.12, -20.03) * mm, "end": v(57.97, -19.9) * mm});
            skLineSegment(sketch, "E2874", {"start": v(57.97, -19.9) * mm, "end": v(57.83, -19.8) * mm});
            skLineSegment(sketch, "E2875", {"start": v(57.83, -19.8) * mm, "end": v(57.7, -19.68) * mm});
            skLineSegment(sketch, "E2876", {"start": v(57.7, -19.68) * mm, "end": v(57.55, -19.58) * mm});
            skLineSegment(sketch, "E2877", {"start": v(57.55, -19.58) * mm, "end": v(57.42, -19.48) * mm});
            skLineSegment(sketch, "E2878", {"start": v(57.42, -19.48) * mm, "end": v(57.29, -19.38) * mm});
            skLineSegment(sketch, "E2879", {"start": v(57.29, -19.38) * mm, "end": v(57.16, -19.28) * mm});
            skArc(sketch, "E2880", {"start": v(57.16, -19.28) * mm, "mid": v(57.37, -18.64) * mm, "end": v(57.58, -18) * mm});
            skLineSegment(sketch, "E2881", {"start": v(57.58, -18) * mm, "end": v(57.74, -18) * mm});
            skLineSegment(sketch, "E2882", {"start": v(57.74, -18) * mm, "end": v(57.9, -18) * mm});
            skLineSegment(sketch, "E2883", {"start": v(57.9, -18) * mm, "end": v(58.07, -18) * mm});
            skLineSegment(sketch, "E2884", {"start": v(58.07, -18) * mm, "end": v(58.24, -17.98) * mm});
            skLineSegment(sketch, "E2885", {"start": v(58.24, -17.98) * mm, "end": v(58.42, -17.98) * mm});
            skLineSegment(sketch, "E2886", {"start": v(58.42, -17.98) * mm, "end": v(58.6, -17.97) * mm});
            skLineSegment(sketch, "E2887", {"start": v(58.6, -17.97) * mm, "end": v(58.79, -17.96) * mm});
            skLineSegment(sketch, "E2888", {"start": v(58.79, -17.96) * mm, "end": v(58.98, -17.94) * mm});
            skLineSegment(sketch, "E2889", {"start": v(58.98, -17.94) * mm, "end": v(59.17, -17.93) * mm});
            skLineSegment(sketch, "E2890", {"start": v(59.17, -17.93) * mm, "end": v(59.37, -17.91) * mm});
            skLineSegment(sketch, "E2891", {"start": v(59.37, -17.91) * mm, "end": v(59.57, -17.9) * mm});
            skLineSegment(sketch, "E2892", {"start": v(59.57, -17.9) * mm, "end": v(59.78, -17.87) * mm});
            skLineSegment(sketch, "E2893", {"start": v(59.78, -17.87) * mm, "end": v(60, -17.85) * mm});
            skLineSegment(sketch, "E2894", {"start": v(60, -17.85) * mm, "end": v(60.2, -17.82) * mm});
            skLineSegment(sketch, "E2895", {"start": v(60.2, -17.82) * mm, "end": v(60.43, -17.8) * mm});
            skLineSegment(sketch, "E2896", {"start": v(60.43, -17.8) * mm, "end": v(60.65, -17.76) * mm});
            skLineSegment(sketch, "E2897", {"start": v(60.65, -17.76) * mm, "end": v(60.88, -17.73) * mm});
            skLineSegment(sketch, "E2898", {"start": v(60.88, -17.73) * mm, "end": v(61.1, -17.7) * mm});
            skLineSegment(sketch, "E2899", {"start": v(61.1, -17.7) * mm, "end": v(61.35, -17.66) * mm});
            skLineSegment(sketch, "E2900", {"start": v(61.35, -17.66) * mm, "end": v(61.59, -17.62) * mm});
            skLineSegment(sketch, "E2901", {"start": v(61.59, -17.62) * mm, "end": v(61.83, -17.57) * mm});
            skLineSegment(sketch, "E2902", {"start": v(61.83, -17.57) * mm, "end": v(62.08, -17.52) * mm});
            skLineSegment(sketch, "E2903", {"start": v(62.08, -17.52) * mm, "end": v(62.33, -17.47) * mm});
            skLineSegment(sketch, "E2904", {"start": v(62.33, -17.47) * mm, "end": v(62.58, -17.42) * mm});
            skLineSegment(sketch, "E2905", {"start": v(62.58, -17.42) * mm, "end": v(62.84, -17.36) * mm});
            skLineSegment(sketch, "E2906", {"start": v(62.84, -17.36) * mm, "end": v(63.1, -17.3) * mm});
            skLineSegment(sketch, "E2907", {"start": v(63.1, -17.3) * mm, "end": v(63.37, -17.24) * mm});
            skLineSegment(sketch, "E2908", {"start": v(63.37, -17.24) * mm, "end": v(63.64, -17.17) * mm});
            skLineSegment(sketch, "E2909", {"start": v(63.64, -17.17) * mm, "end": v(63.78, -17.14) * mm});
            skLineSegment(sketch, "E2910", {"start": v(63.78, -17.14) * mm, "end": v(64.14, -15.7) * mm});
            skLineSegment(sketch, "E2911", {"start": v(64.14, -15.7) * mm, "end": v(64.04, -15.61) * mm});
            skLineSegment(sketch, "E2912", {"start": v(64.04, -15.61) * mm, "end": v(63.84, -15.42) * mm});
            skLineSegment(sketch, "E2913", {"start": v(63.84, -15.42) * mm, "end": v(63.63, -15.24) * mm});
            skLineSegment(sketch, "E2914", {"start": v(63.63, -15.24) * mm, "end": v(63.43, -15.06) * mm});
            skLineSegment(sketch, "E2915", {"start": v(63.43, -15.06) * mm, "end": v(63.23, -14.88) * mm});
            skLineSegment(sketch, "E2916", {"start": v(63.23, -14.88) * mm, "end": v(63.04, -14.71) * mm});
            skLineSegment(sketch, "E2917", {"start": v(63.04, -14.71) * mm, "end": v(62.84, -14.55) * mm});
            skLineSegment(sketch, "E2918", {"start": v(62.84, -14.55) * mm, "end": v(62.65, -14.39) * mm});
            skLineSegment(sketch, "E2919", {"start": v(62.65, -14.39) * mm, "end": v(62.45, -14.23) * mm});
            skLineSegment(sketch, "E2920", {"start": v(62.45, -14.23) * mm, "end": v(62.26, -14.08) * mm});
            skLineSegment(sketch, "E2921", {"start": v(62.26, -14.08) * mm, "end": v(62.08, -13.93) * mm});
            skLineSegment(sketch, "E2922", {"start": v(62.08, -13.93) * mm, "end": v(61.9, -13.8) * mm});
            skLineSegment(sketch, "E2923", {"start": v(61.9, -13.8) * mm, "end": v(61.7, -13.65) * mm});
            skLineSegment(sketch, "E2924", {"start": v(61.7, -13.65) * mm, "end": v(61.53, -13.52) * mm});
            skLineSegment(sketch, "E2925", {"start": v(61.53, -13.52) * mm, "end": v(61.35, -13.39) * mm});
            skLineSegment(sketch, "E2926", {"start": v(61.35, -13.39) * mm, "end": v(61.17, -13.26) * mm});
            skLineSegment(sketch, "E2927", {"start": v(61.17, -13.26) * mm, "end": v(61, -13.14) * mm});
            skLineSegment(sketch, "E2928", {"start": v(61, -13.14) * mm, "end": v(60.83, -13.02) * mm});
            skLineSegment(sketch, "E2929", {"start": v(60.83, -13.02) * mm, "end": v(60.66, -12.9) * mm});
            skLineSegment(sketch, "E2930", {"start": v(60.66, -12.9) * mm, "end": v(60.5, -12.8) * mm});
            skLineSegment(sketch, "E2931", {"start": v(60.5, -12.8) * mm, "end": v(60.33, -12.69) * mm});
            skLineSegment(sketch, "E2932", {"start": v(60.33, -12.69) * mm, "end": v(60.17, -12.58) * mm});
            skLineSegment(sketch, "E2933", {"start": v(60.17, -12.58) * mm, "end": v(60, -12.49) * mm});
            skLineSegment(sketch, "E2934", {"start": v(60, -12.49) * mm, "end": v(59.85, -12.4) * mm});
            skLineSegment(sketch, "E2935", {"start": v(59.85, -12.4) * mm, "end": v(59.7, -12.3) * mm});
            skLineSegment(sketch, "E2936", {"start": v(59.7, -12.3) * mm, "end": v(59.55, -12.21) * mm});
            skLineSegment(sketch, "E2937", {"start": v(59.55, -12.21) * mm, "end": v(59.4, -12.13) * mm});
            skLineSegment(sketch, "E2938", {"start": v(59.4, -12.13) * mm, "end": v(59.26, -12.04) * mm});
            skLineSegment(sketch, "E2939", {"start": v(59.26, -12.04) * mm, "end": v(59.13, -11.97) * mm});
            skArc(sketch, "E2940", {"start": v(59.13, -11.97) * mm, "mid": v(59.25, -11.3) * mm, "end": v(59.38, -10.64) * mm});
            skLineSegment(sketch, "E2941", {"start": v(59.38, -10.64) * mm, "end": v(59.54, -10.62) * mm});
            skLineSegment(sketch, "E2942", {"start": v(59.54, -10.62) * mm, "end": v(59.7, -10.6) * mm});
            skLineSegment(sketch, "E2943", {"start": v(59.7, -10.6) * mm, "end": v(59.87, -10.57) * mm});
            skLineSegment(sketch, "E2944", {"start": v(59.87, -10.57) * mm, "end": v(60.04, -10.54) * mm});
            skLineSegment(sketch, "E2945", {"start": v(60.04, -10.54) * mm, "end": v(60.21, -10.51) * mm});
            skLineSegment(sketch, "E2946", {"start": v(60.21, -10.51) * mm, "end": v(60.4, -10.48) * mm});
            skLineSegment(sketch, "E2947", {"start": v(60.4, -10.48) * mm, "end": v(60.57, -10.45) * mm});
            skLineSegment(sketch, "E2948", {"start": v(60.57, -10.45) * mm, "end": v(60.76, -10.41) * mm});
            skLineSegment(sketch, "E2949", {"start": v(60.76, -10.41) * mm, "end": v(60.95, -10.37) * mm});
            skLineSegment(sketch, "E2950", {"start": v(60.95, -10.37) * mm, "end": v(61.15, -10.33) * mm});
            skLineSegment(sketch, "E2951", {"start": v(61.15, -10.33) * mm, "end": v(61.35, -10.29) * mm});
            skLineSegment(sketch, "E2952", {"start": v(61.35, -10.29) * mm, "end": v(61.55, -10.24) * mm});
            skLineSegment(sketch, "E2953", {"start": v(61.55, -10.24) * mm, "end": v(61.76, -10.19) * mm});
            skLineSegment(sketch, "E2954", {"start": v(61.76, -10.19) * mm, "end": v(61.97, -10.14) * mm});
            skLineSegment(sketch, "E2955", {"start": v(61.97, -10.14) * mm, "end": v(62.18, -10.08) * mm});
            skLineSegment(sketch, "E2956", {"start": v(62.18, -10.08) * mm, "end": v(62.4, -10.02) * mm});
            skLineSegment(sketch, "E2957", {"start": v(62.4, -10.02) * mm, "end": v(62.62, -9.96) * mm});
            skLineSegment(sketch, "E2958", {"start": v(62.62, -9.96) * mm, "end": v(62.85, -9.9) * mm});
            skLineSegment(sketch, "E2959", {"start": v(62.85, -9.9) * mm, "end": v(63.07, -9.83) * mm});
            skLineSegment(sketch, "E2960", {"start": v(63.07, -9.83) * mm, "end": v(63.3, -9.76) * mm});
            skLineSegment(sketch, "E2961", {"start": v(63.3, -9.76) * mm, "end": v(63.54, -9.68) * mm});
            skLineSegment(sketch, "E2962", {"start": v(63.54, -9.68) * mm, "end": v(63.78, -9.6) * mm});
            skLineSegment(sketch, "E2963", {"start": v(63.78, -9.6) * mm, "end": v(64.03, -9.52) * mm});
            skLineSegment(sketch, "E2964", {"start": v(64.03, -9.52) * mm, "end": v(64.27, -9.44) * mm});
            skLineSegment(sketch, "E2965", {"start": v(64.27, -9.44) * mm, "end": v(64.52, -9.35) * mm});
            skLineSegment(sketch, "E2966", {"start": v(64.52, -9.35) * mm, "end": v(64.78, -9.26) * mm});
            skLineSegment(sketch, "E2967", {"start": v(64.78, -9.26) * mm, "end": v(65.03, -9.16) * mm});
            skLineSegment(sketch, "E2968", {"start": v(65.03, -9.16) * mm, "end": v(65.3, -9.06) * mm});
            skLineSegment(sketch, "E2969", {"start": v(65.3, -9.06) * mm, "end": v(65.42, -9.01) * mm});
            skLineSegment(sketch, "E2970", {"start": v(65.42, -9.01) * mm, "end": v(65.6, -7.54) * mm});
            skLineSegment(sketch, "E2971", {"start": v(65.6, -7.54) * mm, "end": v(65.5, -7.46) * mm});
            skLineSegment(sketch, "E2972", {"start": v(65.5, -7.46) * mm, "end": v(65.27, -7.3) * mm});
            skLineSegment(sketch, "E2973", {"start": v(65.27, -7.3) * mm, "end": v(65.04, -7.14) * mm});
            skLineSegment(sketch, "E2974", {"start": v(65.04, -7.14) * mm, "end": v(64.82, -7) * mm});
            skLineSegment(sketch, "E2975", {"start": v(64.82, -7) * mm, "end": v(64.6, -6.84) * mm});
            skLineSegment(sketch, "E2976", {"start": v(64.6, -6.84) * mm, "end": v(64.38, -6.7) * mm});
            skLineSegment(sketch, "E2977", {"start": v(64.38, -6.7) * mm, "end": v(64.17, -6.56) * mm});
            skLineSegment(sketch, "E2978", {"start": v(64.17, -6.56) * mm, "end": v(63.96, -6.42) * mm});
            skLineSegment(sketch, "E2979", {"start": v(63.96, -6.42) * mm, "end": v(63.75, -6.3) * mm});
            skLineSegment(sketch, "E2980", {"start": v(63.75, -6.3) * mm, "end": v(63.54, -6.17) * mm});
            skLineSegment(sketch, "E2981", {"start": v(63.54, -6.17) * mm, "end": v(63.33, -6.04) * mm});
            skLineSegment(sketch, "E2982", {"start": v(63.33, -6.04) * mm, "end": v(63.13, -5.92) * mm});
            skLineSegment(sketch, "E2983", {"start": v(63.13, -5.92) * mm, "end": v(62.93, -5.8) * mm});
            skLineSegment(sketch, "E2984", {"start": v(62.93, -5.8) * mm, "end": v(62.73, -5.7) * mm});
            skLineSegment(sketch, "E2985", {"start": v(62.73, -5.7) * mm, "end": v(62.54, -5.6) * mm});
            skLineSegment(sketch, "E2986", {"start": v(62.54, -5.6) * mm, "end": v(62.35, -5.49) * mm});
            skLineSegment(sketch, "E2987", {"start": v(62.35, -5.49) * mm, "end": v(62.16, -5.39) * mm});
            skLineSegment(sketch, "E2988", {"start": v(62.16, -5.39) * mm, "end": v(61.98, -5.3) * mm});
            skLineSegment(sketch, "E2989", {"start": v(61.98, -5.3) * mm, "end": v(61.8, -5.2) * mm});
            skLineSegment(sketch, "E2990", {"start": v(61.8, -5.2) * mm, "end": v(61.62, -5.11) * mm});
            skLineSegment(sketch, "E2991", {"start": v(61.62, -5.11) * mm, "end": v(61.44, -5.03) * mm});
            skLineSegment(sketch, "E2992", {"start": v(61.44, -5.03) * mm, "end": v(61.27, -4.94) * mm});
            skLineSegment(sketch, "E2993", {"start": v(61.27, -4.94) * mm, "end": v(61.1, -4.87) * mm});
            skLineSegment(sketch, "E2994", {"start": v(61.1, -4.87) * mm, "end": v(60.94, -4.8) * mm});
            skLineSegment(sketch, "E2995", {"start": v(60.94, -4.8) * mm, "end": v(60.77, -4.72) * mm});
            skLineSegment(sketch, "E2996", {"start": v(60.77, -4.72) * mm, "end": v(60.61, -4.65) * mm});
            skLineSegment(sketch, "E2997", {"start": v(60.61, -4.65) * mm, "end": v(60.46, -4.58) * mm});
            skLineSegment(sketch, "E2998", {"start": v(60.46, -4.58) * mm, "end": v(60.3, -4.52) * mm});
            skLineSegment(sketch, "E2999", {"start": v(60.3, -4.52) * mm, "end": v(60.16, -4.46) * mm});
            skArc(sketch, "E3000", {"start": v(60.16, -4.46) * mm, "mid": v(60.2, -3.79) * mm, "end": v(60.24, -3.11) * mm});
            skSolve(sketch);
        }
        {
            var Q0;
            Q0=makeQuery(id+"F2.imprint","IMPRINT",FACE,{"disambiguationData":[TD([[makeQuery(id+"F2.imprint","IMPRINT",EDGE,{"derivedFrom":sQuery(id+"F2.wireOp",EDGE,"E1")}),1.0]])]});
            extrude(context, id + "F3", {"entities" : qUnion([Q0]), "operationType" : NewBodyOperationType.REMOVE, "depth" : 20 * mm});
        }
        {
            var Q0;
            Q0=qCreatedBy(makeId("Front.planeOp"),FACE);
            var sketch = newSketch(context, id + "F4", { "sketchPlane" : qUnion([Q0])});
            skCircle(sketch, "E3001", {"center": v(0, 0) * mm, "radius": 75 * mm});
            skSolve(sketch);
        }
        {
            var Q0;
            Q0=makeQuery(id+"F4.imprint","IMPRINT",FACE,{"disambiguationData":[TD([[makeQuery(id+"F4.imprint","IMPRINT",EDGE,{"derivedFrom":sQuery(id+"F4.wireOp",EDGE,"E3001")}),1.0]])]});
            extrude(context, id + "F5", {"entities" : qUnion([Q0]), "operationType" : NewBodyOperationType.ADD, "oppositeDirection" : true, "depth" : 5 * mm});
        }
        {
            var Q0;
            Q0=makeQuery(id+"F5.opExtrude","CAP_FACE",FACE,{"disambiguationData":[OSD([sQuery(id+"F4.wireOp",EDGE,"E3001")])],"isStart":false});
            var sketch = newSketch(context, id + "F6", { "sketchPlane" : qUnion([Q0])});
            skCircle(sketch, "E3002", {"center": v(0, 0) * mm, "radius": 5 * mm});
            skSolve(sketch);
        }
        {
            var Q0;
            Q0 = qSketchRegion(id + "F6", true);
            extrude(context, id + "F7", {"entities" : qUnion([Q0]), "operationType" : NewBodyOperationType.REMOVE, "endBound" : BoundingType.THROUGH_ALL, "oppositeDirection" : true, "depth" : 25 * mm});
        }
        {
            var Q0;
            Q0=qCreatedBy(makeId("Front.planeOp"),FACE);
            var sketch = newSketch(context, id + "F8", { "sketchPlane" : qUnion([Q0])});
            skCircle(sketch, "E3003", {"center": v(104.89, -78.52) * mm, "radius": 5 * mm});
            skSolve(sketch);
        }
        {
            var Q0;
            Q0 = qSketchRegion(id + "F8", true);
            extrude(context, id + "F9", {"entities" : qUnion([Q0]), "depth" : 50 * mm});
        }
    });
